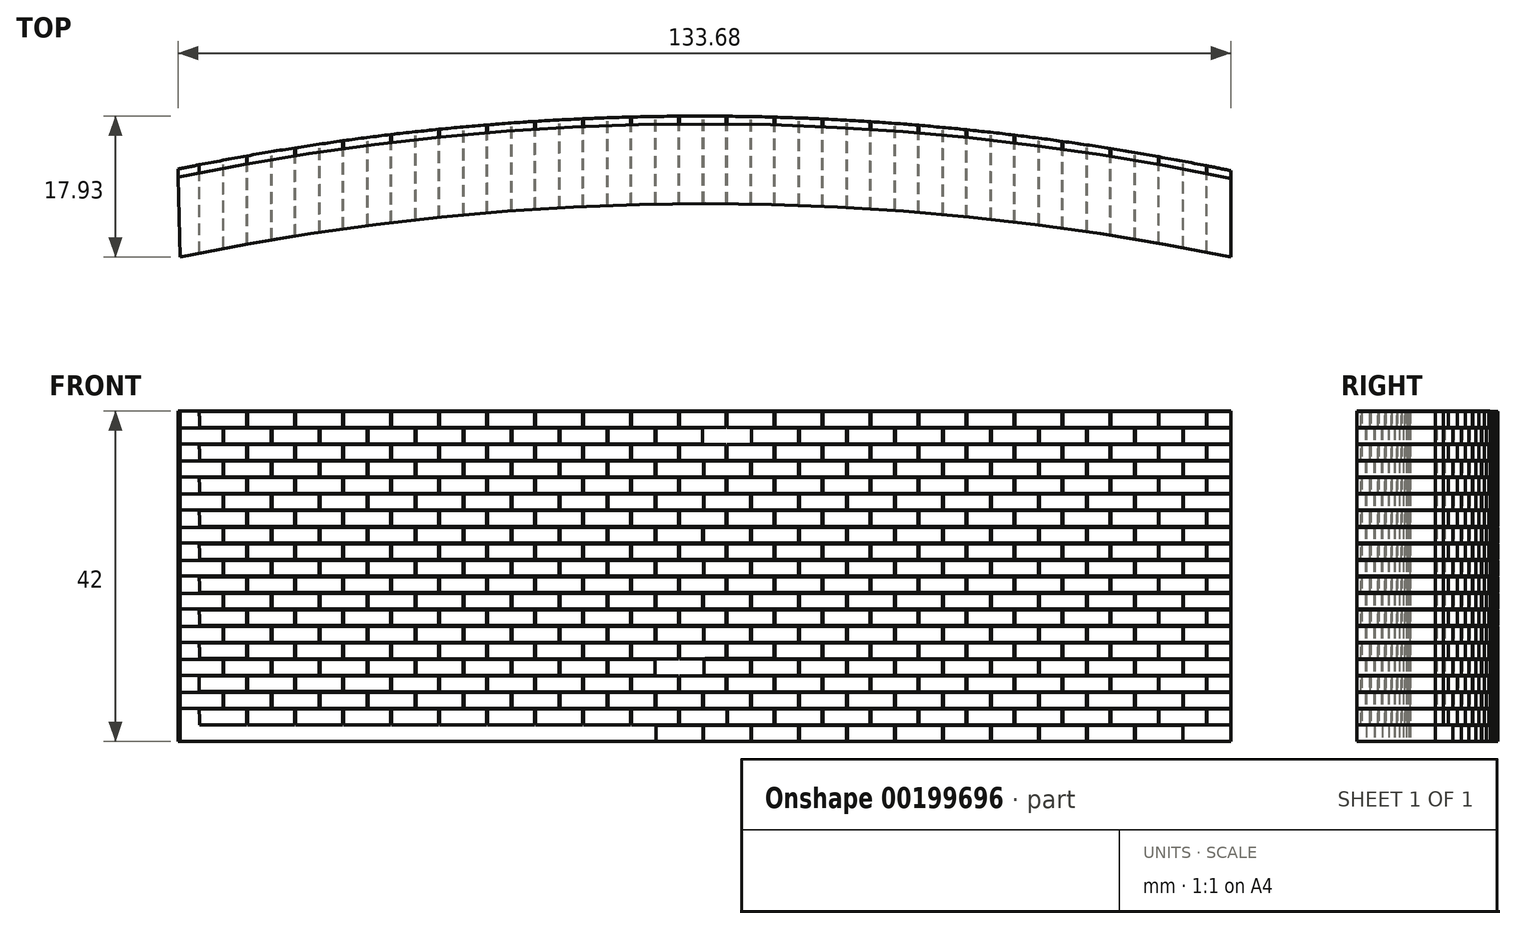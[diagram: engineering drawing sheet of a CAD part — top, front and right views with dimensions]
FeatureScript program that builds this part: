
annotation { "Feature Type Name" : "Feature", "Feature Type Description" : "" }
export const myFeature = defineFeature(function(context is Context, id is Id, definition is map)
    precondition{}
    {
        {
            var Q0;
            Q0=qCreatedBy(makeId("Front.planeOp"),FACE);
            var sketch = newSketch(context, id + "F0", { "sketchPlane" : qUnion([Q0])});
            skLineSegment(sketch, "E0", {"start": v(70.88, 0) * mm, "end": v(70.88, 50) * mm});
            skLineSegment(sketch, "E1", {"start": v(70.88, 0) * mm, "end": v(-68.5, 0) * mm});
            skLineSegment(sketch, "E2", {"start": v(-68.5, 0) * mm, "end": v(-68.5, 50) * mm});
            skLineSegment(sketch, "E3", {"start": v(70.88, 50) * mm, "end": v(-68.5, 50) * mm});
            skLineSegment(sketch, "E4", {"start": v(70.88, 0) * mm, "end": v(70.88, 2) * mm});
            skLineSegment(sketch, "E5", {"start": v(70.88, 2) * mm, "end": v(64.88, 2) * mm});
            skLineSegment(sketch, "E6", {"start": v(64.88, 2) * mm, "end": v(64.88, 0) * mm});
            skLineSegment(sketch, "E7", {"start": v(64.88, 0) * mm, "end": v(70.88, 0) * mm});
            skLineSegment(sketch, "E8", {"start": v(64.88, 0) * mm, "end": v(64.78, 0) * mm});
            skLineSegment(sketch, "E9", {"start": v(64.78, 0) * mm, "end": v(64.78, 2) * mm});
            skLineSegment(sketch, "E10", {"start": v(64.78, 2) * mm, "end": v(58.78, 2) * mm});
            skLineSegment(sketch, "E11", {"start": v(58.78, 2) * mm, "end": v(58.78, 0) * mm});
            skLineSegment(sketch, "E12", {"start": v(58.78, 0) * mm, "end": v(64.78, 0) * mm});
            skLineSegment(sketch, "E13.1.0.0", {"start": v(58.68, 2) * mm, "end": v(52.68, 2) * mm});
            skLineSegment(sketch, "E13.1.0.1", {"start": v(52.68, 2) * mm, "end": v(52.68, 0) * mm});
            skLineSegment(sketch, "E13.1.0.2", {"start": v(52.68, 0) * mm, "end": v(58.68, 0) * mm});
            skLineSegment(sketch, "E13.1.0.3", {"start": v(58.68, 0) * mm, "end": v(58.68, 2) * mm});
            skLineSegment(sketch, "E13.2.0.0", {"start": v(52.58, 2) * mm, "end": v(46.58, 2) * mm});
            skLineSegment(sketch, "E13.2.0.1", {"start": v(46.58, 2) * mm, "end": v(46.58, 0) * mm});
            skLineSegment(sketch, "E13.2.0.2", {"start": v(46.58, 0) * mm, "end": v(52.58, 0) * mm});
            skLineSegment(sketch, "E13.2.0.3", {"start": v(52.58, 0) * mm, "end": v(52.58, 2) * mm});
            skLineSegment(sketch, "E13.3.0.0", {"start": v(46.48, 2) * mm, "end": v(40.48, 2) * mm});
            skLineSegment(sketch, "E13.3.0.1", {"start": v(40.48, 2) * mm, "end": v(40.48, 0) * mm});
            skLineSegment(sketch, "E13.3.0.2", {"start": v(40.48, 0) * mm, "end": v(46.48, 0) * mm});
            skLineSegment(sketch, "E13.3.0.3", {"start": v(46.48, 0) * mm, "end": v(46.48, 2) * mm});
            skLineSegment(sketch, "E13.4.0.0", {"start": v(40.38, 2) * mm, "end": v(34.38, 2) * mm});
            skLineSegment(sketch, "E13.4.0.1", {"start": v(34.38, 2) * mm, "end": v(34.38, 0) * mm});
            skLineSegment(sketch, "E13.4.0.2", {"start": v(34.38, 0) * mm, "end": v(40.38, 0) * mm});
            skLineSegment(sketch, "E13.4.0.3", {"start": v(40.38, 0) * mm, "end": v(40.38, 2) * mm});
            skLineSegment(sketch, "E13.5.0.0", {"start": v(34.28, 2) * mm, "end": v(28.28, 2) * mm});
            skLineSegment(sketch, "E13.5.0.1", {"start": v(28.28, 2) * mm, "end": v(28.28, 0) * mm});
            skLineSegment(sketch, "E13.5.0.2", {"start": v(28.28, 0) * mm, "end": v(34.28, 0) * mm});
            skLineSegment(sketch, "E13.5.0.3", {"start": v(34.28, 0) * mm, "end": v(34.28, 2) * mm});
            skLineSegment(sketch, "E13.6.0.0", {"start": v(28.18, 2) * mm, "end": v(22.18, 2) * mm});
            skLineSegment(sketch, "E13.6.0.1", {"start": v(22.18, 2) * mm, "end": v(22.18, 0) * mm});
            skLineSegment(sketch, "E13.6.0.2", {"start": v(22.18, 0) * mm, "end": v(28.18, 0) * mm});
            skLineSegment(sketch, "E13.6.0.3", {"start": v(28.18, 0) * mm, "end": v(28.18, 2) * mm});
            skLineSegment(sketch, "E13.7.0.0", {"start": v(22.08, 2) * mm, "end": v(16.08, 2) * mm});
            skLineSegment(sketch, "E13.7.0.1", {"start": v(16.08, 2) * mm, "end": v(16.08, 0) * mm});
            skLineSegment(sketch, "E13.7.0.2", {"start": v(16.08, 0) * mm, "end": v(22.08, 0) * mm});
            skLineSegment(sketch, "E13.7.0.3", {"start": v(22.08, 0) * mm, "end": v(22.08, 2) * mm});
            skLineSegment(sketch, "E13.8.0.0", {"start": v(15.98, 2) * mm, "end": v(9.98, 2) * mm});
            skLineSegment(sketch, "E13.8.0.1", {"start": v(9.98, 2) * mm, "end": v(9.98, 0) * mm});
            skLineSegment(sketch, "E13.8.0.2", {"start": v(9.98, 0) * mm, "end": v(15.98, 0) * mm});
            skLineSegment(sketch, "E13.8.0.3", {"start": v(15.98, 0) * mm, "end": v(15.98, 2) * mm});
            skLineSegment(sketch, "E13.9.0.3", {"start": v(9.93, 0) * mm, "end": v(9.93, 2) * mm});
            skLineSegment(sketch, "E14", {"start": v(70.88, 2.1) * mm, "end": v(67.86, 2.1) * mm});
            skLineSegment(sketch, "E15", {"start": v(67.86, 2.1) * mm, "end": v(67.86, 4.1) * mm});
            skLineSegment(sketch, "E16", {"start": v(67.86, 4.1) * mm, "end": v(70.88, 4.1) * mm});
            skLineSegment(sketch, "E17", {"start": v(70.88, 4.1) * mm, "end": v(70.88, 2.1) * mm});
            skLineSegment(sketch, "E18", {"start": v(67.86, 2.1) * mm, "end": v(67.76, 2.1) * mm});
            skLineSegment(sketch, "E19", {"start": v(67.76, 2.1) * mm, "end": v(67.76, 4.1) * mm});
            skLineSegment(sketch, "E20", {"start": v(67.76, 4.1) * mm, "end": v(61.76, 4.1) * mm});
            skLineSegment(sketch, "E21", {"start": v(61.76, 4.1) * mm, "end": v(61.78, 2.1) * mm});
            skPoint(sketch, "E21.endSnap0", {"position": v(61.78, 2) * mm});
            skLineSegment(sketch, "E22", {"start": v(67.76, 2.1) * mm, "end": v(61.78, 2.1) * mm});
            skLineSegment(sketch, "E23.1.0.0", {"start": v(61.66, 4.1) * mm, "end": v(55.66, 4.1) * mm});
            skLineSegment(sketch, "E23.1.0.1", {"start": v(55.66, 4.1) * mm, "end": v(55.68, 2.1) * mm});
            skLineSegment(sketch, "E23.1.0.2", {"start": v(61.66, 2.1) * mm, "end": v(55.68, 2.1) * mm});
            skLineSegment(sketch, "E23.1.0.3", {"start": v(61.66, 2.1) * mm, "end": v(61.66, 4.1) * mm});
            skLineSegment(sketch, "E23.2.0.0", {"start": v(55.56, 4.1) * mm, "end": v(49.56, 4.1) * mm});
            skLineSegment(sketch, "E23.2.0.1", {"start": v(49.56, 4.1) * mm, "end": v(49.58, 2.1) * mm});
            skLineSegment(sketch, "E23.2.0.2", {"start": v(55.56, 2.1) * mm, "end": v(49.58, 2.1) * mm});
            skLineSegment(sketch, "E23.2.0.3", {"start": v(55.56, 2.1) * mm, "end": v(55.56, 4.1) * mm});
            skLineSegment(sketch, "E23.3.0.0", {"start": v(49.46, 4.1) * mm, "end": v(43.46, 4.1) * mm});
            skLineSegment(sketch, "E23.3.0.1", {"start": v(43.46, 4.1) * mm, "end": v(43.48, 2.1) * mm});
            skLineSegment(sketch, "E23.3.0.2", {"start": v(49.46, 2.1) * mm, "end": v(43.48, 2.1) * mm});
            skLineSegment(sketch, "E23.3.0.3", {"start": v(49.46, 2.1) * mm, "end": v(49.46, 4.1) * mm});
            skLineSegment(sketch, "E23.4.0.0", {"start": v(43.36, 4.1) * mm, "end": v(37.36, 4.1) * mm});
            skLineSegment(sketch, "E23.4.0.1", {"start": v(37.36, 4.1) * mm, "end": v(37.38, 2.1) * mm});
            skLineSegment(sketch, "E23.4.0.2", {"start": v(43.36, 2.1) * mm, "end": v(37.38, 2.1) * mm});
            skLineSegment(sketch, "E23.4.0.3", {"start": v(43.36, 2.1) * mm, "end": v(43.36, 4.1) * mm});
            skLineSegment(sketch, "E23.5.0.0", {"start": v(37.26, 4.1) * mm, "end": v(31.26, 4.1) * mm});
            skLineSegment(sketch, "E23.5.0.1", {"start": v(31.26, 4.1) * mm, "end": v(31.28, 2.1) * mm});
            skLineSegment(sketch, "E23.5.0.2", {"start": v(37.26, 2.1) * mm, "end": v(31.28, 2.1) * mm});
            skLineSegment(sketch, "E23.5.0.3", {"start": v(37.26, 2.1) * mm, "end": v(37.26, 4.1) * mm});
            skLineSegment(sketch, "E23.6.0.0", {"start": v(31.16, 4.1) * mm, "end": v(25.16, 4.1) * mm});
            skLineSegment(sketch, "E23.6.0.1", {"start": v(25.16, 4.1) * mm, "end": v(25.18, 2.1) * mm});
            skLineSegment(sketch, "E23.6.0.2", {"start": v(31.16, 2.1) * mm, "end": v(25.18, 2.1) * mm});
            skLineSegment(sketch, "E23.6.0.3", {"start": v(31.16, 2.1) * mm, "end": v(31.16, 4.1) * mm});
            skLineSegment(sketch, "E23.7.0.0", {"start": v(25.06, 4.1) * mm, "end": v(19.06, 4.1) * mm});
            skLineSegment(sketch, "E23.7.0.1", {"start": v(19.06, 4.1) * mm, "end": v(19.08, 2.1) * mm});
            skLineSegment(sketch, "E23.7.0.2", {"start": v(25.06, 2.1) * mm, "end": v(19.08, 2.1) * mm});
            skLineSegment(sketch, "E23.7.0.3", {"start": v(25.06, 2.1) * mm, "end": v(25.06, 4.1) * mm});
            skLineSegment(sketch, "E23.8.0.0", {"start": v(18.96, 4.1) * mm, "end": v(12.96, 4.1) * mm});
            skLineSegment(sketch, "E23.8.0.1", {"start": v(12.96, 4.1) * mm, "end": v(12.98, 2.1) * mm});
            skLineSegment(sketch, "E23.8.0.2", {"start": v(18.96, 2.1) * mm, "end": v(12.98, 2.1) * mm});
            skLineSegment(sketch, "E23.8.0.3", {"start": v(18.96, 2.1) * mm, "end": v(18.96, 4.1) * mm});
            skLineSegment(sketch, "E23.9.0.3", {"start": v(12.86, 2.1) * mm, "end": v(12.86, 4.1) * mm});
            skLineSegment(sketch, "E24", {"start": v(70.88, 4.1) * mm, "end": v(70.88, 4.2) * mm});
            skLineSegment(sketch, "E25.0.1.0", {"start": v(31.16, 8.3) * mm, "end": v(25.16, 8.3) * mm});
            skLineSegment(sketch, "E25.0.1.1", {"start": v(55.56, 8.3) * mm, "end": v(49.56, 8.3) * mm});
            skLineSegment(sketch, "E25.0.1.2", {"start": v(18.96, 8.3) * mm, "end": v(12.96, 8.3) * mm});
            skLineSegment(sketch, "E25.0.1.3", {"start": v(43.36, 8.3) * mm, "end": v(37.36, 8.3) * mm});
            skLineSegment(sketch, "E25.0.1.4", {"start": v(25.06, 8.3) * mm, "end": v(19.06, 8.3) * mm});
            skLineSegment(sketch, "E25.0.1.5", {"start": v(49.46, 8.3) * mm, "end": v(43.46, 8.3) * mm});
            skLineSegment(sketch, "E25.0.1.6", {"start": v(61.66, 8.3) * mm, "end": v(55.66, 8.3) * mm});
            skLineSegment(sketch, "E25.0.1.7", {"start": v(12.86, 8.3) * mm, "end": v(6.86, 8.3) * mm});
            skLineSegment(sketch, "E25.0.1.8", {"start": v(37.26, 8.3) * mm, "end": v(31.26, 8.3) * mm});
            skLineSegment(sketch, "E25.0.1.9", {"start": v(46.58, 4.2) * mm, "end": v(52.58, 4.2) * mm});
            skLineSegment(sketch, "E25.0.1.10", {"start": v(22.18, 4.2) * mm, "end": v(28.18, 4.2) * mm});
            skLineSegment(sketch, "E25.0.1.11", {"start": v(9.98, 4.2) * mm, "end": v(15.98, 4.2) * mm});
            skLineSegment(sketch, "E25.0.1.12", {"start": v(34.38, 4.2) * mm, "end": v(40.38, 4.2) * mm});
            skLineSegment(sketch, "E25.0.1.13", {"start": v(16.08, 4.2) * mm, "end": v(22.08, 4.2) * mm});
            skLineSegment(sketch, "E25.0.1.14", {"start": v(40.48, 4.2) * mm, "end": v(46.48, 4.2) * mm});
            skPoint(sketch, "E25.0.1.15", {"position": v(61.78, 6.2) * mm});
            skLineSegment(sketch, "E25.0.1.17", {"start": v(28.28, 4.2) * mm, "end": v(34.28, 4.2) * mm});
            skLineSegment(sketch, "E25.0.1.18", {"start": v(52.68, 4.2) * mm, "end": v(58.68, 4.2) * mm});
            skLineSegment(sketch, "E25.0.1.19", {"start": v(64.88, 4.2) * mm, "end": v(70.88, 4.2) * mm});
            skLineSegment(sketch, "E25.0.1.20", {"start": v(67.76, 8.3) * mm, "end": v(61.76, 8.3) * mm});
            skLineSegment(sketch, "E25.0.1.22", {"start": v(58.78, 4.2) * mm, "end": v(64.78, 4.2) * mm});
            skLineSegment(sketch, "E25.0.1.23", {"start": v(43.46, 8.3) * mm, "end": v(43.48, 6.3) * mm});
            skLineSegment(sketch, "E25.0.1.24", {"start": v(6.86, 8.3) * mm, "end": v(6.88, 6.3) * mm});
            skLineSegment(sketch, "E25.0.1.26", {"start": v(12.87, 6.3) * mm, "end": v(6.88, 6.3) * mm});
            skLineSegment(sketch, "E25.0.1.27", {"start": v(46.48, 6.2) * mm, "end": v(40.48, 6.2) * mm});
            skLineSegment(sketch, "E25.0.1.28", {"start": v(15.98, 6.2) * mm, "end": v(9.98, 6.2) * mm});
            skLineSegment(sketch, "E25.0.1.29", {"start": v(43.36, 6.3) * mm, "end": v(43.36, 8.3) * mm});
            skLineSegment(sketch, "E25.0.1.30", {"start": v(9.98, 6.2) * mm, "end": v(9.98, 4.2) * mm});
            skLineSegment(sketch, "E25.0.1.31", {"start": v(9.97, 4.2) * mm, "end": v(9.97, 6.18) * mm});
            skLineSegment(sketch, "E25.0.1.32", {"start": v(49.46, 6.3) * mm, "end": v(43.48, 6.3) * mm});
            skLineSegment(sketch, "E25.0.1.33", {"start": v(40.38, 4.2) * mm, "end": v(40.38, 6.2) * mm});
            skLineSegment(sketch, "E25.0.1.34", {"start": v(18.96, 6.3) * mm, "end": v(12.98, 6.3) * mm});
            skLineSegment(sketch, "E25.0.1.35", {"start": v(43.36, 6.3) * mm, "end": v(37.38, 6.3) * mm});
            skLineSegment(sketch, "E25.0.1.36", {"start": v(49.46, 6.3) * mm, "end": v(49.46, 8.3) * mm});
            skLineSegment(sketch, "E25.0.1.37", {"start": v(22.08, 6.2) * mm, "end": v(16.08, 6.2) * mm});
            skLineSegment(sketch, "E25.0.1.38", {"start": v(52.58, 6.2) * mm, "end": v(46.58, 6.2) * mm});
            skLineSegment(sketch, "E25.0.1.39", {"start": v(40.38, 6.2) * mm, "end": v(34.38, 6.2) * mm});
            skLineSegment(sketch, "E25.0.1.40", {"start": v(18.96, 6.3) * mm, "end": v(18.96, 8.3) * mm});
            skLineSegment(sketch, "E25.0.1.41", {"start": v(40.48, 6.2) * mm, "end": v(40.48, 4.2) * mm});
            skLineSegment(sketch, "E25.0.1.42", {"start": v(25.16, 8.3) * mm, "end": v(25.18, 6.3) * mm});
            skLineSegment(sketch, "E25.0.1.43", {"start": v(49.56, 8.3) * mm, "end": v(49.58, 6.3) * mm});
            skLineSegment(sketch, "E25.0.1.44", {"start": v(16.08, 6.2) * mm, "end": v(16.08, 4.2) * mm});
            skLineSegment(sketch, "E25.0.1.45", {"start": v(58.68, 6.2) * mm, "end": v(52.68, 6.2) * mm});
            skLineSegment(sketch, "E25.0.1.46", {"start": v(46.58, 6.2) * mm, "end": v(46.58, 4.2) * mm});
            skLineSegment(sketch, "E25.0.1.47", {"start": v(22.18, 6.2) * mm, "end": v(22.18, 4.2) * mm});
            skLineSegment(sketch, "E25.0.1.48", {"start": v(64.78, 6.2) * mm, "end": v(58.78, 6.2) * mm});
            skLineSegment(sketch, "E25.0.1.49", {"start": v(34.38, 6.2) * mm, "end": v(34.38, 4.2) * mm});
            skLineSegment(sketch, "E25.0.1.50", {"start": v(19.06, 8.3) * mm, "end": v(19.08, 6.3) * mm});
            skLineSegment(sketch, "E25.0.1.51", {"start": v(31.16, 6.3) * mm, "end": v(25.18, 6.3) * mm});
            skLineSegment(sketch, "E25.0.1.52", {"start": v(55.56, 6.3) * mm, "end": v(49.58, 6.3) * mm});
            skLineSegment(sketch, "E25.0.1.53", {"start": v(34.28, 4.2) * mm, "end": v(34.28, 6.2) * mm});
            skLineSegment(sketch, "E25.0.1.54", {"start": v(55.66, 8.3) * mm, "end": v(55.68, 6.3) * mm});
            skLineSegment(sketch, "E25.0.1.55", {"start": v(31.26, 8.3) * mm, "end": v(31.28, 6.3) * mm});
            skLineSegment(sketch, "E25.0.1.56", {"start": v(52.58, 4.2) * mm, "end": v(52.58, 6.2) * mm});
            skLineSegment(sketch, "E25.0.1.57", {"start": v(37.26, 6.3) * mm, "end": v(37.26, 8.3) * mm});
            skLineSegment(sketch, "E25.0.1.58", {"start": v(25.06, 6.3) * mm, "end": v(19.08, 6.3) * mm});
            skLineSegment(sketch, "E25.0.1.59", {"start": v(34.28, 6.2) * mm, "end": v(28.28, 6.2) * mm});
            skLineSegment(sketch, "E25.0.1.60", {"start": v(28.18, 4.2) * mm, "end": v(28.18, 6.2) * mm});
            skLineSegment(sketch, "E25.0.1.61", {"start": v(12.86, 6.3) * mm, "end": v(12.86, 8.3) * mm});
            skLineSegment(sketch, "E25.0.1.62", {"start": v(58.68, 4.2) * mm, "end": v(58.68, 6.2) * mm});
            skLineSegment(sketch, "E25.0.1.63", {"start": v(12.96, 8.3) * mm, "end": v(12.98, 6.3) * mm});
            skLineSegment(sketch, "E25.0.1.64", {"start": v(37.36, 8.3) * mm, "end": v(37.38, 6.3) * mm});
            skLineSegment(sketch, "E25.0.1.65", {"start": v(61.66, 6.3) * mm, "end": v(55.68, 6.3) * mm});
            skLineSegment(sketch, "E25.0.1.66", {"start": v(15.98, 4.2) * mm, "end": v(15.98, 6.2) * mm});
            skLineSegment(sketch, "E25.0.1.67", {"start": v(37.26, 6.3) * mm, "end": v(31.28, 6.3) * mm});
            skLineSegment(sketch, "E25.0.1.68", {"start": v(22.08, 4.2) * mm, "end": v(22.08, 6.2) * mm});
            skLineSegment(sketch, "E25.0.1.69", {"start": v(46.48, 4.2) * mm, "end": v(46.48, 6.2) * mm});
            skLineSegment(sketch, "E25.0.1.70", {"start": v(25.06, 6.3) * mm, "end": v(25.06, 8.3) * mm});
            skLineSegment(sketch, "E25.0.1.71", {"start": v(28.28, 6.2) * mm, "end": v(28.28, 4.2) * mm});
            skLineSegment(sketch, "E25.0.1.72", {"start": v(31.16, 6.3) * mm, "end": v(31.16, 8.3) * mm});
            skLineSegment(sketch, "E25.0.1.73", {"start": v(55.56, 6.3) * mm, "end": v(55.56, 8.3) * mm});
            skLineSegment(sketch, "E25.0.1.74", {"start": v(28.18, 6.2) * mm, "end": v(22.18, 6.2) * mm});
            skLineSegment(sketch, "E25.0.1.75", {"start": v(52.68, 6.2) * mm, "end": v(52.68, 4.2) * mm});
            skLineSegment(sketch, "E25.0.1.76", {"start": v(70.88, 4.2) * mm, "end": v(70.88, 6.2) * mm});
            skLineSegment(sketch, "E25.0.1.77", {"start": v(70.88, 6.2) * mm, "end": v(64.88, 6.2) * mm});
            skLineSegment(sketch, "E25.0.1.78", {"start": v(64.88, 6.2) * mm, "end": v(64.88, 4.2) * mm});
            skLineSegment(sketch, "E25.0.1.79", {"start": v(64.78, 4.2) * mm, "end": v(64.78, 6.2) * mm});
            skLineSegment(sketch, "E25.0.1.80", {"start": v(58.78, 6.2) * mm, "end": v(58.78, 4.2) * mm});
            skLineSegment(sketch, "E25.0.1.81", {"start": v(67.86, 8.3) * mm, "end": v(70.88, 8.3) * mm});
            skLineSegment(sketch, "E25.0.1.82", {"start": v(70.88, 8.3) * mm, "end": v(70.88, 6.3) * mm});
            skLineSegment(sketch, "E25.0.1.83", {"start": v(70.88, 8.3) * mm, "end": v(70.88, 8.4) * mm});
            skLineSegment(sketch, "E25.0.1.84", {"start": v(70.88, 6.3) * mm, "end": v(67.86, 6.3) * mm});
            skLineSegment(sketch, "E25.0.1.85", {"start": v(67.76, 6.3) * mm, "end": v(61.78, 6.3) * mm});
            skLineSegment(sketch, "E25.0.1.86", {"start": v(67.86, 6.3) * mm, "end": v(67.86, 8.3) * mm});
            skLineSegment(sketch, "E25.0.1.87", {"start": v(61.66, 6.3) * mm, "end": v(61.66, 8.3) * mm});
            skLineSegment(sketch, "E25.0.1.88", {"start": v(61.76, 8.3) * mm, "end": v(61.78, 6.3) * mm});
            skLineSegment(sketch, "E25.0.1.89", {"start": v(67.76, 6.3) * mm, "end": v(67.76, 8.3) * mm});
            skLineSegment(sketch, "E25.0.1.90", {"start": v(64.88, 4.2) * mm, "end": v(64.78, 4.2) * mm});
            skLineSegment(sketch, "E25.0.1.91", {"start": v(67.86, 6.3) * mm, "end": v(67.76, 6.3) * mm});
            skLineSegment(sketch, "E25.0.2.0", {"start": v(31.16, 12.5) * mm, "end": v(25.16, 12.5) * mm});
            skLineSegment(sketch, "E25.0.2.1", {"start": v(55.56, 12.5) * mm, "end": v(49.56, 12.5) * mm});
            skLineSegment(sketch, "E25.0.2.2", {"start": v(18.96, 12.5) * mm, "end": v(12.96, 12.5) * mm});
            skLineSegment(sketch, "E25.0.2.3", {"start": v(43.36, 12.5) * mm, "end": v(37.36, 12.5) * mm});
            skLineSegment(sketch, "E25.0.2.4", {"start": v(25.06, 12.5) * mm, "end": v(19.06, 12.5) * mm});
            skLineSegment(sketch, "E25.0.2.5", {"start": v(49.46, 12.5) * mm, "end": v(43.46, 12.5) * mm});
            skLineSegment(sketch, "E25.0.2.6", {"start": v(61.66, 12.5) * mm, "end": v(55.66, 12.5) * mm});
            skLineSegment(sketch, "E25.0.2.7", {"start": v(12.86, 12.52) * mm, "end": v(6.86, 12.52) * mm});
            skLineSegment(sketch, "E25.0.2.8", {"start": v(37.26, 12.5) * mm, "end": v(31.26, 12.5) * mm});
            skLineSegment(sketch, "E25.0.2.9", {"start": v(46.58, 8.4) * mm, "end": v(52.58, 8.4) * mm});
            skLineSegment(sketch, "E25.0.2.10", {"start": v(22.18, 8.4) * mm, "end": v(28.18, 8.4) * mm});
            skLineSegment(sketch, "E25.0.2.11", {"start": v(9.98, 8.4) * mm, "end": v(15.98, 8.4) * mm});
            skLineSegment(sketch, "E25.0.2.12", {"start": v(34.38, 8.4) * mm, "end": v(40.38, 8.4) * mm});
            skLineSegment(sketch, "E25.0.2.13", {"start": v(16.08, 8.4) * mm, "end": v(22.08, 8.4) * mm});
            skLineSegment(sketch, "E25.0.2.14", {"start": v(40.48, 8.4) * mm, "end": v(46.48, 8.4) * mm});
            skPoint(sketch, "E25.0.2.15", {"position": v(61.78, 10.4) * mm});
            skLineSegment(sketch, "E25.0.2.17", {"start": v(28.28, 8.4) * mm, "end": v(34.28, 8.4) * mm});
            skLineSegment(sketch, "E25.0.2.18", {"start": v(52.68, 8.4) * mm, "end": v(58.68, 8.4) * mm});
            skLineSegment(sketch, "E25.0.2.19", {"start": v(64.88, 8.4) * mm, "end": v(70.88, 8.4) * mm});
            skLineSegment(sketch, "E25.0.2.20", {"start": v(67.76, 12.5) * mm, "end": v(61.76, 12.5) * mm});
            skLineSegment(sketch, "E25.0.2.22", {"start": v(58.78, 8.4) * mm, "end": v(64.78, 8.4) * mm});
            skLineSegment(sketch, "E25.0.2.23", {"start": v(43.46, 12.5) * mm, "end": v(43.48, 10.5) * mm});
            skLineSegment(sketch, "E25.0.2.24", {"start": v(6.86, 12.52) * mm, "end": v(6.88, 10.52) * mm});
            skLineSegment(sketch, "E25.0.2.26", {"start": v(12.86, 10.52) * mm, "end": v(6.88, 10.52) * mm});
            skLineSegment(sketch, "E25.0.2.27", {"start": v(46.48, 10.4) * mm, "end": v(40.48, 10.4) * mm});
            skLineSegment(sketch, "E25.0.2.28", {"start": v(15.98, 10.4) * mm, "end": v(9.98, 10.4) * mm});
            skLineSegment(sketch, "E25.0.2.29", {"start": v(43.36, 10.5) * mm, "end": v(43.36, 12.5) * mm});
            skLineSegment(sketch, "E25.0.2.30", {"start": v(9.98, 10.4) * mm, "end": v(9.98, 8.4) * mm});
            skLineSegment(sketch, "E25.0.2.31", {"start": v(9.88, 8.4) * mm, "end": v(9.88, 10.4) * mm});
            skLineSegment(sketch, "E25.0.2.32", {"start": v(49.46, 10.5) * mm, "end": v(43.48, 10.5) * mm});
            skLineSegment(sketch, "E25.0.2.33", {"start": v(40.38, 8.4) * mm, "end": v(40.38, 10.4) * mm});
            skLineSegment(sketch, "E25.0.2.34", {"start": v(18.96, 10.5) * mm, "end": v(12.98, 10.5) * mm});
            skLineSegment(sketch, "E25.0.2.35", {"start": v(43.36, 10.5) * mm, "end": v(37.38, 10.5) * mm});
            skLineSegment(sketch, "E25.0.2.36", {"start": v(49.46, 10.5) * mm, "end": v(49.46, 12.5) * mm});
            skLineSegment(sketch, "E25.0.2.37", {"start": v(22.08, 10.4) * mm, "end": v(16.08, 10.4) * mm});
            skLineSegment(sketch, "E25.0.2.38", {"start": v(52.58, 10.4) * mm, "end": v(46.58, 10.4) * mm});
            skLineSegment(sketch, "E25.0.2.39", {"start": v(40.38, 10.4) * mm, "end": v(34.38, 10.4) * mm});
            skLineSegment(sketch, "E25.0.2.40", {"start": v(18.96, 10.5) * mm, "end": v(18.96, 12.5) * mm});
            skLineSegment(sketch, "E25.0.2.41", {"start": v(40.48, 10.4) * mm, "end": v(40.48, 8.4) * mm});
            skLineSegment(sketch, "E25.0.2.42", {"start": v(25.16, 12.5) * mm, "end": v(25.18, 10.5) * mm});
            skLineSegment(sketch, "E25.0.2.43", {"start": v(49.56, 12.5) * mm, "end": v(49.58, 10.5) * mm});
            skLineSegment(sketch, "E25.0.2.44", {"start": v(16.08, 10.4) * mm, "end": v(16.08, 8.4) * mm});
            skLineSegment(sketch, "E25.0.2.45", {"start": v(58.68, 10.4) * mm, "end": v(52.68, 10.4) * mm});
            skLineSegment(sketch, "E25.0.2.46", {"start": v(46.58, 10.4) * mm, "end": v(46.58, 8.4) * mm});
            skLineSegment(sketch, "E25.0.2.47", {"start": v(22.18, 10.4) * mm, "end": v(22.18, 8.4) * mm});
            skLineSegment(sketch, "E25.0.2.48", {"start": v(64.78, 10.4) * mm, "end": v(58.78, 10.4) * mm});
            skLineSegment(sketch, "E25.0.2.49", {"start": v(34.38, 10.4) * mm, "end": v(34.38, 8.4) * mm});
            skLineSegment(sketch, "E25.0.2.50", {"start": v(19.06, 12.5) * mm, "end": v(19.08, 10.5) * mm});
            skLineSegment(sketch, "E25.0.2.51", {"start": v(31.16, 10.5) * mm, "end": v(25.18, 10.5) * mm});
            skLineSegment(sketch, "E25.0.2.52", {"start": v(55.56, 10.5) * mm, "end": v(49.58, 10.5) * mm});
            skLineSegment(sketch, "E25.0.2.53", {"start": v(34.28, 8.4) * mm, "end": v(34.28, 10.4) * mm});
            skLineSegment(sketch, "E25.0.2.54", {"start": v(55.66, 12.5) * mm, "end": v(55.68, 10.5) * mm});
            skLineSegment(sketch, "E25.0.2.55", {"start": v(31.26, 12.5) * mm, "end": v(31.28, 10.5) * mm});
            skLineSegment(sketch, "E25.0.2.56", {"start": v(52.58, 8.4) * mm, "end": v(52.58, 10.4) * mm});
            skLineSegment(sketch, "E25.0.2.57", {"start": v(37.26, 10.5) * mm, "end": v(37.26, 12.5) * mm});
            skLineSegment(sketch, "E25.0.2.58", {"start": v(25.06, 10.5) * mm, "end": v(19.08, 10.5) * mm});
            skLineSegment(sketch, "E25.0.2.59", {"start": v(34.28, 10.4) * mm, "end": v(28.28, 10.4) * mm});
            skLineSegment(sketch, "E25.0.2.60", {"start": v(28.18, 8.4) * mm, "end": v(28.18, 10.4) * mm});
            skLineSegment(sketch, "E25.0.2.61", {"start": v(12.86, 10.52) * mm, "end": v(12.86, 12.52) * mm});
            skLineSegment(sketch, "E25.0.2.62", {"start": v(58.68, 8.4) * mm, "end": v(58.68, 10.4) * mm});
            skLineSegment(sketch, "E25.0.2.63", {"start": v(12.96, 12.5) * mm, "end": v(12.98, 10.5) * mm});
            skLineSegment(sketch, "E25.0.2.64", {"start": v(37.36, 12.5) * mm, "end": v(37.38, 10.5) * mm});
            skLineSegment(sketch, "E25.0.2.65", {"start": v(61.66, 10.5) * mm, "end": v(55.68, 10.5) * mm});
            skLineSegment(sketch, "E25.0.2.66", {"start": v(15.98, 8.4) * mm, "end": v(15.98, 10.4) * mm});
            skLineSegment(sketch, "E25.0.2.67", {"start": v(37.26, 10.5) * mm, "end": v(31.28, 10.5) * mm});
            skLineSegment(sketch, "E25.0.2.68", {"start": v(22.08, 8.4) * mm, "end": v(22.08, 10.4) * mm});
            skLineSegment(sketch, "E25.0.2.69", {"start": v(46.48, 8.4) * mm, "end": v(46.48, 10.4) * mm});
            skLineSegment(sketch, "E25.0.2.70", {"start": v(25.06, 10.5) * mm, "end": v(25.06, 12.5) * mm});
            skLineSegment(sketch, "E25.0.2.71", {"start": v(28.28, 10.4) * mm, "end": v(28.28, 8.4) * mm});
            skLineSegment(sketch, "E25.0.2.72", {"start": v(31.16, 10.5) * mm, "end": v(31.16, 12.5) * mm});
            skLineSegment(sketch, "E25.0.2.73", {"start": v(55.56, 10.5) * mm, "end": v(55.56, 12.5) * mm});
            skLineSegment(sketch, "E25.0.2.74", {"start": v(28.18, 10.4) * mm, "end": v(22.18, 10.4) * mm});
            skLineSegment(sketch, "E25.0.2.75", {"start": v(52.68, 10.4) * mm, "end": v(52.68, 8.4) * mm});
            skLineSegment(sketch, "E25.0.2.76", {"start": v(70.88, 8.4) * mm, "end": v(70.88, 10.4) * mm});
            skLineSegment(sketch, "E25.0.2.77", {"start": v(70.88, 10.4) * mm, "end": v(64.88, 10.4) * mm});
            skLineSegment(sketch, "E25.0.2.78", {"start": v(64.88, 10.4) * mm, "end": v(64.88, 8.4) * mm});
            skLineSegment(sketch, "E25.0.2.79", {"start": v(64.78, 8.4) * mm, "end": v(64.78, 10.4) * mm});
            skLineSegment(sketch, "E25.0.2.80", {"start": v(58.78, 10.4) * mm, "end": v(58.78, 8.4) * mm});
            skLineSegment(sketch, "E25.0.2.81", {"start": v(67.86, 12.5) * mm, "end": v(70.88, 12.5) * mm});
            skLineSegment(sketch, "E25.0.2.82", {"start": v(70.88, 12.5) * mm, "end": v(70.88, 10.5) * mm});
            skLineSegment(sketch, "E25.0.2.83", {"start": v(70.88, 12.5) * mm, "end": v(70.88, 12.6) * mm});
            skLineSegment(sketch, "E25.0.2.84", {"start": v(70.88, 10.5) * mm, "end": v(67.86, 10.5) * mm});
            skLineSegment(sketch, "E25.0.2.85", {"start": v(67.76, 10.5) * mm, "end": v(61.78, 10.5) * mm});
            skLineSegment(sketch, "E25.0.2.86", {"start": v(67.86, 10.5) * mm, "end": v(67.86, 12.5) * mm});
            skLineSegment(sketch, "E25.0.2.87", {"start": v(61.66, 10.5) * mm, "end": v(61.66, 12.5) * mm});
            skLineSegment(sketch, "E25.0.2.88", {"start": v(61.76, 12.5) * mm, "end": v(61.78, 10.5) * mm});
            skLineSegment(sketch, "E25.0.2.89", {"start": v(67.76, 10.5) * mm, "end": v(67.76, 12.5) * mm});
            skLineSegment(sketch, "E25.0.2.90", {"start": v(64.88, 8.4) * mm, "end": v(64.78, 8.4) * mm});
            skLineSegment(sketch, "E25.0.2.91", {"start": v(67.86, 10.5) * mm, "end": v(67.76, 10.5) * mm});
            skLineSegment(sketch, "E25.0.3.0", {"start": v(31.16, 16.7) * mm, "end": v(25.16, 16.7) * mm});
            skLineSegment(sketch, "E25.0.3.1", {"start": v(55.56, 16.7) * mm, "end": v(49.56, 16.7) * mm});
            skLineSegment(sketch, "E25.0.3.2", {"start": v(18.96, 16.7) * mm, "end": v(12.96, 16.7) * mm});
            skLineSegment(sketch, "E25.0.3.3", {"start": v(43.36, 16.7) * mm, "end": v(37.36, 16.7) * mm});
            skLineSegment(sketch, "E25.0.3.4", {"start": v(25.06, 16.7) * mm, "end": v(19.06, 16.7) * mm});
            skLineSegment(sketch, "E25.0.3.5", {"start": v(49.46, 16.7) * mm, "end": v(43.46, 16.7) * mm});
            skLineSegment(sketch, "E25.0.3.6", {"start": v(61.66, 16.7) * mm, "end": v(55.66, 16.7) * mm});
            skLineSegment(sketch, "E25.0.3.7", {"start": v(12.86, 16.7) * mm, "end": v(6.86, 16.7) * mm});
            skLineSegment(sketch, "E25.0.3.8", {"start": v(37.26, 16.7) * mm, "end": v(31.26, 16.7) * mm});
            skLineSegment(sketch, "E25.0.3.9", {"start": v(46.58, 12.6) * mm, "end": v(52.58, 12.6) * mm});
            skLineSegment(sketch, "E25.0.3.10", {"start": v(22.18, 12.6) * mm, "end": v(28.18, 12.6) * mm});
            skLineSegment(sketch, "E25.0.3.11", {"start": v(9.98, 12.6) * mm, "end": v(15.98, 12.6) * mm});
            skLineSegment(sketch, "E25.0.3.12", {"start": v(34.38, 12.6) * mm, "end": v(40.38, 12.6) * mm});
            skLineSegment(sketch, "E25.0.3.13", {"start": v(16.08, 12.6) * mm, "end": v(22.08, 12.6) * mm});
            skLineSegment(sketch, "E25.0.3.14", {"start": v(40.48, 12.6) * mm, "end": v(46.48, 12.6) * mm});
            skPoint(sketch, "E25.0.3.15", {"position": v(61.78, 14.6) * mm});
            skLineSegment(sketch, "E25.0.3.17", {"start": v(28.28, 12.6) * mm, "end": v(34.28, 12.6) * mm});
            skLineSegment(sketch, "E25.0.3.18", {"start": v(52.68, 12.6) * mm, "end": v(58.68, 12.6) * mm});
            skLineSegment(sketch, "E25.0.3.19", {"start": v(64.88, 12.6) * mm, "end": v(70.88, 12.6) * mm});
            skLineSegment(sketch, "E25.0.3.20", {"start": v(67.76, 16.7) * mm, "end": v(61.76, 16.7) * mm});
            skLineSegment(sketch, "E25.0.3.22", {"start": v(58.78, 12.6) * mm, "end": v(64.78, 12.6) * mm});
            skLineSegment(sketch, "E25.0.3.23", {"start": v(43.46, 16.7) * mm, "end": v(43.48, 14.7) * mm});
            skLineSegment(sketch, "E25.0.3.24", {"start": v(6.86, 16.7) * mm, "end": v(6.88, 14.7) * mm});
            skLineSegment(sketch, "E25.0.3.26", {"start": v(12.86, 14.7) * mm, "end": v(6.88, 14.7) * mm});
            skLineSegment(sketch, "E25.0.3.27", {"start": v(46.48, 14.6) * mm, "end": v(40.48, 14.6) * mm});
            skLineSegment(sketch, "E25.0.3.28", {"start": v(15.98, 14.6) * mm, "end": v(9.98, 14.6) * mm});
            skLineSegment(sketch, "E25.0.3.29", {"start": v(43.36, 14.7) * mm, "end": v(43.36, 16.7) * mm});
            skLineSegment(sketch, "E25.0.3.30", {"start": v(9.98, 14.6) * mm, "end": v(9.98, 12.6) * mm});
            skLineSegment(sketch, "E25.0.3.31", {"start": v(9.88, 12.6) * mm, "end": v(9.88, 14.6) * mm});
            skLineSegment(sketch, "E25.0.3.32", {"start": v(49.46, 14.7) * mm, "end": v(43.48, 14.7) * mm});
            skLineSegment(sketch, "E25.0.3.33", {"start": v(40.38, 12.6) * mm, "end": v(40.38, 14.6) * mm});
            skLineSegment(sketch, "E25.0.3.34", {"start": v(18.96, 14.7) * mm, "end": v(12.98, 14.7) * mm});
            skLineSegment(sketch, "E25.0.3.35", {"start": v(43.36, 14.7) * mm, "end": v(37.38, 14.7) * mm});
            skLineSegment(sketch, "E25.0.3.36", {"start": v(49.46, 14.7) * mm, "end": v(49.46, 16.7) * mm});
            skLineSegment(sketch, "E25.0.3.37", {"start": v(22.08, 14.6) * mm, "end": v(16.08, 14.6) * mm});
            skLineSegment(sketch, "E25.0.3.38", {"start": v(52.58, 14.6) * mm, "end": v(46.58, 14.6) * mm});
            skLineSegment(sketch, "E25.0.3.39", {"start": v(40.38, 14.6) * mm, "end": v(34.38, 14.6) * mm});
            skLineSegment(sketch, "E25.0.3.40", {"start": v(18.96, 14.7) * mm, "end": v(18.96, 16.7) * mm});
            skLineSegment(sketch, "E25.0.3.41", {"start": v(40.48, 14.6) * mm, "end": v(40.48, 12.6) * mm});
            skLineSegment(sketch, "E25.0.3.42", {"start": v(25.16, 16.7) * mm, "end": v(25.18, 14.7) * mm});
            skLineSegment(sketch, "E25.0.3.43", {"start": v(49.56, 16.7) * mm, "end": v(49.58, 14.7) * mm});
            skLineSegment(sketch, "E25.0.3.44", {"start": v(16.08, 14.6) * mm, "end": v(16.08, 12.6) * mm});
            skLineSegment(sketch, "E25.0.3.45", {"start": v(58.68, 14.6) * mm, "end": v(52.68, 14.6) * mm});
            skLineSegment(sketch, "E25.0.3.46", {"start": v(46.58, 14.6) * mm, "end": v(46.58, 12.6) * mm});
            skLineSegment(sketch, "E25.0.3.47", {"start": v(22.18, 14.6) * mm, "end": v(22.18, 12.6) * mm});
            skLineSegment(sketch, "E25.0.3.48", {"start": v(64.78, 14.6) * mm, "end": v(58.78, 14.6) * mm});
            skLineSegment(sketch, "E25.0.3.49", {"start": v(34.38, 14.6) * mm, "end": v(34.38, 12.6) * mm});
            skLineSegment(sketch, "E25.0.3.50", {"start": v(19.06, 16.7) * mm, "end": v(19.08, 14.7) * mm});
            skLineSegment(sketch, "E25.0.3.51", {"start": v(31.16, 14.7) * mm, "end": v(25.18, 14.7) * mm});
            skLineSegment(sketch, "E25.0.3.52", {"start": v(55.56, 14.7) * mm, "end": v(49.58, 14.7) * mm});
            skLineSegment(sketch, "E25.0.3.53", {"start": v(34.28, 12.6) * mm, "end": v(34.28, 14.6) * mm});
            skLineSegment(sketch, "E25.0.3.54", {"start": v(55.66, 16.7) * mm, "end": v(55.68, 14.7) * mm});
            skLineSegment(sketch, "E25.0.3.55", {"start": v(31.26, 16.7) * mm, "end": v(31.28, 14.7) * mm});
            skLineSegment(sketch, "E25.0.3.56", {"start": v(52.58, 12.6) * mm, "end": v(52.58, 14.6) * mm});
            skLineSegment(sketch, "E25.0.3.57", {"start": v(37.26, 14.7) * mm, "end": v(37.26, 16.7) * mm});
            skLineSegment(sketch, "E25.0.3.58", {"start": v(25.06, 14.7) * mm, "end": v(19.08, 14.7) * mm});
            skLineSegment(sketch, "E25.0.3.59", {"start": v(34.28, 14.6) * mm, "end": v(28.28, 14.6) * mm});
            skLineSegment(sketch, "E25.0.3.60", {"start": v(28.18, 12.6) * mm, "end": v(28.18, 14.6) * mm});
            skLineSegment(sketch, "E25.0.3.61", {"start": v(12.86, 14.7) * mm, "end": v(12.86, 16.7) * mm});
            skLineSegment(sketch, "E25.0.3.62", {"start": v(58.68, 12.6) * mm, "end": v(58.68, 14.6) * mm});
            skLineSegment(sketch, "E25.0.3.63", {"start": v(12.96, 16.7) * mm, "end": v(12.98, 14.7) * mm});
            skLineSegment(sketch, "E25.0.3.64", {"start": v(37.36, 16.7) * mm, "end": v(37.38, 14.7) * mm});
            skLineSegment(sketch, "E25.0.3.65", {"start": v(61.66, 14.7) * mm, "end": v(55.68, 14.7) * mm});
            skLineSegment(sketch, "E25.0.3.66", {"start": v(15.98, 12.6) * mm, "end": v(15.98, 14.6) * mm});
            skLineSegment(sketch, "E25.0.3.67", {"start": v(37.26, 14.7) * mm, "end": v(31.28, 14.7) * mm});
            skLineSegment(sketch, "E25.0.3.68", {"start": v(22.08, 12.6) * mm, "end": v(22.08, 14.6) * mm});
            skLineSegment(sketch, "E25.0.3.69", {"start": v(46.48, 12.6) * mm, "end": v(46.48, 14.6) * mm});
            skLineSegment(sketch, "E25.0.3.70", {"start": v(25.06, 14.7) * mm, "end": v(25.06, 16.7) * mm});
            skLineSegment(sketch, "E25.0.3.71", {"start": v(28.28, 14.6) * mm, "end": v(28.28, 12.6) * mm});
            skLineSegment(sketch, "E25.0.3.72", {"start": v(31.16, 14.7) * mm, "end": v(31.16, 16.7) * mm});
            skLineSegment(sketch, "E25.0.3.73", {"start": v(55.56, 14.7) * mm, "end": v(55.56, 16.7) * mm});
            skLineSegment(sketch, "E25.0.3.74", {"start": v(28.18, 14.6) * mm, "end": v(22.18, 14.6) * mm});
            skLineSegment(sketch, "E25.0.3.75", {"start": v(52.68, 14.6) * mm, "end": v(52.68, 12.6) * mm});
            skLineSegment(sketch, "E25.0.3.76", {"start": v(70.88, 12.6) * mm, "end": v(70.88, 14.6) * mm});
            skLineSegment(sketch, "E25.0.3.77", {"start": v(70.88, 14.6) * mm, "end": v(64.88, 14.6) * mm});
            skLineSegment(sketch, "E25.0.3.78", {"start": v(64.88, 14.6) * mm, "end": v(64.88, 12.6) * mm});
            skLineSegment(sketch, "E25.0.3.79", {"start": v(64.78, 12.6) * mm, "end": v(64.78, 14.6) * mm});
            skLineSegment(sketch, "E25.0.3.80", {"start": v(58.78, 14.6) * mm, "end": v(58.78, 12.6) * mm});
            skLineSegment(sketch, "E25.0.3.81", {"start": v(67.86, 16.7) * mm, "end": v(70.88, 16.7) * mm});
            skLineSegment(sketch, "E25.0.3.82", {"start": v(70.88, 16.7) * mm, "end": v(70.88, 14.7) * mm});
            skLineSegment(sketch, "E25.0.3.83", {"start": v(70.88, 16.7) * mm, "end": v(70.88, 16.8) * mm});
            skLineSegment(sketch, "E25.0.3.84", {"start": v(70.88, 14.7) * mm, "end": v(67.86, 14.7) * mm});
            skLineSegment(sketch, "E25.0.3.85", {"start": v(67.76, 14.7) * mm, "end": v(61.78, 14.7) * mm});
            skLineSegment(sketch, "E25.0.3.86", {"start": v(67.86, 14.7) * mm, "end": v(67.86, 16.7) * mm});
            skLineSegment(sketch, "E25.0.3.87", {"start": v(61.66, 14.7) * mm, "end": v(61.66, 16.7) * mm});
            skLineSegment(sketch, "E25.0.3.88", {"start": v(61.76, 16.7) * mm, "end": v(61.78, 14.7) * mm});
            skLineSegment(sketch, "E25.0.3.89", {"start": v(67.76, 14.7) * mm, "end": v(67.76, 16.7) * mm});
            skLineSegment(sketch, "E25.0.3.90", {"start": v(64.88, 12.6) * mm, "end": v(64.78, 12.6) * mm});
            skLineSegment(sketch, "E25.0.3.91", {"start": v(67.86, 14.7) * mm, "end": v(67.76, 14.7) * mm});
            skLineSegment(sketch, "E25.0.4.0", {"start": v(31.16, 20.9) * mm, "end": v(25.16, 20.9) * mm});
            skLineSegment(sketch, "E25.0.4.1", {"start": v(55.56, 20.9) * mm, "end": v(49.56, 20.9) * mm});
            skLineSegment(sketch, "E25.0.4.2", {"start": v(18.96, 20.9) * mm, "end": v(12.96, 20.9) * mm});
            skLineSegment(sketch, "E25.0.4.3", {"start": v(43.36, 20.9) * mm, "end": v(37.36, 20.9) * mm});
            skLineSegment(sketch, "E25.0.4.4", {"start": v(25.06, 20.9) * mm, "end": v(19.06, 20.9) * mm});
            skLineSegment(sketch, "E25.0.4.5", {"start": v(49.46, 20.9) * mm, "end": v(43.46, 20.9) * mm});
            skLineSegment(sketch, "E25.0.4.6", {"start": v(61.66, 20.9) * mm, "end": v(55.66, 20.9) * mm});
            skLineSegment(sketch, "E25.0.4.7", {"start": v(12.86, 20.9) * mm, "end": v(6.86, 20.9) * mm});
            skLineSegment(sketch, "E25.0.4.8", {"start": v(37.26, 20.9) * mm, "end": v(31.26, 20.9) * mm});
            skLineSegment(sketch, "E25.0.4.9", {"start": v(46.58, 16.8) * mm, "end": v(52.58, 16.8) * mm});
            skLineSegment(sketch, "E25.0.4.10", {"start": v(22.18, 16.8) * mm, "end": v(28.18, 16.8) * mm});
            skLineSegment(sketch, "E25.0.4.11", {"start": v(9.98, 16.8) * mm, "end": v(15.98, 16.8) * mm});
            skLineSegment(sketch, "E25.0.4.12", {"start": v(34.38, 16.8) * mm, "end": v(40.38, 16.8) * mm});
            skLineSegment(sketch, "E25.0.4.13", {"start": v(16.08, 16.8) * mm, "end": v(22.08, 16.8) * mm});
            skLineSegment(sketch, "E25.0.4.14", {"start": v(40.48, 16.8) * mm, "end": v(46.48, 16.8) * mm});
            skPoint(sketch, "E25.0.4.15", {"position": v(61.78, 18.8) * mm});
            skLineSegment(sketch, "E25.0.4.16", {"start": v(3.88, 16.8) * mm, "end": v(9.88, 16.8) * mm});
            skLineSegment(sketch, "E25.0.4.17", {"start": v(28.28, 16.8) * mm, "end": v(34.28, 16.8) * mm});
            skLineSegment(sketch, "E25.0.4.18", {"start": v(52.68, 16.8) * mm, "end": v(58.68, 16.8) * mm});
            skLineSegment(sketch, "E25.0.4.19", {"start": v(64.88, 16.8) * mm, "end": v(70.88, 16.8) * mm});
            skLineSegment(sketch, "E25.0.4.20", {"start": v(67.76, 20.9) * mm, "end": v(61.76, 20.9) * mm});
            skLineSegment(sketch, "E25.0.4.21", {"start": v(3.88, 18.8) * mm, "end": v(3.88, 16.8) * mm});
            skLineSegment(sketch, "E25.0.4.22", {"start": v(58.78, 16.8) * mm, "end": v(64.78, 16.8) * mm});
            skLineSegment(sketch, "E25.0.4.23", {"start": v(43.46, 20.9) * mm, "end": v(43.48, 18.9) * mm});
            skLineSegment(sketch, "E25.0.4.24", {"start": v(6.86, 20.9) * mm, "end": v(6.88, 18.9) * mm});
            skLineSegment(sketch, "E25.0.4.25", {"start": v(9.88, 18.8) * mm, "end": v(3.88, 18.8) * mm});
            skLineSegment(sketch, "E25.0.4.26", {"start": v(12.86, 18.9) * mm, "end": v(6.88, 18.9) * mm});
            skLineSegment(sketch, "E25.0.4.27", {"start": v(46.48, 18.8) * mm, "end": v(40.48, 18.8) * mm});
            skLineSegment(sketch, "E25.0.4.28", {"start": v(15.98, 18.8) * mm, "end": v(9.98, 18.8) * mm});
            skLineSegment(sketch, "E25.0.4.29", {"start": v(43.36, 18.9) * mm, "end": v(43.36, 20.9) * mm});
            skLineSegment(sketch, "E25.0.4.30", {"start": v(9.98, 18.8) * mm, "end": v(9.98, 16.8) * mm});
            skLineSegment(sketch, "E25.0.4.31", {"start": v(9.88, 16.8) * mm, "end": v(9.88, 18.8) * mm});
            skLineSegment(sketch, "E25.0.4.32", {"start": v(49.46, 18.9) * mm, "end": v(43.48, 18.9) * mm});
            skLineSegment(sketch, "E25.0.4.33", {"start": v(40.38, 16.8) * mm, "end": v(40.38, 18.8) * mm});
            skLineSegment(sketch, "E25.0.4.34", {"start": v(18.96, 18.9) * mm, "end": v(12.98, 18.9) * mm});
            skLineSegment(sketch, "E25.0.4.35", {"start": v(43.36, 18.9) * mm, "end": v(37.38, 18.9) * mm});
            skLineSegment(sketch, "E25.0.4.36", {"start": v(49.46, 18.9) * mm, "end": v(49.46, 20.9) * mm});
            skLineSegment(sketch, "E25.0.4.37", {"start": v(22.08, 18.8) * mm, "end": v(16.08, 18.8) * mm});
            skLineSegment(sketch, "E25.0.4.38", {"start": v(52.58, 18.8) * mm, "end": v(46.58, 18.8) * mm});
            skLineSegment(sketch, "E25.0.4.39", {"start": v(40.38, 18.8) * mm, "end": v(34.38, 18.8) * mm});
            skLineSegment(sketch, "E25.0.4.40", {"start": v(18.96, 18.9) * mm, "end": v(18.96, 20.9) * mm});
            skLineSegment(sketch, "E25.0.4.41", {"start": v(40.48, 18.8) * mm, "end": v(40.48, 16.8) * mm});
            skLineSegment(sketch, "E25.0.4.42", {"start": v(25.16, 20.9) * mm, "end": v(25.18, 18.9) * mm});
            skLineSegment(sketch, "E25.0.4.43", {"start": v(49.56, 20.9) * mm, "end": v(49.58, 18.9) * mm});
            skLineSegment(sketch, "E25.0.4.44", {"start": v(16.08, 18.8) * mm, "end": v(16.08, 16.8) * mm});
            skLineSegment(sketch, "E25.0.4.45", {"start": v(58.68, 18.8) * mm, "end": v(52.68, 18.8) * mm});
            skLineSegment(sketch, "E25.0.4.46", {"start": v(46.58, 18.8) * mm, "end": v(46.58, 16.8) * mm});
            skLineSegment(sketch, "E25.0.4.47", {"start": v(22.18, 18.8) * mm, "end": v(22.18, 16.8) * mm});
            skLineSegment(sketch, "E25.0.4.48", {"start": v(64.78, 18.8) * mm, "end": v(58.78, 18.8) * mm});
            skLineSegment(sketch, "E25.0.4.49", {"start": v(34.38, 18.8) * mm, "end": v(34.38, 16.8) * mm});
            skLineSegment(sketch, "E25.0.4.50", {"start": v(19.06, 20.9) * mm, "end": v(19.08, 18.9) * mm});
            skLineSegment(sketch, "E25.0.4.51", {"start": v(31.16, 18.9) * mm, "end": v(25.18, 18.9) * mm});
            skLineSegment(sketch, "E25.0.4.52", {"start": v(55.56, 18.9) * mm, "end": v(49.58, 18.9) * mm});
            skLineSegment(sketch, "E25.0.4.53", {"start": v(34.28, 16.8) * mm, "end": v(34.28, 18.8) * mm});
            skLineSegment(sketch, "E25.0.4.54", {"start": v(55.66, 20.9) * mm, "end": v(55.68, 18.9) * mm});
            skLineSegment(sketch, "E25.0.4.55", {"start": v(31.26, 20.9) * mm, "end": v(31.28, 18.9) * mm});
            skLineSegment(sketch, "E25.0.4.56", {"start": v(52.58, 16.8) * mm, "end": v(52.58, 18.8) * mm});
            skLineSegment(sketch, "E25.0.4.57", {"start": v(37.26, 18.9) * mm, "end": v(37.26, 20.9) * mm});
            skLineSegment(sketch, "E25.0.4.58", {"start": v(25.06, 18.9) * mm, "end": v(19.08, 18.9) * mm});
            skLineSegment(sketch, "E25.0.4.59", {"start": v(34.28, 18.8) * mm, "end": v(28.28, 18.8) * mm});
            skLineSegment(sketch, "E25.0.4.60", {"start": v(28.18, 16.8) * mm, "end": v(28.18, 18.8) * mm});
            skLineSegment(sketch, "E25.0.4.61", {"start": v(12.86, 18.9) * mm, "end": v(12.86, 20.9) * mm});
            skLineSegment(sketch, "E25.0.4.62", {"start": v(58.68, 16.8) * mm, "end": v(58.68, 18.8) * mm});
            skLineSegment(sketch, "E25.0.4.63", {"start": v(12.96, 20.9) * mm, "end": v(12.98, 18.9) * mm});
            skLineSegment(sketch, "E25.0.4.64", {"start": v(37.36, 20.9) * mm, "end": v(37.38, 18.9) * mm});
            skLineSegment(sketch, "E25.0.4.65", {"start": v(61.66, 18.9) * mm, "end": v(55.68, 18.9) * mm});
            skLineSegment(sketch, "E25.0.4.66", {"start": v(15.98, 16.8) * mm, "end": v(15.98, 18.8) * mm});
            skLineSegment(sketch, "E25.0.4.67", {"start": v(37.26, 18.9) * mm, "end": v(31.28, 18.9) * mm});
            skLineSegment(sketch, "E25.0.4.68", {"start": v(22.08, 16.8) * mm, "end": v(22.08, 18.8) * mm});
            skLineSegment(sketch, "E25.0.4.69", {"start": v(46.48, 16.8) * mm, "end": v(46.48, 18.8) * mm});
            skLineSegment(sketch, "E25.0.4.70", {"start": v(25.06, 18.9) * mm, "end": v(25.06, 20.9) * mm});
            skLineSegment(sketch, "E25.0.4.71", {"start": v(28.28, 18.8) * mm, "end": v(28.28, 16.8) * mm});
            skLineSegment(sketch, "E25.0.4.72", {"start": v(31.16, 18.9) * mm, "end": v(31.16, 20.9) * mm});
            skLineSegment(sketch, "E25.0.4.73", {"start": v(55.56, 18.9) * mm, "end": v(55.56, 20.9) * mm});
            skLineSegment(sketch, "E25.0.4.74", {"start": v(28.18, 18.8) * mm, "end": v(22.18, 18.8) * mm});
            skLineSegment(sketch, "E25.0.4.75", {"start": v(52.68, 18.8) * mm, "end": v(52.68, 16.8) * mm});
            skLineSegment(sketch, "E25.0.4.76", {"start": v(70.88, 16.8) * mm, "end": v(70.88, 18.8) * mm});
            skLineSegment(sketch, "E25.0.4.77", {"start": v(70.88, 18.8) * mm, "end": v(64.88, 18.8) * mm});
            skLineSegment(sketch, "E25.0.4.78", {"start": v(64.88, 18.8) * mm, "end": v(64.88, 16.8) * mm});
            skLineSegment(sketch, "E25.0.4.79", {"start": v(64.78, 16.8) * mm, "end": v(64.78, 18.8) * mm});
            skLineSegment(sketch, "E25.0.4.80", {"start": v(58.78, 18.8) * mm, "end": v(58.78, 16.8) * mm});
            skLineSegment(sketch, "E25.0.4.81", {"start": v(67.86, 20.9) * mm, "end": v(70.88, 20.9) * mm});
            skLineSegment(sketch, "E25.0.4.82", {"start": v(70.88, 20.9) * mm, "end": v(70.88, 18.9) * mm});
            skLineSegment(sketch, "E25.0.4.83", {"start": v(70.88, 20.9) * mm, "end": v(70.88, 21) * mm});
            skLineSegment(sketch, "E25.0.4.84", {"start": v(70.88, 18.9) * mm, "end": v(67.86, 18.9) * mm});
            skLineSegment(sketch, "E25.0.4.85", {"start": v(67.76, 18.9) * mm, "end": v(61.78, 18.9) * mm});
            skLineSegment(sketch, "E25.0.4.86", {"start": v(67.86, 18.9) * mm, "end": v(67.86, 20.9) * mm});
            skLineSegment(sketch, "E25.0.4.87", {"start": v(61.66, 18.9) * mm, "end": v(61.66, 20.9) * mm});
            skLineSegment(sketch, "E25.0.4.88", {"start": v(61.76, 20.9) * mm, "end": v(61.78, 18.9) * mm});
            skLineSegment(sketch, "E25.0.4.89", {"start": v(67.76, 18.9) * mm, "end": v(67.76, 20.9) * mm});
            skLineSegment(sketch, "E25.0.4.90", {"start": v(64.88, 16.8) * mm, "end": v(64.78, 16.8) * mm});
            skLineSegment(sketch, "E25.0.4.91", {"start": v(67.86, 18.9) * mm, "end": v(67.76, 18.9) * mm});
            skLineSegment(sketch, "E25.0.5.0", {"start": v(31.16, 25.1) * mm, "end": v(25.16, 25.1) * mm});
            skLineSegment(sketch, "E25.0.5.1", {"start": v(55.56, 25.1) * mm, "end": v(49.56, 25.1) * mm});
            skLineSegment(sketch, "E25.0.5.2", {"start": v(18.96, 25.1) * mm, "end": v(12.96, 25.1) * mm});
            skLineSegment(sketch, "E25.0.5.3", {"start": v(43.36, 25.1) * mm, "end": v(37.36, 25.1) * mm});
            skLineSegment(sketch, "E25.0.5.4", {"start": v(25.06, 25.1) * mm, "end": v(19.06, 25.1) * mm});
            skLineSegment(sketch, "E25.0.5.5", {"start": v(49.46, 25.1) * mm, "end": v(43.46, 25.1) * mm});
            skLineSegment(sketch, "E25.0.5.6", {"start": v(61.66, 25.1) * mm, "end": v(55.66, 25.1) * mm});
            skLineSegment(sketch, "E25.0.5.7", {"start": v(12.86, 25.1) * mm, "end": v(6.86, 25.1) * mm});
            skLineSegment(sketch, "E25.0.5.8", {"start": v(37.26, 25.1) * mm, "end": v(31.26, 25.1) * mm});
            skLineSegment(sketch, "E25.0.5.9", {"start": v(46.58, 21) * mm, "end": v(52.58, 21) * mm});
            skLineSegment(sketch, "E25.0.5.10", {"start": v(22.18, 21) * mm, "end": v(28.18, 21) * mm});
            skLineSegment(sketch, "E25.0.5.11", {"start": v(9.98, 21) * mm, "end": v(15.98, 21) * mm});
            skLineSegment(sketch, "E25.0.5.12", {"start": v(34.38, 21) * mm, "end": v(40.38, 21) * mm});
            skLineSegment(sketch, "E25.0.5.13", {"start": v(16.08, 21) * mm, "end": v(22.08, 21) * mm});
            skLineSegment(sketch, "E25.0.5.14", {"start": v(40.48, 21) * mm, "end": v(46.48, 21) * mm});
            skPoint(sketch, "E25.0.5.15", {"position": v(61.78, 23) * mm});
            skLineSegment(sketch, "E25.0.5.17", {"start": v(28.28, 21) * mm, "end": v(34.28, 21) * mm});
            skLineSegment(sketch, "E25.0.5.18", {"start": v(52.68, 21) * mm, "end": v(58.68, 21) * mm});
            skLineSegment(sketch, "E25.0.5.19", {"start": v(64.88, 21) * mm, "end": v(70.88, 21) * mm});
            skLineSegment(sketch, "E25.0.5.20", {"start": v(67.76, 25.1) * mm, "end": v(61.76, 25.1) * mm});
            skLineSegment(sketch, "E25.0.5.21", {"start": v(3.88, 23) * mm, "end": v(3.88, 21) * mm});
            skLineSegment(sketch, "E25.0.5.22", {"start": v(58.78, 21) * mm, "end": v(64.78, 21) * mm});
            skLineSegment(sketch, "E25.0.5.23", {"start": v(43.46, 25.1) * mm, "end": v(43.48, 23.1) * mm});
            skLineSegment(sketch, "E25.0.5.24", {"start": v(6.86, 25.1) * mm, "end": v(6.88, 23.1) * mm});
            skLineSegment(sketch, "E25.0.5.26", {"start": v(12.86, 23.1) * mm, "end": v(6.88, 23.1) * mm});
            skLineSegment(sketch, "E25.0.5.27", {"start": v(46.48, 23) * mm, "end": v(40.48, 23) * mm});
            skLineSegment(sketch, "E25.0.5.28", {"start": v(15.98, 23) * mm, "end": v(9.98, 23) * mm});
            skLineSegment(sketch, "E25.0.5.29", {"start": v(43.36, 23.1) * mm, "end": v(43.36, 25.1) * mm});
            skLineSegment(sketch, "E25.0.5.30", {"start": v(9.98, 23) * mm, "end": v(9.98, 21) * mm});
            skLineSegment(sketch, "E25.0.5.31", {"start": v(9.88, 21) * mm, "end": v(9.88, 23) * mm});
            skLineSegment(sketch, "E25.0.5.32", {"start": v(49.46, 23.1) * mm, "end": v(43.48, 23.1) * mm});
            skLineSegment(sketch, "E25.0.5.33", {"start": v(40.38, 21) * mm, "end": v(40.38, 23) * mm});
            skLineSegment(sketch, "E25.0.5.34", {"start": v(18.96, 23.1) * mm, "end": v(12.98, 23.1) * mm});
            skLineSegment(sketch, "E25.0.5.35", {"start": v(43.36, 23.1) * mm, "end": v(37.38, 23.1) * mm});
            skLineSegment(sketch, "E25.0.5.36", {"start": v(49.46, 23.1) * mm, "end": v(49.46, 25.1) * mm});
            skLineSegment(sketch, "E25.0.5.37", {"start": v(22.08, 23) * mm, "end": v(16.08, 23) * mm});
            skLineSegment(sketch, "E25.0.5.38", {"start": v(52.58, 23) * mm, "end": v(46.58, 23) * mm});
            skLineSegment(sketch, "E25.0.5.39", {"start": v(40.38, 23) * mm, "end": v(34.38, 23) * mm});
            skLineSegment(sketch, "E25.0.5.40", {"start": v(18.96, 23.1) * mm, "end": v(18.96, 25.1) * mm});
            skLineSegment(sketch, "E25.0.5.41", {"start": v(40.48, 23) * mm, "end": v(40.48, 21) * mm});
            skLineSegment(sketch, "E25.0.5.42", {"start": v(25.16, 25.1) * mm, "end": v(25.18, 23.1) * mm});
            skLineSegment(sketch, "E25.0.5.43", {"start": v(49.56, 25.1) * mm, "end": v(49.58, 23.1) * mm});
            skLineSegment(sketch, "E25.0.5.44", {"start": v(16.08, 23) * mm, "end": v(16.08, 21) * mm});
            skLineSegment(sketch, "E25.0.5.45", {"start": v(58.68, 23) * mm, "end": v(52.68, 23) * mm});
            skLineSegment(sketch, "E25.0.5.46", {"start": v(46.58, 23) * mm, "end": v(46.58, 21) * mm});
            skLineSegment(sketch, "E25.0.5.47", {"start": v(22.18, 23) * mm, "end": v(22.18, 21) * mm});
            skLineSegment(sketch, "E25.0.5.48", {"start": v(64.78, 23) * mm, "end": v(58.78, 23) * mm});
            skLineSegment(sketch, "E25.0.5.49", {"start": v(34.38, 23) * mm, "end": v(34.38, 21) * mm});
            skLineSegment(sketch, "E25.0.5.50", {"start": v(19.06, 25.1) * mm, "end": v(19.08, 23.1) * mm});
            skLineSegment(sketch, "E25.0.5.51", {"start": v(31.16, 23.1) * mm, "end": v(25.18, 23.1) * mm});
            skLineSegment(sketch, "E25.0.5.52", {"start": v(55.56, 23.1) * mm, "end": v(49.58, 23.1) * mm});
            skLineSegment(sketch, "E25.0.5.53", {"start": v(34.28, 21) * mm, "end": v(34.28, 23) * mm});
            skLineSegment(sketch, "E25.0.5.54", {"start": v(55.66, 25.1) * mm, "end": v(55.68, 23.1) * mm});
            skLineSegment(sketch, "E25.0.5.55", {"start": v(31.26, 25.1) * mm, "end": v(31.28, 23.1) * mm});
            skLineSegment(sketch, "E25.0.5.56", {"start": v(52.58, 21) * mm, "end": v(52.58, 23) * mm});
            skLineSegment(sketch, "E25.0.5.57", {"start": v(37.26, 23.1) * mm, "end": v(37.26, 25.1) * mm});
            skLineSegment(sketch, "E25.0.5.58", {"start": v(25.06, 23.1) * mm, "end": v(19.08, 23.1) * mm});
            skLineSegment(sketch, "E25.0.5.59", {"start": v(34.28, 23) * mm, "end": v(28.28, 23) * mm});
            skLineSegment(sketch, "E25.0.5.60", {"start": v(28.18, 21) * mm, "end": v(28.18, 23) * mm});
            skLineSegment(sketch, "E25.0.5.61", {"start": v(12.86, 23.1) * mm, "end": v(12.86, 25.1) * mm});
            skLineSegment(sketch, "E25.0.5.62", {"start": v(58.68, 21) * mm, "end": v(58.68, 23) * mm});
            skLineSegment(sketch, "E25.0.5.63", {"start": v(12.96, 25.1) * mm, "end": v(12.98, 23.1) * mm});
            skLineSegment(sketch, "E25.0.5.64", {"start": v(37.36, 25.1) * mm, "end": v(37.38, 23.1) * mm});
            skLineSegment(sketch, "E25.0.5.65", {"start": v(61.66, 23.1) * mm, "end": v(55.68, 23.1) * mm});
            skLineSegment(sketch, "E25.0.5.66", {"start": v(15.98, 21) * mm, "end": v(15.98, 23) * mm});
            skLineSegment(sketch, "E25.0.5.67", {"start": v(37.26, 23.1) * mm, "end": v(31.28, 23.1) * mm});
            skLineSegment(sketch, "E25.0.5.68", {"start": v(22.08, 21) * mm, "end": v(22.08, 23) * mm});
            skLineSegment(sketch, "E25.0.5.69", {"start": v(46.48, 21) * mm, "end": v(46.48, 23) * mm});
            skLineSegment(sketch, "E25.0.5.70", {"start": v(25.06, 23.1) * mm, "end": v(25.06, 25.1) * mm});
            skLineSegment(sketch, "E25.0.5.71", {"start": v(28.28, 23) * mm, "end": v(28.28, 21) * mm});
            skLineSegment(sketch, "E25.0.5.72", {"start": v(31.16, 23.1) * mm, "end": v(31.16, 25.1) * mm});
            skLineSegment(sketch, "E25.0.5.73", {"start": v(55.56, 23.1) * mm, "end": v(55.56, 25.1) * mm});
            skLineSegment(sketch, "E25.0.5.74", {"start": v(28.18, 23) * mm, "end": v(22.18, 23) * mm});
            skLineSegment(sketch, "E25.0.5.75", {"start": v(52.68, 23) * mm, "end": v(52.68, 21) * mm});
            skLineSegment(sketch, "E25.0.5.76", {"start": v(70.88, 21) * mm, "end": v(70.88, 23) * mm});
            skLineSegment(sketch, "E25.0.5.77", {"start": v(70.88, 23) * mm, "end": v(64.88, 23) * mm});
            skLineSegment(sketch, "E25.0.5.78", {"start": v(64.88, 23) * mm, "end": v(64.88, 21) * mm});
            skLineSegment(sketch, "E25.0.5.79", {"start": v(64.78, 21) * mm, "end": v(64.78, 23) * mm});
            skLineSegment(sketch, "E25.0.5.80", {"start": v(58.78, 23) * mm, "end": v(58.78, 21) * mm});
            skLineSegment(sketch, "E25.0.5.81", {"start": v(67.86, 25.1) * mm, "end": v(70.88, 25.1) * mm});
            skLineSegment(sketch, "E25.0.5.82", {"start": v(70.88, 25.1) * mm, "end": v(70.88, 23.1) * mm});
            skLineSegment(sketch, "E25.0.5.83", {"start": v(70.88, 25.1) * mm, "end": v(70.88, 25.2) * mm});
            skLineSegment(sketch, "E25.0.5.84", {"start": v(70.88, 23.1) * mm, "end": v(67.86, 23.1) * mm});
            skLineSegment(sketch, "E25.0.5.85", {"start": v(67.76, 23.1) * mm, "end": v(61.78, 23.1) * mm});
            skLineSegment(sketch, "E25.0.5.86", {"start": v(67.86, 23.1) * mm, "end": v(67.86, 25.1) * mm});
            skLineSegment(sketch, "E25.0.5.87", {"start": v(61.66, 23.1) * mm, "end": v(61.66, 25.1) * mm});
            skLineSegment(sketch, "E25.0.5.88", {"start": v(61.76, 25.1) * mm, "end": v(61.78, 23.1) * mm});
            skLineSegment(sketch, "E25.0.5.89", {"start": v(67.76, 23.1) * mm, "end": v(67.76, 25.1) * mm});
            skLineSegment(sketch, "E25.0.5.90", {"start": v(64.88, 21) * mm, "end": v(64.78, 21) * mm});
            skLineSegment(sketch, "E25.0.5.91", {"start": v(67.86, 23.1) * mm, "end": v(67.76, 23.1) * mm});
            skLineSegment(sketch, "E25.0.6.0", {"start": v(31.16, 29.3) * mm, "end": v(25.16, 29.3) * mm});
            skLineSegment(sketch, "E25.0.6.1", {"start": v(55.56, 29.3) * mm, "end": v(49.56, 29.3) * mm});
            skLineSegment(sketch, "E25.0.6.2", {"start": v(18.96, 29.3) * mm, "end": v(12.96, 29.3) * mm});
            skLineSegment(sketch, "E25.0.6.3", {"start": v(43.36, 29.3) * mm, "end": v(37.36, 29.3) * mm});
            skLineSegment(sketch, "E25.0.6.4", {"start": v(25.06, 29.3) * mm, "end": v(19.06, 29.3) * mm});
            skLineSegment(sketch, "E25.0.6.5", {"start": v(49.46, 29.3) * mm, "end": v(43.46, 29.3) * mm});
            skLineSegment(sketch, "E25.0.6.6", {"start": v(61.66, 29.3) * mm, "end": v(55.66, 29.3) * mm});
            skLineSegment(sketch, "E25.0.6.7", {"start": v(12.86, 29.3) * mm, "end": v(6.86, 29.3) * mm});
            skLineSegment(sketch, "E25.0.6.8", {"start": v(37.26, 29.3) * mm, "end": v(31.26, 29.3) * mm});
            skLineSegment(sketch, "E25.0.6.9", {"start": v(46.58, 25.2) * mm, "end": v(52.58, 25.2) * mm});
            skLineSegment(sketch, "E25.0.6.10", {"start": v(22.18, 25.2) * mm, "end": v(28.18, 25.2) * mm});
            skLineSegment(sketch, "E25.0.6.11", {"start": v(9.98, 25.2) * mm, "end": v(15.98, 25.2) * mm});
            skLineSegment(sketch, "E25.0.6.12", {"start": v(34.38, 25.2) * mm, "end": v(40.38, 25.2) * mm});
            skLineSegment(sketch, "E25.0.6.13", {"start": v(16.08, 25.2) * mm, "end": v(22.08, 25.2) * mm});
            skLineSegment(sketch, "E25.0.6.14", {"start": v(40.48, 25.2) * mm, "end": v(46.48, 25.2) * mm});
            skPoint(sketch, "E25.0.6.15", {"position": v(61.78, 27.2) * mm});
            skLineSegment(sketch, "E25.0.6.16", {"start": v(3.88, 25.2) * mm, "end": v(9.88, 25.2) * mm});
            skLineSegment(sketch, "E25.0.6.17", {"start": v(28.28, 25.2) * mm, "end": v(34.28, 25.2) * mm});
            skLineSegment(sketch, "E25.0.6.18", {"start": v(52.68, 25.2) * mm, "end": v(58.68, 25.2) * mm});
            skLineSegment(sketch, "E25.0.6.19", {"start": v(64.88, 25.2) * mm, "end": v(70.88, 25.2) * mm});
            skLineSegment(sketch, "E25.0.6.20", {"start": v(67.76, 29.3) * mm, "end": v(61.76, 29.3) * mm});
            skLineSegment(sketch, "E25.0.6.22", {"start": v(58.78, 25.2) * mm, "end": v(64.78, 25.2) * mm});
            skLineSegment(sketch, "E25.0.6.23", {"start": v(43.46, 29.3) * mm, "end": v(43.48, 27.3) * mm});
            skLineSegment(sketch, "E25.0.6.24", {"start": v(6.86, 29.3) * mm, "end": v(6.88, 27.3) * mm});
            skLineSegment(sketch, "E25.0.6.25", {"start": v(9.88, 27.2) * mm, "end": v(3.88, 27.2) * mm});
            skLineSegment(sketch, "E25.0.6.26", {"start": v(12.86, 27.3) * mm, "end": v(6.88, 27.3) * mm});
            skLineSegment(sketch, "E25.0.6.27", {"start": v(46.48, 27.2) * mm, "end": v(40.48, 27.2) * mm});
            skLineSegment(sketch, "E25.0.6.28", {"start": v(15.98, 27.2) * mm, "end": v(9.98, 27.2) * mm});
            skLineSegment(sketch, "E25.0.6.29", {"start": v(43.36, 27.3) * mm, "end": v(43.36, 29.3) * mm});
            skLineSegment(sketch, "E25.0.6.30", {"start": v(9.98, 27.2) * mm, "end": v(9.98, 25.2) * mm});
            skLineSegment(sketch, "E25.0.6.31", {"start": v(9.88, 25.2) * mm, "end": v(9.88, 27.2) * mm});
            skLineSegment(sketch, "E25.0.6.32", {"start": v(49.46, 27.3) * mm, "end": v(43.48, 27.3) * mm});
            skLineSegment(sketch, "E25.0.6.33", {"start": v(40.38, 25.2) * mm, "end": v(40.38, 27.2) * mm});
            skLineSegment(sketch, "E25.0.6.34", {"start": v(18.96, 27.3) * mm, "end": v(12.98, 27.3) * mm});
            skLineSegment(sketch, "E25.0.6.35", {"start": v(43.36, 27.3) * mm, "end": v(37.38, 27.3) * mm});
            skLineSegment(sketch, "E25.0.6.36", {"start": v(49.46, 27.3) * mm, "end": v(49.46, 29.3) * mm});
            skLineSegment(sketch, "E25.0.6.37", {"start": v(22.08, 27.2) * mm, "end": v(16.08, 27.2) * mm});
            skLineSegment(sketch, "E25.0.6.38", {"start": v(52.58, 27.2) * mm, "end": v(46.58, 27.2) * mm});
            skLineSegment(sketch, "E25.0.6.39", {"start": v(40.38, 27.2) * mm, "end": v(34.38, 27.2) * mm});
            skLineSegment(sketch, "E25.0.6.40", {"start": v(18.96, 27.3) * mm, "end": v(18.96, 29.3) * mm});
            skLineSegment(sketch, "E25.0.6.41", {"start": v(40.48, 27.2) * mm, "end": v(40.48, 25.2) * mm});
            skLineSegment(sketch, "E25.0.6.42", {"start": v(25.16, 29.3) * mm, "end": v(25.18, 27.3) * mm});
            skLineSegment(sketch, "E25.0.6.43", {"start": v(49.56, 29.3) * mm, "end": v(49.58, 27.3) * mm});
            skLineSegment(sketch, "E25.0.6.44", {"start": v(16.08, 27.2) * mm, "end": v(16.08, 25.2) * mm});
            skLineSegment(sketch, "E25.0.6.45", {"start": v(58.68, 27.2) * mm, "end": v(52.68, 27.2) * mm});
            skLineSegment(sketch, "E25.0.6.46", {"start": v(46.58, 27.2) * mm, "end": v(46.58, 25.2) * mm});
            skLineSegment(sketch, "E25.0.6.47", {"start": v(22.18, 27.2) * mm, "end": v(22.18, 25.2) * mm});
            skLineSegment(sketch, "E25.0.6.48", {"start": v(64.78, 27.2) * mm, "end": v(58.78, 27.2) * mm});
            skLineSegment(sketch, "E25.0.6.49", {"start": v(34.38, 27.2) * mm, "end": v(34.38, 25.2) * mm});
            skLineSegment(sketch, "E25.0.6.50", {"start": v(19.06, 29.3) * mm, "end": v(19.08, 27.3) * mm});
            skLineSegment(sketch, "E25.0.6.51", {"start": v(31.16, 27.3) * mm, "end": v(25.18, 27.3) * mm});
            skLineSegment(sketch, "E25.0.6.52", {"start": v(55.56, 27.3) * mm, "end": v(49.58, 27.3) * mm});
            skLineSegment(sketch, "E25.0.6.53", {"start": v(34.28, 25.2) * mm, "end": v(34.28, 27.2) * mm});
            skLineSegment(sketch, "E25.0.6.54", {"start": v(55.66, 29.3) * mm, "end": v(55.68, 27.3) * mm});
            skLineSegment(sketch, "E25.0.6.55", {"start": v(31.26, 29.3) * mm, "end": v(31.28, 27.3) * mm});
            skLineSegment(sketch, "E25.0.6.56", {"start": v(52.58, 25.2) * mm, "end": v(52.58, 27.2) * mm});
            skLineSegment(sketch, "E25.0.6.57", {"start": v(37.26, 27.3) * mm, "end": v(37.26, 29.3) * mm});
            skLineSegment(sketch, "E25.0.6.58", {"start": v(25.06, 27.3) * mm, "end": v(19.08, 27.3) * mm});
            skLineSegment(sketch, "E25.0.6.59", {"start": v(34.28, 27.2) * mm, "end": v(28.28, 27.2) * mm});
            skLineSegment(sketch, "E25.0.6.60", {"start": v(28.18, 25.2) * mm, "end": v(28.18, 27.2) * mm});
            skLineSegment(sketch, "E25.0.6.61", {"start": v(12.86, 27.3) * mm, "end": v(12.86, 29.3) * mm});
            skLineSegment(sketch, "E25.0.6.62", {"start": v(58.68, 25.2) * mm, "end": v(58.68, 27.2) * mm});
            skLineSegment(sketch, "E25.0.6.63", {"start": v(12.96, 29.3) * mm, "end": v(12.98, 27.3) * mm});
            skLineSegment(sketch, "E25.0.6.64", {"start": v(37.36, 29.3) * mm, "end": v(37.38, 27.3) * mm});
            skLineSegment(sketch, "E25.0.6.65", {"start": v(61.66, 27.3) * mm, "end": v(55.68, 27.3) * mm});
            skLineSegment(sketch, "E25.0.6.66", {"start": v(15.98, 25.2) * mm, "end": v(15.98, 27.2) * mm});
            skLineSegment(sketch, "E25.0.6.67", {"start": v(37.26, 27.3) * mm, "end": v(31.28, 27.3) * mm});
            skLineSegment(sketch, "E25.0.6.68", {"start": v(22.08, 25.2) * mm, "end": v(22.08, 27.2) * mm});
            skLineSegment(sketch, "E25.0.6.69", {"start": v(46.48, 25.2) * mm, "end": v(46.48, 27.2) * mm});
            skLineSegment(sketch, "E25.0.6.70", {"start": v(25.06, 27.3) * mm, "end": v(25.06, 29.3) * mm});
            skLineSegment(sketch, "E25.0.6.71", {"start": v(28.28, 27.2) * mm, "end": v(28.28, 25.2) * mm});
            skLineSegment(sketch, "E25.0.6.72", {"start": v(31.16, 27.3) * mm, "end": v(31.16, 29.3) * mm});
            skLineSegment(sketch, "E25.0.6.73", {"start": v(55.56, 27.3) * mm, "end": v(55.56, 29.3) * mm});
            skLineSegment(sketch, "E25.0.6.74", {"start": v(28.18, 27.2) * mm, "end": v(22.18, 27.2) * mm});
            skLineSegment(sketch, "E25.0.6.75", {"start": v(52.68, 27.2) * mm, "end": v(52.68, 25.2) * mm});
            skLineSegment(sketch, "E25.0.6.76", {"start": v(70.88, 25.2) * mm, "end": v(70.88, 27.2) * mm});
            skLineSegment(sketch, "E25.0.6.77", {"start": v(70.88, 27.2) * mm, "end": v(64.88, 27.2) * mm});
            skLineSegment(sketch, "E25.0.6.78", {"start": v(64.88, 27.2) * mm, "end": v(64.88, 25.2) * mm});
            skLineSegment(sketch, "E25.0.6.79", {"start": v(64.78, 25.2) * mm, "end": v(64.78, 27.2) * mm});
            skLineSegment(sketch, "E25.0.6.80", {"start": v(58.78, 27.2) * mm, "end": v(58.78, 25.2) * mm});
            skLineSegment(sketch, "E25.0.6.81", {"start": v(67.86, 29.3) * mm, "end": v(70.88, 29.3) * mm});
            skLineSegment(sketch, "E25.0.6.82", {"start": v(70.88, 29.3) * mm, "end": v(70.88, 27.3) * mm});
            skLineSegment(sketch, "E25.0.6.83", {"start": v(70.88, 29.3) * mm, "end": v(70.88, 29.4) * mm});
            skLineSegment(sketch, "E25.0.6.84", {"start": v(70.88, 27.3) * mm, "end": v(67.86, 27.3) * mm});
            skLineSegment(sketch, "E25.0.6.85", {"start": v(67.76, 27.3) * mm, "end": v(61.78, 27.3) * mm});
            skLineSegment(sketch, "E25.0.6.86", {"start": v(67.86, 27.3) * mm, "end": v(67.86, 29.3) * mm});
            skLineSegment(sketch, "E25.0.6.87", {"start": v(61.66, 27.3) * mm, "end": v(61.66, 29.3) * mm});
            skLineSegment(sketch, "E25.0.6.88", {"start": v(61.76, 29.3) * mm, "end": v(61.78, 27.3) * mm});
            skLineSegment(sketch, "E25.0.6.89", {"start": v(67.76, 27.3) * mm, "end": v(67.76, 29.3) * mm});
            skLineSegment(sketch, "E25.0.6.90", {"start": v(64.88, 25.2) * mm, "end": v(64.78, 25.2) * mm});
            skLineSegment(sketch, "E25.0.6.91", {"start": v(67.86, 27.3) * mm, "end": v(67.76, 27.3) * mm});
            skLineSegment(sketch, "E25.0.7.0", {"start": v(31.16, 33.5) * mm, "end": v(25.16, 33.5) * mm});
            skLineSegment(sketch, "E25.0.7.1", {"start": v(55.56, 33.5) * mm, "end": v(49.56, 33.5) * mm});
            skLineSegment(sketch, "E25.0.7.2", {"start": v(18.96, 33.5) * mm, "end": v(12.96, 33.5) * mm});
            skLineSegment(sketch, "E25.0.7.3", {"start": v(43.36, 33.5) * mm, "end": v(37.36, 33.5) * mm});
            skLineSegment(sketch, "E25.0.7.4", {"start": v(25.06, 33.5) * mm, "end": v(19.06, 33.5) * mm});
            skLineSegment(sketch, "E25.0.7.5", {"start": v(49.46, 33.5) * mm, "end": v(43.46, 33.5) * mm});
            skLineSegment(sketch, "E25.0.7.6", {"start": v(61.66, 33.5) * mm, "end": v(55.66, 33.5) * mm});
            skLineSegment(sketch, "E25.0.7.7", {"start": v(12.86, 33.5) * mm, "end": v(6.86, 33.5) * mm});
            skLineSegment(sketch, "E25.0.7.8", {"start": v(37.26, 33.5) * mm, "end": v(31.26, 33.5) * mm});
            skLineSegment(sketch, "E25.0.7.9", {"start": v(46.58, 29.4) * mm, "end": v(52.58, 29.4) * mm});
            skLineSegment(sketch, "E25.0.7.10", {"start": v(22.18, 29.4) * mm, "end": v(28.18, 29.4) * mm});
            skLineSegment(sketch, "E25.0.7.11", {"start": v(9.98, 29.4) * mm, "end": v(15.98, 29.4) * mm});
            skLineSegment(sketch, "E25.0.7.12", {"start": v(34.38, 29.4) * mm, "end": v(40.38, 29.4) * mm});
            skLineSegment(sketch, "E25.0.7.13", {"start": v(16.08, 29.4) * mm, "end": v(22.08, 29.4) * mm});
            skLineSegment(sketch, "E25.0.7.14", {"start": v(40.48, 29.4) * mm, "end": v(46.48, 29.4) * mm});
            skPoint(sketch, "E25.0.7.15", {"position": v(61.78, 31.4) * mm});
            skLineSegment(sketch, "E25.0.7.17", {"start": v(28.28, 29.4) * mm, "end": v(34.28, 29.4) * mm});
            skLineSegment(sketch, "E25.0.7.18", {"start": v(52.68, 29.4) * mm, "end": v(58.68, 29.4) * mm});
            skLineSegment(sketch, "E25.0.7.19", {"start": v(64.88, 29.4) * mm, "end": v(70.88, 29.4) * mm});
            skLineSegment(sketch, "E25.0.7.20", {"start": v(67.76, 33.5) * mm, "end": v(61.76, 33.5) * mm});
            skLineSegment(sketch, "E25.0.7.22", {"start": v(58.78, 29.4) * mm, "end": v(64.78, 29.4) * mm});
            skLineSegment(sketch, "E25.0.7.23", {"start": v(43.46, 33.5) * mm, "end": v(43.48, 31.5) * mm});
            skLineSegment(sketch, "E25.0.7.24", {"start": v(6.86, 33.5) * mm, "end": v(6.88, 31.5) * mm});
            skLineSegment(sketch, "E25.0.7.26", {"start": v(12.86, 31.5) * mm, "end": v(6.88, 31.5) * mm});
            skLineSegment(sketch, "E25.0.7.27", {"start": v(46.48, 31.4) * mm, "end": v(40.48, 31.4) * mm});
            skLineSegment(sketch, "E25.0.7.28", {"start": v(15.98, 31.4) * mm, "end": v(9.98, 31.4) * mm});
            skLineSegment(sketch, "E25.0.7.29", {"start": v(43.36, 31.5) * mm, "end": v(43.36, 33.5) * mm});
            skLineSegment(sketch, "E25.0.7.30", {"start": v(9.98, 31.4) * mm, "end": v(9.98, 29.4) * mm});
            skLineSegment(sketch, "E25.0.7.31", {"start": v(9.88, 29.4) * mm, "end": v(9.88, 31.4) * mm});
            skLineSegment(sketch, "E25.0.7.32", {"start": v(49.46, 31.5) * mm, "end": v(43.48, 31.5) * mm});
            skLineSegment(sketch, "E25.0.7.33", {"start": v(40.38, 29.4) * mm, "end": v(40.38, 31.4) * mm});
            skLineSegment(sketch, "E25.0.7.34", {"start": v(18.96, 31.5) * mm, "end": v(12.98, 31.5) * mm});
            skLineSegment(sketch, "E25.0.7.35", {"start": v(43.36, 31.5) * mm, "end": v(37.38, 31.5) * mm});
            skLineSegment(sketch, "E25.0.7.36", {"start": v(49.46, 31.5) * mm, "end": v(49.46, 33.5) * mm});
            skLineSegment(sketch, "E25.0.7.37", {"start": v(22.08, 31.4) * mm, "end": v(16.08, 31.4) * mm});
            skLineSegment(sketch, "E25.0.7.38", {"start": v(52.58, 31.4) * mm, "end": v(46.58, 31.4) * mm});
            skLineSegment(sketch, "E25.0.7.39", {"start": v(40.38, 31.4) * mm, "end": v(34.38, 31.4) * mm});
            skLineSegment(sketch, "E25.0.7.40", {"start": v(18.96, 31.5) * mm, "end": v(18.96, 33.5) * mm});
            skLineSegment(sketch, "E25.0.7.41", {"start": v(40.48, 31.4) * mm, "end": v(40.48, 29.4) * mm});
            skLineSegment(sketch, "E25.0.7.42", {"start": v(25.16, 33.5) * mm, "end": v(25.18, 31.5) * mm});
            skLineSegment(sketch, "E25.0.7.43", {"start": v(49.56, 33.5) * mm, "end": v(49.58, 31.5) * mm});
            skLineSegment(sketch, "E25.0.7.44", {"start": v(16.08, 31.4) * mm, "end": v(16.08, 29.4) * mm});
            skLineSegment(sketch, "E25.0.7.45", {"start": v(58.68, 31.4) * mm, "end": v(52.68, 31.4) * mm});
            skLineSegment(sketch, "E25.0.7.46", {"start": v(46.58, 31.4) * mm, "end": v(46.58, 29.4) * mm});
            skLineSegment(sketch, "E25.0.7.47", {"start": v(22.18, 31.4) * mm, "end": v(22.18, 29.4) * mm});
            skLineSegment(sketch, "E25.0.7.48", {"start": v(64.78, 31.4) * mm, "end": v(58.78, 31.4) * mm});
            skLineSegment(sketch, "E25.0.7.49", {"start": v(34.38, 31.4) * mm, "end": v(34.38, 29.4) * mm});
            skLineSegment(sketch, "E25.0.7.50", {"start": v(19.06, 33.5) * mm, "end": v(19.08, 31.5) * mm});
            skLineSegment(sketch, "E25.0.7.51", {"start": v(31.16, 31.5) * mm, "end": v(25.18, 31.5) * mm});
            skLineSegment(sketch, "E25.0.7.52", {"start": v(55.56, 31.5) * mm, "end": v(49.58, 31.5) * mm});
            skLineSegment(sketch, "E25.0.7.53", {"start": v(34.28, 29.4) * mm, "end": v(34.28, 31.4) * mm});
            skLineSegment(sketch, "E25.0.7.54", {"start": v(55.66, 33.5) * mm, "end": v(55.68, 31.5) * mm});
            skLineSegment(sketch, "E25.0.7.55", {"start": v(31.26, 33.5) * mm, "end": v(31.28, 31.5) * mm});
            skLineSegment(sketch, "E25.0.7.56", {"start": v(52.58, 29.4) * mm, "end": v(52.58, 31.4) * mm});
            skLineSegment(sketch, "E25.0.7.57", {"start": v(37.26, 31.5) * mm, "end": v(37.26, 33.5) * mm});
            skLineSegment(sketch, "E25.0.7.58", {"start": v(25.06, 31.5) * mm, "end": v(19.08, 31.5) * mm});
            skLineSegment(sketch, "E25.0.7.59", {"start": v(34.28, 31.4) * mm, "end": v(28.28, 31.4) * mm});
            skLineSegment(sketch, "E25.0.7.60", {"start": v(28.18, 29.4) * mm, "end": v(28.18, 31.4) * mm});
            skLineSegment(sketch, "E25.0.7.61", {"start": v(12.86, 31.5) * mm, "end": v(12.86, 33.5) * mm});
            skLineSegment(sketch, "E25.0.7.62", {"start": v(58.68, 29.4) * mm, "end": v(58.68, 31.4) * mm});
            skLineSegment(sketch, "E25.0.7.63", {"start": v(12.96, 33.5) * mm, "end": v(12.98, 31.5) * mm});
            skLineSegment(sketch, "E25.0.7.64", {"start": v(37.36, 33.5) * mm, "end": v(37.38, 31.5) * mm});
            skLineSegment(sketch, "E25.0.7.65", {"start": v(61.66, 31.5) * mm, "end": v(55.68, 31.5) * mm});
            skLineSegment(sketch, "E25.0.7.66", {"start": v(15.98, 29.4) * mm, "end": v(15.98, 31.4) * mm});
            skLineSegment(sketch, "E25.0.7.67", {"start": v(37.26, 31.5) * mm, "end": v(31.28, 31.5) * mm});
            skLineSegment(sketch, "E25.0.7.68", {"start": v(22.08, 29.4) * mm, "end": v(22.08, 31.4) * mm});
            skLineSegment(sketch, "E25.0.7.69", {"start": v(46.48, 29.4) * mm, "end": v(46.48, 31.4) * mm});
            skLineSegment(sketch, "E25.0.7.70", {"start": v(25.06, 31.5) * mm, "end": v(25.06, 33.5) * mm});
            skLineSegment(sketch, "E25.0.7.71", {"start": v(28.28, 31.4) * mm, "end": v(28.28, 29.4) * mm});
            skLineSegment(sketch, "E25.0.7.72", {"start": v(31.16, 31.5) * mm, "end": v(31.16, 33.5) * mm});
            skLineSegment(sketch, "E25.0.7.73", {"start": v(55.56, 31.5) * mm, "end": v(55.56, 33.5) * mm});
            skLineSegment(sketch, "E25.0.7.74", {"start": v(28.18, 31.4) * mm, "end": v(22.18, 31.4) * mm});
            skLineSegment(sketch, "E25.0.7.75", {"start": v(52.68, 31.4) * mm, "end": v(52.68, 29.4) * mm});
            skLineSegment(sketch, "E25.0.7.76", {"start": v(70.88, 29.4) * mm, "end": v(70.88, 31.4) * mm});
            skLineSegment(sketch, "E25.0.7.77", {"start": v(70.88, 31.4) * mm, "end": v(64.88, 31.4) * mm});
            skLineSegment(sketch, "E25.0.7.78", {"start": v(64.88, 31.4) * mm, "end": v(64.88, 29.4) * mm});
            skLineSegment(sketch, "E25.0.7.79", {"start": v(64.78, 29.4) * mm, "end": v(64.78, 31.4) * mm});
            skLineSegment(sketch, "E25.0.7.80", {"start": v(58.78, 31.4) * mm, "end": v(58.78, 29.4) * mm});
            skLineSegment(sketch, "E25.0.7.81", {"start": v(67.86, 33.5) * mm, "end": v(70.88, 33.5) * mm});
            skLineSegment(sketch, "E25.0.7.82", {"start": v(70.88, 33.5) * mm, "end": v(70.88, 31.5) * mm});
            skLineSegment(sketch, "E25.0.7.83", {"start": v(70.88, 33.5) * mm, "end": v(70.88, 33.6) * mm});
            skLineSegment(sketch, "E25.0.7.84", {"start": v(70.88, 31.5) * mm, "end": v(67.86, 31.5) * mm});
            skLineSegment(sketch, "E25.0.7.85", {"start": v(67.76, 31.5) * mm, "end": v(61.78, 31.5) * mm});
            skLineSegment(sketch, "E25.0.7.86", {"start": v(67.86, 31.5) * mm, "end": v(67.86, 33.5) * mm});
            skLineSegment(sketch, "E25.0.7.87", {"start": v(61.66, 31.5) * mm, "end": v(61.66, 33.5) * mm});
            skLineSegment(sketch, "E25.0.7.88", {"start": v(61.76, 33.5) * mm, "end": v(61.78, 31.5) * mm});
            skLineSegment(sketch, "E25.0.7.89", {"start": v(67.76, 31.5) * mm, "end": v(67.76, 33.5) * mm});
            skLineSegment(sketch, "E25.0.7.90", {"start": v(64.88, 29.4) * mm, "end": v(64.78, 29.4) * mm});
            skLineSegment(sketch, "E25.0.7.91", {"start": v(67.86, 31.5) * mm, "end": v(67.76, 31.5) * mm});
            skLineSegment(sketch, "E25.0.8.0", {"start": v(31.16, 37.7) * mm, "end": v(25.16, 37.7) * mm});
            skLineSegment(sketch, "E25.0.8.1", {"start": v(55.56, 37.7) * mm, "end": v(49.56, 37.7) * mm});
            skLineSegment(sketch, "E25.0.8.2", {"start": v(18.96, 37.7) * mm, "end": v(12.96, 37.7) * mm});
            skLineSegment(sketch, "E25.0.8.3", {"start": v(43.36, 37.7) * mm, "end": v(37.36, 37.7) * mm});
            skLineSegment(sketch, "E25.0.8.4", {"start": v(25.06, 37.7) * mm, "end": v(19.06, 37.7) * mm});
            skLineSegment(sketch, "E25.0.8.5", {"start": v(49.46, 37.7) * mm, "end": v(43.46, 37.7) * mm});
            skLineSegment(sketch, "E25.0.8.6", {"start": v(61.66, 37.7) * mm, "end": v(55.66, 37.7) * mm});
            skLineSegment(sketch, "E25.0.8.7", {"start": v(12.86, 37.7) * mm, "end": v(6.86, 37.7) * mm});
            skLineSegment(sketch, "E25.0.8.8", {"start": v(37.26, 37.7) * mm, "end": v(31.26, 37.7) * mm});
            skLineSegment(sketch, "E25.0.8.9", {"start": v(46.58, 33.6) * mm, "end": v(52.58, 33.6) * mm});
            skLineSegment(sketch, "E25.0.8.10", {"start": v(22.18, 33.6) * mm, "end": v(28.18, 33.6) * mm});
            skLineSegment(sketch, "E25.0.8.11", {"start": v(9.98, 33.6) * mm, "end": v(15.98, 33.6) * mm});
            skLineSegment(sketch, "E25.0.8.12", {"start": v(34.38, 33.6) * mm, "end": v(40.38, 33.6) * mm});
            skLineSegment(sketch, "E25.0.8.13", {"start": v(16.08, 33.6) * mm, "end": v(22.08, 33.6) * mm});
            skLineSegment(sketch, "E25.0.8.14", {"start": v(40.48, 33.6) * mm, "end": v(46.48, 33.6) * mm});
            skPoint(sketch, "E25.0.8.15", {"position": v(61.78, 35.6) * mm});
            skLineSegment(sketch, "E25.0.8.17", {"start": v(28.28, 33.6) * mm, "end": v(34.28, 33.6) * mm});
            skLineSegment(sketch, "E25.0.8.18", {"start": v(52.68, 33.6) * mm, "end": v(58.68, 33.6) * mm});
            skLineSegment(sketch, "E25.0.8.19", {"start": v(64.88, 33.6) * mm, "end": v(70.88, 33.6) * mm});
            skLineSegment(sketch, "E25.0.8.20", {"start": v(67.76, 37.7) * mm, "end": v(61.76, 37.7) * mm});
            skLineSegment(sketch, "E25.0.8.22", {"start": v(58.78, 33.6) * mm, "end": v(64.78, 33.6) * mm});
            skLineSegment(sketch, "E25.0.8.23", {"start": v(43.46, 37.7) * mm, "end": v(43.48, 35.7) * mm});
            skLineSegment(sketch, "E25.0.8.24", {"start": v(6.86, 37.7) * mm, "end": v(6.88, 35.7) * mm});
            skLineSegment(sketch, "E25.0.8.26", {"start": v(12.86, 35.7) * mm, "end": v(6.88, 35.7) * mm});
            skLineSegment(sketch, "E25.0.8.27", {"start": v(46.48, 35.6) * mm, "end": v(40.48, 35.6) * mm});
            skLineSegment(sketch, "E25.0.8.28", {"start": v(15.98, 35.6) * mm, "end": v(9.98, 35.6) * mm});
            skLineSegment(sketch, "E25.0.8.29", {"start": v(43.36, 35.7) * mm, "end": v(43.36, 37.7) * mm});
            skLineSegment(sketch, "E25.0.8.30", {"start": v(9.98, 35.6) * mm, "end": v(9.98, 33.6) * mm});
            skLineSegment(sketch, "E25.0.8.31", {"start": v(9.88, 33.6) * mm, "end": v(9.88, 35.6) * mm});
            skLineSegment(sketch, "E25.0.8.32", {"start": v(49.46, 35.7) * mm, "end": v(43.48, 35.7) * mm});
            skLineSegment(sketch, "E25.0.8.33", {"start": v(40.38, 33.6) * mm, "end": v(40.38, 35.6) * mm});
            skLineSegment(sketch, "E25.0.8.34", {"start": v(18.96, 35.7) * mm, "end": v(12.98, 35.7) * mm});
            skLineSegment(sketch, "E25.0.8.35", {"start": v(43.36, 35.7) * mm, "end": v(37.38, 35.7) * mm});
            skLineSegment(sketch, "E25.0.8.36", {"start": v(49.46, 35.7) * mm, "end": v(49.46, 37.7) * mm});
            skLineSegment(sketch, "E25.0.8.37", {"start": v(22.08, 35.6) * mm, "end": v(16.08, 35.6) * mm});
            skLineSegment(sketch, "E25.0.8.38", {"start": v(52.58, 35.6) * mm, "end": v(46.58, 35.6) * mm});
            skLineSegment(sketch, "E25.0.8.39", {"start": v(40.38, 35.6) * mm, "end": v(34.38, 35.6) * mm});
            skLineSegment(sketch, "E25.0.8.40", {"start": v(18.96, 35.7) * mm, "end": v(18.96, 37.7) * mm});
            skLineSegment(sketch, "E25.0.8.41", {"start": v(40.48, 35.6) * mm, "end": v(40.48, 33.6) * mm});
            skLineSegment(sketch, "E25.0.8.42", {"start": v(25.16, 37.7) * mm, "end": v(25.18, 35.7) * mm});
            skLineSegment(sketch, "E25.0.8.43", {"start": v(49.56, 37.7) * mm, "end": v(49.58, 35.7) * mm});
            skLineSegment(sketch, "E25.0.8.44", {"start": v(16.08, 35.6) * mm, "end": v(16.08, 33.6) * mm});
            skLineSegment(sketch, "E25.0.8.45", {"start": v(58.68, 35.6) * mm, "end": v(52.68, 35.6) * mm});
            skLineSegment(sketch, "E25.0.8.46", {"start": v(46.58, 35.6) * mm, "end": v(46.58, 33.6) * mm});
            skLineSegment(sketch, "E25.0.8.47", {"start": v(22.18, 35.6) * mm, "end": v(22.18, 33.6) * mm});
            skLineSegment(sketch, "E25.0.8.48", {"start": v(64.78, 35.6) * mm, "end": v(58.78, 35.6) * mm});
            skLineSegment(sketch, "E25.0.8.49", {"start": v(34.38, 35.6) * mm, "end": v(34.38, 33.6) * mm});
            skLineSegment(sketch, "E25.0.8.50", {"start": v(19.06, 37.7) * mm, "end": v(19.08, 35.7) * mm});
            skLineSegment(sketch, "E25.0.8.51", {"start": v(31.16, 35.7) * mm, "end": v(25.18, 35.7) * mm});
            skLineSegment(sketch, "E25.0.8.52", {"start": v(55.56, 35.7) * mm, "end": v(49.58, 35.7) * mm});
            skLineSegment(sketch, "E25.0.8.53", {"start": v(34.28, 33.6) * mm, "end": v(34.28, 35.6) * mm});
            skLineSegment(sketch, "E25.0.8.54", {"start": v(55.66, 37.7) * mm, "end": v(55.68, 35.7) * mm});
            skLineSegment(sketch, "E25.0.8.55", {"start": v(31.26, 37.7) * mm, "end": v(31.28, 35.7) * mm});
            skLineSegment(sketch, "E25.0.8.56", {"start": v(52.58, 33.6) * mm, "end": v(52.58, 35.6) * mm});
            skLineSegment(sketch, "E25.0.8.57", {"start": v(37.26, 35.7) * mm, "end": v(37.26, 37.7) * mm});
            skLineSegment(sketch, "E25.0.8.58", {"start": v(25.06, 35.7) * mm, "end": v(19.08, 35.7) * mm});
            skLineSegment(sketch, "E25.0.8.59", {"start": v(34.28, 35.6) * mm, "end": v(28.28, 35.6) * mm});
            skLineSegment(sketch, "E25.0.8.60", {"start": v(28.18, 33.6) * mm, "end": v(28.18, 35.6) * mm});
            skLineSegment(sketch, "E25.0.8.61", {"start": v(12.86, 35.7) * mm, "end": v(12.86, 37.7) * mm});
            skLineSegment(sketch, "E25.0.8.62", {"start": v(58.68, 33.6) * mm, "end": v(58.68, 35.6) * mm});
            skLineSegment(sketch, "E25.0.8.63", {"start": v(12.96, 37.7) * mm, "end": v(12.98, 35.7) * mm});
            skLineSegment(sketch, "E25.0.8.64", {"start": v(37.36, 37.7) * mm, "end": v(37.38, 35.7) * mm});
            skLineSegment(sketch, "E25.0.8.65", {"start": v(61.66, 35.7) * mm, "end": v(55.68, 35.7) * mm});
            skLineSegment(sketch, "E25.0.8.66", {"start": v(15.98, 33.6) * mm, "end": v(15.98, 35.6) * mm});
            skLineSegment(sketch, "E25.0.8.67", {"start": v(37.26, 35.7) * mm, "end": v(31.28, 35.7) * mm});
            skLineSegment(sketch, "E25.0.8.68", {"start": v(22.08, 33.6) * mm, "end": v(22.08, 35.6) * mm});
            skLineSegment(sketch, "E25.0.8.69", {"start": v(46.48, 33.6) * mm, "end": v(46.48, 35.6) * mm});
            skLineSegment(sketch, "E25.0.8.70", {"start": v(25.06, 35.7) * mm, "end": v(25.06, 37.7) * mm});
            skLineSegment(sketch, "E25.0.8.71", {"start": v(28.28, 35.6) * mm, "end": v(28.28, 33.6) * mm});
            skLineSegment(sketch, "E25.0.8.72", {"start": v(31.16, 35.7) * mm, "end": v(31.16, 37.7) * mm});
            skLineSegment(sketch, "E25.0.8.73", {"start": v(55.56, 35.7) * mm, "end": v(55.56, 37.7) * mm});
            skLineSegment(sketch, "E25.0.8.74", {"start": v(28.18, 35.6) * mm, "end": v(22.18, 35.6) * mm});
            skLineSegment(sketch, "E25.0.8.75", {"start": v(52.68, 35.6) * mm, "end": v(52.68, 33.6) * mm});
            skLineSegment(sketch, "E25.0.8.76", {"start": v(70.88, 33.6) * mm, "end": v(70.88, 35.6) * mm});
            skLineSegment(sketch, "E25.0.8.77", {"start": v(70.88, 35.6) * mm, "end": v(64.88, 35.6) * mm});
            skLineSegment(sketch, "E25.0.8.78", {"start": v(64.88, 35.6) * mm, "end": v(64.88, 33.6) * mm});
            skLineSegment(sketch, "E25.0.8.79", {"start": v(64.78, 33.6) * mm, "end": v(64.78, 35.6) * mm});
            skLineSegment(sketch, "E25.0.8.80", {"start": v(58.78, 35.6) * mm, "end": v(58.78, 33.6) * mm});
            skLineSegment(sketch, "E25.0.8.81", {"start": v(67.86, 37.7) * mm, "end": v(70.88, 37.7) * mm});
            skLineSegment(sketch, "E25.0.8.82", {"start": v(70.88, 37.7) * mm, "end": v(70.88, 35.7) * mm});
            skLineSegment(sketch, "E25.0.8.83", {"start": v(70.88, 37.7) * mm, "end": v(70.88, 37.8) * mm});
            skLineSegment(sketch, "E25.0.8.84", {"start": v(70.88, 35.7) * mm, "end": v(67.86, 35.7) * mm});
            skLineSegment(sketch, "E25.0.8.85", {"start": v(67.76, 35.7) * mm, "end": v(61.78, 35.7) * mm});
            skLineSegment(sketch, "E25.0.8.86", {"start": v(67.86, 35.7) * mm, "end": v(67.86, 37.7) * mm});
            skLineSegment(sketch, "E25.0.8.87", {"start": v(61.66, 35.7) * mm, "end": v(61.66, 37.7) * mm});
            skLineSegment(sketch, "E25.0.8.88", {"start": v(61.76, 37.7) * mm, "end": v(61.78, 35.7) * mm});
            skLineSegment(sketch, "E25.0.8.89", {"start": v(67.76, 35.7) * mm, "end": v(67.76, 37.7) * mm});
            skLineSegment(sketch, "E25.0.8.90", {"start": v(64.88, 33.6) * mm, "end": v(64.78, 33.6) * mm});
            skLineSegment(sketch, "E25.0.8.91", {"start": v(67.86, 35.7) * mm, "end": v(67.76, 35.7) * mm});
            skLineSegment(sketch, "E25.0.9.0", {"start": v(31.16, 41.9) * mm, "end": v(25.16, 41.9) * mm});
            skLineSegment(sketch, "E25.0.9.1", {"start": v(55.56, 41.9) * mm, "end": v(49.56, 41.9) * mm});
            skLineSegment(sketch, "E25.0.9.2", {"start": v(18.96, 41.9) * mm, "end": v(12.96, 41.9) * mm});
            skLineSegment(sketch, "E25.0.9.3", {"start": v(43.36, 41.9) * mm, "end": v(37.36, 41.9) * mm});
            skLineSegment(sketch, "E25.0.9.4", {"start": v(25.06, 41.9) * mm, "end": v(19.06, 41.9) * mm});
            skLineSegment(sketch, "E25.0.9.5", {"start": v(49.46, 41.9) * mm, "end": v(43.46, 41.9) * mm});
            skLineSegment(sketch, "E25.0.9.6", {"start": v(61.66, 41.9) * mm, "end": v(55.66, 41.9) * mm});
            skLineSegment(sketch, "E25.0.9.7", {"start": v(12.86, 41.9) * mm, "end": v(6.86, 41.9) * mm});
            skLineSegment(sketch, "E25.0.9.8", {"start": v(37.26, 41.9) * mm, "end": v(31.26, 41.9) * mm});
            skLineSegment(sketch, "E25.0.9.9", {"start": v(46.58, 37.8) * mm, "end": v(52.58, 37.8) * mm});
            skLineSegment(sketch, "E25.0.9.10", {"start": v(22.18, 37.8) * mm, "end": v(28.18, 37.8) * mm});
            skLineSegment(sketch, "E25.0.9.11", {"start": v(9.98, 37.8) * mm, "end": v(15.98, 37.8) * mm});
            skLineSegment(sketch, "E25.0.9.12", {"start": v(34.38, 37.8) * mm, "end": v(40.38, 37.8) * mm});
            skLineSegment(sketch, "E25.0.9.13", {"start": v(16.08, 37.8) * mm, "end": v(22.08, 37.8) * mm});
            skLineSegment(sketch, "E25.0.9.14", {"start": v(40.48, 37.8) * mm, "end": v(46.48, 37.8) * mm});
            skPoint(sketch, "E25.0.9.15", {"position": v(61.78, 39.8) * mm});
            skLineSegment(sketch, "E25.0.9.16", {"start": v(3.88, 37.8) * mm, "end": v(9.88, 37.8) * mm});
            skLineSegment(sketch, "E25.0.9.17", {"start": v(28.28, 37.8) * mm, "end": v(34.28, 37.8) * mm});
            skLineSegment(sketch, "E25.0.9.18", {"start": v(52.68, 37.8) * mm, "end": v(58.68, 37.8) * mm});
            skLineSegment(sketch, "E25.0.9.19", {"start": v(64.88, 37.8) * mm, "end": v(70.88, 37.8) * mm});
            skLineSegment(sketch, "E25.0.9.20", {"start": v(67.76, 41.9) * mm, "end": v(61.76, 41.9) * mm});
            skLineSegment(sketch, "E25.0.9.22", {"start": v(58.78, 37.8) * mm, "end": v(64.78, 37.8) * mm});
            skLineSegment(sketch, "E25.0.9.23", {"start": v(43.46, 41.9) * mm, "end": v(43.48, 39.9) * mm});
            skLineSegment(sketch, "E25.0.9.24", {"start": v(6.86, 41.9) * mm, "end": v(6.88, 39.9) * mm});
            skLineSegment(sketch, "E25.0.9.25", {"start": v(9.88, 39.8) * mm, "end": v(3.88, 39.8) * mm});
            skLineSegment(sketch, "E25.0.9.26", {"start": v(12.86, 39.9) * mm, "end": v(6.88, 39.9) * mm});
            skLineSegment(sketch, "E25.0.9.27", {"start": v(46.48, 39.8) * mm, "end": v(40.48, 39.8) * mm});
            skLineSegment(sketch, "E25.0.9.28", {"start": v(15.98, 39.8) * mm, "end": v(9.98, 39.8) * mm});
            skLineSegment(sketch, "E25.0.9.29", {"start": v(43.36, 39.9) * mm, "end": v(43.36, 41.9) * mm});
            skLineSegment(sketch, "E25.0.9.30", {"start": v(9.98, 39.8) * mm, "end": v(9.98, 37.8) * mm});
            skLineSegment(sketch, "E25.0.9.31", {"start": v(9.88, 37.8) * mm, "end": v(9.88, 39.8) * mm});
            skLineSegment(sketch, "E25.0.9.32", {"start": v(49.46, 39.9) * mm, "end": v(43.48, 39.9) * mm});
            skLineSegment(sketch, "E25.0.9.33", {"start": v(40.38, 37.8) * mm, "end": v(40.38, 39.8) * mm});
            skLineSegment(sketch, "E25.0.9.34", {"start": v(18.96, 39.9) * mm, "end": v(12.98, 39.9) * mm});
            skLineSegment(sketch, "E25.0.9.35", {"start": v(43.36, 39.9) * mm, "end": v(37.38, 39.9) * mm});
            skLineSegment(sketch, "E25.0.9.36", {"start": v(49.46, 39.9) * mm, "end": v(49.46, 41.9) * mm});
            skLineSegment(sketch, "E25.0.9.37", {"start": v(22.08, 39.8) * mm, "end": v(16.08, 39.8) * mm});
            skLineSegment(sketch, "E25.0.9.38", {"start": v(52.58, 39.8) * mm, "end": v(46.58, 39.8) * mm});
            skLineSegment(sketch, "E25.0.9.39", {"start": v(40.38, 39.8) * mm, "end": v(34.38, 39.8) * mm});
            skLineSegment(sketch, "E25.0.9.40", {"start": v(18.96, 39.9) * mm, "end": v(18.96, 41.9) * mm});
            skLineSegment(sketch, "E25.0.9.41", {"start": v(40.48, 39.8) * mm, "end": v(40.48, 37.8) * mm});
            skLineSegment(sketch, "E25.0.9.42", {"start": v(25.16, 41.9) * mm, "end": v(25.18, 39.9) * mm});
            skLineSegment(sketch, "E25.0.9.43", {"start": v(49.56, 41.9) * mm, "end": v(49.58, 39.9) * mm});
            skLineSegment(sketch, "E25.0.9.44", {"start": v(16.08, 39.8) * mm, "end": v(16.08, 37.8) * mm});
            skLineSegment(sketch, "E25.0.9.45", {"start": v(58.68, 39.8) * mm, "end": v(52.68, 39.8) * mm});
            skLineSegment(sketch, "E25.0.9.46", {"start": v(46.58, 39.8) * mm, "end": v(46.58, 37.8) * mm});
            skLineSegment(sketch, "E25.0.9.47", {"start": v(22.18, 39.8) * mm, "end": v(22.18, 37.8) * mm});
            skLineSegment(sketch, "E25.0.9.48", {"start": v(64.78, 39.8) * mm, "end": v(58.78, 39.8) * mm});
            skLineSegment(sketch, "E25.0.9.49", {"start": v(34.38, 39.8) * mm, "end": v(34.38, 37.8) * mm});
            skLineSegment(sketch, "E25.0.9.50", {"start": v(19.06, 41.9) * mm, "end": v(19.08, 39.9) * mm});
            skLineSegment(sketch, "E25.0.9.51", {"start": v(31.16, 39.9) * mm, "end": v(25.18, 39.9) * mm});
            skLineSegment(sketch, "E25.0.9.52", {"start": v(55.56, 39.9) * mm, "end": v(49.58, 39.9) * mm});
            skLineSegment(sketch, "E25.0.9.53", {"start": v(34.28, 37.8) * mm, "end": v(34.28, 39.8) * mm});
            skLineSegment(sketch, "E25.0.9.54", {"start": v(55.66, 41.9) * mm, "end": v(55.68, 39.9) * mm});
            skLineSegment(sketch, "E25.0.9.55", {"start": v(31.26, 41.9) * mm, "end": v(31.28, 39.9) * mm});
            skLineSegment(sketch, "E25.0.9.56", {"start": v(52.58, 37.8) * mm, "end": v(52.58, 39.8) * mm});
            skLineSegment(sketch, "E25.0.9.57", {"start": v(37.26, 39.9) * mm, "end": v(37.26, 41.9) * mm});
            skLineSegment(sketch, "E25.0.9.58", {"start": v(25.06, 39.9) * mm, "end": v(19.08, 39.9) * mm});
            skLineSegment(sketch, "E25.0.9.59", {"start": v(34.28, 39.8) * mm, "end": v(28.28, 39.8) * mm});
            skLineSegment(sketch, "E25.0.9.60", {"start": v(28.18, 37.8) * mm, "end": v(28.18, 39.8) * mm});
            skLineSegment(sketch, "E25.0.9.61", {"start": v(12.86, 39.9) * mm, "end": v(12.86, 41.9) * mm});
            skLineSegment(sketch, "E25.0.9.62", {"start": v(58.68, 37.8) * mm, "end": v(58.68, 39.8) * mm});
            skLineSegment(sketch, "E25.0.9.63", {"start": v(12.96, 41.9) * mm, "end": v(12.98, 39.9) * mm});
            skLineSegment(sketch, "E25.0.9.64", {"start": v(37.36, 41.9) * mm, "end": v(37.38, 39.9) * mm});
            skLineSegment(sketch, "E25.0.9.65", {"start": v(61.66, 39.9) * mm, "end": v(55.68, 39.9) * mm});
            skLineSegment(sketch, "E25.0.9.66", {"start": v(15.98, 37.8) * mm, "end": v(15.98, 39.8) * mm});
            skLineSegment(sketch, "E25.0.9.67", {"start": v(37.26, 39.9) * mm, "end": v(31.28, 39.9) * mm});
            skLineSegment(sketch, "E25.0.9.68", {"start": v(22.08, 37.8) * mm, "end": v(22.08, 39.8) * mm});
            skLineSegment(sketch, "E25.0.9.69", {"start": v(46.48, 37.8) * mm, "end": v(46.48, 39.8) * mm});
            skLineSegment(sketch, "E25.0.9.70", {"start": v(25.06, 39.9) * mm, "end": v(25.06, 41.9) * mm});
            skLineSegment(sketch, "E25.0.9.71", {"start": v(28.28, 39.8) * mm, "end": v(28.28, 37.8) * mm});
            skLineSegment(sketch, "E25.0.9.72", {"start": v(31.16, 39.9) * mm, "end": v(31.16, 41.9) * mm});
            skLineSegment(sketch, "E25.0.9.73", {"start": v(55.56, 39.9) * mm, "end": v(55.56, 41.9) * mm});
            skLineSegment(sketch, "E25.0.9.74", {"start": v(28.18, 39.8) * mm, "end": v(22.18, 39.8) * mm});
            skLineSegment(sketch, "E25.0.9.75", {"start": v(52.68, 39.8) * mm, "end": v(52.68, 37.8) * mm});
            skLineSegment(sketch, "E25.0.9.76", {"start": v(70.88, 37.8) * mm, "end": v(70.88, 39.8) * mm});
            skLineSegment(sketch, "E25.0.9.77", {"start": v(70.88, 39.8) * mm, "end": v(64.88, 39.8) * mm});
            skLineSegment(sketch, "E25.0.9.78", {"start": v(64.88, 39.8) * mm, "end": v(64.88, 37.8) * mm});
            skLineSegment(sketch, "E25.0.9.79", {"start": v(64.78, 37.8) * mm, "end": v(64.78, 39.8) * mm});
            skLineSegment(sketch, "E25.0.9.80", {"start": v(58.78, 39.8) * mm, "end": v(58.78, 37.8) * mm});
            skLineSegment(sketch, "E25.0.9.81", {"start": v(67.86, 41.9) * mm, "end": v(70.88, 41.9) * mm});
            skLineSegment(sketch, "E25.0.9.82", {"start": v(70.88, 41.9) * mm, "end": v(70.88, 39.9) * mm});
            skLineSegment(sketch, "E25.0.9.83", {"start": v(70.88, 41.9) * mm, "end": v(70.88, 42) * mm});
            skLineSegment(sketch, "E25.0.9.84", {"start": v(70.88, 39.9) * mm, "end": v(67.86, 39.9) * mm});
            skLineSegment(sketch, "E25.0.9.85", {"start": v(67.76, 39.9) * mm, "end": v(61.78, 39.9) * mm});
            skLineSegment(sketch, "E25.0.9.86", {"start": v(67.86, 39.9) * mm, "end": v(67.86, 41.9) * mm});
            skLineSegment(sketch, "E25.0.9.87", {"start": v(61.66, 39.9) * mm, "end": v(61.66, 41.9) * mm});
            skLineSegment(sketch, "E25.0.9.88", {"start": v(61.76, 41.9) * mm, "end": v(61.78, 39.9) * mm});
            skLineSegment(sketch, "E25.0.9.89", {"start": v(67.76, 39.9) * mm, "end": v(67.76, 41.9) * mm});
            skLineSegment(sketch, "E25.0.9.90", {"start": v(64.88, 37.8) * mm, "end": v(64.78, 37.8) * mm});
            skLineSegment(sketch, "E25.0.9.91", {"start": v(67.86, 39.9) * mm, "end": v(67.76, 39.9) * mm});
            skLineSegment(sketch, "E25.1.0.0", {"start": v(-35.84, 4.1) * mm, "end": v(-41.84, 4.1) * mm});
            skLineSegment(sketch, "E25.1.0.1", {"start": v(-11.44, 4.1) * mm, "end": v(-17.44, 4.1) * mm});
            skLineSegment(sketch, "E25.1.0.2", {"start": v(-48.04, 4.1) * mm, "end": v(-54.04, 4.1) * mm});
            skLineSegment(sketch, "E25.1.0.3", {"start": v(-23.64, 4.1) * mm, "end": v(-29.64, 4.1) * mm});
            skLineSegment(sketch, "E25.1.0.4", {"start": v(-41.94, 4.1) * mm, "end": v(-47.94, 4.1) * mm});
            skLineSegment(sketch, "E25.1.0.5", {"start": v(-17.54, 4.1) * mm, "end": v(-23.54, 4.1) * mm});
            skLineSegment(sketch, "E25.1.0.6", {"start": v(-5.34, 4.1) * mm, "end": v(-11.34, 4.1) * mm});
            skLineSegment(sketch, "E25.1.0.7", {"start": v(-54.14, 4.1) * mm, "end": v(-60.14, 4.1) * mm});
            skLineSegment(sketch, "E25.1.0.8", {"start": v(-29.74, 4.1) * mm, "end": v(-35.74, 4.1) * mm});
            skLineSegment(sketch, "E25.1.0.9", {"start": v(-20.42, 0) * mm, "end": v(-14.42, 0) * mm});
            skLineSegment(sketch, "E25.1.0.10", {"start": v(-44.82, 0) * mm, "end": v(-38.82, 0) * mm});
            skLineSegment(sketch, "E25.1.0.11", {"start": v(-57.02, 0) * mm, "end": v(-51.02, 0) * mm});
            skLineSegment(sketch, "E25.1.0.12", {"start": v(-32.62, 0) * mm, "end": v(-26.62, 0) * mm});
            skLineSegment(sketch, "E25.1.0.13", {"start": v(-50.92, 0) * mm, "end": v(-44.92, 0) * mm});
            skLineSegment(sketch, "E25.1.0.14", {"start": v(-26.52, 0) * mm, "end": v(-20.52, 0) * mm});
            skPoint(sketch, "E25.1.0.15", {"position": v(-5.22, 2) * mm});
            skLineSegment(sketch, "E25.1.0.16", {"start": v(-63.12, 0) * mm, "end": v(-57.12, 0) * mm});
            skLineSegment(sketch, "E25.1.0.17", {"start": v(-38.72, 0) * mm, "end": v(-32.72, 0) * mm});
            skLineSegment(sketch, "E25.1.0.18", {"start": v(-14.32, 0) * mm, "end": v(-8.32, 0) * mm});
            skLineSegment(sketch, "E25.1.0.20", {"start": v(0.76, 4.1) * mm, "end": v(-5.24, 4.1) * mm});
            skLineSegment(sketch, "E25.1.0.21", {"start": v(-63.12, 2) * mm, "end": v(-63.12, 0) * mm});
            skLineSegment(sketch, "E25.1.0.22", {"start": v(-8.22, 0) * mm, "end": v(-2.22, 0) * mm});
            skLineSegment(sketch, "E25.1.0.23", {"start": v(-23.54, 4.1) * mm, "end": v(-23.52, 2.1) * mm});
            skLineSegment(sketch, "E25.1.0.24", {"start": v(-60.14, 4.1) * mm, "end": v(-60.12, 2.1) * mm});
            skLineSegment(sketch, "E25.1.0.25", {"start": v(-57.12, 2) * mm, "end": v(-63.12, 2) * mm});
            skLineSegment(sketch, "E25.1.0.26", {"start": v(-54.14, 2.1) * mm, "end": v(-60.12, 2.1) * mm});
            skLineSegment(sketch, "E25.1.0.27", {"start": v(-20.52, 2) * mm, "end": v(-26.52, 2) * mm});
            skLineSegment(sketch, "E25.1.0.28", {"start": v(-51.02, 2) * mm, "end": v(-57.02, 2) * mm});
            skLineSegment(sketch, "E25.1.0.29", {"start": v(-23.64, 2.1) * mm, "end": v(-23.64, 4.1) * mm});
            skLineSegment(sketch, "E25.1.0.30", {"start": v(-57.02, 2) * mm, "end": v(-57.02, 0) * mm});
            skLineSegment(sketch, "E25.1.0.31", {"start": v(-57.12, 0) * mm, "end": v(-57.12, 2) * mm});
            skLineSegment(sketch, "E25.1.0.32", {"start": v(-17.54, 2.1) * mm, "end": v(-23.52, 2.1) * mm});
            skLineSegment(sketch, "E25.1.0.33", {"start": v(-26.62, 0) * mm, "end": v(-26.62, 2) * mm});
            skLineSegment(sketch, "E25.1.0.34", {"start": v(-48.04, 2.1) * mm, "end": v(-54.02, 2.1) * mm});
            skLineSegment(sketch, "E25.1.0.35", {"start": v(-23.64, 2.1) * mm, "end": v(-29.62, 2.1) * mm});
            skLineSegment(sketch, "E25.1.0.36", {"start": v(-17.54, 2.1) * mm, "end": v(-17.54, 4.1) * mm});
            skLineSegment(sketch, "E25.1.0.37", {"start": v(-44.92, 2) * mm, "end": v(-50.92, 2) * mm});
            skLineSegment(sketch, "E25.1.0.38", {"start": v(-14.42, 2) * mm, "end": v(-20.42, 2) * mm});
            skLineSegment(sketch, "E25.1.0.39", {"start": v(-26.62, 2) * mm, "end": v(-32.62, 2) * mm});
            skLineSegment(sketch, "E25.1.0.40", {"start": v(-48.04, 2.1) * mm, "end": v(-48.04, 4.1) * mm});
            skLineSegment(sketch, "E25.1.0.41", {"start": v(-26.52, 2) * mm, "end": v(-26.52, 0) * mm});
            skLineSegment(sketch, "E25.1.0.42", {"start": v(-41.84, 4.1) * mm, "end": v(-41.82, 2.1) * mm});
            skLineSegment(sketch, "E25.1.0.43", {"start": v(-17.44, 4.1) * mm, "end": v(-17.42, 2.1) * mm});
            skLineSegment(sketch, "E25.1.0.44", {"start": v(-50.92, 2) * mm, "end": v(-50.92, 0) * mm});
            skLineSegment(sketch, "E25.1.0.45", {"start": v(-8.32, 2) * mm, "end": v(-14.32, 2) * mm});
            skLineSegment(sketch, "E25.1.0.46", {"start": v(-20.42, 2) * mm, "end": v(-20.42, 0) * mm});
            skLineSegment(sketch, "E25.1.0.47", {"start": v(-44.82, 2) * mm, "end": v(-44.82, 0) * mm});
            skLineSegment(sketch, "E25.1.0.48", {"start": v(-2.22, 2) * mm, "end": v(-8.22, 2) * mm});
            skLineSegment(sketch, "E25.1.0.49", {"start": v(-32.62, 2) * mm, "end": v(-32.62, 0) * mm});
            skLineSegment(sketch, "E25.1.0.50", {"start": v(-47.94, 4.1) * mm, "end": v(-47.92, 2.1) * mm});
            skLineSegment(sketch, "E25.1.0.51", {"start": v(-35.84, 2.1) * mm, "end": v(-41.82, 2.1) * mm});
            skLineSegment(sketch, "E25.1.0.52", {"start": v(-11.44, 2.1) * mm, "end": v(-17.42, 2.1) * mm});
            skLineSegment(sketch, "E25.1.0.53", {"start": v(-32.72, 0) * mm, "end": v(-32.72, 2) * mm});
            skLineSegment(sketch, "E25.1.0.54", {"start": v(-11.34, 4.1) * mm, "end": v(-11.32, 2.1) * mm});
            skLineSegment(sketch, "E25.1.0.55", {"start": v(-35.74, 4.1) * mm, "end": v(-35.72, 2.1) * mm});
            skLineSegment(sketch, "E25.1.0.56", {"start": v(-14.42, 0) * mm, "end": v(-14.42, 2) * mm});
            skLineSegment(sketch, "E25.1.0.57", {"start": v(-29.74, 2.1) * mm, "end": v(-29.74, 4.1) * mm});
            skLineSegment(sketch, "E25.1.0.58", {"start": v(-41.94, 2.1) * mm, "end": v(-47.92, 2.1) * mm});
            skLineSegment(sketch, "E25.1.0.59", {"start": v(-32.72, 2) * mm, "end": v(-38.72, 2) * mm});
            skLineSegment(sketch, "E25.1.0.60", {"start": v(-38.82, 0) * mm, "end": v(-38.82, 2) * mm});
            skLineSegment(sketch, "E25.1.0.61", {"start": v(-54.14, 2.1) * mm, "end": v(-54.14, 4.1) * mm});
            skLineSegment(sketch, "E25.1.0.62", {"start": v(-8.32, 0) * mm, "end": v(-8.32, 2) * mm});
            skLineSegment(sketch, "E25.1.0.63", {"start": v(-54.04, 4.1) * mm, "end": v(-54.02, 2.1) * mm});
            skLineSegment(sketch, "E25.1.0.64", {"start": v(-29.64, 4.1) * mm, "end": v(-29.62, 2.1) * mm});
            skLineSegment(sketch, "E25.1.0.65", {"start": v(-5.34, 2.1) * mm, "end": v(-11.32, 2.1) * mm});
            skLineSegment(sketch, "E25.1.0.66", {"start": v(-51.02, 0) * mm, "end": v(-51.02, 2) * mm});
            skLineSegment(sketch, "E25.1.0.67", {"start": v(-29.74, 2.1) * mm, "end": v(-35.72, 2.1) * mm});
            skLineSegment(sketch, "E25.1.0.68", {"start": v(-44.92, 0) * mm, "end": v(-44.92, 2) * mm});
            skLineSegment(sketch, "E25.1.0.69", {"start": v(-20.52, 0) * mm, "end": v(-20.52, 2) * mm});
            skLineSegment(sketch, "E25.1.0.70", {"start": v(-41.94, 2.1) * mm, "end": v(-41.94, 4.1) * mm});
            skLineSegment(sketch, "E25.1.0.71", {"start": v(-38.72, 2) * mm, "end": v(-38.72, 0) * mm});
            skLineSegment(sketch, "E25.1.0.72", {"start": v(-35.84, 2.1) * mm, "end": v(-35.84, 4.1) * mm});
            skLineSegment(sketch, "E25.1.0.73", {"start": v(-11.44, 2.1) * mm, "end": v(-11.44, 4.1) * mm});
            skLineSegment(sketch, "E25.1.0.74", {"start": v(-38.82, 2) * mm, "end": v(-44.82, 2) * mm});
            skLineSegment(sketch, "E25.1.0.75", {"start": v(-14.32, 2) * mm, "end": v(-14.32, 0) * mm});
            skLineSegment(sketch, "E25.1.0.78", {"start": v(-2.12, 2) * mm, "end": v(-2.12, 0) * mm});
            skLineSegment(sketch, "E25.1.0.79", {"start": v(-2.22, 0) * mm, "end": v(-2.22, 2) * mm});
            skLineSegment(sketch, "E25.1.0.80", {"start": v(-8.22, 2) * mm, "end": v(-8.22, 0) * mm});
            skLineSegment(sketch, "E25.1.0.85", {"start": v(0.76, 2.1) * mm, "end": v(-5.22, 2.1) * mm});
            skLineSegment(sketch, "E25.1.0.86", {"start": v(0.86, 2.1) * mm, "end": v(0.86, 4.1) * mm});
            skLineSegment(sketch, "E25.1.0.87", {"start": v(-5.34, 2.1) * mm, "end": v(-5.34, 4.1) * mm});
            skLineSegment(sketch, "E25.1.0.88", {"start": v(-5.24, 4.1) * mm, "end": v(-5.22, 2.1) * mm});
            skLineSegment(sketch, "E25.1.0.89", {"start": v(0.76, 2.1) * mm, "end": v(0.76, 4.1) * mm});
            skLineSegment(sketch, "E25.1.0.90", {"start": v(-2.12, 0) * mm, "end": v(-2.22, 0) * mm});
            skLineSegment(sketch, "E25.1.0.91", {"start": v(0.86, 2.1) * mm, "end": v(0.76, 2.1) * mm});
            skLineSegment(sketch, "E25.1.1.0", {"start": v(-35.84, 8.32) * mm, "end": v(-41.84, 8.32) * mm});
            skLineSegment(sketch, "E25.1.1.1", {"start": v(-11.44, 8.3) * mm, "end": v(-17.44, 8.3) * mm});
            skLineSegment(sketch, "E25.1.1.2", {"start": v(-48.04, 8.32) * mm, "end": v(-54.04, 8.32) * mm});
            skLineSegment(sketch, "E25.1.1.3", {"start": v(-23.64, 8.3) * mm, "end": v(-29.64, 8.3) * mm});
            skLineSegment(sketch, "E25.1.1.4", {"start": v(-41.94, 8.32) * mm, "end": v(-47.94, 8.32) * mm});
            skLineSegment(sketch, "E25.1.1.5", {"start": v(-17.54, 8.3) * mm, "end": v(-23.54, 8.3) * mm});
            skLineSegment(sketch, "E25.1.1.6", {"start": v(-5.34, 8.3) * mm, "end": v(-11.34, 8.3) * mm});
            skLineSegment(sketch, "E25.1.1.8", {"start": v(-29.74, 8.3) * mm, "end": v(-35.74, 8.3) * mm});
            skLineSegment(sketch, "E25.1.1.9", {"start": v(-20.42, 4.2) * mm, "end": v(-14.42, 4.2) * mm});
            skLineSegment(sketch, "E25.1.1.10", {"start": v(-44.82, 4.2) * mm, "end": v(-38.82, 4.2) * mm});
            skLineSegment(sketch, "E25.1.1.11", {"start": v(-57.02, 4.2) * mm, "end": v(-51.02, 4.2) * mm});
            skLineSegment(sketch, "E25.1.1.12", {"start": v(-32.62, 4.2) * mm, "end": v(-26.62, 4.2) * mm});
            skLineSegment(sketch, "E25.1.1.13", {"start": v(-50.92, 4.2) * mm, "end": v(-44.92, 4.2) * mm});
            skLineSegment(sketch, "E25.1.1.14", {"start": v(-26.52, 4.2) * mm, "end": v(-20.52, 4.2) * mm});
            skPoint(sketch, "E25.1.1.15", {"position": v(-5.22, 6.2) * mm});
            skLineSegment(sketch, "E25.1.1.16", {"start": v(-63.12, 4.2) * mm, "end": v(-57.12, 4.2) * mm});
            skLineSegment(sketch, "E25.1.1.17", {"start": v(-38.72, 4.2) * mm, "end": v(-32.72, 4.2) * mm});
            skLineSegment(sketch, "E25.1.1.18", {"start": v(-14.32, 4.2) * mm, "end": v(-8.32, 4.2) * mm});
            skLineSegment(sketch, "E25.1.1.20", {"start": v(0.76, 8.3) * mm, "end": v(-5.24, 8.3) * mm});
            skLineSegment(sketch, "E25.1.1.21", {"start": v(-63.12, 6.2) * mm, "end": v(-63.12, 4.2) * mm});
            skLineSegment(sketch, "E25.1.1.22", {"start": v(-8.22, 4.2) * mm, "end": v(-2.22, 4.2) * mm});
            skLineSegment(sketch, "E25.1.1.23", {"start": v(-23.54, 8.3) * mm, "end": v(-23.52, 6.3) * mm});
            skLineSegment(sketch, "E25.1.1.25", {"start": v(-57.12, 6.2) * mm, "end": v(-63.12, 6.2) * mm});
            skLineSegment(sketch, "E25.1.1.27", {"start": v(-20.52, 6.2) * mm, "end": v(-26.52, 6.2) * mm});
            skLineSegment(sketch, "E25.1.1.28", {"start": v(-51.02, 6.2) * mm, "end": v(-57.02, 6.2) * mm});
            skLineSegment(sketch, "E25.1.1.29", {"start": v(-23.64, 6.3) * mm, "end": v(-23.64, 8.3) * mm});
            skLineSegment(sketch, "E25.1.1.30", {"start": v(-57.02, 6.2) * mm, "end": v(-57.02, 4.2) * mm});
            skLineSegment(sketch, "E25.1.1.31", {"start": v(-57.12, 4.2) * mm, "end": v(-57.12, 6.2) * mm});
            skLineSegment(sketch, "E25.1.1.32", {"start": v(-17.54, 6.3) * mm, "end": v(-23.52, 6.3) * mm});
            skLineSegment(sketch, "E25.1.1.33", {"start": v(-26.62, 4.2) * mm, "end": v(-26.62, 6.2) * mm});
            skLineSegment(sketch, "E25.1.1.34", {"start": v(-48.04, 6.32) * mm, "end": v(-54.02, 6.32) * mm});
            skLineSegment(sketch, "E25.1.1.35", {"start": v(-23.64, 6.3) * mm, "end": v(-29.62, 6.3) * mm});
            skLineSegment(sketch, "E25.1.1.36", {"start": v(-17.54, 6.3) * mm, "end": v(-17.54, 8.3) * mm});
            skLineSegment(sketch, "E25.1.1.37", {"start": v(-44.92, 6.2) * mm, "end": v(-50.92, 6.2) * mm});
            skLineSegment(sketch, "E25.1.1.38", {"start": v(-14.42, 6.2) * mm, "end": v(-20.42, 6.2) * mm});
            skLineSegment(sketch, "E25.1.1.39", {"start": v(-26.62, 6.2) * mm, "end": v(-32.62, 6.2) * mm});
            skLineSegment(sketch, "E25.1.1.40", {"start": v(-48.04, 6.32) * mm, "end": v(-48.04, 8.32) * mm});
            skLineSegment(sketch, "E25.1.1.41", {"start": v(-26.52, 6.2) * mm, "end": v(-26.52, 4.2) * mm});
            skLineSegment(sketch, "E25.1.1.42", {"start": v(-41.84, 8.32) * mm, "end": v(-41.82, 6.32) * mm});
            skLineSegment(sketch, "E25.1.1.43", {"start": v(-17.44, 8.3) * mm, "end": v(-17.42, 6.3) * mm});
            skLineSegment(sketch, "E25.1.1.44", {"start": v(-50.92, 6.2) * mm, "end": v(-50.92, 4.2) * mm});
            skLineSegment(sketch, "E25.1.1.45", {"start": v(-8.32, 6.2) * mm, "end": v(-14.32, 6.2) * mm});
            skLineSegment(sketch, "E25.1.1.46", {"start": v(-20.42, 6.2) * mm, "end": v(-20.42, 4.2) * mm});
            skLineSegment(sketch, "E25.1.1.47", {"start": v(-44.82, 6.2) * mm, "end": v(-44.82, 4.2) * mm});
            skLineSegment(sketch, "E25.1.1.48", {"start": v(-2.22, 6.2) * mm, "end": v(-8.22, 6.2) * mm});
            skLineSegment(sketch, "E25.1.1.49", {"start": v(-32.62, 6.2) * mm, "end": v(-32.62, 4.2) * mm});
            skLineSegment(sketch, "E25.1.1.50", {"start": v(-47.94, 8.32) * mm, "end": v(-47.92, 6.32) * mm});
            skLineSegment(sketch, "E25.1.1.51", {"start": v(-35.84, 6.32) * mm, "end": v(-41.82, 6.32) * mm});
            skLineSegment(sketch, "E25.1.1.52", {"start": v(-11.44, 6.3) * mm, "end": v(-17.42, 6.3) * mm});
            skLineSegment(sketch, "E25.1.1.53", {"start": v(-32.72, 4.2) * mm, "end": v(-32.72, 6.2) * mm});
            skLineSegment(sketch, "E25.1.1.54", {"start": v(-11.34, 8.3) * mm, "end": v(-11.32, 6.3) * mm});
            skLineSegment(sketch, "E25.1.1.55", {"start": v(-35.74, 8.3) * mm, "end": v(-35.72, 6.3) * mm});
            skLineSegment(sketch, "E25.1.1.56", {"start": v(-14.42, 4.2) * mm, "end": v(-14.42, 6.2) * mm});
            skLineSegment(sketch, "E25.1.1.57", {"start": v(-29.74, 6.3) * mm, "end": v(-29.74, 8.3) * mm});
            skLineSegment(sketch, "E25.1.1.58", {"start": v(-41.94, 6.32) * mm, "end": v(-47.92, 6.32) * mm});
            skLineSegment(sketch, "E25.1.1.59", {"start": v(-32.72, 6.2) * mm, "end": v(-38.72, 6.2) * mm});
            skLineSegment(sketch, "E25.1.1.60", {"start": v(-38.82, 4.2) * mm, "end": v(-38.82, 6.2) * mm});
            skLineSegment(sketch, "E25.1.1.62", {"start": v(-8.32, 4.2) * mm, "end": v(-8.32, 6.2) * mm});
            skLineSegment(sketch, "E25.1.1.64", {"start": v(-29.64, 8.3) * mm, "end": v(-29.62, 6.3) * mm});
            skLineSegment(sketch, "E25.1.1.65", {"start": v(-5.34, 6.3) * mm, "end": v(-11.32, 6.3) * mm});
            skLineSegment(sketch, "E25.1.1.66", {"start": v(-51.02, 4.2) * mm, "end": v(-51.02, 6.2) * mm});
            skLineSegment(sketch, "E25.1.1.67", {"start": v(-29.74, 6.3) * mm, "end": v(-35.72, 6.3) * mm});
            skLineSegment(sketch, "E25.1.1.68", {"start": v(-44.92, 4.2) * mm, "end": v(-44.92, 6.2) * mm});
            skLineSegment(sketch, "E25.1.1.69", {"start": v(-20.52, 4.2) * mm, "end": v(-20.52, 6.2) * mm});
            skLineSegment(sketch, "E25.1.1.70", {"start": v(-41.94, 6.32) * mm, "end": v(-41.94, 8.32) * mm});
            skLineSegment(sketch, "E25.1.1.71", {"start": v(-38.72, 6.2) * mm, "end": v(-38.72, 4.2) * mm});
            skLineSegment(sketch, "E25.1.1.72", {"start": v(-35.84, 6.32) * mm, "end": v(-35.84, 8.32) * mm});
            skLineSegment(sketch, "E25.1.1.73", {"start": v(-11.44, 6.3) * mm, "end": v(-11.44, 8.3) * mm});
            skLineSegment(sketch, "E25.1.1.74", {"start": v(-38.82, 6.2) * mm, "end": v(-44.82, 6.2) * mm});
            skLineSegment(sketch, "E25.1.1.75", {"start": v(-14.32, 6.2) * mm, "end": v(-14.32, 4.2) * mm});
            skLineSegment(sketch, "E25.1.1.78", {"start": v(-2.12, 6.2) * mm, "end": v(-2.12, 4.2) * mm});
            skLineSegment(sketch, "E25.1.1.79", {"start": v(-2.22, 4.2) * mm, "end": v(-2.22, 6.2) * mm});
            skLineSegment(sketch, "E25.1.1.80", {"start": v(-8.22, 6.2) * mm, "end": v(-8.22, 4.2) * mm});
            skLineSegment(sketch, "E25.1.1.81", {"start": v(0.86, 8.3) * mm, "end": v(3.88, 8.3) * mm});
            skLineSegment(sketch, "E25.1.1.84", {"start": v(3.88, 6.3) * mm, "end": v(0.86, 6.3) * mm});
            skLineSegment(sketch, "E25.1.1.85", {"start": v(0.76, 6.3) * mm, "end": v(-5.22, 6.3) * mm});
            skLineSegment(sketch, "E25.1.1.86", {"start": v(0.86, 6.3) * mm, "end": v(0.86, 8.3) * mm});
            skLineSegment(sketch, "E25.1.1.87", {"start": v(-5.34, 6.3) * mm, "end": v(-5.34, 8.3) * mm});
            skLineSegment(sketch, "E25.1.1.88", {"start": v(-5.24, 8.3) * mm, "end": v(-5.22, 6.3) * mm});
            skLineSegment(sketch, "E25.1.1.89", {"start": v(0.76, 6.3) * mm, "end": v(0.76, 8.3) * mm});
            skLineSegment(sketch, "E25.1.1.90", {"start": v(-2.12, 4.2) * mm, "end": v(-2.22, 4.2) * mm});
            skLineSegment(sketch, "E25.1.1.91", {"start": v(0.86, 6.3) * mm, "end": v(0.76, 6.3) * mm});
            skLineSegment(sketch, "E25.1.2.0", {"start": v(-35.84, 12.5) * mm, "end": v(-41.84, 12.5) * mm});
            skLineSegment(sketch, "E25.1.2.1", {"start": v(-11.44, 12.5) * mm, "end": v(-17.44, 12.5) * mm});
            skLineSegment(sketch, "E25.1.2.2", {"start": v(-48.04, 12.5) * mm, "end": v(-54.04, 12.5) * mm});
            skLineSegment(sketch, "E25.1.2.3", {"start": v(-23.64, 12.5) * mm, "end": v(-29.64, 12.5) * mm});
            skLineSegment(sketch, "E25.1.2.4", {"start": v(-41.94, 12.5) * mm, "end": v(-47.94, 12.5) * mm});
            skLineSegment(sketch, "E25.1.2.5", {"start": v(-17.54, 12.5) * mm, "end": v(-23.54, 12.5) * mm});
            skLineSegment(sketch, "E25.1.2.6", {"start": v(-5.34, 12.5) * mm, "end": v(-11.34, 12.5) * mm});
            skLineSegment(sketch, "E25.1.2.7", {"start": v(-54.14, 12.5) * mm, "end": v(-60.14, 12.5) * mm});
            skLineSegment(sketch, "E25.1.2.8", {"start": v(-29.74, 12.5) * mm, "end": v(-35.74, 12.5) * mm});
            skLineSegment(sketch, "E25.1.2.9", {"start": v(-20.42, 8.4) * mm, "end": v(-14.42, 8.4) * mm});
            skLineSegment(sketch, "E25.1.2.10", {"start": v(-44.82, 8.4) * mm, "end": v(-38.82, 8.4) * mm});
            skLineSegment(sketch, "E25.1.2.11", {"start": v(-57.02, 8.4) * mm, "end": v(-51.02, 8.4) * mm});
            skLineSegment(sketch, "E25.1.2.12", {"start": v(-32.62, 8.4) * mm, "end": v(-26.62, 8.4) * mm});
            skLineSegment(sketch, "E25.1.2.13", {"start": v(-50.92, 8.4) * mm, "end": v(-44.92, 8.4) * mm});
            skLineSegment(sketch, "E25.1.2.14", {"start": v(-26.52, 8.4) * mm, "end": v(-20.52, 8.4) * mm});
            skPoint(sketch, "E25.1.2.15", {"position": v(-5.22, 10.4) * mm});
            skLineSegment(sketch, "E25.1.2.16", {"start": v(-63.12, 8.4) * mm, "end": v(-57.12, 8.4) * mm});
            skLineSegment(sketch, "E25.1.2.17", {"start": v(-38.72, 8.4) * mm, "end": v(-32.72, 8.4) * mm});
            skLineSegment(sketch, "E25.1.2.18", {"start": v(-14.32, 8.4) * mm, "end": v(-8.32, 8.4) * mm});
            skLineSegment(sketch, "E25.1.2.19", {"start": v(-2.12, 8.4) * mm, "end": v(3.88, 8.4) * mm});
            skLineSegment(sketch, "E25.1.2.20", {"start": v(0.76, 12.5) * mm, "end": v(-5.24, 12.5) * mm});
            skLineSegment(sketch, "E25.1.2.21", {"start": v(-63.12, 10.4) * mm, "end": v(-63.12, 8.4) * mm});
            skLineSegment(sketch, "E25.1.2.22", {"start": v(-8.22, 8.4) * mm, "end": v(-2.22, 8.4) * mm});
            skLineSegment(sketch, "E25.1.2.23", {"start": v(-23.54, 12.5) * mm, "end": v(-23.52, 10.5) * mm});
            skLineSegment(sketch, "E25.1.2.24", {"start": v(-60.14, 12.5) * mm, "end": v(-60.12, 10.5) * mm});
            skLineSegment(sketch, "E25.1.2.25", {"start": v(-57.12, 10.4) * mm, "end": v(-63.12, 10.4) * mm});
            skLineSegment(sketch, "E25.1.2.26", {"start": v(-54.14, 10.5) * mm, "end": v(-60.12, 10.5) * mm});
            skLineSegment(sketch, "E25.1.2.27", {"start": v(-20.52, 10.4) * mm, "end": v(-26.52, 10.4) * mm});
            skLineSegment(sketch, "E25.1.2.28", {"start": v(-51.02, 10.4) * mm, "end": v(-57.02, 10.4) * mm});
            skLineSegment(sketch, "E25.1.2.29", {"start": v(-23.64, 10.5) * mm, "end": v(-23.64, 12.5) * mm});
            skLineSegment(sketch, "E25.1.2.30", {"start": v(-57.02, 10.4) * mm, "end": v(-57.02, 8.4) * mm});
            skLineSegment(sketch, "E25.1.2.31", {"start": v(-57.12, 8.4) * mm, "end": v(-57.12, 10.4) * mm});
            skLineSegment(sketch, "E25.1.2.32", {"start": v(-17.54, 10.5) * mm, "end": v(-23.52, 10.5) * mm});
            skLineSegment(sketch, "E25.1.2.33", {"start": v(-26.62, 8.4) * mm, "end": v(-26.62, 10.4) * mm});
            skLineSegment(sketch, "E25.1.2.34", {"start": v(-48.04, 10.5) * mm, "end": v(-54.02, 10.5) * mm});
            skLineSegment(sketch, "E25.1.2.35", {"start": v(-23.64, 10.5) * mm, "end": v(-29.62, 10.5) * mm});
            skLineSegment(sketch, "E25.1.2.36", {"start": v(-17.54, 10.5) * mm, "end": v(-17.54, 12.5) * mm});
            skLineSegment(sketch, "E25.1.2.37", {"start": v(-44.92, 10.4) * mm, "end": v(-50.92, 10.4) * mm});
            skLineSegment(sketch, "E25.1.2.38", {"start": v(-14.42, 10.4) * mm, "end": v(-20.42, 10.4) * mm});
            skLineSegment(sketch, "E25.1.2.39", {"start": v(-26.62, 10.4) * mm, "end": v(-32.62, 10.4) * mm});
            skLineSegment(sketch, "E25.1.2.40", {"start": v(-48.04, 10.5) * mm, "end": v(-48.04, 12.5) * mm});
            skLineSegment(sketch, "E25.1.2.41", {"start": v(-26.52, 10.4) * mm, "end": v(-26.52, 8.4) * mm});
            skLineSegment(sketch, "E25.1.2.42", {"start": v(-41.84, 12.5) * mm, "end": v(-41.82, 10.5) * mm});
            skLineSegment(sketch, "E25.1.2.43", {"start": v(-17.44, 12.5) * mm, "end": v(-17.42, 10.5) * mm});
            skLineSegment(sketch, "E25.1.2.44", {"start": v(-50.92, 10.4) * mm, "end": v(-50.92, 8.4) * mm});
            skLineSegment(sketch, "E25.1.2.45", {"start": v(-8.32, 10.4) * mm, "end": v(-14.32, 10.4) * mm});
            skLineSegment(sketch, "E25.1.2.46", {"start": v(-20.42, 10.4) * mm, "end": v(-20.42, 8.4) * mm});
            skLineSegment(sketch, "E25.1.2.47", {"start": v(-44.82, 10.4) * mm, "end": v(-44.82, 8.4) * mm});
            skLineSegment(sketch, "E25.1.2.48", {"start": v(-2.22, 10.4) * mm, "end": v(-8.22, 10.4) * mm});
            skLineSegment(sketch, "E25.1.2.49", {"start": v(-32.62, 10.4) * mm, "end": v(-32.62, 8.4) * mm});
            skLineSegment(sketch, "E25.1.2.50", {"start": v(-47.94, 12.5) * mm, "end": v(-47.92, 10.5) * mm});
            skLineSegment(sketch, "E25.1.2.51", {"start": v(-35.84, 10.5) * mm, "end": v(-41.82, 10.5) * mm});
            skLineSegment(sketch, "E25.1.2.52", {"start": v(-11.44, 10.5) * mm, "end": v(-17.42, 10.5) * mm});
            skLineSegment(sketch, "E25.1.2.53", {"start": v(-32.72, 8.4) * mm, "end": v(-32.72, 10.4) * mm});
            skLineSegment(sketch, "E25.1.2.54", {"start": v(-11.34, 12.5) * mm, "end": v(-11.32, 10.5) * mm});
            skLineSegment(sketch, "E25.1.2.55", {"start": v(-35.74, 12.5) * mm, "end": v(-35.72, 10.5) * mm});
            skLineSegment(sketch, "E25.1.2.56", {"start": v(-14.42, 8.4) * mm, "end": v(-14.42, 10.4) * mm});
            skLineSegment(sketch, "E25.1.2.57", {"start": v(-29.74, 10.5) * mm, "end": v(-29.74, 12.5) * mm});
            skLineSegment(sketch, "E25.1.2.58", {"start": v(-41.94, 10.5) * mm, "end": v(-47.92, 10.5) * mm});
            skLineSegment(sketch, "E25.1.2.59", {"start": v(-32.72, 10.4) * mm, "end": v(-38.72, 10.4) * mm});
            skLineSegment(sketch, "E25.1.2.60", {"start": v(-38.82, 8.4) * mm, "end": v(-38.82, 10.4) * mm});
            skLineSegment(sketch, "E25.1.2.61", {"start": v(-54.14, 10.5) * mm, "end": v(-54.14, 12.5) * mm});
            skLineSegment(sketch, "E25.1.2.62", {"start": v(-8.32, 8.4) * mm, "end": v(-8.32, 10.4) * mm});
            skLineSegment(sketch, "E25.1.2.63", {"start": v(-54.04, 12.5) * mm, "end": v(-54.02, 10.5) * mm});
            skLineSegment(sketch, "E25.1.2.64", {"start": v(-29.64, 12.5) * mm, "end": v(-29.62, 10.5) * mm});
            skLineSegment(sketch, "E25.1.2.65", {"start": v(-5.34, 10.5) * mm, "end": v(-11.32, 10.5) * mm});
            skLineSegment(sketch, "E25.1.2.66", {"start": v(-51.02, 8.4) * mm, "end": v(-51.02, 10.4) * mm});
            skLineSegment(sketch, "E25.1.2.67", {"start": v(-29.74, 10.5) * mm, "end": v(-35.72, 10.5) * mm});
            skLineSegment(sketch, "E25.1.2.68", {"start": v(-44.92, 8.4) * mm, "end": v(-44.92, 10.4) * mm});
            skLineSegment(sketch, "E25.1.2.69", {"start": v(-20.52, 8.4) * mm, "end": v(-20.52, 10.4) * mm});
            skLineSegment(sketch, "E25.1.2.70", {"start": v(-41.94, 10.5) * mm, "end": v(-41.94, 12.5) * mm});
            skLineSegment(sketch, "E25.1.2.71", {"start": v(-38.72, 10.4) * mm, "end": v(-38.72, 8.4) * mm});
            skLineSegment(sketch, "E25.1.2.72", {"start": v(-35.84, 10.5) * mm, "end": v(-35.84, 12.5) * mm});
            skLineSegment(sketch, "E25.1.2.73", {"start": v(-11.44, 10.5) * mm, "end": v(-11.44, 12.5) * mm});
            skLineSegment(sketch, "E25.1.2.74", {"start": v(-38.82, 10.4) * mm, "end": v(-44.82, 10.4) * mm});
            skLineSegment(sketch, "E25.1.2.75", {"start": v(-14.32, 10.4) * mm, "end": v(-14.32, 8.4) * mm});
            skLineSegment(sketch, "E25.1.2.76", {"start": v(3.88, 8.4) * mm, "end": v(3.88, 10.4) * mm});
            skLineSegment(sketch, "E25.1.2.77", {"start": v(3.88, 10.4) * mm, "end": v(-2.12, 10.4) * mm});
            skLineSegment(sketch, "E25.1.2.78", {"start": v(-2.12, 10.4) * mm, "end": v(-2.12, 8.4) * mm});
            skLineSegment(sketch, "E25.1.2.79", {"start": v(-2.22, 8.4) * mm, "end": v(-2.22, 10.4) * mm});
            skLineSegment(sketch, "E25.1.2.80", {"start": v(-8.22, 10.4) * mm, "end": v(-8.22, 8.4) * mm});
            skLineSegment(sketch, "E25.1.2.81", {"start": v(0.86, 12.5) * mm, "end": v(3.88, 12.5) * mm});
            skLineSegment(sketch, "E25.1.2.84", {"start": v(3.88, 10.5) * mm, "end": v(0.86, 10.5) * mm});
            skLineSegment(sketch, "E25.1.2.85", {"start": v(0.76, 10.5) * mm, "end": v(-5.22, 10.5) * mm});
            skLineSegment(sketch, "E25.1.2.86", {"start": v(0.86, 10.5) * mm, "end": v(0.86, 12.5) * mm});
            skLineSegment(sketch, "E25.1.2.87", {"start": v(-5.34, 10.5) * mm, "end": v(-5.34, 12.5) * mm});
            skLineSegment(sketch, "E25.1.2.88", {"start": v(-5.24, 12.5) * mm, "end": v(-5.22, 10.5) * mm});
            skLineSegment(sketch, "E25.1.2.89", {"start": v(0.76, 10.5) * mm, "end": v(0.76, 12.5) * mm});
            skLineSegment(sketch, "E25.1.2.90", {"start": v(-2.12, 8.4) * mm, "end": v(-2.22, 8.4) * mm});
            skLineSegment(sketch, "E25.1.2.91", {"start": v(0.86, 10.5) * mm, "end": v(0.76, 10.5) * mm});
            skLineSegment(sketch, "E25.1.3.0", {"start": v(-35.84, 16.7) * mm, "end": v(-41.84, 16.7) * mm});
            skLineSegment(sketch, "E25.1.3.1", {"start": v(-11.44, 16.7) * mm, "end": v(-17.44, 16.7) * mm});
            skLineSegment(sketch, "E25.1.3.2", {"start": v(-48.04, 16.7) * mm, "end": v(-54.04, 16.7) * mm});
            skLineSegment(sketch, "E25.1.3.3", {"start": v(-23.64, 16.7) * mm, "end": v(-29.64, 16.7) * mm});
            skLineSegment(sketch, "E25.1.3.4", {"start": v(-41.94, 16.7) * mm, "end": v(-47.94, 16.7) * mm});
            skLineSegment(sketch, "E25.1.3.5", {"start": v(-17.54, 16.7) * mm, "end": v(-23.54, 16.7) * mm});
            skLineSegment(sketch, "E25.1.3.6", {"start": v(-5.34, 16.7) * mm, "end": v(-11.34, 16.7) * mm});
            skLineSegment(sketch, "E25.1.3.7", {"start": v(-54.14, 16.7) * mm, "end": v(-60.14, 16.7) * mm});
            skLineSegment(sketch, "E25.1.3.8", {"start": v(-29.74, 16.7) * mm, "end": v(-35.74, 16.7) * mm});
            skLineSegment(sketch, "E25.1.3.9", {"start": v(-20.42, 12.6) * mm, "end": v(-14.42, 12.6) * mm});
            skLineSegment(sketch, "E25.1.3.10", {"start": v(-44.82, 12.6) * mm, "end": v(-38.82, 12.6) * mm});
            skLineSegment(sketch, "E25.1.3.11", {"start": v(-57.02, 12.6) * mm, "end": v(-51.02, 12.6) * mm});
            skLineSegment(sketch, "E25.1.3.12", {"start": v(-32.62, 12.6) * mm, "end": v(-26.62, 12.6) * mm});
            skLineSegment(sketch, "E25.1.3.13", {"start": v(-50.92, 12.6) * mm, "end": v(-44.92, 12.6) * mm});
            skLineSegment(sketch, "E25.1.3.14", {"start": v(-26.52, 12.6) * mm, "end": v(-20.52, 12.6) * mm});
            skPoint(sketch, "E25.1.3.15", {"position": v(-5.22, 14.6) * mm});
            skLineSegment(sketch, "E25.1.3.16", {"start": v(-63.12, 12.6) * mm, "end": v(-57.12, 12.6) * mm});
            skLineSegment(sketch, "E25.1.3.17", {"start": v(-38.72, 12.6) * mm, "end": v(-32.72, 12.6) * mm});
            skLineSegment(sketch, "E25.1.3.18", {"start": v(-14.32, 12.6) * mm, "end": v(-8.32, 12.6) * mm});
            skLineSegment(sketch, "E25.1.3.19", {"start": v(-2.12, 12.6) * mm, "end": v(3.88, 12.6) * mm});
            skLineSegment(sketch, "E25.1.3.20", {"start": v(0.76, 16.7) * mm, "end": v(-5.24, 16.7) * mm});
            skLineSegment(sketch, "E25.1.3.21", {"start": v(-63.12, 14.6) * mm, "end": v(-63.12, 12.6) * mm});
            skLineSegment(sketch, "E25.1.3.22", {"start": v(-8.22, 12.6) * mm, "end": v(-2.22, 12.6) * mm});
            skLineSegment(sketch, "E25.1.3.23", {"start": v(-23.54, 16.7) * mm, "end": v(-23.52, 14.7) * mm});
            skLineSegment(sketch, "E25.1.3.24", {"start": v(-60.14, 16.7) * mm, "end": v(-60.12, 14.7) * mm});
            skLineSegment(sketch, "E25.1.3.25", {"start": v(-57.12, 14.6) * mm, "end": v(-63.12, 14.6) * mm});
            skLineSegment(sketch, "E25.1.3.26", {"start": v(-54.14, 14.7) * mm, "end": v(-60.12, 14.7) * mm});
            skLineSegment(sketch, "E25.1.3.27", {"start": v(-20.52, 14.6) * mm, "end": v(-26.52, 14.6) * mm});
            skLineSegment(sketch, "E25.1.3.28", {"start": v(-51.02, 14.6) * mm, "end": v(-57.02, 14.6) * mm});
            skLineSegment(sketch, "E25.1.3.29", {"start": v(-23.64, 14.7) * mm, "end": v(-23.64, 16.7) * mm});
            skLineSegment(sketch, "E25.1.3.30", {"start": v(-57.02, 14.6) * mm, "end": v(-57.02, 12.6) * mm});
            skLineSegment(sketch, "E25.1.3.31", {"start": v(-57.12, 12.6) * mm, "end": v(-57.12, 14.6) * mm});
            skLineSegment(sketch, "E25.1.3.32", {"start": v(-17.54, 14.7) * mm, "end": v(-23.52, 14.7) * mm});
            skLineSegment(sketch, "E25.1.3.33", {"start": v(-26.62, 12.6) * mm, "end": v(-26.62, 14.6) * mm});
            skLineSegment(sketch, "E25.1.3.34", {"start": v(-48.04, 14.7) * mm, "end": v(-54.02, 14.7) * mm});
            skLineSegment(sketch, "E25.1.3.35", {"start": v(-23.64, 14.7) * mm, "end": v(-29.62, 14.7) * mm});
            skLineSegment(sketch, "E25.1.3.36", {"start": v(-17.54, 14.7) * mm, "end": v(-17.54, 16.7) * mm});
            skLineSegment(sketch, "E25.1.3.37", {"start": v(-44.92, 14.6) * mm, "end": v(-50.92, 14.6) * mm});
            skLineSegment(sketch, "E25.1.3.38", {"start": v(-14.42, 14.6) * mm, "end": v(-20.42, 14.6) * mm});
            skLineSegment(sketch, "E25.1.3.39", {"start": v(-26.62, 14.6) * mm, "end": v(-32.62, 14.6) * mm});
            skLineSegment(sketch, "E25.1.3.40", {"start": v(-48.04, 14.7) * mm, "end": v(-48.04, 16.7) * mm});
            skLineSegment(sketch, "E25.1.3.41", {"start": v(-26.52, 14.6) * mm, "end": v(-26.52, 12.6) * mm});
            skLineSegment(sketch, "E25.1.3.42", {"start": v(-41.84, 16.7) * mm, "end": v(-41.82, 14.7) * mm});
            skLineSegment(sketch, "E25.1.3.43", {"start": v(-17.44, 16.7) * mm, "end": v(-17.42, 14.7) * mm});
            skLineSegment(sketch, "E25.1.3.44", {"start": v(-50.92, 14.6) * mm, "end": v(-50.92, 12.6) * mm});
            skLineSegment(sketch, "E25.1.3.45", {"start": v(-8.32, 14.6) * mm, "end": v(-14.32, 14.6) * mm});
            skLineSegment(sketch, "E25.1.3.46", {"start": v(-20.42, 14.6) * mm, "end": v(-20.42, 12.6) * mm});
            skLineSegment(sketch, "E25.1.3.47", {"start": v(-44.82, 14.6) * mm, "end": v(-44.82, 12.6) * mm});
            skLineSegment(sketch, "E25.1.3.48", {"start": v(-2.22, 14.6) * mm, "end": v(-8.22, 14.6) * mm});
            skLineSegment(sketch, "E25.1.3.49", {"start": v(-32.62, 14.6) * mm, "end": v(-32.62, 12.6) * mm});
            skLineSegment(sketch, "E25.1.3.50", {"start": v(-47.94, 16.7) * mm, "end": v(-47.92, 14.7) * mm});
            skLineSegment(sketch, "E25.1.3.51", {"start": v(-35.84, 14.7) * mm, "end": v(-41.82, 14.7) * mm});
            skLineSegment(sketch, "E25.1.3.52", {"start": v(-11.44, 14.7) * mm, "end": v(-17.42, 14.7) * mm});
            skLineSegment(sketch, "E25.1.3.53", {"start": v(-32.72, 12.6) * mm, "end": v(-32.72, 14.6) * mm});
            skLineSegment(sketch, "E25.1.3.54", {"start": v(-11.34, 16.7) * mm, "end": v(-11.32, 14.7) * mm});
            skLineSegment(sketch, "E25.1.3.55", {"start": v(-35.74, 16.7) * mm, "end": v(-35.72, 14.7) * mm});
            skLineSegment(sketch, "E25.1.3.56", {"start": v(-14.42, 12.6) * mm, "end": v(-14.42, 14.6) * mm});
            skLineSegment(sketch, "E25.1.3.57", {"start": v(-29.74, 14.7) * mm, "end": v(-29.74, 16.7) * mm});
            skLineSegment(sketch, "E25.1.3.58", {"start": v(-41.94, 14.7) * mm, "end": v(-47.92, 14.7) * mm});
            skLineSegment(sketch, "E25.1.3.59", {"start": v(-32.72, 14.6) * mm, "end": v(-38.72, 14.6) * mm});
            skLineSegment(sketch, "E25.1.3.60", {"start": v(-38.82, 12.6) * mm, "end": v(-38.82, 14.6) * mm});
            skLineSegment(sketch, "E25.1.3.61", {"start": v(-54.14, 14.7) * mm, "end": v(-54.14, 16.7) * mm});
            skLineSegment(sketch, "E25.1.3.62", {"start": v(-8.32, 12.6) * mm, "end": v(-8.32, 14.6) * mm});
            skLineSegment(sketch, "E25.1.3.63", {"start": v(-54.04, 16.7) * mm, "end": v(-54.02, 14.7) * mm});
            skLineSegment(sketch, "E25.1.3.64", {"start": v(-29.64, 16.7) * mm, "end": v(-29.62, 14.7) * mm});
            skLineSegment(sketch, "E25.1.3.65", {"start": v(-5.34, 14.7) * mm, "end": v(-11.32, 14.7) * mm});
            skLineSegment(sketch, "E25.1.3.66", {"start": v(-51.02, 12.6) * mm, "end": v(-51.02, 14.6) * mm});
            skLineSegment(sketch, "E25.1.3.67", {"start": v(-29.74, 14.7) * mm, "end": v(-35.72, 14.7) * mm});
            skLineSegment(sketch, "E25.1.3.68", {"start": v(-44.92, 12.6) * mm, "end": v(-44.92, 14.6) * mm});
            skLineSegment(sketch, "E25.1.3.69", {"start": v(-20.52, 12.6) * mm, "end": v(-20.52, 14.6) * mm});
            skLineSegment(sketch, "E25.1.3.70", {"start": v(-41.94, 14.7) * mm, "end": v(-41.94, 16.7) * mm});
            skLineSegment(sketch, "E25.1.3.71", {"start": v(-38.72, 14.6) * mm, "end": v(-38.72, 12.6) * mm});
            skLineSegment(sketch, "E25.1.3.72", {"start": v(-35.84, 14.7) * mm, "end": v(-35.84, 16.7) * mm});
            skLineSegment(sketch, "E25.1.3.73", {"start": v(-11.44, 14.7) * mm, "end": v(-11.44, 16.7) * mm});
            skLineSegment(sketch, "E25.1.3.74", {"start": v(-38.82, 14.6) * mm, "end": v(-44.82, 14.6) * mm});
            skLineSegment(sketch, "E25.1.3.75", {"start": v(-14.32, 14.6) * mm, "end": v(-14.32, 12.6) * mm});
            skLineSegment(sketch, "E25.1.3.76", {"start": v(3.88, 12.6) * mm, "end": v(3.88, 14.6) * mm});
            skLineSegment(sketch, "E25.1.3.77", {"start": v(3.88, 14.6) * mm, "end": v(-2.12, 14.6) * mm});
            skLineSegment(sketch, "E25.1.3.78", {"start": v(-2.12, 14.6) * mm, "end": v(-2.12, 12.6) * mm});
            skLineSegment(sketch, "E25.1.3.79", {"start": v(-2.22, 12.6) * mm, "end": v(-2.22, 14.6) * mm});
            skLineSegment(sketch, "E25.1.3.80", {"start": v(-8.22, 14.6) * mm, "end": v(-8.22, 12.6) * mm});
            skLineSegment(sketch, "E25.1.3.81", {"start": v(0.86, 16.7) * mm, "end": v(3.88, 16.7) * mm});
            skLineSegment(sketch, "E25.1.3.84", {"start": v(3.88, 14.7) * mm, "end": v(0.86, 14.7) * mm});
            skLineSegment(sketch, "E25.1.3.85", {"start": v(0.76, 14.7) * mm, "end": v(-5.22, 14.7) * mm});
            skLineSegment(sketch, "E25.1.3.86", {"start": v(0.86, 14.7) * mm, "end": v(0.86, 16.7) * mm});
            skLineSegment(sketch, "E25.1.3.87", {"start": v(-5.34, 14.7) * mm, "end": v(-5.34, 16.7) * mm});
            skLineSegment(sketch, "E25.1.3.88", {"start": v(-5.24, 16.7) * mm, "end": v(-5.22, 14.7) * mm});
            skLineSegment(sketch, "E25.1.3.89", {"start": v(0.76, 14.7) * mm, "end": v(0.76, 16.7) * mm});
            skLineSegment(sketch, "E25.1.3.90", {"start": v(-2.12, 12.6) * mm, "end": v(-2.22, 12.6) * mm});
            skLineSegment(sketch, "E25.1.3.91", {"start": v(0.86, 14.7) * mm, "end": v(0.76, 14.7) * mm});
            skLineSegment(sketch, "E25.1.4.0", {"start": v(-35.84, 20.9) * mm, "end": v(-41.84, 20.9) * mm});
            skLineSegment(sketch, "E25.1.4.1", {"start": v(-11.44, 20.9) * mm, "end": v(-17.44, 20.9) * mm});
            skLineSegment(sketch, "E25.1.4.2", {"start": v(-48.04, 20.9) * mm, "end": v(-54.04, 20.9) * mm});
            skLineSegment(sketch, "E25.1.4.3", {"start": v(-23.64, 20.9) * mm, "end": v(-29.64, 20.9) * mm});
            skLineSegment(sketch, "E25.1.4.4", {"start": v(-41.94, 20.9) * mm, "end": v(-47.94, 20.9) * mm});
            skLineSegment(sketch, "E25.1.4.5", {"start": v(-17.54, 20.9) * mm, "end": v(-23.54, 20.9) * mm});
            skLineSegment(sketch, "E25.1.4.6", {"start": v(-5.34, 20.9) * mm, "end": v(-11.34, 20.9) * mm});
            skLineSegment(sketch, "E25.1.4.7", {"start": v(-54.14, 20.9) * mm, "end": v(-60.14, 20.9) * mm});
            skLineSegment(sketch, "E25.1.4.8", {"start": v(-29.74, 20.9) * mm, "end": v(-35.74, 20.9) * mm});
            skLineSegment(sketch, "E25.1.4.9", {"start": v(-20.42, 16.8) * mm, "end": v(-14.42, 16.8) * mm});
            skLineSegment(sketch, "E25.1.4.10", {"start": v(-44.82, 16.8) * mm, "end": v(-38.82, 16.8) * mm});
            skLineSegment(sketch, "E25.1.4.11", {"start": v(-57.02, 16.8) * mm, "end": v(-51.02, 16.8) * mm});
            skLineSegment(sketch, "E25.1.4.12", {"start": v(-32.62, 16.8) * mm, "end": v(-26.62, 16.8) * mm});
            skLineSegment(sketch, "E25.1.4.13", {"start": v(-50.92, 16.8) * mm, "end": v(-44.92, 16.8) * mm});
            skLineSegment(sketch, "E25.1.4.14", {"start": v(-26.52, 16.8) * mm, "end": v(-20.52, 16.8) * mm});
            skPoint(sketch, "E25.1.4.15", {"position": v(-5.22, 18.8) * mm});
            skLineSegment(sketch, "E25.1.4.16", {"start": v(-63.12, 16.8) * mm, "end": v(-57.12, 16.8) * mm});
            skLineSegment(sketch, "E25.1.4.17", {"start": v(-38.72, 16.8) * mm, "end": v(-32.72, 16.8) * mm});
            skLineSegment(sketch, "E25.1.4.18", {"start": v(-14.32, 16.8) * mm, "end": v(-8.32, 16.8) * mm});
            skLineSegment(sketch, "E25.1.4.20", {"start": v(0.76, 20.9) * mm, "end": v(-5.24, 20.9) * mm});
            skLineSegment(sketch, "E25.1.4.21", {"start": v(-63.12, 18.8) * mm, "end": v(-63.12, 16.8) * mm});
            skLineSegment(sketch, "E25.1.4.22", {"start": v(-8.22, 16.8) * mm, "end": v(-2.22, 16.8) * mm});
            skLineSegment(sketch, "E25.1.4.23", {"start": v(-23.54, 20.9) * mm, "end": v(-23.52, 18.9) * mm});
            skLineSegment(sketch, "E25.1.4.24", {"start": v(-60.14, 20.9) * mm, "end": v(-60.12, 18.9) * mm});
            skLineSegment(sketch, "E25.1.4.25", {"start": v(-57.12, 18.8) * mm, "end": v(-63.12, 18.8) * mm});
            skLineSegment(sketch, "E25.1.4.26", {"start": v(-54.14, 18.9) * mm, "end": v(-60.12, 18.9) * mm});
            skLineSegment(sketch, "E25.1.4.27", {"start": v(-20.52, 18.8) * mm, "end": v(-26.52, 18.8) * mm});
            skLineSegment(sketch, "E25.1.4.28", {"start": v(-51.02, 18.8) * mm, "end": v(-57.02, 18.8) * mm});
            skLineSegment(sketch, "E25.1.4.29", {"start": v(-23.64, 18.9) * mm, "end": v(-23.64, 20.9) * mm});
            skLineSegment(sketch, "E25.1.4.30", {"start": v(-57.02, 18.8) * mm, "end": v(-57.02, 16.8) * mm});
            skLineSegment(sketch, "E25.1.4.31", {"start": v(-57.12, 16.8) * mm, "end": v(-57.12, 18.8) * mm});
            skLineSegment(sketch, "E25.1.4.32", {"start": v(-17.54, 18.9) * mm, "end": v(-23.52, 18.9) * mm});
            skLineSegment(sketch, "E25.1.4.33", {"start": v(-26.62, 16.8) * mm, "end": v(-26.62, 18.8) * mm});
            skLineSegment(sketch, "E25.1.4.34", {"start": v(-48.04, 18.9) * mm, "end": v(-54.02, 18.9) * mm});
            skLineSegment(sketch, "E25.1.4.35", {"start": v(-23.64, 18.9) * mm, "end": v(-29.62, 18.9) * mm});
            skLineSegment(sketch, "E25.1.4.36", {"start": v(-17.54, 18.9) * mm, "end": v(-17.54, 20.9) * mm});
            skLineSegment(sketch, "E25.1.4.37", {"start": v(-44.92, 18.8) * mm, "end": v(-50.92, 18.8) * mm});
            skLineSegment(sketch, "E25.1.4.38", {"start": v(-14.42, 18.8) * mm, "end": v(-20.42, 18.8) * mm});
            skLineSegment(sketch, "E25.1.4.39", {"start": v(-26.62, 18.8) * mm, "end": v(-32.62, 18.8) * mm});
            skLineSegment(sketch, "E25.1.4.40", {"start": v(-48.04, 18.9) * mm, "end": v(-48.04, 20.9) * mm});
            skLineSegment(sketch, "E25.1.4.41", {"start": v(-26.52, 18.8) * mm, "end": v(-26.52, 16.8) * mm});
            skLineSegment(sketch, "E25.1.4.42", {"start": v(-41.84, 20.9) * mm, "end": v(-41.82, 18.9) * mm});
            skLineSegment(sketch, "E25.1.4.43", {"start": v(-17.44, 20.9) * mm, "end": v(-17.42, 18.9) * mm});
            skLineSegment(sketch, "E25.1.4.44", {"start": v(-50.92, 18.8) * mm, "end": v(-50.92, 16.8) * mm});
            skLineSegment(sketch, "E25.1.4.45", {"start": v(-8.32, 18.8) * mm, "end": v(-14.32, 18.8) * mm});
            skLineSegment(sketch, "E25.1.4.46", {"start": v(-20.42, 18.8) * mm, "end": v(-20.42, 16.8) * mm});
            skLineSegment(sketch, "E25.1.4.47", {"start": v(-44.82, 18.8) * mm, "end": v(-44.82, 16.8) * mm});
            skLineSegment(sketch, "E25.1.4.48", {"start": v(-2.22, 18.8) * mm, "end": v(-8.22, 18.8) * mm});
            skLineSegment(sketch, "E25.1.4.49", {"start": v(-32.62, 18.8) * mm, "end": v(-32.62, 16.8) * mm});
            skLineSegment(sketch, "E25.1.4.50", {"start": v(-47.94, 20.9) * mm, "end": v(-47.92, 18.9) * mm});
            skLineSegment(sketch, "E25.1.4.51", {"start": v(-35.84, 18.9) * mm, "end": v(-41.82, 18.9) * mm});
            skLineSegment(sketch, "E25.1.4.52", {"start": v(-11.44, 18.9) * mm, "end": v(-17.42, 18.9) * mm});
            skLineSegment(sketch, "E25.1.4.53", {"start": v(-32.72, 16.8) * mm, "end": v(-32.72, 18.8) * mm});
            skLineSegment(sketch, "E25.1.4.54", {"start": v(-11.34, 20.9) * mm, "end": v(-11.32, 18.9) * mm});
            skLineSegment(sketch, "E25.1.4.55", {"start": v(-35.74, 20.9) * mm, "end": v(-35.72, 18.9) * mm});
            skLineSegment(sketch, "E25.1.4.56", {"start": v(-14.42, 16.8) * mm, "end": v(-14.42, 18.8) * mm});
            skLineSegment(sketch, "E25.1.4.57", {"start": v(-29.74, 18.9) * mm, "end": v(-29.74, 20.9) * mm});
            skLineSegment(sketch, "E25.1.4.58", {"start": v(-41.94, 18.9) * mm, "end": v(-47.92, 18.9) * mm});
            skLineSegment(sketch, "E25.1.4.59", {"start": v(-32.72, 18.8) * mm, "end": v(-38.72, 18.8) * mm});
            skLineSegment(sketch, "E25.1.4.60", {"start": v(-38.82, 16.8) * mm, "end": v(-38.82, 18.8) * mm});
            skLineSegment(sketch, "E25.1.4.61", {"start": v(-54.14, 18.9) * mm, "end": v(-54.14, 20.9) * mm});
            skLineSegment(sketch, "E25.1.4.62", {"start": v(-8.32, 16.8) * mm, "end": v(-8.32, 18.8) * mm});
            skLineSegment(sketch, "E25.1.4.63", {"start": v(-54.04, 20.9) * mm, "end": v(-54.02, 18.9) * mm});
            skLineSegment(sketch, "E25.1.4.64", {"start": v(-29.64, 20.9) * mm, "end": v(-29.62, 18.9) * mm});
            skLineSegment(sketch, "E25.1.4.65", {"start": v(-5.34, 18.9) * mm, "end": v(-11.32, 18.9) * mm});
            skLineSegment(sketch, "E25.1.4.66", {"start": v(-51.02, 16.8) * mm, "end": v(-51.02, 18.8) * mm});
            skLineSegment(sketch, "E25.1.4.67", {"start": v(-29.74, 18.9) * mm, "end": v(-35.72, 18.9) * mm});
            skLineSegment(sketch, "E25.1.4.68", {"start": v(-44.92, 16.8) * mm, "end": v(-44.92, 18.8) * mm});
            skLineSegment(sketch, "E25.1.4.69", {"start": v(-20.52, 16.8) * mm, "end": v(-20.52, 18.8) * mm});
            skLineSegment(sketch, "E25.1.4.70", {"start": v(-41.94, 18.9) * mm, "end": v(-41.94, 20.9) * mm});
            skLineSegment(sketch, "E25.1.4.71", {"start": v(-38.72, 18.8) * mm, "end": v(-38.72, 16.8) * mm});
            skLineSegment(sketch, "E25.1.4.72", {"start": v(-35.84, 18.9) * mm, "end": v(-35.84, 20.9) * mm});
            skLineSegment(sketch, "E25.1.4.73", {"start": v(-11.44, 18.9) * mm, "end": v(-11.44, 20.9) * mm});
            skLineSegment(sketch, "E25.1.4.74", {"start": v(-38.82, 18.8) * mm, "end": v(-44.82, 18.8) * mm});
            skLineSegment(sketch, "E25.1.4.75", {"start": v(-14.32, 18.8) * mm, "end": v(-14.32, 16.8) * mm});
            skLineSegment(sketch, "E25.1.4.78", {"start": v(-2.12, 18.8) * mm, "end": v(-2.12, 16.8) * mm});
            skLineSegment(sketch, "E25.1.4.79", {"start": v(-2.22, 16.8) * mm, "end": v(-2.22, 18.8) * mm});
            skLineSegment(sketch, "E25.1.4.80", {"start": v(-8.22, 18.8) * mm, "end": v(-8.22, 16.8) * mm});
            skLineSegment(sketch, "E25.1.4.81", {"start": v(0.86, 20.9) * mm, "end": v(3.88, 20.9) * mm});
            skLineSegment(sketch, "E25.1.4.84", {"start": v(3.88, 18.9) * mm, "end": v(0.86, 18.9) * mm});
            skLineSegment(sketch, "E25.1.4.85", {"start": v(0.76, 18.9) * mm, "end": v(-5.22, 18.9) * mm});
            skLineSegment(sketch, "E25.1.4.86", {"start": v(0.86, 18.9) * mm, "end": v(0.86, 20.9) * mm});
            skLineSegment(sketch, "E25.1.4.87", {"start": v(-5.34, 18.9) * mm, "end": v(-5.34, 20.9) * mm});
            skLineSegment(sketch, "E25.1.4.88", {"start": v(-5.24, 20.9) * mm, "end": v(-5.22, 18.9) * mm});
            skLineSegment(sketch, "E25.1.4.89", {"start": v(0.76, 18.9) * mm, "end": v(0.76, 20.9) * mm});
            skLineSegment(sketch, "E25.1.4.90", {"start": v(-2.12, 16.8) * mm, "end": v(-2.22, 16.8) * mm});
            skLineSegment(sketch, "E25.1.4.91", {"start": v(0.86, 18.9) * mm, "end": v(0.76, 18.9) * mm});
            skLineSegment(sketch, "E25.1.5.0", {"start": v(-35.84, 25.1) * mm, "end": v(-41.84, 25.1) * mm});
            skLineSegment(sketch, "E25.1.5.1", {"start": v(-11.44, 25.1) * mm, "end": v(-17.44, 25.1) * mm});
            skLineSegment(sketch, "E25.1.5.2", {"start": v(-48.04, 25.1) * mm, "end": v(-54.04, 25.1) * mm});
            skLineSegment(sketch, "E25.1.5.3", {"start": v(-23.64, 25.1) * mm, "end": v(-29.64, 25.1) * mm});
            skLineSegment(sketch, "E25.1.5.4", {"start": v(-41.94, 25.1) * mm, "end": v(-47.94, 25.1) * mm});
            skLineSegment(sketch, "E25.1.5.5", {"start": v(-17.54, 25.1) * mm, "end": v(-23.54, 25.1) * mm});
            skLineSegment(sketch, "E25.1.5.6", {"start": v(-5.34, 25.1) * mm, "end": v(-11.34, 25.1) * mm});
            skLineSegment(sketch, "E25.1.5.7", {"start": v(-54.14, 25.1) * mm, "end": v(-60.14, 25.1) * mm});
            skLineSegment(sketch, "E25.1.5.8", {"start": v(-29.74, 25.1) * mm, "end": v(-35.74, 25.1) * mm});
            skLineSegment(sketch, "E25.1.5.9", {"start": v(-20.42, 21) * mm, "end": v(-14.42, 21) * mm});
            skLineSegment(sketch, "E25.1.5.10", {"start": v(-44.82, 21) * mm, "end": v(-38.82, 21) * mm});
            skLineSegment(sketch, "E25.1.5.11", {"start": v(-57.02, 21) * mm, "end": v(-51.02, 21) * mm});
            skLineSegment(sketch, "E25.1.5.12", {"start": v(-32.62, 21) * mm, "end": v(-26.62, 21) * mm});
            skLineSegment(sketch, "E25.1.5.13", {"start": v(-50.92, 21) * mm, "end": v(-44.92, 21) * mm});
            skLineSegment(sketch, "E25.1.5.14", {"start": v(-26.52, 21) * mm, "end": v(-20.52, 21) * mm});
            skPoint(sketch, "E25.1.5.15", {"position": v(-5.22, 23) * mm});
            skLineSegment(sketch, "E25.1.5.16", {"start": v(-63.12, 21) * mm, "end": v(-57.12, 21) * mm});
            skLineSegment(sketch, "E25.1.5.17", {"start": v(-38.72, 21) * mm, "end": v(-32.72, 21) * mm});
            skLineSegment(sketch, "E25.1.5.18", {"start": v(-14.32, 21) * mm, "end": v(-8.32, 21) * mm});
            skLineSegment(sketch, "E25.1.5.19", {"start": v(-2.12, 21) * mm, "end": v(3.88, 21) * mm});
            skLineSegment(sketch, "E25.1.5.20", {"start": v(0.76, 25.1) * mm, "end": v(-5.24, 25.1) * mm});
            skLineSegment(sketch, "E25.1.5.21", {"start": v(-63.12, 23) * mm, "end": v(-63.12, 21) * mm});
            skLineSegment(sketch, "E25.1.5.22", {"start": v(-8.22, 21) * mm, "end": v(-2.22, 21) * mm});
            skLineSegment(sketch, "E25.1.5.23", {"start": v(-23.54, 25.1) * mm, "end": v(-23.52, 23.1) * mm});
            skLineSegment(sketch, "E25.1.5.24", {"start": v(-60.14, 25.1) * mm, "end": v(-60.12, 23.1) * mm});
            skLineSegment(sketch, "E25.1.5.25", {"start": v(-57.12, 23) * mm, "end": v(-63.12, 23) * mm});
            skLineSegment(sketch, "E25.1.5.26", {"start": v(-54.14, 23.1) * mm, "end": v(-60.12, 23.1) * mm});
            skLineSegment(sketch, "E25.1.5.27", {"start": v(-20.52, 23) * mm, "end": v(-26.52, 23) * mm});
            skLineSegment(sketch, "E25.1.5.28", {"start": v(-51.02, 23) * mm, "end": v(-57.02, 23) * mm});
            skLineSegment(sketch, "E25.1.5.29", {"start": v(-23.64, 23.1) * mm, "end": v(-23.64, 25.1) * mm});
            skLineSegment(sketch, "E25.1.5.30", {"start": v(-57.02, 23) * mm, "end": v(-57.02, 21) * mm});
            skLineSegment(sketch, "E25.1.5.31", {"start": v(-57.12, 21) * mm, "end": v(-57.12, 23) * mm});
            skLineSegment(sketch, "E25.1.5.32", {"start": v(-17.54, 23.1) * mm, "end": v(-23.52, 23.1) * mm});
            skLineSegment(sketch, "E25.1.5.33", {"start": v(-26.62, 21) * mm, "end": v(-26.62, 23) * mm});
            skLineSegment(sketch, "E25.1.5.34", {"start": v(-48.04, 23.1) * mm, "end": v(-54.02, 23.1) * mm});
            skLineSegment(sketch, "E25.1.5.35", {"start": v(-23.64, 23.1) * mm, "end": v(-29.62, 23.1) * mm});
            skLineSegment(sketch, "E25.1.5.36", {"start": v(-17.54, 23.1) * mm, "end": v(-17.54, 25.1) * mm});
            skLineSegment(sketch, "E25.1.5.37", {"start": v(-44.92, 23) * mm, "end": v(-50.92, 23) * mm});
            skLineSegment(sketch, "E25.1.5.38", {"start": v(-14.42, 23) * mm, "end": v(-20.42, 23) * mm});
            skLineSegment(sketch, "E25.1.5.39", {"start": v(-26.62, 23) * mm, "end": v(-32.62, 23) * mm});
            skLineSegment(sketch, "E25.1.5.40", {"start": v(-48.04, 23.1) * mm, "end": v(-48.04, 25.1) * mm});
            skLineSegment(sketch, "E25.1.5.41", {"start": v(-26.52, 23) * mm, "end": v(-26.52, 21) * mm});
            skLineSegment(sketch, "E25.1.5.42", {"start": v(-41.84, 25.1) * mm, "end": v(-41.82, 23.1) * mm});
            skLineSegment(sketch, "E25.1.5.43", {"start": v(-17.44, 25.1) * mm, "end": v(-17.42, 23.1) * mm});
            skLineSegment(sketch, "E25.1.5.44", {"start": v(-50.92, 23) * mm, "end": v(-50.92, 21) * mm});
            skLineSegment(sketch, "E25.1.5.45", {"start": v(-8.32, 23) * mm, "end": v(-14.32, 23) * mm});
            skLineSegment(sketch, "E25.1.5.46", {"start": v(-20.42, 23) * mm, "end": v(-20.42, 21) * mm});
            skLineSegment(sketch, "E25.1.5.47", {"start": v(-44.82, 23) * mm, "end": v(-44.82, 21) * mm});
            skLineSegment(sketch, "E25.1.5.48", {"start": v(-2.22, 23) * mm, "end": v(-8.22, 23) * mm});
            skLineSegment(sketch, "E25.1.5.49", {"start": v(-32.62, 23) * mm, "end": v(-32.62, 21) * mm});
            skLineSegment(sketch, "E25.1.5.50", {"start": v(-47.94, 25.1) * mm, "end": v(-47.92, 23.1) * mm});
            skLineSegment(sketch, "E25.1.5.51", {"start": v(-35.84, 23.1) * mm, "end": v(-41.82, 23.1) * mm});
            skLineSegment(sketch, "E25.1.5.52", {"start": v(-11.44, 23.1) * mm, "end": v(-17.42, 23.1) * mm});
            skLineSegment(sketch, "E25.1.5.53", {"start": v(-32.72, 21) * mm, "end": v(-32.72, 23) * mm});
            skLineSegment(sketch, "E25.1.5.54", {"start": v(-11.34, 25.1) * mm, "end": v(-11.32, 23.1) * mm});
            skLineSegment(sketch, "E25.1.5.55", {"start": v(-35.74, 25.1) * mm, "end": v(-35.72, 23.1) * mm});
            skLineSegment(sketch, "E25.1.5.56", {"start": v(-14.42, 21) * mm, "end": v(-14.42, 23) * mm});
            skLineSegment(sketch, "E25.1.5.57", {"start": v(-29.74, 23.1) * mm, "end": v(-29.74, 25.1) * mm});
            skLineSegment(sketch, "E25.1.5.58", {"start": v(-41.94, 23.1) * mm, "end": v(-47.92, 23.1) * mm});
            skLineSegment(sketch, "E25.1.5.59", {"start": v(-32.72, 23) * mm, "end": v(-38.72, 23) * mm});
            skLineSegment(sketch, "E25.1.5.60", {"start": v(-38.82, 21) * mm, "end": v(-38.82, 23) * mm});
            skLineSegment(sketch, "E25.1.5.61", {"start": v(-54.14, 23.1) * mm, "end": v(-54.14, 25.1) * mm});
            skLineSegment(sketch, "E25.1.5.62", {"start": v(-8.32, 21) * mm, "end": v(-8.32, 23) * mm});
            skLineSegment(sketch, "E25.1.5.63", {"start": v(-54.04, 25.1) * mm, "end": v(-54.02, 23.1) * mm});
            skLineSegment(sketch, "E25.1.5.64", {"start": v(-29.64, 25.1) * mm, "end": v(-29.62, 23.1) * mm});
            skLineSegment(sketch, "E25.1.5.65", {"start": v(-5.34, 23.1) * mm, "end": v(-11.32, 23.1) * mm});
            skLineSegment(sketch, "E25.1.5.66", {"start": v(-51.02, 21) * mm, "end": v(-51.02, 23) * mm});
            skLineSegment(sketch, "E25.1.5.67", {"start": v(-29.74, 23.1) * mm, "end": v(-35.72, 23.1) * mm});
            skLineSegment(sketch, "E25.1.5.68", {"start": v(-44.92, 21) * mm, "end": v(-44.92, 23) * mm});
            skLineSegment(sketch, "E25.1.5.69", {"start": v(-20.52, 21) * mm, "end": v(-20.52, 23) * mm});
            skLineSegment(sketch, "E25.1.5.70", {"start": v(-41.94, 23.1) * mm, "end": v(-41.94, 25.1) * mm});
            skLineSegment(sketch, "E25.1.5.71", {"start": v(-38.72, 23) * mm, "end": v(-38.72, 21) * mm});
            skLineSegment(sketch, "E25.1.5.72", {"start": v(-35.84, 23.1) * mm, "end": v(-35.84, 25.1) * mm});
            skLineSegment(sketch, "E25.1.5.73", {"start": v(-11.44, 23.1) * mm, "end": v(-11.44, 25.1) * mm});
            skLineSegment(sketch, "E25.1.5.74", {"start": v(-38.82, 23) * mm, "end": v(-44.82, 23) * mm});
            skLineSegment(sketch, "E25.1.5.75", {"start": v(-14.32, 23) * mm, "end": v(-14.32, 21) * mm});
            skLineSegment(sketch, "E25.1.5.77", {"start": v(3.88, 23) * mm, "end": v(-2.12, 23) * mm});
            skLineSegment(sketch, "E25.1.5.78", {"start": v(-2.12, 23) * mm, "end": v(-2.12, 21) * mm});
            skLineSegment(sketch, "E25.1.5.79", {"start": v(-2.22, 21) * mm, "end": v(-2.22, 23) * mm});
            skLineSegment(sketch, "E25.1.5.80", {"start": v(-8.22, 23) * mm, "end": v(-8.22, 21) * mm});
            skLineSegment(sketch, "E25.1.5.81", {"start": v(0.86, 25.1) * mm, "end": v(3.88, 25.1) * mm});
            skLineSegment(sketch, "E25.1.5.85", {"start": v(0.76, 23.1) * mm, "end": v(-5.22, 23.1) * mm});
            skLineSegment(sketch, "E25.1.5.86", {"start": v(0.86, 23.1) * mm, "end": v(0.86, 25.1) * mm});
            skLineSegment(sketch, "E25.1.5.87", {"start": v(-5.34, 23.1) * mm, "end": v(-5.34, 25.1) * mm});
            skLineSegment(sketch, "E25.1.5.88", {"start": v(-5.24, 25.1) * mm, "end": v(-5.22, 23.1) * mm});
            skLineSegment(sketch, "E25.1.5.89", {"start": v(0.76, 23.1) * mm, "end": v(0.76, 25.1) * mm});
            skLineSegment(sketch, "E25.1.5.90", {"start": v(-2.12, 21) * mm, "end": v(-2.22, 21) * mm});
            skLineSegment(sketch, "E25.1.5.91", {"start": v(0.86, 23.1) * mm, "end": v(0.76, 23.1) * mm});
            skLineSegment(sketch, "E25.1.6.0", {"start": v(-35.84, 29.3) * mm, "end": v(-41.84, 29.3) * mm});
            skLineSegment(sketch, "E25.1.6.1", {"start": v(-11.44, 29.3) * mm, "end": v(-17.44, 29.3) * mm});
            skLineSegment(sketch, "E25.1.6.2", {"start": v(-48.04, 29.3) * mm, "end": v(-54.04, 29.3) * mm});
            skLineSegment(sketch, "E25.1.6.3", {"start": v(-23.64, 29.3) * mm, "end": v(-29.64, 29.3) * mm});
            skLineSegment(sketch, "E25.1.6.4", {"start": v(-41.94, 29.3) * mm, "end": v(-47.94, 29.3) * mm});
            skLineSegment(sketch, "E25.1.6.5", {"start": v(-17.54, 29.3) * mm, "end": v(-23.54, 29.3) * mm});
            skLineSegment(sketch, "E25.1.6.6", {"start": v(-5.34, 29.3) * mm, "end": v(-11.34, 29.3) * mm});
            skLineSegment(sketch, "E25.1.6.7", {"start": v(-54.14, 29.3) * mm, "end": v(-60.14, 29.3) * mm});
            skLineSegment(sketch, "E25.1.6.8", {"start": v(-29.74, 29.3) * mm, "end": v(-35.74, 29.3) * mm});
            skLineSegment(sketch, "E25.1.6.9", {"start": v(-20.42, 25.2) * mm, "end": v(-14.42, 25.2) * mm});
            skLineSegment(sketch, "E25.1.6.10", {"start": v(-44.82, 25.2) * mm, "end": v(-38.82, 25.2) * mm});
            skLineSegment(sketch, "E25.1.6.11", {"start": v(-57.02, 25.2) * mm, "end": v(-51.02, 25.2) * mm});
            skLineSegment(sketch, "E25.1.6.12", {"start": v(-32.62, 25.2) * mm, "end": v(-26.62, 25.2) * mm});
            skLineSegment(sketch, "E25.1.6.13", {"start": v(-50.92, 25.2) * mm, "end": v(-44.92, 25.2) * mm});
            skLineSegment(sketch, "E25.1.6.14", {"start": v(-26.52, 25.2) * mm, "end": v(-20.52, 25.2) * mm});
            skPoint(sketch, "E25.1.6.15", {"position": v(-5.22, 27.2) * mm});
            skLineSegment(sketch, "E25.1.6.16", {"start": v(-63.12, 25.2) * mm, "end": v(-57.12, 25.2) * mm});
            skLineSegment(sketch, "E25.1.6.17", {"start": v(-38.72, 25.2) * mm, "end": v(-32.72, 25.2) * mm});
            skLineSegment(sketch, "E25.1.6.18", {"start": v(-14.32, 25.2) * mm, "end": v(-8.32, 25.2) * mm});
            skLineSegment(sketch, "E25.1.6.20", {"start": v(0.76, 29.3) * mm, "end": v(-5.24, 29.3) * mm});
            skLineSegment(sketch, "E25.1.6.21", {"start": v(-63.12, 27.2) * mm, "end": v(-63.12, 25.2) * mm});
            skLineSegment(sketch, "E25.1.6.22", {"start": v(-8.22, 25.2) * mm, "end": v(-2.22, 25.2) * mm});
            skLineSegment(sketch, "E25.1.6.23", {"start": v(-23.54, 29.3) * mm, "end": v(-23.52, 27.3) * mm});
            skLineSegment(sketch, "E25.1.6.24", {"start": v(-60.14, 29.3) * mm, "end": v(-60.12, 27.3) * mm});
            skLineSegment(sketch, "E25.1.6.25", {"start": v(-57.12, 27.2) * mm, "end": v(-63.12, 27.2) * mm});
            skLineSegment(sketch, "E25.1.6.26", {"start": v(-54.14, 27.3) * mm, "end": v(-60.12, 27.3) * mm});
            skLineSegment(sketch, "E25.1.6.27", {"start": v(-20.52, 27.2) * mm, "end": v(-26.52, 27.2) * mm});
            skLineSegment(sketch, "E25.1.6.28", {"start": v(-51.02, 27.2) * mm, "end": v(-57.02, 27.2) * mm});
            skLineSegment(sketch, "E25.1.6.29", {"start": v(-23.64, 27.3) * mm, "end": v(-23.64, 29.3) * mm});
            skLineSegment(sketch, "E25.1.6.30", {"start": v(-57.02, 27.2) * mm, "end": v(-57.02, 25.2) * mm});
            skLineSegment(sketch, "E25.1.6.31", {"start": v(-57.12, 25.2) * mm, "end": v(-57.12, 27.2) * mm});
            skLineSegment(sketch, "E25.1.6.32", {"start": v(-17.54, 27.3) * mm, "end": v(-23.52, 27.3) * mm});
            skLineSegment(sketch, "E25.1.6.33", {"start": v(-26.62, 25.2) * mm, "end": v(-26.62, 27.2) * mm});
            skLineSegment(sketch, "E25.1.6.34", {"start": v(-48.04, 27.3) * mm, "end": v(-54.02, 27.3) * mm});
            skLineSegment(sketch, "E25.1.6.35", {"start": v(-23.64, 27.3) * mm, "end": v(-29.62, 27.3) * mm});
            skLineSegment(sketch, "E25.1.6.36", {"start": v(-17.54, 27.3) * mm, "end": v(-17.54, 29.3) * mm});
            skLineSegment(sketch, "E25.1.6.37", {"start": v(-44.92, 27.2) * mm, "end": v(-50.92, 27.2) * mm});
            skLineSegment(sketch, "E25.1.6.38", {"start": v(-14.42, 27.2) * mm, "end": v(-20.42, 27.2) * mm});
            skLineSegment(sketch, "E25.1.6.39", {"start": v(-26.62, 27.2) * mm, "end": v(-32.62, 27.2) * mm});
            skLineSegment(sketch, "E25.1.6.40", {"start": v(-48.04, 27.3) * mm, "end": v(-48.04, 29.3) * mm});
            skLineSegment(sketch, "E25.1.6.41", {"start": v(-26.52, 27.2) * mm, "end": v(-26.52, 25.2) * mm});
            skLineSegment(sketch, "E25.1.6.42", {"start": v(-41.84, 29.3) * mm, "end": v(-41.82, 27.3) * mm});
            skLineSegment(sketch, "E25.1.6.43", {"start": v(-17.44, 29.3) * mm, "end": v(-17.42, 27.3) * mm});
            skLineSegment(sketch, "E25.1.6.44", {"start": v(-50.92, 27.2) * mm, "end": v(-50.92, 25.2) * mm});
            skLineSegment(sketch, "E25.1.6.45", {"start": v(-8.32, 27.2) * mm, "end": v(-14.32, 27.2) * mm});
            skLineSegment(sketch, "E25.1.6.46", {"start": v(-20.42, 27.2) * mm, "end": v(-20.42, 25.2) * mm});
            skLineSegment(sketch, "E25.1.6.47", {"start": v(-44.82, 27.2) * mm, "end": v(-44.82, 25.2) * mm});
            skLineSegment(sketch, "E25.1.6.48", {"start": v(-2.22, 27.2) * mm, "end": v(-8.22, 27.2) * mm});
            skLineSegment(sketch, "E25.1.6.49", {"start": v(-32.62, 27.2) * mm, "end": v(-32.62, 25.2) * mm});
            skLineSegment(sketch, "E25.1.6.50", {"start": v(-47.94, 29.3) * mm, "end": v(-47.92, 27.3) * mm});
            skLineSegment(sketch, "E25.1.6.51", {"start": v(-35.84, 27.3) * mm, "end": v(-41.82, 27.3) * mm});
            skLineSegment(sketch, "E25.1.6.52", {"start": v(-11.44, 27.3) * mm, "end": v(-17.42, 27.3) * mm});
            skLineSegment(sketch, "E25.1.6.53", {"start": v(-32.72, 25.2) * mm, "end": v(-32.72, 27.2) * mm});
            skLineSegment(sketch, "E25.1.6.54", {"start": v(-11.34, 29.3) * mm, "end": v(-11.32, 27.3) * mm});
            skLineSegment(sketch, "E25.1.6.55", {"start": v(-35.74, 29.3) * mm, "end": v(-35.72, 27.3) * mm});
            skLineSegment(sketch, "E25.1.6.56", {"start": v(-14.42, 25.2) * mm, "end": v(-14.42, 27.2) * mm});
            skLineSegment(sketch, "E25.1.6.57", {"start": v(-29.74, 27.3) * mm, "end": v(-29.74, 29.3) * mm});
            skLineSegment(sketch, "E25.1.6.58", {"start": v(-41.94, 27.3) * mm, "end": v(-47.92, 27.3) * mm});
            skLineSegment(sketch, "E25.1.6.59", {"start": v(-32.72, 27.2) * mm, "end": v(-38.72, 27.2) * mm});
            skLineSegment(sketch, "E25.1.6.60", {"start": v(-38.82, 25.2) * mm, "end": v(-38.82, 27.2) * mm});
            skLineSegment(sketch, "E25.1.6.61", {"start": v(-54.14, 27.3) * mm, "end": v(-54.14, 29.3) * mm});
            skLineSegment(sketch, "E25.1.6.62", {"start": v(-8.32, 25.2) * mm, "end": v(-8.32, 27.2) * mm});
            skLineSegment(sketch, "E25.1.6.63", {"start": v(-54.04, 29.3) * mm, "end": v(-54.02, 27.3) * mm});
            skLineSegment(sketch, "E25.1.6.64", {"start": v(-29.64, 29.3) * mm, "end": v(-29.62, 27.3) * mm});
            skLineSegment(sketch, "E25.1.6.65", {"start": v(-5.34, 27.3) * mm, "end": v(-11.32, 27.3) * mm});
            skLineSegment(sketch, "E25.1.6.66", {"start": v(-51.02, 25.2) * mm, "end": v(-51.02, 27.2) * mm});
            skLineSegment(sketch, "E25.1.6.67", {"start": v(-29.74, 27.3) * mm, "end": v(-35.72, 27.3) * mm});
            skLineSegment(sketch, "E25.1.6.68", {"start": v(-44.92, 25.2) * mm, "end": v(-44.92, 27.2) * mm});
            skLineSegment(sketch, "E25.1.6.69", {"start": v(-20.52, 25.2) * mm, "end": v(-20.52, 27.2) * mm});
            skLineSegment(sketch, "E25.1.6.70", {"start": v(-41.94, 27.3) * mm, "end": v(-41.94, 29.3) * mm});
            skLineSegment(sketch, "E25.1.6.71", {"start": v(-38.72, 27.2) * mm, "end": v(-38.72, 25.2) * mm});
            skLineSegment(sketch, "E25.1.6.72", {"start": v(-35.84, 27.3) * mm, "end": v(-35.84, 29.3) * mm});
            skLineSegment(sketch, "E25.1.6.73", {"start": v(-11.44, 27.3) * mm, "end": v(-11.44, 29.3) * mm});
            skLineSegment(sketch, "E25.1.6.74", {"start": v(-38.82, 27.2) * mm, "end": v(-44.82, 27.2) * mm});
            skLineSegment(sketch, "E25.1.6.75", {"start": v(-14.32, 27.2) * mm, "end": v(-14.32, 25.2) * mm});
            skLineSegment(sketch, "E25.1.6.76", {"start": v(3.88, 25.2) * mm, "end": v(3.88, 27.2) * mm});
            skLineSegment(sketch, "E25.1.6.78", {"start": v(-2.12, 27.2) * mm, "end": v(-2.12, 25.2) * mm});
            skLineSegment(sketch, "E25.1.6.79", {"start": v(-2.22, 25.2) * mm, "end": v(-2.22, 27.2) * mm});
            skLineSegment(sketch, "E25.1.6.80", {"start": v(-8.22, 27.2) * mm, "end": v(-8.22, 25.2) * mm});
            skLineSegment(sketch, "E25.1.6.81", {"start": v(0.86, 29.3) * mm, "end": v(3.88, 29.3) * mm});
            skLineSegment(sketch, "E25.1.6.83", {"start": v(3.88, 29.3) * mm, "end": v(3.88, 29.4) * mm});
            skLineSegment(sketch, "E25.1.6.84", {"start": v(3.88, 27.3) * mm, "end": v(0.86, 27.3) * mm});
            skLineSegment(sketch, "E25.1.6.85", {"start": v(0.76, 27.3) * mm, "end": v(-5.22, 27.3) * mm});
            skLineSegment(sketch, "E25.1.6.86", {"start": v(0.86, 27.3) * mm, "end": v(0.86, 29.3) * mm});
            skLineSegment(sketch, "E25.1.6.87", {"start": v(-5.34, 27.3) * mm, "end": v(-5.34, 29.3) * mm});
            skLineSegment(sketch, "E25.1.6.88", {"start": v(-5.24, 29.3) * mm, "end": v(-5.22, 27.3) * mm});
            skLineSegment(sketch, "E25.1.6.89", {"start": v(0.76, 27.3) * mm, "end": v(0.76, 29.3) * mm});
            skLineSegment(sketch, "E25.1.6.90", {"start": v(-2.12, 25.2) * mm, "end": v(-2.22, 25.2) * mm});
            skLineSegment(sketch, "E25.1.6.91", {"start": v(0.86, 27.3) * mm, "end": v(0.76, 27.3) * mm});
            skLineSegment(sketch, "E25.1.7.0", {"start": v(-35.84, 33.5) * mm, "end": v(-41.84, 33.5) * mm});
            skLineSegment(sketch, "E25.1.7.1", {"start": v(-11.44, 33.5) * mm, "end": v(-17.44, 33.5) * mm});
            skLineSegment(sketch, "E25.1.7.2", {"start": v(-48.04, 33.5) * mm, "end": v(-54.04, 33.5) * mm});
            skLineSegment(sketch, "E25.1.7.3", {"start": v(-23.64, 33.5) * mm, "end": v(-29.64, 33.5) * mm});
            skLineSegment(sketch, "E25.1.7.4", {"start": v(-41.94, 33.5) * mm, "end": v(-47.94, 33.5) * mm});
            skLineSegment(sketch, "E25.1.7.5", {"start": v(-17.54, 33.5) * mm, "end": v(-23.54, 33.5) * mm});
            skLineSegment(sketch, "E25.1.7.6", {"start": v(-5.34, 33.5) * mm, "end": v(-11.34, 33.5) * mm});
            skLineSegment(sketch, "E25.1.7.7", {"start": v(-54.14, 33.5) * mm, "end": v(-60.14, 33.5) * mm});
            skLineSegment(sketch, "E25.1.7.8", {"start": v(-29.74, 33.5) * mm, "end": v(-35.74, 33.5) * mm});
            skLineSegment(sketch, "E25.1.7.9", {"start": v(-20.42, 29.4) * mm, "end": v(-14.42, 29.4) * mm});
            skLineSegment(sketch, "E25.1.7.10", {"start": v(-44.82, 29.4) * mm, "end": v(-38.82, 29.4) * mm});
            skLineSegment(sketch, "E25.1.7.11", {"start": v(-57.02, 29.4) * mm, "end": v(-51.02, 29.4) * mm});
            skLineSegment(sketch, "E25.1.7.12", {"start": v(-32.62, 29.4) * mm, "end": v(-26.62, 29.4) * mm});
            skLineSegment(sketch, "E25.1.7.13", {"start": v(-50.92, 29.4) * mm, "end": v(-44.92, 29.4) * mm});
            skLineSegment(sketch, "E25.1.7.14", {"start": v(-26.52, 29.4) * mm, "end": v(-20.52, 29.4) * mm});
            skPoint(sketch, "E25.1.7.15", {"position": v(-5.22, 31.4) * mm});
            skLineSegment(sketch, "E25.1.7.16", {"start": v(-63.12, 29.4) * mm, "end": v(-57.12, 29.4) * mm});
            skLineSegment(sketch, "E25.1.7.17", {"start": v(-38.72, 29.4) * mm, "end": v(-32.72, 29.4) * mm});
            skLineSegment(sketch, "E25.1.7.18", {"start": v(-14.32, 29.4) * mm, "end": v(-8.32, 29.4) * mm});
            skLineSegment(sketch, "E25.1.7.19", {"start": v(-2.12, 29.4) * mm, "end": v(3.88, 29.4) * mm});
            skLineSegment(sketch, "E25.1.7.20", {"start": v(0.76, 33.5) * mm, "end": v(-5.24, 33.5) * mm});
            skLineSegment(sketch, "E25.1.7.21", {"start": v(-63.12, 31.4) * mm, "end": v(-63.12, 29.4) * mm});
            skLineSegment(sketch, "E25.1.7.22", {"start": v(-8.22, 29.4) * mm, "end": v(-2.22, 29.4) * mm});
            skLineSegment(sketch, "E25.1.7.23", {"start": v(-23.54, 33.5) * mm, "end": v(-23.52, 31.5) * mm});
            skLineSegment(sketch, "E25.1.7.24", {"start": v(-60.14, 33.5) * mm, "end": v(-60.12, 31.5) * mm});
            skLineSegment(sketch, "E25.1.7.25", {"start": v(-57.12, 31.4) * mm, "end": v(-63.12, 31.4) * mm});
            skLineSegment(sketch, "E25.1.7.26", {"start": v(-54.14, 31.5) * mm, "end": v(-60.12, 31.5) * mm});
            skLineSegment(sketch, "E25.1.7.27", {"start": v(-20.52, 31.4) * mm, "end": v(-26.52, 31.4) * mm});
            skLineSegment(sketch, "E25.1.7.28", {"start": v(-51.02, 31.4) * mm, "end": v(-57.02, 31.4) * mm});
            skLineSegment(sketch, "E25.1.7.29", {"start": v(-23.64, 31.5) * mm, "end": v(-23.64, 33.5) * mm});
            skLineSegment(sketch, "E25.1.7.30", {"start": v(-57.02, 31.4) * mm, "end": v(-57.02, 29.4) * mm});
            skLineSegment(sketch, "E25.1.7.31", {"start": v(-57.12, 29.4) * mm, "end": v(-57.12, 31.4) * mm});
            skLineSegment(sketch, "E25.1.7.32", {"start": v(-17.54, 31.5) * mm, "end": v(-23.52, 31.5) * mm});
            skLineSegment(sketch, "E25.1.7.33", {"start": v(-26.62, 29.4) * mm, "end": v(-26.62, 31.4) * mm});
            skLineSegment(sketch, "E25.1.7.34", {"start": v(-48.04, 31.5) * mm, "end": v(-54.02, 31.5) * mm});
            skLineSegment(sketch, "E25.1.7.35", {"start": v(-23.64, 31.5) * mm, "end": v(-29.62, 31.5) * mm});
            skLineSegment(sketch, "E25.1.7.36", {"start": v(-17.54, 31.5) * mm, "end": v(-17.54, 33.5) * mm});
            skLineSegment(sketch, "E25.1.7.37", {"start": v(-44.92, 31.4) * mm, "end": v(-50.92, 31.4) * mm});
            skLineSegment(sketch, "E25.1.7.38", {"start": v(-14.42, 31.4) * mm, "end": v(-20.42, 31.4) * mm});
            skLineSegment(sketch, "E25.1.7.39", {"start": v(-26.62, 31.4) * mm, "end": v(-32.62, 31.4) * mm});
            skLineSegment(sketch, "E25.1.7.40", {"start": v(-48.04, 31.5) * mm, "end": v(-48.04, 33.5) * mm});
            skLineSegment(sketch, "E25.1.7.41", {"start": v(-26.52, 31.4) * mm, "end": v(-26.52, 29.4) * mm});
            skLineSegment(sketch, "E25.1.7.42", {"start": v(-41.84, 33.5) * mm, "end": v(-41.82, 31.5) * mm});
            skLineSegment(sketch, "E25.1.7.43", {"start": v(-17.44, 33.5) * mm, "end": v(-17.42, 31.5) * mm});
            skLineSegment(sketch, "E25.1.7.44", {"start": v(-50.92, 31.4) * mm, "end": v(-50.92, 29.4) * mm});
            skLineSegment(sketch, "E25.1.7.45", {"start": v(-8.32, 31.4) * mm, "end": v(-14.32, 31.4) * mm});
            skLineSegment(sketch, "E25.1.7.46", {"start": v(-20.42, 31.4) * mm, "end": v(-20.42, 29.4) * mm});
            skLineSegment(sketch, "E25.1.7.47", {"start": v(-44.82, 31.4) * mm, "end": v(-44.82, 29.4) * mm});
            skLineSegment(sketch, "E25.1.7.48", {"start": v(-2.22, 31.4) * mm, "end": v(-8.22, 31.4) * mm});
            skLineSegment(sketch, "E25.1.7.49", {"start": v(-32.62, 31.4) * mm, "end": v(-32.62, 29.4) * mm});
            skLineSegment(sketch, "E25.1.7.50", {"start": v(-47.94, 33.5) * mm, "end": v(-47.92, 31.5) * mm});
            skLineSegment(sketch, "E25.1.7.51", {"start": v(-35.84, 31.5) * mm, "end": v(-41.82, 31.5) * mm});
            skLineSegment(sketch, "E25.1.7.52", {"start": v(-11.44, 31.5) * mm, "end": v(-17.42, 31.5) * mm});
            skLineSegment(sketch, "E25.1.7.53", {"start": v(-32.72, 29.4) * mm, "end": v(-32.72, 31.4) * mm});
            skLineSegment(sketch, "E25.1.7.54", {"start": v(-11.34, 33.5) * mm, "end": v(-11.32, 31.5) * mm});
            skLineSegment(sketch, "E25.1.7.55", {"start": v(-35.74, 33.5) * mm, "end": v(-35.72, 31.5) * mm});
            skLineSegment(sketch, "E25.1.7.56", {"start": v(-14.42, 29.4) * mm, "end": v(-14.42, 31.4) * mm});
            skLineSegment(sketch, "E25.1.7.57", {"start": v(-29.74, 31.5) * mm, "end": v(-29.74, 33.5) * mm});
            skLineSegment(sketch, "E25.1.7.58", {"start": v(-41.94, 31.5) * mm, "end": v(-47.92, 31.5) * mm});
            skLineSegment(sketch, "E25.1.7.59", {"start": v(-32.72, 31.4) * mm, "end": v(-38.72, 31.4) * mm});
            skLineSegment(sketch, "E25.1.7.60", {"start": v(-38.82, 29.4) * mm, "end": v(-38.82, 31.4) * mm});
            skLineSegment(sketch, "E25.1.7.61", {"start": v(-54.14, 31.5) * mm, "end": v(-54.14, 33.5) * mm});
            skLineSegment(sketch, "E25.1.7.62", {"start": v(-8.32, 29.4) * mm, "end": v(-8.32, 31.4) * mm});
            skLineSegment(sketch, "E25.1.7.63", {"start": v(-54.04, 33.5) * mm, "end": v(-54.02, 31.5) * mm});
            skLineSegment(sketch, "E25.1.7.64", {"start": v(-29.64, 33.5) * mm, "end": v(-29.62, 31.5) * mm});
            skLineSegment(sketch, "E25.1.7.65", {"start": v(-5.34, 31.5) * mm, "end": v(-11.32, 31.5) * mm});
            skLineSegment(sketch, "E25.1.7.66", {"start": v(-51.02, 29.4) * mm, "end": v(-51.02, 31.4) * mm});
            skLineSegment(sketch, "E25.1.7.67", {"start": v(-29.74, 31.5) * mm, "end": v(-35.72, 31.5) * mm});
            skLineSegment(sketch, "E25.1.7.68", {"start": v(-44.92, 29.4) * mm, "end": v(-44.92, 31.4) * mm});
            skLineSegment(sketch, "E25.1.7.69", {"start": v(-20.52, 29.4) * mm, "end": v(-20.52, 31.4) * mm});
            skLineSegment(sketch, "E25.1.7.70", {"start": v(-41.94, 31.5) * mm, "end": v(-41.94, 33.5) * mm});
            skLineSegment(sketch, "E25.1.7.71", {"start": v(-38.72, 31.4) * mm, "end": v(-38.72, 29.4) * mm});
            skLineSegment(sketch, "E25.1.7.72", {"start": v(-35.84, 31.5) * mm, "end": v(-35.84, 33.5) * mm});
            skLineSegment(sketch, "E25.1.7.73", {"start": v(-11.44, 31.5) * mm, "end": v(-11.44, 33.5) * mm});
            skLineSegment(sketch, "E25.1.7.74", {"start": v(-38.82, 31.4) * mm, "end": v(-44.82, 31.4) * mm});
            skLineSegment(sketch, "E25.1.7.75", {"start": v(-14.32, 31.4) * mm, "end": v(-14.32, 29.4) * mm});
            skLineSegment(sketch, "E25.1.7.76", {"start": v(3.88, 29.4) * mm, "end": v(3.88, 31.4) * mm});
            skLineSegment(sketch, "E25.1.7.77", {"start": v(3.88, 31.4) * mm, "end": v(-2.12, 31.4) * mm});
            skLineSegment(sketch, "E25.1.7.78", {"start": v(-2.12, 31.4) * mm, "end": v(-2.12, 29.4) * mm});
            skLineSegment(sketch, "E25.1.7.79", {"start": v(-2.22, 29.4) * mm, "end": v(-2.22, 31.4) * mm});
            skLineSegment(sketch, "E25.1.7.80", {"start": v(-8.22, 31.4) * mm, "end": v(-8.22, 29.4) * mm});
            skLineSegment(sketch, "E25.1.7.81", {"start": v(0.86, 33.5) * mm, "end": v(3.88, 33.5) * mm});
            skLineSegment(sketch, "E25.1.7.85", {"start": v(0.76, 31.5) * mm, "end": v(-5.22, 31.5) * mm});
            skLineSegment(sketch, "E25.1.7.86", {"start": v(0.86, 31.5) * mm, "end": v(0.86, 33.5) * mm});
            skLineSegment(sketch, "E25.1.7.87", {"start": v(-5.34, 31.5) * mm, "end": v(-5.34, 33.5) * mm});
            skLineSegment(sketch, "E25.1.7.88", {"start": v(-5.24, 33.5) * mm, "end": v(-5.22, 31.5) * mm});
            skLineSegment(sketch, "E25.1.7.89", {"start": v(0.76, 31.5) * mm, "end": v(0.76, 33.5) * mm});
            skLineSegment(sketch, "E25.1.7.90", {"start": v(-2.12, 29.4) * mm, "end": v(-2.22, 29.4) * mm});
            skLineSegment(sketch, "E25.1.7.91", {"start": v(0.86, 31.5) * mm, "end": v(0.76, 31.5) * mm});
            skLineSegment(sketch, "E25.1.8.0", {"start": v(-35.84, 37.7) * mm, "end": v(-41.84, 37.7) * mm});
            skLineSegment(sketch, "E25.1.8.1", {"start": v(-11.44, 37.7) * mm, "end": v(-17.44, 37.7) * mm});
            skLineSegment(sketch, "E25.1.8.2", {"start": v(-48.04, 37.7) * mm, "end": v(-54.04, 37.7) * mm});
            skLineSegment(sketch, "E25.1.8.3", {"start": v(-23.64, 37.7) * mm, "end": v(-29.64, 37.7) * mm});
            skLineSegment(sketch, "E25.1.8.4", {"start": v(-41.94, 37.7) * mm, "end": v(-47.94, 37.7) * mm});
            skLineSegment(sketch, "E25.1.8.5", {"start": v(-17.54, 37.7) * mm, "end": v(-23.54, 37.7) * mm});
            skLineSegment(sketch, "E25.1.8.6", {"start": v(-5.34, 37.7) * mm, "end": v(-11.34, 37.7) * mm});
            skLineSegment(sketch, "E25.1.8.7", {"start": v(-54.14, 37.7) * mm, "end": v(-60.14, 37.7) * mm});
            skLineSegment(sketch, "E25.1.8.8", {"start": v(-29.74, 37.7) * mm, "end": v(-35.74, 37.7) * mm});
            skLineSegment(sketch, "E25.1.8.9", {"start": v(-20.42, 33.6) * mm, "end": v(-14.42, 33.6) * mm});
            skLineSegment(sketch, "E25.1.8.10", {"start": v(-44.82, 33.6) * mm, "end": v(-38.82, 33.6) * mm});
            skLineSegment(sketch, "E25.1.8.11", {"start": v(-57.02, 33.6) * mm, "end": v(-51.02, 33.6) * mm});
            skLineSegment(sketch, "E25.1.8.12", {"start": v(-32.62, 33.6) * mm, "end": v(-26.62, 33.6) * mm});
            skLineSegment(sketch, "E25.1.8.13", {"start": v(-50.92, 33.6) * mm, "end": v(-44.92, 33.6) * mm});
            skLineSegment(sketch, "E25.1.8.14", {"start": v(-26.52, 33.6) * mm, "end": v(-20.52, 33.6) * mm});
            skPoint(sketch, "E25.1.8.15", {"position": v(-5.22, 35.6) * mm});
            skLineSegment(sketch, "E25.1.8.16", {"start": v(-63.12, 33.6) * mm, "end": v(-57.12, 33.6) * mm});
            skLineSegment(sketch, "E25.1.8.17", {"start": v(-38.72, 33.6) * mm, "end": v(-32.72, 33.6) * mm});
            skLineSegment(sketch, "E25.1.8.18", {"start": v(-14.32, 33.6) * mm, "end": v(-8.32, 33.6) * mm});
            skLineSegment(sketch, "E25.1.8.19", {"start": v(-2.12, 33.6) * mm, "end": v(3.88, 33.6) * mm});
            skLineSegment(sketch, "E25.1.8.20", {"start": v(0.76, 37.7) * mm, "end": v(-5.24, 37.7) * mm});
            skLineSegment(sketch, "E25.1.8.21", {"start": v(-63.12, 35.6) * mm, "end": v(-63.12, 33.6) * mm});
            skLineSegment(sketch, "E25.1.8.22", {"start": v(-8.22, 33.6) * mm, "end": v(-2.22, 33.6) * mm});
            skLineSegment(sketch, "E25.1.8.23", {"start": v(-23.54, 37.7) * mm, "end": v(-23.52, 35.7) * mm});
            skLineSegment(sketch, "E25.1.8.24", {"start": v(-60.14, 37.7) * mm, "end": v(-60.12, 35.7) * mm});
            skLineSegment(sketch, "E25.1.8.25", {"start": v(-57.12, 35.6) * mm, "end": v(-63.12, 35.6) * mm});
            skLineSegment(sketch, "E25.1.8.26", {"start": v(-54.14, 35.7) * mm, "end": v(-60.12, 35.7) * mm});
            skLineSegment(sketch, "E25.1.8.27", {"start": v(-20.52, 35.6) * mm, "end": v(-26.52, 35.6) * mm});
            skLineSegment(sketch, "E25.1.8.28", {"start": v(-51.02, 35.6) * mm, "end": v(-57.02, 35.6) * mm});
            skLineSegment(sketch, "E25.1.8.29", {"start": v(-23.64, 35.7) * mm, "end": v(-23.64, 37.7) * mm});
            skLineSegment(sketch, "E25.1.8.30", {"start": v(-57.02, 35.6) * mm, "end": v(-57.02, 33.6) * mm});
            skLineSegment(sketch, "E25.1.8.31", {"start": v(-57.12, 33.6) * mm, "end": v(-57.12, 35.6) * mm});
            skLineSegment(sketch, "E25.1.8.32", {"start": v(-17.54, 35.7) * mm, "end": v(-23.52, 35.7) * mm});
            skLineSegment(sketch, "E25.1.8.33", {"start": v(-26.62, 33.6) * mm, "end": v(-26.62, 35.6) * mm});
            skLineSegment(sketch, "E25.1.8.34", {"start": v(-48.04, 35.7) * mm, "end": v(-54.02, 35.7) * mm});
            skLineSegment(sketch, "E25.1.8.35", {"start": v(-23.64, 35.7) * mm, "end": v(-29.62, 35.7) * mm});
            skLineSegment(sketch, "E25.1.8.36", {"start": v(-17.54, 35.7) * mm, "end": v(-17.54, 37.7) * mm});
            skLineSegment(sketch, "E25.1.8.37", {"start": v(-44.92, 35.6) * mm, "end": v(-50.92, 35.6) * mm});
            skLineSegment(sketch, "E25.1.8.38", {"start": v(-14.42, 35.6) * mm, "end": v(-20.42, 35.6) * mm});
            skLineSegment(sketch, "E25.1.8.39", {"start": v(-26.62, 35.6) * mm, "end": v(-32.62, 35.6) * mm});
            skLineSegment(sketch, "E25.1.8.40", {"start": v(-48.04, 35.7) * mm, "end": v(-48.04, 37.7) * mm});
            skLineSegment(sketch, "E25.1.8.41", {"start": v(-26.52, 35.6) * mm, "end": v(-26.52, 33.6) * mm});
            skLineSegment(sketch, "E25.1.8.42", {"start": v(-41.84, 37.7) * mm, "end": v(-41.82, 35.7) * mm});
            skLineSegment(sketch, "E25.1.8.43", {"start": v(-17.44, 37.7) * mm, "end": v(-17.42, 35.7) * mm});
            skLineSegment(sketch, "E25.1.8.44", {"start": v(-50.92, 35.6) * mm, "end": v(-50.92, 33.6) * mm});
            skLineSegment(sketch, "E25.1.8.45", {"start": v(-8.32, 35.6) * mm, "end": v(-14.32, 35.6) * mm});
            skLineSegment(sketch, "E25.1.8.46", {"start": v(-20.42, 35.6) * mm, "end": v(-20.42, 33.6) * mm});
            skLineSegment(sketch, "E25.1.8.47", {"start": v(-44.82, 35.6) * mm, "end": v(-44.82, 33.6) * mm});
            skLineSegment(sketch, "E25.1.8.48", {"start": v(-2.22, 35.6) * mm, "end": v(-8.22, 35.6) * mm});
            skLineSegment(sketch, "E25.1.8.49", {"start": v(-32.62, 35.6) * mm, "end": v(-32.62, 33.6) * mm});
            skLineSegment(sketch, "E25.1.8.50", {"start": v(-47.94, 37.7) * mm, "end": v(-47.92, 35.7) * mm});
            skLineSegment(sketch, "E25.1.8.51", {"start": v(-35.84, 35.7) * mm, "end": v(-41.82, 35.7) * mm});
            skLineSegment(sketch, "E25.1.8.52", {"start": v(-11.44, 35.7) * mm, "end": v(-17.42, 35.7) * mm});
            skLineSegment(sketch, "E25.1.8.53", {"start": v(-32.72, 33.6) * mm, "end": v(-32.72, 35.6) * mm});
            skLineSegment(sketch, "E25.1.8.54", {"start": v(-11.34, 37.7) * mm, "end": v(-11.32, 35.7) * mm});
            skLineSegment(sketch, "E25.1.8.55", {"start": v(-35.74, 37.7) * mm, "end": v(-35.72, 35.7) * mm});
            skLineSegment(sketch, "E25.1.8.56", {"start": v(-14.42, 33.6) * mm, "end": v(-14.42, 35.6) * mm});
            skLineSegment(sketch, "E25.1.8.57", {"start": v(-29.74, 35.7) * mm, "end": v(-29.74, 37.7) * mm});
            skLineSegment(sketch, "E25.1.8.58", {"start": v(-41.94, 35.7) * mm, "end": v(-47.92, 35.7) * mm});
            skLineSegment(sketch, "E25.1.8.59", {"start": v(-32.72, 35.6) * mm, "end": v(-38.72, 35.6) * mm});
            skLineSegment(sketch, "E25.1.8.60", {"start": v(-38.82, 33.6) * mm, "end": v(-38.82, 35.6) * mm});
            skLineSegment(sketch, "E25.1.8.61", {"start": v(-54.14, 35.7) * mm, "end": v(-54.14, 37.7) * mm});
            skLineSegment(sketch, "E25.1.8.62", {"start": v(-8.32, 33.6) * mm, "end": v(-8.32, 35.6) * mm});
            skLineSegment(sketch, "E25.1.8.63", {"start": v(-54.04, 37.7) * mm, "end": v(-54.02, 35.7) * mm});
            skLineSegment(sketch, "E25.1.8.64", {"start": v(-29.64, 37.7) * mm, "end": v(-29.62, 35.7) * mm});
            skLineSegment(sketch, "E25.1.8.65", {"start": v(-5.34, 35.7) * mm, "end": v(-11.32, 35.7) * mm});
            skLineSegment(sketch, "E25.1.8.66", {"start": v(-51.02, 33.6) * mm, "end": v(-51.02, 35.6) * mm});
            skLineSegment(sketch, "E25.1.8.67", {"start": v(-29.74, 35.7) * mm, "end": v(-35.72, 35.7) * mm});
            skLineSegment(sketch, "E25.1.8.68", {"start": v(-44.92, 33.6) * mm, "end": v(-44.92, 35.6) * mm});
            skLineSegment(sketch, "E25.1.8.69", {"start": v(-20.52, 33.6) * mm, "end": v(-20.52, 35.6) * mm});
            skLineSegment(sketch, "E25.1.8.70", {"start": v(-41.94, 35.7) * mm, "end": v(-41.94, 37.7) * mm});
            skLineSegment(sketch, "E25.1.8.71", {"start": v(-38.72, 35.6) * mm, "end": v(-38.72, 33.6) * mm});
            skLineSegment(sketch, "E25.1.8.72", {"start": v(-35.84, 35.7) * mm, "end": v(-35.84, 37.7) * mm});
            skLineSegment(sketch, "E25.1.8.73", {"start": v(-11.44, 35.7) * mm, "end": v(-11.44, 37.7) * mm});
            skLineSegment(sketch, "E25.1.8.74", {"start": v(-38.82, 35.6) * mm, "end": v(-44.82, 35.6) * mm});
            skLineSegment(sketch, "E25.1.8.75", {"start": v(-14.32, 35.6) * mm, "end": v(-14.32, 33.6) * mm});
            skLineSegment(sketch, "E25.1.8.76", {"start": v(3.88, 33.6) * mm, "end": v(3.88, 35.6) * mm});
            skLineSegment(sketch, "E25.1.8.77", {"start": v(3.88, 35.6) * mm, "end": v(-2.12, 35.6) * mm});
            skLineSegment(sketch, "E25.1.8.78", {"start": v(-2.12, 35.6) * mm, "end": v(-2.12, 33.6) * mm});
            skLineSegment(sketch, "E25.1.8.79", {"start": v(-2.22, 33.6) * mm, "end": v(-2.22, 35.6) * mm});
            skLineSegment(sketch, "E25.1.8.80", {"start": v(-8.22, 35.6) * mm, "end": v(-8.22, 33.6) * mm});
            skLineSegment(sketch, "E25.1.8.81", {"start": v(0.86, 37.7) * mm, "end": v(3.88, 37.7) * mm});
            skLineSegment(sketch, "E25.1.8.84", {"start": v(3.88, 35.7) * mm, "end": v(0.86, 35.7) * mm});
            skLineSegment(sketch, "E25.1.8.85", {"start": v(0.76, 35.7) * mm, "end": v(-5.22, 35.7) * mm});
            skLineSegment(sketch, "E25.1.8.86", {"start": v(0.86, 35.7) * mm, "end": v(0.86, 37.7) * mm});
            skLineSegment(sketch, "E25.1.8.87", {"start": v(-5.34, 35.7) * mm, "end": v(-5.34, 37.7) * mm});
            skLineSegment(sketch, "E25.1.8.88", {"start": v(-5.24, 37.7) * mm, "end": v(-5.22, 35.7) * mm});
            skLineSegment(sketch, "E25.1.8.89", {"start": v(0.76, 35.7) * mm, "end": v(0.76, 37.7) * mm});
            skLineSegment(sketch, "E25.1.8.90", {"start": v(-2.12, 33.6) * mm, "end": v(-2.22, 33.6) * mm});
            skLineSegment(sketch, "E25.1.8.91", {"start": v(0.86, 35.7) * mm, "end": v(0.76, 35.7) * mm});
            skLineSegment(sketch, "E25.1.9.0", {"start": v(-35.84, 41.9) * mm, "end": v(-41.84, 41.9) * mm});
            skLineSegment(sketch, "E25.1.9.1", {"start": v(-11.44, 41.9) * mm, "end": v(-17.44, 41.9) * mm});
            skLineSegment(sketch, "E25.1.9.2", {"start": v(-48.04, 41.9) * mm, "end": v(-54.04, 41.9) * mm});
            skLineSegment(sketch, "E25.1.9.3", {"start": v(-23.64, 41.9) * mm, "end": v(-29.64, 41.9) * mm});
            skLineSegment(sketch, "E25.1.9.4", {"start": v(-41.94, 41.9) * mm, "end": v(-47.94, 41.9) * mm});
            skLineSegment(sketch, "E25.1.9.5", {"start": v(-17.54, 41.9) * mm, "end": v(-23.54, 41.9) * mm});
            skLineSegment(sketch, "E25.1.9.6", {"start": v(-5.34, 41.9) * mm, "end": v(-11.34, 41.9) * mm});
            skLineSegment(sketch, "E25.1.9.7", {"start": v(-54.14, 41.9) * mm, "end": v(-60.14, 41.9) * mm});
            skLineSegment(sketch, "E25.1.9.8", {"start": v(-29.74, 41.9) * mm, "end": v(-35.74, 41.9) * mm});
            skLineSegment(sketch, "E25.1.9.9", {"start": v(-20.42, 37.8) * mm, "end": v(-14.42, 37.8) * mm});
            skLineSegment(sketch, "E25.1.9.10", {"start": v(-44.82, 37.8) * mm, "end": v(-38.82, 37.8) * mm});
            skLineSegment(sketch, "E25.1.9.11", {"start": v(-57.02, 37.8) * mm, "end": v(-51.02, 37.8) * mm});
            skLineSegment(sketch, "E25.1.9.12", {"start": v(-32.62, 37.8) * mm, "end": v(-26.62, 37.8) * mm});
            skLineSegment(sketch, "E25.1.9.13", {"start": v(-50.92, 37.8) * mm, "end": v(-44.92, 37.8) * mm});
            skLineSegment(sketch, "E25.1.9.14", {"start": v(-26.52, 37.8) * mm, "end": v(-20.52, 37.8) * mm});
            skPoint(sketch, "E25.1.9.15", {"position": v(-5.22, 39.8) * mm});
            skLineSegment(sketch, "E25.1.9.16", {"start": v(-63.12, 37.8) * mm, "end": v(-57.12, 37.8) * mm});
            skLineSegment(sketch, "E25.1.9.17", {"start": v(-38.72, 37.8) * mm, "end": v(-32.72, 37.8) * mm});
            skLineSegment(sketch, "E25.1.9.18", {"start": v(-14.32, 37.8) * mm, "end": v(-8.32, 37.8) * mm});
            skLineSegment(sketch, "E25.1.9.20", {"start": v(0.76, 41.9) * mm, "end": v(-5.24, 41.9) * mm});
            skLineSegment(sketch, "E25.1.9.21", {"start": v(-63.12, 39.8) * mm, "end": v(-63.12, 37.8) * mm});
            skLineSegment(sketch, "E25.1.9.22", {"start": v(-8.22, 37.8) * mm, "end": v(-2.22, 37.8) * mm});
            skLineSegment(sketch, "E25.1.9.23", {"start": v(-23.54, 41.9) * mm, "end": v(-23.52, 39.9) * mm});
            skLineSegment(sketch, "E25.1.9.24", {"start": v(-60.14, 41.9) * mm, "end": v(-60.12, 39.9) * mm});
            skLineSegment(sketch, "E25.1.9.25", {"start": v(-57.12, 39.8) * mm, "end": v(-63.12, 39.8) * mm});
            skLineSegment(sketch, "E25.1.9.26", {"start": v(-54.14, 39.9) * mm, "end": v(-60.12, 39.9) * mm});
            skLineSegment(sketch, "E25.1.9.27", {"start": v(-20.52, 39.8) * mm, "end": v(-26.52, 39.8) * mm});
            skLineSegment(sketch, "E25.1.9.28", {"start": v(-51.02, 39.8) * mm, "end": v(-57.02, 39.8) * mm});
            skLineSegment(sketch, "E25.1.9.29", {"start": v(-23.64, 39.9) * mm, "end": v(-23.64, 41.9) * mm});
            skLineSegment(sketch, "E25.1.9.30", {"start": v(-57.02, 39.8) * mm, "end": v(-57.02, 37.8) * mm});
            skLineSegment(sketch, "E25.1.9.31", {"start": v(-57.12, 37.8) * mm, "end": v(-57.12, 39.8) * mm});
            skLineSegment(sketch, "E25.1.9.32", {"start": v(-17.54, 39.9) * mm, "end": v(-23.52, 39.9) * mm});
            skLineSegment(sketch, "E25.1.9.33", {"start": v(-26.62, 37.8) * mm, "end": v(-26.62, 39.8) * mm});
            skLineSegment(sketch, "E25.1.9.34", {"start": v(-48.04, 39.9) * mm, "end": v(-54.02, 39.9) * mm});
            skLineSegment(sketch, "E25.1.9.35", {"start": v(-23.64, 39.9) * mm, "end": v(-29.62, 39.9) * mm});
            skLineSegment(sketch, "E25.1.9.36", {"start": v(-17.54, 39.9) * mm, "end": v(-17.54, 41.9) * mm});
            skLineSegment(sketch, "E25.1.9.37", {"start": v(-44.92, 39.8) * mm, "end": v(-50.92, 39.8) * mm});
            skLineSegment(sketch, "E25.1.9.38", {"start": v(-14.42, 39.8) * mm, "end": v(-20.42, 39.8) * mm});
            skLineSegment(sketch, "E25.1.9.39", {"start": v(-26.62, 39.8) * mm, "end": v(-32.62, 39.8) * mm});
            skLineSegment(sketch, "E25.1.9.40", {"start": v(-48.04, 39.9) * mm, "end": v(-48.04, 41.9) * mm});
            skLineSegment(sketch, "E25.1.9.41", {"start": v(-26.52, 39.8) * mm, "end": v(-26.52, 37.8) * mm});
            skLineSegment(sketch, "E25.1.9.42", {"start": v(-41.84, 41.9) * mm, "end": v(-41.82, 39.9) * mm});
            skLineSegment(sketch, "E25.1.9.43", {"start": v(-17.44, 41.9) * mm, "end": v(-17.42, 39.9) * mm});
            skLineSegment(sketch, "E25.1.9.44", {"start": v(-50.92, 39.8) * mm, "end": v(-50.92, 37.8) * mm});
            skLineSegment(sketch, "E25.1.9.45", {"start": v(-8.32, 39.8) * mm, "end": v(-14.32, 39.8) * mm});
            skLineSegment(sketch, "E25.1.9.46", {"start": v(-20.42, 39.8) * mm, "end": v(-20.42, 37.8) * mm});
            skLineSegment(sketch, "E25.1.9.47", {"start": v(-44.82, 39.8) * mm, "end": v(-44.82, 37.8) * mm});
            skLineSegment(sketch, "E25.1.9.48", {"start": v(-2.22, 39.8) * mm, "end": v(-8.22, 39.8) * mm});
            skLineSegment(sketch, "E25.1.9.49", {"start": v(-32.62, 39.8) * mm, "end": v(-32.62, 37.8) * mm});
            skLineSegment(sketch, "E25.1.9.50", {"start": v(-47.94, 41.9) * mm, "end": v(-47.92, 39.9) * mm});
            skLineSegment(sketch, "E25.1.9.51", {"start": v(-35.84, 39.9) * mm, "end": v(-41.82, 39.9) * mm});
            skLineSegment(sketch, "E25.1.9.52", {"start": v(-11.44, 39.9) * mm, "end": v(-17.42, 39.9) * mm});
            skLineSegment(sketch, "E25.1.9.53", {"start": v(-32.72, 37.8) * mm, "end": v(-32.72, 39.8) * mm});
            skLineSegment(sketch, "E25.1.9.54", {"start": v(-11.34, 41.9) * mm, "end": v(-11.32, 39.9) * mm});
            skLineSegment(sketch, "E25.1.9.55", {"start": v(-35.74, 41.9) * mm, "end": v(-35.72, 39.9) * mm});
            skLineSegment(sketch, "E25.1.9.56", {"start": v(-14.42, 37.8) * mm, "end": v(-14.42, 39.8) * mm});
            skLineSegment(sketch, "E25.1.9.57", {"start": v(-29.74, 39.9) * mm, "end": v(-29.74, 41.9) * mm});
            skLineSegment(sketch, "E25.1.9.58", {"start": v(-41.94, 39.9) * mm, "end": v(-47.92, 39.9) * mm});
            skLineSegment(sketch, "E25.1.9.59", {"start": v(-32.72, 39.8) * mm, "end": v(-38.72, 39.8) * mm});
            skLineSegment(sketch, "E25.1.9.60", {"start": v(-38.82, 37.8) * mm, "end": v(-38.82, 39.8) * mm});
            skLineSegment(sketch, "E25.1.9.61", {"start": v(-54.14, 39.9) * mm, "end": v(-54.14, 41.9) * mm});
            skLineSegment(sketch, "E25.1.9.62", {"start": v(-8.32, 37.8) * mm, "end": v(-8.32, 39.8) * mm});
            skLineSegment(sketch, "E25.1.9.63", {"start": v(-54.04, 41.9) * mm, "end": v(-54.02, 39.9) * mm});
            skLineSegment(sketch, "E25.1.9.64", {"start": v(-29.64, 41.9) * mm, "end": v(-29.62, 39.9) * mm});
            skLineSegment(sketch, "E25.1.9.65", {"start": v(-5.34, 39.9) * mm, "end": v(-11.32, 39.9) * mm});
            skLineSegment(sketch, "E25.1.9.66", {"start": v(-51.02, 37.8) * mm, "end": v(-51.02, 39.8) * mm});
            skLineSegment(sketch, "E25.1.9.67", {"start": v(-29.74, 39.9) * mm, "end": v(-35.72, 39.9) * mm});
            skLineSegment(sketch, "E25.1.9.68", {"start": v(-44.92, 37.8) * mm, "end": v(-44.92, 39.8) * mm});
            skLineSegment(sketch, "E25.1.9.69", {"start": v(-20.52, 37.8) * mm, "end": v(-20.52, 39.8) * mm});
            skLineSegment(sketch, "E25.1.9.70", {"start": v(-41.94, 39.9) * mm, "end": v(-41.94, 41.9) * mm});
            skLineSegment(sketch, "E25.1.9.71", {"start": v(-38.72, 39.8) * mm, "end": v(-38.72, 37.8) * mm});
            skLineSegment(sketch, "E25.1.9.72", {"start": v(-35.84, 39.9) * mm, "end": v(-35.84, 41.9) * mm});
            skLineSegment(sketch, "E25.1.9.73", {"start": v(-11.44, 39.9) * mm, "end": v(-11.44, 41.9) * mm});
            skLineSegment(sketch, "E25.1.9.74", {"start": v(-38.82, 39.8) * mm, "end": v(-44.82, 39.8) * mm});
            skLineSegment(sketch, "E25.1.9.75", {"start": v(-14.32, 39.8) * mm, "end": v(-14.32, 37.8) * mm});
            skLineSegment(sketch, "E25.1.9.76", {"start": v(3.88, 37.8) * mm, "end": v(3.88, 39.8) * mm});
            skLineSegment(sketch, "E25.1.9.78", {"start": v(-2.12, 39.8) * mm, "end": v(-2.12, 37.8) * mm});
            skLineSegment(sketch, "E25.1.9.79", {"start": v(-2.22, 37.8) * mm, "end": v(-2.22, 39.8) * mm});
            skLineSegment(sketch, "E25.1.9.80", {"start": v(-8.22, 39.8) * mm, "end": v(-8.22, 37.8) * mm});
            skLineSegment(sketch, "E25.1.9.81", {"start": v(0.86, 41.9) * mm, "end": v(3.88, 41.9) * mm});
            skLineSegment(sketch, "E25.1.9.84", {"start": v(3.88, 39.9) * mm, "end": v(0.86, 39.9) * mm});
            skLineSegment(sketch, "E25.1.9.85", {"start": v(0.76, 39.9) * mm, "end": v(-5.22, 39.9) * mm});
            skLineSegment(sketch, "E25.1.9.86", {"start": v(0.86, 39.9) * mm, "end": v(0.86, 41.9) * mm});
            skLineSegment(sketch, "E25.1.9.87", {"start": v(-5.34, 39.9) * mm, "end": v(-5.34, 41.9) * mm});
            skLineSegment(sketch, "E25.1.9.88", {"start": v(-5.24, 41.9) * mm, "end": v(-5.22, 39.9) * mm});
            skLineSegment(sketch, "E25.1.9.89", {"start": v(0.76, 39.9) * mm, "end": v(0.76, 41.9) * mm});
            skLineSegment(sketch, "E25.1.9.90", {"start": v(-2.12, 37.8) * mm, "end": v(-2.22, 37.8) * mm});
            skLineSegment(sketch, "E25.1.9.91", {"start": v(0.86, 39.9) * mm, "end": v(0.76, 39.9) * mm});
            skLineSegment(sketch, "E25.direction1", {"start": v(3.88, 0) * mm, "end": v(-63.12, 0) * mm, "construction": true});
            skLineSegment(sketch, "E26", {"start": v(9.93, 2) * mm, "end": v(3.93, 2) * mm});
            skLineSegment(sketch, "E27", {"start": v(9.93, 0) * mm, "end": v(3.88, 0) * mm});
            skLineSegment(sketch, "E28", {"start": v(3.93, 2) * mm, "end": v(3.83, 2) * mm});
            skLineSegment(sketch, "E29", {"start": v(3.93, 2) * mm, "end": v(3.93, 0) * mm});
            skLineSegment(sketch, "E30", {"start": v(3.83, 2) * mm, "end": v(3.83, 0) * mm});
            skLineSegment(sketch, "E31", {"start": v(3.83, 0) * mm, "end": v(3.93, 0) * mm});
            skLineSegment(sketch, "E32", {"start": v(3.83, 2) * mm, "end": v(-2.12, 2) * mm});
            skLineSegment(sketch, "E33", {"start": v(0.86, 2.1) * mm, "end": v(6.86, 2.1) * mm});
            skLineSegment(sketch, "E34", {"start": v(6.86, 2.1) * mm, "end": v(6.86, 4.1) * mm});
            skLineSegment(sketch, "E35", {"start": v(6.86, 4.1) * mm, "end": v(0.86, 4.1) * mm});
            skLineSegment(sketch, "E36", {"start": v(6.86, 4.1) * mm, "end": v(6.96, 4.1) * mm});
            skLineSegment(sketch, "E37", {"start": v(6.96, 4.1) * mm, "end": v(6.96, 2.1) * mm});
            skLineSegment(sketch, "E38", {"start": v(6.96, 4.1) * mm, "end": v(12.86, 4.1) * mm});
            skLineSegment(sketch, "E39", {"start": v(12.86, 2.1) * mm, "end": v(6.96, 2.1) * mm});
            skLineSegment(sketch, "E40", {"start": v(9.98, 4.2) * mm, "end": v(9.88, 4.2) * mm});
            skLineSegment(sketch, "E41", {"start": v(9.98, 6.2) * mm, "end": v(9.88, 6.2) * mm});
            skLineSegment(sketch, "E42", {"start": v(9.88, 4.2) * mm, "end": v(9.88, 6.2) * mm});
            skLineSegment(sketch, "E43", {"start": v(9.88, 6.2) * mm, "end": v(3.88, 6.2) * mm});
            skLineSegment(sketch, "E44", {"start": v(9.88, 4.2) * mm, "end": v(3.88, 4.2) * mm});
            skLineSegment(sketch, "E45", {"start": v(3.88, 4.2) * mm, "end": v(3.88, 6.2) * mm});
            skLineSegment(sketch, "E46", {"start": v(3.88, 6.2) * mm, "end": v(3.78, 6.2) * mm});
            skLineSegment(sketch, "E47", {"start": v(3.78, 6.2) * mm, "end": v(3.78, 4.2) * mm});
            skLineSegment(sketch, "E48", {"start": v(3.78, 6.2) * mm, "end": v(-2.12, 6.2) * mm});
            skLineSegment(sketch, "E49", {"start": v(-2.12, 4.2) * mm, "end": v(3.78, 4.2) * mm});
            skLineSegment(sketch, "E50", {"start": v(6.88, 6.3) * mm, "end": v(6.78, 6.3) * mm});
            skLineSegment(sketch, "E51", {"start": v(6.78, 6.3) * mm, "end": v(6.76, 8.3) * mm});
            skLineSegment(sketch, "E52", {"start": v(6.76, 8.3) * mm, "end": v(3.88, 8.3) * mm});
            skLineSegment(sketch, "E53", {"start": v(3.88, 6.3) * mm, "end": v(6.78, 6.3) * mm});
            skLineSegment(sketch, "E54", {"start": v(3.88, 8.4) * mm, "end": v(3.98, 8.4) * mm});
            skLineSegment(sketch, "E55", {"start": v(3.98, 8.4) * mm, "end": v(3.98, 10.4) * mm});
            skLineSegment(sketch, "E56", {"start": v(9.88, 10.4) * mm, "end": v(3.98, 10.4) * mm});
            skLineSegment(sketch, "E57", {"start": v(3.98, 8.4) * mm, "end": v(9.88, 8.4) * mm});
            skLineSegment(sketch, "E58", {"start": v(6.88, 10.52) * mm, "end": v(6.78, 10.52) * mm});
            skLineSegment(sketch, "E59", {"start": v(6.78, 10.52) * mm, "end": v(6.76, 12.52) * mm});
            skLineSegment(sketch, "E60", {"start": v(6.76, 12.52) * mm, "end": v(3.88, 12.5) * mm});
            skLineSegment(sketch, "E61", {"start": v(6.78, 10.52) * mm, "end": v(3.88, 10.5) * mm});
            skLineSegment(sketch, "E62", {"start": v(3.88, 14.6) * mm, "end": v(3.98, 14.6) * mm});
            skLineSegment(sketch, "E63", {"start": v(3.98, 14.6) * mm, "end": v(3.99, 12.6) * mm});
            skLineSegment(sketch, "E64", {"start": v(9.88, 14.6) * mm, "end": v(3.98, 14.6) * mm});
            skLineSegment(sketch, "E65", {"start": v(3.99, 12.6) * mm, "end": v(9.88, 12.6) * mm});
            skLineSegment(sketch, "E66", {"start": v(6.88, 14.7) * mm, "end": v(6.78, 14.7) * mm});
            skLineSegment(sketch, "E67", {"start": v(6.78, 14.7) * mm, "end": v(6.78, 16.7) * mm});
            skLineSegment(sketch, "E68", {"start": v(6.78, 16.7) * mm, "end": v(3.88, 16.7) * mm});
            skLineSegment(sketch, "E69", {"start": v(3.88, 14.7) * mm, "end": v(6.78, 14.7) * mm});
            skLineSegment(sketch, "E70", {"start": v(3.88, 18.8) * mm, "end": v(3.78, 18.8) * mm});
            skLineSegment(sketch, "E71", {"start": v(3.78, 18.8) * mm, "end": v(3.78, 16.8) * mm});
            skLineSegment(sketch, "E72", {"start": v(3.78, 16.8) * mm, "end": v(-2.12, 16.8) * mm});
            skLineSegment(sketch, "E73", {"start": v(-2.12, 18.8) * mm, "end": v(3.78, 18.8) * mm});
            skLineSegment(sketch, "E74", {"start": v(6.88, 18.9) * mm, "end": v(6.78, 18.9) * mm});
            skLineSegment(sketch, "E75", {"start": v(6.78, 18.9) * mm, "end": v(6.78, 20.9) * mm});
            skLineSegment(sketch, "E76", {"start": v(6.78, 20.9) * mm, "end": v(3.88, 20.9) * mm});
            skLineSegment(sketch, "E77", {"start": v(3.88, 18.9) * mm, "end": v(6.78, 18.9) * mm});
            skLineSegment(sketch, "E78", {"start": v(3.88, 21) * mm, "end": v(3.98, 21) * mm});
            skLineSegment(sketch, "E79", {"start": v(3.98, 21) * mm, "end": v(3.98, 23) * mm});
            skLineSegment(sketch, "E80", {"start": v(9.88, 23) * mm, "end": v(3.98, 23) * mm});
            skLineSegment(sketch, "E81", {"start": v(3.98, 21) * mm, "end": v(9.88, 21) * mm});
            skLineSegment(sketch, "E82", {"start": v(6.88, 23.1) * mm, "end": v(6.78, 23.1) * mm});
            skLineSegment(sketch, "E83", {"start": v(6.78, 23.1) * mm, "end": v(6.76, 25.1) * mm});
            skLineSegment(sketch, "E84", {"start": v(6.76, 25.1) * mm, "end": v(3.88, 25.1) * mm});
            skLineSegment(sketch, "E85", {"start": v(6.78, 23.1) * mm, "end": v(0.86, 23.1) * mm});
            skLineSegment(sketch, "E86", {"start": v(3.88, 25.2) * mm, "end": v(3.78, 25.2) * mm});
            skLineSegment(sketch, "E87", {"start": v(3.78, 25.2) * mm, "end": v(3.78, 27.2) * mm});
            skLineSegment(sketch, "E88", {"start": v(3.78, 27.2) * mm, "end": v(-2.12, 27.2) * mm});
            skLineSegment(sketch, "E89", {"start": v(-2.12, 25.2) * mm, "end": v(3.78, 25.2) * mm});
            skLineSegment(sketch, "E90", {"start": v(6.88, 27.3) * mm, "end": v(6.78, 27.3) * mm});
            skLineSegment(sketch, "E91", {"start": v(6.78, 27.3) * mm, "end": v(6.78, 29.3) * mm});
            skLineSegment(sketch, "E92", {"start": v(6.78, 27.3) * mm, "end": v(3.88, 27.3) * mm});
            skLineSegment(sketch, "E93", {"start": v(3.88, 29.3) * mm, "end": v(6.78, 29.3) * mm});
            skLineSegment(sketch, "E94", {"start": v(3.88, 31.4) * mm, "end": v(3.98, 31.4) * mm});
            skLineSegment(sketch, "E95", {"start": v(3.98, 31.4) * mm, "end": v(3.98, 29.4) * mm});
            skLineSegment(sketch, "E96", {"start": v(9.88, 31.4) * mm, "end": v(3.98, 31.4) * mm});
            skLineSegment(sketch, "E97", {"start": v(3.98, 29.4) * mm, "end": v(9.88, 29.4) * mm});
            skLineSegment(sketch, "E98", {"start": v(6.88, 31.5) * mm, "end": v(6.78, 31.5) * mm});
            skLineSegment(sketch, "E99", {"start": v(6.78, 31.5) * mm, "end": v(6.78, 33.5) * mm});
            skLineSegment(sketch, "E100", {"start": v(6.78, 33.5) * mm, "end": v(3.88, 33.5) * mm});
            skLineSegment(sketch, "E101", {"start": v(6.78, 31.5) * mm, "end": v(0.86, 31.5) * mm});
            skLineSegment(sketch, "E102", {"start": v(3.88, 35.6) * mm, "end": v(3.98, 35.6) * mm});
            skLineSegment(sketch, "E103", {"start": v(3.98, 35.6) * mm, "end": v(3.98, 33.6) * mm});
            skLineSegment(sketch, "E104", {"start": v(3.98, 35.6) * mm, "end": v(9.88, 35.6) * mm});
            skLineSegment(sketch, "E105", {"start": v(3.98, 33.6) * mm, "end": v(9.88, 33.6) * mm});
            skLineSegment(sketch, "E106", {"start": v(6.88, 35.7) * mm, "end": v(6.78, 35.7) * mm});
            skLineSegment(sketch, "E107", {"start": v(6.78, 35.7) * mm, "end": v(6.76, 37.7) * mm});
            skLineSegment(sketch, "E108", {"start": v(6.76, 37.7) * mm, "end": v(3.88, 37.7) * mm});
            skLineSegment(sketch, "E109", {"start": v(3.88, 35.7) * mm, "end": v(6.78, 35.7) * mm});
            skLineSegment(sketch, "E110", {"start": v(3.88, 39.8) * mm, "end": v(3.78, 39.8) * mm});
            skLineSegment(sketch, "E111", {"start": v(3.78, 39.8) * mm, "end": v(3.78, 37.8) * mm});
            skLineSegment(sketch, "E112", {"start": v(3.78, 39.8) * mm, "end": v(-2.12, 39.8) * mm});
            skLineSegment(sketch, "E113", {"start": v(-2.12, 37.8) * mm, "end": v(3.78, 37.8) * mm});
            skLineSegment(sketch, "E114", {"start": v(6.88, 39.9) * mm, "end": v(6.78, 39.9) * mm});
            skLineSegment(sketch, "E115", {"start": v(6.78, 39.9) * mm, "end": v(6.76, 41.9) * mm});
            skLineSegment(sketch, "E116", {"start": v(6.76, 41.9) * mm, "end": v(3.88, 41.9) * mm});
            skLineSegment(sketch, "E117", {"start": v(3.88, 39.9) * mm, "end": v(6.78, 39.9) * mm});
            skLineSegment(sketch, "E118", {"start": v(-63.12, 2) * mm, "end": v(-63.22, 2) * mm});
            skLineSegment(sketch, "E119", {"start": v(-63.22, 2) * mm, "end": v(-63.22, 0) * mm});
            skLineSegment(sketch, "E120", {"start": v(-63.22, 2) * mm, "end": v(-68.5, 2) * mm});
            skLineSegment(sketch, "E121", {"start": v(-60.12, 2.1) * mm, "end": v(-60.22, 2.1) * mm});
            skLineSegment(sketch, "E122", {"start": v(-60.22, 2.1) * mm, "end": v(-60.22, 4.1) * mm});
            skLineSegment(sketch, "E123", {"start": v(-60.22, 2.1) * mm, "end": v(-66.22, 2.1) * mm});
            skLineSegment(sketch, "E124", {"start": v(-60.22, 4.1) * mm, "end": v(-66.22, 4.1) * mm});
            skLineSegment(sketch, "E125", {"start": v(-66.22, 4.1) * mm, "end": v(-66.22, 2.1) * mm});
            skLineSegment(sketch, "E126", {"start": v(-66.22, 2.1) * mm, "end": v(-66.32, 2.1) * mm});
            skLineSegment(sketch, "E127", {"start": v(-66.32, 2.1) * mm, "end": v(-66.32, 4.1) * mm});
            skLineSegment(sketch, "E128", {"start": v(-66.32, 4.1) * mm, "end": v(-68.5, 4.1) * mm});
            skLineSegment(sketch, "E129", {"start": v(-66.32, 2.1) * mm, "end": v(-68.5, 2.1) * mm});
            skLineSegment(sketch, "E130", {"start": v(-68.5, 2.1) * mm, "end": v(-68.5, 4.1) * mm});
            skLineSegment(sketch, "E131", {"start": v(-63.12, 4.2) * mm, "end": v(-63.22, 4.2) * mm});
            skLineSegment(sketch, "E132", {"start": v(-63.12, 6.2) * mm, "end": v(-68.5, 6.2) * mm});
            skLineSegment(sketch, "E133", {"start": v(-63.22, 4.2) * mm, "end": v(-63.22, 6.2) * mm});
            skLineSegment(sketch, "E134", {"start": v(-63.22, 4.2) * mm, "end": v(-68.5, 4.2) * mm});
            skLineSegment(sketch, "E135", {"start": v(-68.5, 4.2) * mm, "end": v(-68.5, 6.2) * mm});
            skLineSegment(sketch, "E136", {"start": v(-47.94, 8.32) * mm, "end": v(-48.04, 8.32) * mm});
            skLineSegment(sketch, "E137", {"start": v(-41.94, 6.32) * mm, "end": v(-41.82, 6.32) * mm});
            skLineSegment(sketch, "E138", {"start": v(-54.02, 6.32) * mm, "end": v(-54.04, 8.32) * mm});
            skLineSegment(sketch, "E139", {"start": v(-54.02, 6.32) * mm, "end": v(-54.14, 6.32) * mm});
            skLineSegment(sketch, "E140", {"start": v(-54.14, 6.32) * mm, "end": v(-54.15, 8.32) * mm});
            skLineSegment(sketch, "E141", {"start": v(-54.15, 8.32) * mm, "end": v(-60.15, 8.32) * mm});
            skLineSegment(sketch, "E142", {"start": v(-60.15, 8.32) * mm, "end": v(-60.14, 6.32) * mm});
            skLineSegment(sketch, "E143", {"start": v(-60.14, 6.32) * mm, "end": v(-54.14, 6.32) * mm});
            skLineSegment(sketch, "E144", {"start": v(-60.14, 6.32) * mm, "end": v(-60.24, 6.32) * mm});
            skLineSegment(sketch, "E145", {"start": v(-60.24, 6.32) * mm, "end": v(-60.25, 8.32) * mm});
            skLineSegment(sketch, "E146", {"start": v(-60.25, 8.32) * mm, "end": v(-66.25, 8.32) * mm});
            skLineSegment(sketch, "E147", {"start": v(-66.25, 8.32) * mm, "end": v(-66.25, 6.32) * mm});
            skLineSegment(sketch, "E148", {"start": v(-66.25, 6.32) * mm, "end": v(-60.24, 6.32) * mm});
            skLineSegment(sketch, "E149", {"start": v(-66.25, 6.32) * mm, "end": v(-66.35, 6.32) * mm});
            skLineSegment(sketch, "E150", {"start": v(-66.35, 6.32) * mm, "end": v(-66.35, 8.32) * mm});
            skLineSegment(sketch, "E151", {"start": v(-66.35, 6.32) * mm, "end": v(-68.5, 6.32) * mm});
            skLineSegment(sketch, "E152", {"start": v(-66.35, 8.32) * mm, "end": v(-68.5, 8.32) * mm});
            skLineSegment(sketch, "E153", {"start": v(-68.5, 8.32) * mm, "end": v(-68.5, 6.32) * mm});
            skLineSegment(sketch, "E154", {"start": v(-63.12, 8.4) * mm, "end": v(-63.22, 8.4) * mm});
            skLineSegment(sketch, "E155", {"start": v(-63.22, 8.4) * mm, "end": v(-63.22, 10.4) * mm});
            skLineSegment(sketch, "E156", {"start": v(-63.22, 8.4) * mm, "end": v(-68.5, 8.4) * mm});
            skLineSegment(sketch, "E157", {"start": v(-63.22, 10.4) * mm, "end": v(-68.5, 10.4) * mm});
            skLineSegment(sketch, "E158", {"start": v(-68.5, 10.4) * mm, "end": v(-68.5, 8.4) * mm});
            skLineSegment(sketch, "E159", {"start": v(-60.12, 10.5) * mm, "end": v(-60.22, 10.5) * mm});
            skLineSegment(sketch, "E160", {"start": v(-60.22, 10.5) * mm, "end": v(-60.24, 12.5) * mm});
            skLineSegment(sketch, "E161", {"start": v(-60.22, 10.5) * mm, "end": v(-66.22, 10.5) * mm});
            skLineSegment(sketch, "E162", {"start": v(-66.22, 10.5) * mm, "end": v(-66.22, 12.5) * mm});
            skLineSegment(sketch, "E163", {"start": v(-60.24, 12.5) * mm, "end": v(-66.22, 12.5) * mm});
            skLineSegment(sketch, "E164", {"start": v(-66.22, 10.5) * mm, "end": v(-66.35, 10.5) * mm});
            skLineSegment(sketch, "E165", {"start": v(-66.35, 10.5) * mm, "end": v(-66.35, 12.5) * mm});
            skLineSegment(sketch, "E166", {"start": v(-66.35, 10.5) * mm, "end": v(-68.5, 10.5) * mm});
            skLineSegment(sketch, "E167", {"start": v(-66.35, 12.5) * mm, "end": v(-68.5, 12.5) * mm});
            skLineSegment(sketch, "E168", {"start": v(-68.5, 12.5) * mm, "end": v(-68.5, 10.5) * mm});
            skLineSegment(sketch, "E169", {"start": v(-63.12, 12.6) * mm, "end": v(-63.22, 12.6) * mm});
            skLineSegment(sketch, "E170", {"start": v(-63.22, 12.6) * mm, "end": v(-63.22, 14.6) * mm});
            skLineSegment(sketch, "E171", {"start": v(-63.22, 14.6) * mm, "end": v(-68.5, 14.6) * mm});
            skLineSegment(sketch, "E172", {"start": v(-63.22, 12.6) * mm, "end": v(-68.5, 12.6) * mm});
            skLineSegment(sketch, "E173", {"start": v(-68.5, 12.6) * mm, "end": v(-68.5, 14.6) * mm});
            skLineSegment(sketch, "E174", {"start": v(-60.12, 14.7) * mm, "end": v(-60.22, 14.7) * mm});
            skLineSegment(sketch, "E175", {"start": v(-60.22, 14.7) * mm, "end": v(-60.24, 16.7) * mm});
            skLineSegment(sketch, "E176", {"start": v(-60.22, 14.7) * mm, "end": v(-66.22, 14.7) * mm});
            skLineSegment(sketch, "E177", {"start": v(-66.22, 14.7) * mm, "end": v(-66.22, 16.7) * mm});
            skLineSegment(sketch, "E178", {"start": v(-66.22, 16.7) * mm, "end": v(-60.24, 16.7) * mm});
            skLineSegment(sketch, "E179", {"start": v(-66.22, 14.7) * mm, "end": v(-66.32, 14.7) * mm});
            skLineSegment(sketch, "E180", {"start": v(-66.32, 14.7) * mm, "end": v(-66.32, 16.7) * mm});
            skLineSegment(sketch, "E181", {"start": v(-66.32, 16.7) * mm, "end": v(-68.5, 16.7) * mm});
            skLineSegment(sketch, "E182", {"start": v(-66.32, 14.7) * mm, "end": v(-68.5, 14.7) * mm});
            skLineSegment(sketch, "E183", {"start": v(-68.5, 14.7) * mm, "end": v(-68.5, 16.7) * mm});
            skLineSegment(sketch, "E184", {"start": v(-63.12, 16.8) * mm, "end": v(-63.22, 16.8) * mm});
            skLineSegment(sketch, "E185", {"start": v(-63.22, 16.8) * mm, "end": v(-63.22, 18.8) * mm});
            skLineSegment(sketch, "E186", {"start": v(-63.22, 18.8) * mm, "end": v(-68.5, 18.8) * mm});
            skLineSegment(sketch, "E187", {"start": v(-63.22, 16.8) * mm, "end": v(-68.5, 16.8) * mm});
            skLineSegment(sketch, "E188", {"start": v(-68.5, 16.8) * mm, "end": v(-68.5, 18.8) * mm});
            skLineSegment(sketch, "E189", {"start": v(-60.12, 18.9) * mm, "end": v(-60.22, 18.9) * mm});
            skLineSegment(sketch, "E190", {"start": v(-60.22, 18.9) * mm, "end": v(-60.24, 20.9) * mm});
            skLineSegment(sketch, "E191", {"start": v(-66.2, 18.9) * mm, "end": v(-60.22, 18.9) * mm});
            skLineSegment(sketch, "E192", {"start": v(-66.2, 18.9) * mm, "end": v(-66.3, 18.9) * mm});
            skLineSegment(sketch, "E193", {"start": v(-66.2, 18.9) * mm, "end": v(-66.2, 20.9) * mm});
            skLineSegment(sketch, "E194", {"start": v(-66.2, 20.9) * mm, "end": v(-60.24, 20.9) * mm});
            skLineSegment(sketch, "E195", {"start": v(-66.3, 18.9) * mm, "end": v(-66.3, 20.9) * mm});
            skLineSegment(sketch, "E196", {"start": v(-66.3, 20.9) * mm, "end": v(-68.5, 20.9) * mm});
            skLineSegment(sketch, "E197", {"start": v(-66.3, 18.9) * mm, "end": v(-68.5, 18.9) * mm});
            skLineSegment(sketch, "E198", {"start": v(-68.5, 18.9) * mm, "end": v(-68.5, 20.9) * mm});
            skSolve(sketch);
        }
        {
            var Q0;
            Q0=qCreatedBy(makeId("Top.planeOp"),FACE);
            var sketch = newSketch(context, id + "F1", { "sketchPlane" : qUnion([Q0])});
            skLineSegment(sketch, "E199", {"start": v(-62.57, -16.2) * mm, "end": v(-62.8, -6) * mm});
            skLineSegment(sketch, "E200", {"start": v(70.88, -6.22) * mm, "end": v(70.88, -16.22) * mm});
            skArc(sketch, "E201", {"start": v(70.88, -6.22) * mm, "mid": v(4.05, 0.73) * mm, "end": v(-62.8, -6) * mm});
            skArc(sketch, "E202", {"start": v(70.88, -16.22) * mm, "mid": v(4.16, -9.4) * mm, "end": v(-62.57, -16.2) * mm});
            skSolve(sketch);
        }
        {
            var Q0;
            Q0 = qSketchRegion(id + "F1", true);
            extrude(context, id + "F2", {"entities" : qUnion([Q0]), "depth" : 42 * mm});
        }
        {
            var Q0;
            Q0=makeQuery(id+"F2.opExtrude","SWEPT_BODY",BODY,{"disambiguationData":[OSD([sQuery(id+"F1.wireOp",EDGE,"E199"),sQuery(id+"F1.wireOp",EDGE,"E200"),sQuery(id+"F1.wireOp",EDGE,"E201"),sQuery(id+"F1.wireOp",EDGE,"E202")])]});
            transform(context, id + "F3", {"entities" : qUnion([Q0]), "transformType" : TransformType.TRANSLATION_3D, "dx" : 0 * mm, "dy" : -7.8 * mm, "dz" : 0 * mm, "makeCopy" : false});
        }
        {
            var Q0;
            Q0=makeQuery(id+"F0.imprint","IMPRINT",FACE,{"disambiguationData":[TD([[makeQuery(id+"F0.imprint","IMPRINT",EDGE,{"derivedFrom":sQuery(id+"F0.wireOp",EDGE,"E25.0.9.81")}),-1.0]])]});
            var Q1;
            Q1=makeQuery(id+"F0.imprint","IMPRINT",FACE,{"disambiguationData":[TD([[makeQuery(id+"F0.imprint","IMPRINT",EDGE,{"derivedFrom":sQuery(id+"F0.wireOp",EDGE,"E25.0.9.20")}),1.0]])]});
            var Q2;
            Q2=makeQuery(id+"F0.imprint","IMPRINT",FACE,{"disambiguationData":[TD([[makeQuery(id+"F0.imprint","IMPRINT",EDGE,{"derivedFrom":sQuery(id+"F0.wireOp",EDGE,"E25.0.9.6")}),1.0]])]});
            var Q3;
            Q3=makeQuery(id+"F0.imprint","IMPRINT",FACE,{"disambiguationData":[TD([[makeQuery(id+"F0.imprint","IMPRINT",EDGE,{"derivedFrom":sQuery(id+"F0.wireOp",EDGE,"E25.0.9.1")}),1.0]])]});
            var Q4;
            Q4=makeQuery(id+"F0.imprint","IMPRINT",FACE,{"disambiguationData":[TD([[makeQuery(id+"F0.imprint","IMPRINT",EDGE,{"derivedFrom":sQuery(id+"F0.wireOp",EDGE,"E25.0.9.5")}),1.0]])]});
            var Q5;
            Q5=makeQuery(id+"F0.imprint","IMPRINT",FACE,{"disambiguationData":[TD([[makeQuery(id+"F0.imprint","IMPRINT",EDGE,{"derivedFrom":sQuery(id+"F0.wireOp",EDGE,"E25.0.9.3")}),1.0]])]});
            var Q6;
            Q6=makeQuery(id+"F0.imprint","IMPRINT",FACE,{"disambiguationData":[TD([[makeQuery(id+"F0.imprint","IMPRINT",EDGE,{"derivedFrom":sQuery(id+"F0.wireOp",EDGE,"E25.0.9.8")}),1.0]])]});
            var Q7;
            Q7=makeQuery(id+"F0.imprint","IMPRINT",FACE,{"disambiguationData":[TD([[makeQuery(id+"F0.imprint","IMPRINT",EDGE,{"derivedFrom":sQuery(id+"F0.wireOp",EDGE,"E25.0.9.0")}),1.0]])]});
            var Q8;
            Q8=makeQuery(id+"F0.imprint","IMPRINT",FACE,{"disambiguationData":[TD([[makeQuery(id+"F0.imprint","IMPRINT",EDGE,{"derivedFrom":sQuery(id+"F0.wireOp",EDGE,"E25.0.9.4")}),1.0]])]});
            var Q9;
            Q9=makeQuery(id+"F0.imprint","IMPRINT",FACE,{"disambiguationData":[TD([[makeQuery(id+"F0.imprint","IMPRINT",EDGE,{"derivedFrom":sQuery(id+"F0.wireOp",EDGE,"E25.0.9.2")}),1.0]])]});
            var Q10;
            Q10=makeQuery(id+"F0.imprint","IMPRINT",FACE,{"disambiguationData":[TD([[makeQuery(id+"F0.imprint","IMPRINT",EDGE,{"derivedFrom":sQuery(id+"F0.wireOp",EDGE,"E25.0.9.7")}),1.0]])]});
            var Q11;
            Q11=makeQuery(id+"F0.imprint","IMPRINT",FACE,{"disambiguationData":[TD([[makeQuery(id+"F0.imprint","IMPRINT",EDGE,{"derivedFrom":sQuery(id+"F0.wireOp",EDGE,"E25.1.9.81")}),-1.0]])]});
            var Q12;
            Q12=makeQuery(id+"F0.imprint","IMPRINT",FACE,{"disambiguationData":[TD([[makeQuery(id+"F0.imprint","IMPRINT",EDGE,{"derivedFrom":sQuery(id+"F0.wireOp",EDGE,"E25.1.9.20")}),1.0]])]});
            var Q13;
            Q13=makeQuery(id+"F0.imprint","IMPRINT",FACE,{"disambiguationData":[TD([[makeQuery(id+"F0.imprint","IMPRINT",EDGE,{"derivedFrom":sQuery(id+"F0.wireOp",EDGE,"E25.1.9.6")}),1.0]])]});
            var Q14;
            Q14=makeQuery(id+"F0.imprint","IMPRINT",FACE,{"disambiguationData":[TD([[makeQuery(id+"F0.imprint","IMPRINT",EDGE,{"derivedFrom":sQuery(id+"F0.wireOp",EDGE,"E25.1.9.1")}),1.0]])]});
            var Q15;
            Q15=makeQuery(id+"F0.imprint","IMPRINT",FACE,{"disambiguationData":[TD([[makeQuery(id+"F0.imprint","IMPRINT",EDGE,{"derivedFrom":sQuery(id+"F0.wireOp",EDGE,"E25.1.9.5")}),1.0]])]});
            var Q16;
            Q16=makeQuery(id+"F0.imprint","IMPRINT",FACE,{"disambiguationData":[TD([[makeQuery(id+"F0.imprint","IMPRINT",EDGE,{"derivedFrom":sQuery(id+"F0.wireOp",EDGE,"E25.1.9.3")}),1.0]])]});
            var Q17;
            Q17=makeQuery(id+"F0.imprint","IMPRINT",FACE,{"disambiguationData":[TD([[makeQuery(id+"F0.imprint","IMPRINT",EDGE,{"derivedFrom":sQuery(id+"F0.wireOp",EDGE,"E25.1.9.8")}),1.0]])]});
            var Q18;
            Q18=makeQuery(id+"F0.imprint","IMPRINT",FACE,{"disambiguationData":[TD([[makeQuery(id+"F0.imprint","IMPRINT",EDGE,{"derivedFrom":sQuery(id+"F0.wireOp",EDGE,"E25.1.9.0")}),1.0]])]});
            var Q19;
            Q19=makeQuery(id+"F0.imprint","IMPRINT",FACE,{"disambiguationData":[TD([[makeQuery(id+"F0.imprint","IMPRINT",EDGE,{"derivedFrom":sQuery(id+"F0.wireOp",EDGE,"E25.1.9.4")}),1.0]])]});
            var Q20;
            Q20=makeQuery(id+"F0.imprint","IMPRINT",FACE,{"disambiguationData":[TD([[makeQuery(id+"F0.imprint","IMPRINT",EDGE,{"derivedFrom":sQuery(id+"F0.wireOp",EDGE,"E25.1.9.2")}),1.0]])]});
            var Q21;
            Q21=makeQuery(id+"F0.imprint","IMPRINT",FACE,{"disambiguationData":[TD([[makeQuery(id+"F0.imprint","IMPRINT",EDGE,{"derivedFrom":sQuery(id+"F0.wireOp",EDGE,"E25.1.9.7")}),1.0]])]});
            var Q22;
            {var subQ0=sQuery(id+"F0.wireOp",EDGE,"E25.0.9.19");Q22=makeQuery(id+"F0.imprint","IMPRINT",FACE,{"disambiguationData":[TD([[makeQuery(id+"F0.imprint","IMPRINT",EDGE,{"derivedFrom":subQ0}),1.0]])]});}
            var Q23;
            Q23=makeQuery(id+"F0.imprint","IMPRINT",FACE,{"disambiguationData":[TD([[makeQuery(id+"F0.imprint","IMPRINT",EDGE,{"derivedFrom":sQuery(id+"F0.wireOp",EDGE,"E25.0.9.22")}),1.0]])]});
            var Q24;
            Q24=makeQuery(id+"F0.imprint","IMPRINT",FACE,{"disambiguationData":[TD([[makeQuery(id+"F0.imprint","IMPRINT",EDGE,{"derivedFrom":sQuery(id+"F0.wireOp",EDGE,"E25.0.9.18")}),1.0]])]});
            var Q25;
            Q25=makeQuery(id+"F0.imprint","IMPRINT",FACE,{"disambiguationData":[TD([[makeQuery(id+"F0.imprint","IMPRINT",EDGE,{"derivedFrom":sQuery(id+"F0.wireOp",EDGE,"E25.0.9.9")}),1.0]])]});
            var Q26;
            Q26=makeQuery(id+"F0.imprint","IMPRINT",FACE,{"disambiguationData":[TD([[makeQuery(id+"F0.imprint","IMPRINT",EDGE,{"derivedFrom":sQuery(id+"F0.wireOp",EDGE,"E25.0.9.14")}),1.0]])]});
            var Q27;
            Q27=makeQuery(id+"F0.imprint","IMPRINT",FACE,{"disambiguationData":[TD([[makeQuery(id+"F0.imprint","IMPRINT",EDGE,{"derivedFrom":sQuery(id+"F0.wireOp",EDGE,"E25.0.9.12")}),1.0]])]});
            var Q28;
            Q28=makeQuery(id+"F0.imprint","IMPRINT",FACE,{"disambiguationData":[TD([[makeQuery(id+"F0.imprint","IMPRINT",EDGE,{"derivedFrom":sQuery(id+"F0.wireOp",EDGE,"E25.0.9.17")}),1.0]])]});
            var Q29;
            Q29=makeQuery(id+"F0.imprint","IMPRINT",FACE,{"disambiguationData":[TD([[makeQuery(id+"F0.imprint","IMPRINT",EDGE,{"derivedFrom":sQuery(id+"F0.wireOp",EDGE,"E25.0.9.10")}),1.0]])]});
            var Q30;
            Q30=makeQuery(id+"F0.imprint","IMPRINT",FACE,{"disambiguationData":[TD([[makeQuery(id+"F0.imprint","IMPRINT",EDGE,{"derivedFrom":sQuery(id+"F0.wireOp",EDGE,"E25.0.9.13")}),1.0]])]});
            var Q31;
            Q31=makeQuery(id+"F0.imprint","IMPRINT",FACE,{"disambiguationData":[TD([[makeQuery(id+"F0.imprint","IMPRINT",EDGE,{"derivedFrom":sQuery(id+"F0.wireOp",EDGE,"E25.0.9.11")}),1.0]])]});
            var Q32;
            Q32=makeQuery(id+"F0.imprint","IMPRINT",FACE,{"disambiguationData":[TD([[makeQuery(id+"F0.imprint","IMPRINT",EDGE,{"derivedFrom":sQuery(id+"F0.wireOp",EDGE,"E25.1.9.78")}),1.0]])]});
            var Q33;
            Q33=makeQuery(id+"F0.imprint","IMPRINT",FACE,{"disambiguationData":[TD([[makeQuery(id+"F0.imprint","IMPRINT",EDGE,{"derivedFrom":sQuery(id+"F0.wireOp",EDGE,"E25.1.9.22")}),1.0]])]});
            var Q34;
            Q34=makeQuery(id+"F0.imprint","IMPRINT",FACE,{"disambiguationData":[TD([[makeQuery(id+"F0.imprint","IMPRINT",EDGE,{"derivedFrom":sQuery(id+"F0.wireOp",EDGE,"E25.1.9.18")}),1.0]])]});
            var Q35;
            Q35=makeQuery(id+"F0.imprint","IMPRINT",FACE,{"disambiguationData":[TD([[makeQuery(id+"F0.imprint","IMPRINT",EDGE,{"derivedFrom":sQuery(id+"F0.wireOp",EDGE,"E25.1.9.9")}),1.0]])]});
            var Q36;
            Q36=makeQuery(id+"F0.imprint","IMPRINT",FACE,{"disambiguationData":[TD([[makeQuery(id+"F0.imprint","IMPRINT",EDGE,{"derivedFrom":sQuery(id+"F0.wireOp",EDGE,"E25.1.9.14")}),1.0]])]});
            var Q37;
            Q37=makeQuery(id+"F0.imprint","IMPRINT",FACE,{"disambiguationData":[TD([[makeQuery(id+"F0.imprint","IMPRINT",EDGE,{"derivedFrom":sQuery(id+"F0.wireOp",EDGE,"E25.1.9.12")}),1.0]])]});
            var Q38;
            Q38=makeQuery(id+"F0.imprint","IMPRINT",FACE,{"disambiguationData":[TD([[makeQuery(id+"F0.imprint","IMPRINT",EDGE,{"derivedFrom":sQuery(id+"F0.wireOp",EDGE,"E25.1.9.17")}),1.0]])]});
            var Q39;
            Q39=makeQuery(id+"F0.imprint","IMPRINT",FACE,{"disambiguationData":[TD([[makeQuery(id+"F0.imprint","IMPRINT",EDGE,{"derivedFrom":sQuery(id+"F0.wireOp",EDGE,"E25.1.9.10")}),1.0]])]});
            var Q40;
            Q40=makeQuery(id+"F0.imprint","IMPRINT",FACE,{"disambiguationData":[TD([[makeQuery(id+"F0.imprint","IMPRINT",EDGE,{"derivedFrom":sQuery(id+"F0.wireOp",EDGE,"E25.1.9.13")}),1.0]])]});
            var Q41;
            Q41=makeQuery(id+"F0.imprint","IMPRINT",FACE,{"disambiguationData":[TD([[makeQuery(id+"F0.imprint","IMPRINT",EDGE,{"derivedFrom":sQuery(id+"F0.wireOp",EDGE,"E25.1.9.11")}),1.0]])]});
            var Q42;
            Q42=makeQuery(id+"F0.imprint","IMPRINT",FACE,{"disambiguationData":[TD([[makeQuery(id+"F0.imprint","IMPRINT",EDGE,{"derivedFrom":sQuery(id+"F0.wireOp",EDGE,"E25.1.9.16")}),1.0]])]});
            var Q43;
            Q43=makeQuery(id+"F0.imprint","IMPRINT",FACE,{"disambiguationData":[TD([[makeQuery(id+"F0.imprint","IMPRINT",EDGE,{"derivedFrom":sQuery(id+"F0.wireOp",EDGE,"E25.1.8.7")}),1.0]])]});
            var Q44;
            Q44=makeQuery(id+"F0.imprint","IMPRINT",FACE,{"disambiguationData":[TD([[makeQuery(id+"F0.imprint","IMPRINT",EDGE,{"derivedFrom":sQuery(id+"F0.wireOp",EDGE,"E25.1.8.2")}),1.0]])]});
            var Q45;
            Q45=makeQuery(id+"F0.imprint","IMPRINT",FACE,{"disambiguationData":[TD([[makeQuery(id+"F0.imprint","IMPRINT",EDGE,{"derivedFrom":sQuery(id+"F0.wireOp",EDGE,"E25.1.8.4")}),1.0]])]});
            var Q46;
            Q46=makeQuery(id+"F0.imprint","IMPRINT",FACE,{"disambiguationData":[TD([[makeQuery(id+"F0.imprint","IMPRINT",EDGE,{"derivedFrom":sQuery(id+"F0.wireOp",EDGE,"E25.1.8.0")}),1.0]])]});
            var Q47;
            Q47=makeQuery(id+"F0.imprint","IMPRINT",FACE,{"disambiguationData":[TD([[makeQuery(id+"F0.imprint","IMPRINT",EDGE,{"derivedFrom":sQuery(id+"F0.wireOp",EDGE,"E25.1.8.8")}),1.0]])]});
            var Q48;
            Q48=makeQuery(id+"F0.imprint","IMPRINT",FACE,{"disambiguationData":[TD([[makeQuery(id+"F0.imprint","IMPRINT",EDGE,{"derivedFrom":sQuery(id+"F0.wireOp",EDGE,"E25.1.8.3")}),1.0]])]});
            var Q49;
            Q49=makeQuery(id+"F0.imprint","IMPRINT",FACE,{"disambiguationData":[TD([[makeQuery(id+"F0.imprint","IMPRINT",EDGE,{"derivedFrom":sQuery(id+"F0.wireOp",EDGE,"E25.1.8.5")}),1.0]])]});
            var Q50;
            Q50=makeQuery(id+"F0.imprint","IMPRINT",FACE,{"disambiguationData":[TD([[makeQuery(id+"F0.imprint","IMPRINT",EDGE,{"derivedFrom":sQuery(id+"F0.wireOp",EDGE,"E25.1.8.1")}),1.0]])]});
            var Q51;
            Q51=makeQuery(id+"F0.imprint","IMPRINT",FACE,{"disambiguationData":[TD([[makeQuery(id+"F0.imprint","IMPRINT",EDGE,{"derivedFrom":sQuery(id+"F0.wireOp",EDGE,"E25.1.8.6")}),1.0]])]});
            var Q52;
            Q52=makeQuery(id+"F0.imprint","IMPRINT",FACE,{"disambiguationData":[TD([[makeQuery(id+"F0.imprint","IMPRINT",EDGE,{"derivedFrom":sQuery(id+"F0.wireOp",EDGE,"E25.1.8.20")}),1.0]])]});
            var Q53;
            Q53=makeQuery(id+"F0.imprint","IMPRINT",FACE,{"disambiguationData":[TD([[makeQuery(id+"F0.imprint","IMPRINT",EDGE,{"derivedFrom":sQuery(id+"F0.wireOp",EDGE,"E25.1.8.81")}),-1.0]])]});
            var Q54;
            Q54=makeQuery(id+"F0.imprint","IMPRINT",FACE,{"disambiguationData":[TD([[makeQuery(id+"F0.imprint","IMPRINT",EDGE,{"derivedFrom":sQuery(id+"F0.wireOp",EDGE,"E25.0.8.7")}),1.0]])]});
            var Q55;
            Q55=makeQuery(id+"F0.imprint","IMPRINT",FACE,{"disambiguationData":[TD([[makeQuery(id+"F0.imprint","IMPRINT",EDGE,{"derivedFrom":sQuery(id+"F0.wireOp",EDGE,"E25.0.8.2")}),1.0]])]});
            var Q56;
            Q56=makeQuery(id+"F0.imprint","IMPRINT",FACE,{"disambiguationData":[TD([[makeQuery(id+"F0.imprint","IMPRINT",EDGE,{"derivedFrom":sQuery(id+"F0.wireOp",EDGE,"E25.0.8.4")}),1.0]])]});
            var Q57;
            Q57=makeQuery(id+"F0.imprint","IMPRINT",FACE,{"disambiguationData":[TD([[makeQuery(id+"F0.imprint","IMPRINT",EDGE,{"derivedFrom":sQuery(id+"F0.wireOp",EDGE,"E25.0.8.0")}),1.0]])]});
            var Q58;
            Q58=makeQuery(id+"F0.imprint","IMPRINT",FACE,{"disambiguationData":[TD([[makeQuery(id+"F0.imprint","IMPRINT",EDGE,{"derivedFrom":sQuery(id+"F0.wireOp",EDGE,"E25.0.8.8")}),1.0]])]});
            var Q59;
            Q59=makeQuery(id+"F0.imprint","IMPRINT",FACE,{"disambiguationData":[TD([[makeQuery(id+"F0.imprint","IMPRINT",EDGE,{"derivedFrom":sQuery(id+"F0.wireOp",EDGE,"E25.0.8.3")}),1.0]])]});
            var Q60;
            Q60=makeQuery(id+"F0.imprint","IMPRINT",FACE,{"disambiguationData":[TD([[makeQuery(id+"F0.imprint","IMPRINT",EDGE,{"derivedFrom":sQuery(id+"F0.wireOp",EDGE,"E25.0.8.5")}),1.0]])]});
            var Q61;
            Q61=makeQuery(id+"F0.imprint","IMPRINT",FACE,{"disambiguationData":[TD([[makeQuery(id+"F0.imprint","IMPRINT",EDGE,{"derivedFrom":sQuery(id+"F0.wireOp",EDGE,"E25.0.8.1")}),1.0]])]});
            var Q62;
            Q62=makeQuery(id+"F0.imprint","IMPRINT",FACE,{"disambiguationData":[TD([[makeQuery(id+"F0.imprint","IMPRINT",EDGE,{"derivedFrom":sQuery(id+"F0.wireOp",EDGE,"E25.0.8.6")}),1.0]])]});
            var Q63;
            Q63=makeQuery(id+"F0.imprint","IMPRINT",FACE,{"disambiguationData":[TD([[makeQuery(id+"F0.imprint","IMPRINT",EDGE,{"derivedFrom":sQuery(id+"F0.wireOp",EDGE,"E25.0.8.20")}),1.0]])]});
            var Q64;
            Q64=makeQuery(id+"F0.imprint","IMPRINT",FACE,{"disambiguationData":[TD([[makeQuery(id+"F0.imprint","IMPRINT",EDGE,{"derivedFrom":sQuery(id+"F0.wireOp",EDGE,"E25.0.8.81")}),-1.0]])]});
            var Q65;
            {var subQ0=sQuery(id+"F0.wireOp",EDGE,"E25.0.8.19");Q65=makeQuery(id+"F0.imprint","IMPRINT",FACE,{"disambiguationData":[TD([[makeQuery(id+"F0.imprint","IMPRINT",EDGE,{"derivedFrom":subQ0}),1.0]])]});}
            var Q66;
            Q66=makeQuery(id+"F0.imprint","IMPRINT",FACE,{"disambiguationData":[TD([[makeQuery(id+"F0.imprint","IMPRINT",EDGE,{"derivedFrom":sQuery(id+"F0.wireOp",EDGE,"E25.0.8.22")}),1.0]])]});
            var Q67;
            Q67=makeQuery(id+"F0.imprint","IMPRINT",FACE,{"disambiguationData":[TD([[makeQuery(id+"F0.imprint","IMPRINT",EDGE,{"derivedFrom":sQuery(id+"F0.wireOp",EDGE,"E25.0.8.18")}),1.0]])]});
            var Q68;
            Q68=makeQuery(id+"F0.imprint","IMPRINT",FACE,{"disambiguationData":[TD([[makeQuery(id+"F0.imprint","IMPRINT",EDGE,{"derivedFrom":sQuery(id+"F0.wireOp",EDGE,"E25.0.8.9")}),1.0]])]});
            var Q69;
            Q69=makeQuery(id+"F0.imprint","IMPRINT",FACE,{"disambiguationData":[TD([[makeQuery(id+"F0.imprint","IMPRINT",EDGE,{"derivedFrom":sQuery(id+"F0.wireOp",EDGE,"E25.0.8.14")}),1.0]])]});
            var Q70;
            Q70=makeQuery(id+"F0.imprint","IMPRINT",FACE,{"disambiguationData":[TD([[makeQuery(id+"F0.imprint","IMPRINT",EDGE,{"derivedFrom":sQuery(id+"F0.wireOp",EDGE,"E25.0.8.12")}),1.0]])]});
            var Q71;
            Q71=makeQuery(id+"F0.imprint","IMPRINT",FACE,{"disambiguationData":[TD([[makeQuery(id+"F0.imprint","IMPRINT",EDGE,{"derivedFrom":sQuery(id+"F0.wireOp",EDGE,"E25.0.8.17")}),1.0]])]});
            var Q72;
            Q72=makeQuery(id+"F0.imprint","IMPRINT",FACE,{"disambiguationData":[TD([[makeQuery(id+"F0.imprint","IMPRINT",EDGE,{"derivedFrom":sQuery(id+"F0.wireOp",EDGE,"E25.0.8.10")}),1.0]])]});
            var Q73;
            Q73=makeQuery(id+"F0.imprint","IMPRINT",FACE,{"disambiguationData":[TD([[makeQuery(id+"F0.imprint","IMPRINT",EDGE,{"derivedFrom":sQuery(id+"F0.wireOp",EDGE,"E25.0.8.13")}),1.0]])]});
            var Q74;
            Q74=makeQuery(id+"F0.imprint","IMPRINT",FACE,{"disambiguationData":[TD([[makeQuery(id+"F0.imprint","IMPRINT",EDGE,{"derivedFrom":sQuery(id+"F0.wireOp",EDGE,"E25.0.8.11")}),1.0]])]});
            var Q75;
            Q75=makeQuery(id+"F0.imprint","IMPRINT",FACE,{"disambiguationData":[TD([[makeQuery(id+"F0.imprint","IMPRINT",EDGE,{"derivedFrom":sQuery(id+"F0.wireOp",EDGE,"E25.0.8.31")}),1.0]])]});
            var Q76;
            Q76=makeQuery(id+"F0.imprint","IMPRINT",FACE,{"disambiguationData":[TD([[makeQuery(id+"F0.imprint","IMPRINT",EDGE,{"derivedFrom":sQuery(id+"F0.wireOp",EDGE,"E25.1.8.19")}),1.0]])]});
            var Q77;
            Q77=makeQuery(id+"F0.imprint","IMPRINT",FACE,{"disambiguationData":[TD([[makeQuery(id+"F0.imprint","IMPRINT",EDGE,{"derivedFrom":sQuery(id+"F0.wireOp",EDGE,"E25.1.8.22")}),1.0]])]});
            var Q78;
            Q78=makeQuery(id+"F0.imprint","IMPRINT",FACE,{"disambiguationData":[TD([[makeQuery(id+"F0.imprint","IMPRINT",EDGE,{"derivedFrom":sQuery(id+"F0.wireOp",EDGE,"E25.1.8.18")}),1.0]])]});
            var Q79;
            Q79=makeQuery(id+"F0.imprint","IMPRINT",FACE,{"disambiguationData":[TD([[makeQuery(id+"F0.imprint","IMPRINT",EDGE,{"derivedFrom":sQuery(id+"F0.wireOp",EDGE,"E25.1.8.9")}),1.0]])]});
            var Q80;
            Q80=makeQuery(id+"F0.imprint","IMPRINT",FACE,{"disambiguationData":[TD([[makeQuery(id+"F0.imprint","IMPRINT",EDGE,{"derivedFrom":sQuery(id+"F0.wireOp",EDGE,"E25.1.8.14")}),1.0]])]});
            var Q81;
            Q81=makeQuery(id+"F0.imprint","IMPRINT",FACE,{"disambiguationData":[TD([[makeQuery(id+"F0.imprint","IMPRINT",EDGE,{"derivedFrom":sQuery(id+"F0.wireOp",EDGE,"E25.1.8.12")}),1.0]])]});
            var Q82;
            Q82=makeQuery(id+"F0.imprint","IMPRINT",FACE,{"disambiguationData":[TD([[makeQuery(id+"F0.imprint","IMPRINT",EDGE,{"derivedFrom":sQuery(id+"F0.wireOp",EDGE,"E25.1.8.17")}),1.0]])]});
            var Q83;
            Q83=makeQuery(id+"F0.imprint","IMPRINT",FACE,{"disambiguationData":[TD([[makeQuery(id+"F0.imprint","IMPRINT",EDGE,{"derivedFrom":sQuery(id+"F0.wireOp",EDGE,"E25.1.8.10")}),1.0]])]});
            var Q84;
            Q84=makeQuery(id+"F0.imprint","IMPRINT",FACE,{"disambiguationData":[TD([[makeQuery(id+"F0.imprint","IMPRINT",EDGE,{"derivedFrom":sQuery(id+"F0.wireOp",EDGE,"E25.1.8.13")}),1.0]])]});
            var Q85;
            Q85=makeQuery(id+"F0.imprint","IMPRINT",FACE,{"disambiguationData":[TD([[makeQuery(id+"F0.imprint","IMPRINT",EDGE,{"derivedFrom":sQuery(id+"F0.wireOp",EDGE,"E25.1.8.11")}),1.0]])]});
            var Q86;
            Q86=makeQuery(id+"F0.imprint","IMPRINT",FACE,{"disambiguationData":[TD([[makeQuery(id+"F0.imprint","IMPRINT",EDGE,{"derivedFrom":sQuery(id+"F0.wireOp",EDGE,"E25.1.8.16")}),1.0]])]});
            var Q87;
            Q87=makeQuery(id+"F0.imprint","IMPRINT",FACE,{"disambiguationData":[TD([[makeQuery(id+"F0.imprint","IMPRINT",EDGE,{"derivedFrom":sQuery(id+"F0.wireOp",EDGE,"E25.1.7.7")}),1.0]])]});
            var Q88;
            Q88=makeQuery(id+"F0.imprint","IMPRINT",FACE,{"disambiguationData":[TD([[makeQuery(id+"F0.imprint","IMPRINT",EDGE,{"derivedFrom":sQuery(id+"F0.wireOp",EDGE,"E25.1.7.16")}),1.0]])]});
            var Q89;
            Q89=makeQuery(id+"F0.imprint","IMPRINT",FACE,{"disambiguationData":[TD([[makeQuery(id+"F0.imprint","IMPRINT",EDGE,{"derivedFrom":sQuery(id+"F0.wireOp",EDGE,"E25.1.7.11")}),1.0]])]});
            var Q90;
            Q90=makeQuery(id+"F0.imprint","IMPRINT",FACE,{"disambiguationData":[TD([[makeQuery(id+"F0.imprint","IMPRINT",EDGE,{"derivedFrom":sQuery(id+"F0.wireOp",EDGE,"E25.1.6.7")}),1.0]])]});
            var Q91;
            Q91=makeQuery(id+"F0.imprint","IMPRINT",FACE,{"disambiguationData":[TD([[makeQuery(id+"F0.imprint","IMPRINT",EDGE,{"derivedFrom":sQuery(id+"F0.wireOp",EDGE,"E25.1.6.11")}),1.0]])]});
            var Q92;
            Q92=makeQuery(id+"F0.imprint","IMPRINT",FACE,{"disambiguationData":[TD([[makeQuery(id+"F0.imprint","IMPRINT",EDGE,{"derivedFrom":sQuery(id+"F0.wireOp",EDGE,"E25.1.6.16")}),1.0]])]});
            var Q93;
            Q93=makeQuery(id+"F0.imprint","IMPRINT",FACE,{"disambiguationData":[TD([[makeQuery(id+"F0.imprint","IMPRINT",EDGE,{"derivedFrom":sQuery(id+"F0.wireOp",EDGE,"E25.1.5.7")}),1.0]])]});
            var Q94;
            Q94=makeQuery(id+"F0.imprint","IMPRINT",FACE,{"disambiguationData":[TD([[makeQuery(id+"F0.imprint","IMPRINT",EDGE,{"derivedFrom":sQuery(id+"F0.wireOp",EDGE,"E25.1.5.2")}),1.0]])]});
            var Q95;
            Q95=makeQuery(id+"F0.imprint","IMPRINT",FACE,{"disambiguationData":[TD([[makeQuery(id+"F0.imprint","IMPRINT",EDGE,{"derivedFrom":sQuery(id+"F0.wireOp",EDGE,"E25.1.5.11")}),1.0]])]});
            var Q96;
            Q96=makeQuery(id+"F0.imprint","IMPRINT",FACE,{"disambiguationData":[TD([[makeQuery(id+"F0.imprint","IMPRINT",EDGE,{"derivedFrom":sQuery(id+"F0.wireOp",EDGE,"E25.1.5.16")}),1.0]])]});
            var Q97;
            Q97=makeQuery(id+"F0.imprint","IMPRINT",FACE,{"disambiguationData":[TD([[makeQuery(id+"F0.imprint","IMPRINT",EDGE,{"derivedFrom":sQuery(id+"F0.wireOp",EDGE,"E25.1.4.7")}),1.0]])]});
            var Q98;
            Q98=makeQuery(id+"F0.imprint","IMPRINT",FACE,{"disambiguationData":[TD([[makeQuery(id+"F0.imprint","IMPRINT",EDGE,{"derivedFrom":sQuery(id+"F0.wireOp",EDGE,"E25.1.4.2")}),1.0]])]});
            var Q99;
            Q99=makeQuery(id+"F0.imprint","IMPRINT",FACE,{"disambiguationData":[TD([[makeQuery(id+"F0.imprint","IMPRINT",EDGE,{"derivedFrom":sQuery(id+"F0.wireOp",EDGE,"E25.1.4.11")}),1.0]])]});
            var Q100;
            Q100=makeQuery(id+"F0.imprint","IMPRINT",FACE,{"disambiguationData":[TD([[makeQuery(id+"F0.imprint","IMPRINT",EDGE,{"derivedFrom":sQuery(id+"F0.wireOp",EDGE,"E25.1.4.16")}),1.0]])]});
            var Q101;
            Q101=makeQuery(id+"F0.imprint","IMPRINT",FACE,{"disambiguationData":[TD([[makeQuery(id+"F0.imprint","IMPRINT",EDGE,{"derivedFrom":sQuery(id+"F0.wireOp",EDGE,"E25.1.3.7")}),1.0]])]});
            var Q102;
            Q102=makeQuery(id+"F0.imprint","IMPRINT",FACE,{"disambiguationData":[TD([[makeQuery(id+"F0.imprint","IMPRINT",EDGE,{"derivedFrom":sQuery(id+"F0.wireOp",EDGE,"E25.1.3.2")}),1.0]])]});
            var Q103;
            Q103=makeQuery(id+"F0.imprint","IMPRINT",FACE,{"disambiguationData":[TD([[makeQuery(id+"F0.imprint","IMPRINT",EDGE,{"derivedFrom":sQuery(id+"F0.wireOp",EDGE,"E25.1.3.11")}),1.0]])]});
            var Q104;
            Q104=makeQuery(id+"F0.imprint","IMPRINT",FACE,{"disambiguationData":[TD([[makeQuery(id+"F0.imprint","IMPRINT",EDGE,{"derivedFrom":sQuery(id+"F0.wireOp",EDGE,"E25.1.3.16")}),1.0]])]});
            var Q105;
            Q105=makeQuery(id+"F0.imprint","IMPRINT",FACE,{"disambiguationData":[TD([[makeQuery(id+"F0.imprint","IMPRINT",EDGE,{"derivedFrom":sQuery(id+"F0.wireOp",EDGE,"E25.1.2.7")}),1.0]])]});
            var Q106;
            Q106=makeQuery(id+"F0.imprint","IMPRINT",FACE,{"disambiguationData":[TD([[makeQuery(id+"F0.imprint","IMPRINT",EDGE,{"derivedFrom":sQuery(id+"F0.wireOp",EDGE,"E25.1.2.2")}),1.0]])]});
            var Q107;
            Q107=makeQuery(id+"F0.imprint","IMPRINT",FACE,{"disambiguationData":[TD([[makeQuery(id+"F0.imprint","IMPRINT",EDGE,{"derivedFrom":sQuery(id+"F0.wireOp",EDGE,"E25.1.2.11")}),1.0]])]});
            var Q108;
            Q108=makeQuery(id+"F0.imprint","IMPRINT",FACE,{"disambiguationData":[TD([[makeQuery(id+"F0.imprint","IMPRINT",EDGE,{"derivedFrom":sQuery(id+"F0.wireOp",EDGE,"E25.1.2.16")}),1.0]])]});
            var Q109;
            Q109=makeQuery(id+"F0.imprint","IMPRINT",FACE,{"disambiguationData":[TD([[makeQuery(id+"F0.imprint","IMPRINT",EDGE,{"derivedFrom":sQuery(id+"F0.wireOp",EDGE,"E140")}),1.0]])]});
            var Q110;
            Q110=makeQuery(id+"F0.imprint","IMPRINT",FACE,{"disambiguationData":[TD([[makeQuery(id+"F0.imprint","IMPRINT",EDGE,{"derivedFrom":sQuery(id+"F0.wireOp",EDGE,"E25.1.1.2")}),1.0]])]});
            var Q111;
            Q111=makeQuery(id+"F0.imprint","IMPRINT",FACE,{"disambiguationData":[TD([[makeQuery(id+"F0.imprint","IMPRINT",EDGE,{"derivedFrom":sQuery(id+"F0.wireOp",EDGE,"E25.1.1.11")}),1.0]])]});
            var Q112;
            Q112=makeQuery(id+"F0.imprint","IMPRINT",FACE,{"disambiguationData":[TD([[makeQuery(id+"F0.imprint","IMPRINT",EDGE,{"derivedFrom":sQuery(id+"F0.wireOp",EDGE,"E25.1.1.16")}),1.0]])]});
            var Q113;
            Q113=makeQuery(id+"F0.imprint","IMPRINT",FACE,{"disambiguationData":[TD([[makeQuery(id+"F0.imprint","IMPRINT",EDGE,{"derivedFrom":sQuery(id+"F0.wireOp",EDGE,"E25.1.0.7")}),1.0]])]});
            var Q114;
            Q114=makeQuery(id+"F0.imprint","IMPRINT",FACE,{"disambiguationData":[TD([[makeQuery(id+"F0.imprint","IMPRINT",EDGE,{"derivedFrom":sQuery(id+"F0.wireOp",EDGE,"E25.1.0.2")}),1.0]])]});
            var Q115;
            Q115=makeQuery(id+"F0.imprint","IMPRINT",FACE,{"disambiguationData":[TD([[makeQuery(id+"F0.imprint","IMPRINT",EDGE,{"derivedFrom":sQuery(id+"F0.wireOp",EDGE,"E25.1.0.11")}),1.0]])]});
            var Q116;
            Q116=makeQuery(id+"F0.imprint","IMPRINT",FACE,{"disambiguationData":[TD([[makeQuery(id+"F0.imprint","IMPRINT",EDGE,{"derivedFrom":sQuery(id+"F0.wireOp",EDGE,"E25.1.0.16")}),1.0]])]});
            var Q117;
            Q117=makeQuery(id+"F0.imprint","IMPRINT",FACE,{"disambiguationData":[TD([[makeQuery(id+"F0.imprint","IMPRINT",EDGE,{"derivedFrom":sQuery(id+"F0.wireOp",EDGE,"E25.1.0.13")}),1.0]])]});
            var Q118;
            Q118=makeQuery(id+"F0.imprint","IMPRINT",FACE,{"disambiguationData":[TD([[makeQuery(id+"F0.imprint","IMPRINT",EDGE,{"derivedFrom":sQuery(id+"F0.wireOp",EDGE,"E25.1.0.4")}),1.0]])]});
            var Q119;
            Q119=makeQuery(id+"F0.imprint","IMPRINT",FACE,{"disambiguationData":[TD([[makeQuery(id+"F0.imprint","IMPRINT",EDGE,{"derivedFrom":sQuery(id+"F0.wireOp",EDGE,"E25.1.1.13")}),1.0]])]});
            var Q120;
            Q120=makeQuery(id+"F0.imprint","IMPRINT",FACE,{"disambiguationData":[TD([[makeQuery(id+"F0.imprint","IMPRINT",EDGE,{"derivedFrom":sQuery(id+"F0.wireOp",EDGE,"E25.1.1.10")}),1.0]])]});
            var Q121;
            Q121=makeQuery(id+"F0.imprint","IMPRINT",FACE,{"disambiguationData":[TD([[makeQuery(id+"F0.imprint","IMPRINT",EDGE,{"derivedFrom":sQuery(id+"F0.wireOp",EDGE,"E25.1.1.4")}),1.0]])]});
            var Q122;
            Q122=makeQuery(id+"F0.imprint","IMPRINT",FACE,{"disambiguationData":[TD([[makeQuery(id+"F0.imprint","IMPRINT",EDGE,{"derivedFrom":sQuery(id+"F0.wireOp",EDGE,"E25.1.2.13")}),1.0]])]});
            var Q123;
            Q123=makeQuery(id+"F0.imprint","IMPRINT",FACE,{"disambiguationData":[TD([[makeQuery(id+"F0.imprint","IMPRINT",EDGE,{"derivedFrom":sQuery(id+"F0.wireOp",EDGE,"E25.1.2.10")}),1.0]])]});
            var Q124;
            Q124=makeQuery(id+"F0.imprint","IMPRINT",FACE,{"disambiguationData":[TD([[makeQuery(id+"F0.imprint","IMPRINT",EDGE,{"derivedFrom":sQuery(id+"F0.wireOp",EDGE,"E25.1.2.4")}),1.0]])]});
            var Q125;
            Q125=makeQuery(id+"F0.imprint","IMPRINT",FACE,{"disambiguationData":[TD([[makeQuery(id+"F0.imprint","IMPRINT",EDGE,{"derivedFrom":sQuery(id+"F0.wireOp",EDGE,"E25.1.3.13")}),1.0]])]});
            var Q126;
            Q126=makeQuery(id+"F0.imprint","IMPRINT",FACE,{"disambiguationData":[TD([[makeQuery(id+"F0.imprint","IMPRINT",EDGE,{"derivedFrom":sQuery(id+"F0.wireOp",EDGE,"E25.1.3.10")}),1.0]])]});
            var Q127;
            Q127=makeQuery(id+"F0.imprint","IMPRINT",FACE,{"disambiguationData":[TD([[makeQuery(id+"F0.imprint","IMPRINT",EDGE,{"derivedFrom":sQuery(id+"F0.wireOp",EDGE,"E25.1.3.4")}),1.0]])]});
            var Q128;
            Q128=makeQuery(id+"F0.imprint","IMPRINT",FACE,{"disambiguationData":[TD([[makeQuery(id+"F0.imprint","IMPRINT",EDGE,{"derivedFrom":sQuery(id+"F0.wireOp",EDGE,"E25.1.4.13")}),1.0]])]});
            var Q129;
            Q129=makeQuery(id+"F0.imprint","IMPRINT",FACE,{"disambiguationData":[TD([[makeQuery(id+"F0.imprint","IMPRINT",EDGE,{"derivedFrom":sQuery(id+"F0.wireOp",EDGE,"E25.1.4.10")}),1.0]])]});
            var Q130;
            Q130=makeQuery(id+"F0.imprint","IMPRINT",FACE,{"disambiguationData":[TD([[makeQuery(id+"F0.imprint","IMPRINT",EDGE,{"derivedFrom":sQuery(id+"F0.wireOp",EDGE,"E25.1.4.4")}),1.0]])]});
            var Q131;
            Q131=makeQuery(id+"F0.imprint","IMPRINT",FACE,{"disambiguationData":[TD([[makeQuery(id+"F0.imprint","IMPRINT",EDGE,{"derivedFrom":sQuery(id+"F0.wireOp",EDGE,"E25.1.5.13")}),1.0]])]});
            var Q132;
            Q132=makeQuery(id+"F0.imprint","IMPRINT",FACE,{"disambiguationData":[TD([[makeQuery(id+"F0.imprint","IMPRINT",EDGE,{"derivedFrom":sQuery(id+"F0.wireOp",EDGE,"E25.1.5.10")}),1.0]])]});
            var Q133;
            Q133=makeQuery(id+"F0.imprint","IMPRINT",FACE,{"disambiguationData":[TD([[makeQuery(id+"F0.imprint","IMPRINT",EDGE,{"derivedFrom":sQuery(id+"F0.wireOp",EDGE,"E25.1.5.4")}),1.0]])]});
            var Q134;
            Q134=makeQuery(id+"F0.imprint","IMPRINT",FACE,{"disambiguationData":[TD([[makeQuery(id+"F0.imprint","IMPRINT",EDGE,{"derivedFrom":sQuery(id+"F0.wireOp",EDGE,"E25.1.6.13")}),1.0]])]});
            var Q135;
            Q135=makeQuery(id+"F0.imprint","IMPRINT",FACE,{"disambiguationData":[TD([[makeQuery(id+"F0.imprint","IMPRINT",EDGE,{"derivedFrom":sQuery(id+"F0.wireOp",EDGE,"E25.1.6.10")}),1.0]])]});
            var Q136;
            Q136=makeQuery(id+"F0.imprint","IMPRINT",FACE,{"disambiguationData":[TD([[makeQuery(id+"F0.imprint","IMPRINT",EDGE,{"derivedFrom":sQuery(id+"F0.wireOp",EDGE,"E25.1.5.0")}),1.0]])]});
            var Q137;
            Q137=makeQuery(id+"F0.imprint","IMPRINT",FACE,{"disambiguationData":[TD([[makeQuery(id+"F0.imprint","IMPRINT",EDGE,{"derivedFrom":sQuery(id+"F0.wireOp",EDGE,"E25.1.5.17")}),1.0]])]});
            var Q138;
            Q138=makeQuery(id+"F0.imprint","IMPRINT",FACE,{"disambiguationData":[TD([[makeQuery(id+"F0.imprint","IMPRINT",EDGE,{"derivedFrom":sQuery(id+"F0.wireOp",EDGE,"E25.1.4.0")}),1.0]])]});
            var Q139;
            Q139=makeQuery(id+"F0.imprint","IMPRINT",FACE,{"disambiguationData":[TD([[makeQuery(id+"F0.imprint","IMPRINT",EDGE,{"derivedFrom":sQuery(id+"F0.wireOp",EDGE,"E25.1.4.17")}),1.0]])]});
            var Q140;
            Q140=makeQuery(id+"F0.imprint","IMPRINT",FACE,{"disambiguationData":[TD([[makeQuery(id+"F0.imprint","IMPRINT",EDGE,{"derivedFrom":sQuery(id+"F0.wireOp",EDGE,"E25.1.3.0")}),1.0]])]});
            var Q141;
            Q141=makeQuery(id+"F0.imprint","IMPRINT",FACE,{"disambiguationData":[TD([[makeQuery(id+"F0.imprint","IMPRINT",EDGE,{"derivedFrom":sQuery(id+"F0.wireOp",EDGE,"E25.1.3.8")}),1.0]])]});
            var Q142;
            Q142=makeQuery(id+"F0.imprint","IMPRINT",FACE,{"disambiguationData":[TD([[makeQuery(id+"F0.imprint","IMPRINT",EDGE,{"derivedFrom":sQuery(id+"F0.wireOp",EDGE,"E25.1.3.17")}),1.0]])]});
            var Q143;
            Q143=makeQuery(id+"F0.imprint","IMPRINT",FACE,{"disambiguationData":[TD([[makeQuery(id+"F0.imprint","IMPRINT",EDGE,{"derivedFrom":sQuery(id+"F0.wireOp",EDGE,"E25.1.2.0")}),1.0]])]});
            var Q144;
            Q144=makeQuery(id+"F0.imprint","IMPRINT",FACE,{"disambiguationData":[TD([[makeQuery(id+"F0.imprint","IMPRINT",EDGE,{"derivedFrom":sQuery(id+"F0.wireOp",EDGE,"E25.1.2.8")}),1.0]])]});
            var Q145;
            Q145=makeQuery(id+"F0.imprint","IMPRINT",FACE,{"disambiguationData":[TD([[makeQuery(id+"F0.imprint","IMPRINT",EDGE,{"derivedFrom":sQuery(id+"F0.wireOp",EDGE,"E25.1.2.17")}),1.0]])]});
            var Q146;
            Q146=makeQuery(id+"F0.imprint","IMPRINT",FACE,{"disambiguationData":[TD([[makeQuery(id+"F0.imprint","IMPRINT",EDGE,{"derivedFrom":sQuery(id+"F0.wireOp",EDGE,"E25.1.1.8")}),1.0]])]});
            var Q147;
            Q147=makeQuery(id+"F0.imprint","IMPRINT",FACE,{"disambiguationData":[TD([[makeQuery(id+"F0.imprint","IMPRINT",EDGE,{"derivedFrom":sQuery(id+"F0.wireOp",EDGE,"E25.1.1.0")}),1.0]])]});
            var Q148;
            Q148=makeQuery(id+"F0.imprint","IMPRINT",FACE,{"disambiguationData":[TD([[makeQuery(id+"F0.imprint","IMPRINT",EDGE,{"derivedFrom":sQuery(id+"F0.wireOp",EDGE,"E25.1.1.17")}),1.0]])]});
            var Q149;
            Q149=makeQuery(id+"F0.imprint","IMPRINT",FACE,{"disambiguationData":[TD([[makeQuery(id+"F0.imprint","IMPRINT",EDGE,{"derivedFrom":sQuery(id+"F0.wireOp",EDGE,"E25.1.0.8")}),1.0]])]});
            var Q150;
            Q150=makeQuery(id+"F0.imprint","IMPRINT",FACE,{"disambiguationData":[TD([[makeQuery(id+"F0.imprint","IMPRINT",EDGE,{"derivedFrom":sQuery(id+"F0.wireOp",EDGE,"E25.1.0.17")}),1.0]])]});
            var Q151;
            Q151=makeQuery(id+"F0.imprint","IMPRINT",FACE,{"disambiguationData":[TD([[makeQuery(id+"F0.imprint","IMPRINT",EDGE,{"derivedFrom":sQuery(id+"F0.wireOp",EDGE,"E25.1.0.0")}),1.0]])]});
            var Q152;
            Q152=makeQuery(id+"F0.imprint","IMPRINT",FACE,{"disambiguationData":[TD([[makeQuery(id+"F0.imprint","IMPRINT",EDGE,{"derivedFrom":sQuery(id+"F0.wireOp",EDGE,"E25.1.0.10")}),1.0]])]});
            var Q153;
            Q153=makeQuery(id+"F0.imprint","IMPRINT",FACE,{"disambiguationData":[TD([[makeQuery(id+"F0.imprint","IMPRINT",EDGE,{"derivedFrom":sQuery(id+"F0.wireOp",EDGE,"E25.1.0.12")}),1.0]])]});
            var Q154;
            Q154=makeQuery(id+"F0.imprint","IMPRINT",FACE,{"disambiguationData":[TD([[makeQuery(id+"F0.imprint","IMPRINT",EDGE,{"derivedFrom":sQuery(id+"F0.wireOp",EDGE,"E25.1.0.14")}),1.0]])]});
            var Q155;
            Q155=makeQuery(id+"F0.imprint","IMPRINT",FACE,{"disambiguationData":[TD([[makeQuery(id+"F0.imprint","IMPRINT",EDGE,{"derivedFrom":sQuery(id+"F0.wireOp",EDGE,"E25.1.0.3")}),1.0]])]});
            var Q156;
            Q156=makeQuery(id+"F0.imprint","IMPRINT",FACE,{"disambiguationData":[TD([[makeQuery(id+"F0.imprint","IMPRINT",EDGE,{"derivedFrom":sQuery(id+"F0.wireOp",EDGE,"E25.1.1.12")}),1.0]])]});
            var Q157;
            Q157=makeQuery(id+"F0.imprint","IMPRINT",FACE,{"disambiguationData":[TD([[makeQuery(id+"F0.imprint","IMPRINT",EDGE,{"derivedFrom":sQuery(id+"F0.wireOp",EDGE,"E25.1.0.9")}),1.0]])]});
            var Q158;
            Q158=makeQuery(id+"F0.imprint","IMPRINT",FACE,{"disambiguationData":[TD([[makeQuery(id+"F0.imprint","IMPRINT",EDGE,{"derivedFrom":sQuery(id+"F0.wireOp",EDGE,"E25.1.0.5")}),1.0]])]});
            var Q159;
            Q159=makeQuery(id+"F0.imprint","IMPRINT",FACE,{"disambiguationData":[TD([[makeQuery(id+"F0.imprint","IMPRINT",EDGE,{"derivedFrom":sQuery(id+"F0.wireOp",EDGE,"E25.1.1.14")}),1.0]])]});
            var Q160;
            Q160=makeQuery(id+"F0.imprint","IMPRINT",FACE,{"disambiguationData":[TD([[makeQuery(id+"F0.imprint","IMPRINT",EDGE,{"derivedFrom":sQuery(id+"F0.wireOp",EDGE,"E25.1.1.3")}),1.0]])]});
            var Q161;
            Q161=makeQuery(id+"F0.imprint","IMPRINT",FACE,{"disambiguationData":[TD([[makeQuery(id+"F0.imprint","IMPRINT",EDGE,{"derivedFrom":sQuery(id+"F0.wireOp",EDGE,"E25.1.2.12")}),1.0]])]});
            var Q162;
            Q162=makeQuery(id+"F0.imprint","IMPRINT",FACE,{"disambiguationData":[TD([[makeQuery(id+"F0.imprint","IMPRINT",EDGE,{"derivedFrom":sQuery(id+"F0.wireOp",EDGE,"E25.1.2.14")}),1.0]])]});
            var Q163;
            Q163=makeQuery(id+"F0.imprint","IMPRINT",FACE,{"disambiguationData":[TD([[makeQuery(id+"F0.imprint","IMPRINT",EDGE,{"derivedFrom":sQuery(id+"F0.wireOp",EDGE,"E25.1.1.5")}),1.0]])]});
            var Q164;
            Q164=makeQuery(id+"F0.imprint","IMPRINT",FACE,{"disambiguationData":[TD([[makeQuery(id+"F0.imprint","IMPRINT",EDGE,{"derivedFrom":sQuery(id+"F0.wireOp",EDGE,"E25.1.1.9")}),1.0]])]});
            var Q165;
            Q165=makeQuery(id+"F0.imprint","IMPRINT",FACE,{"disambiguationData":[TD([[makeQuery(id+"F0.imprint","IMPRINT",EDGE,{"derivedFrom":sQuery(id+"F0.wireOp",EDGE,"E25.1.0.1")}),1.0]])]});
            var Q166;
            Q166=makeQuery(id+"F0.imprint","IMPRINT",FACE,{"disambiguationData":[TD([[makeQuery(id+"F0.imprint","IMPRINT",EDGE,{"derivedFrom":sQuery(id+"F0.wireOp",EDGE,"E25.1.2.3")}),1.0]])]});
            var Q167;
            Q167=makeQuery(id+"F0.imprint","IMPRINT",FACE,{"disambiguationData":[TD([[makeQuery(id+"F0.imprint","IMPRINT",EDGE,{"derivedFrom":sQuery(id+"F0.wireOp",EDGE,"E25.1.3.12")}),1.0]])]});
            var Q168;
            Q168=makeQuery(id+"F0.imprint","IMPRINT",FACE,{"disambiguationData":[TD([[makeQuery(id+"F0.imprint","IMPRINT",EDGE,{"derivedFrom":sQuery(id+"F0.wireOp",EDGE,"E25.1.3.3")}),1.0]])]});
            var Q169;
            Q169=makeQuery(id+"F0.imprint","IMPRINT",FACE,{"disambiguationData":[TD([[makeQuery(id+"F0.imprint","IMPRINT",EDGE,{"derivedFrom":sQuery(id+"F0.wireOp",EDGE,"E25.1.3.14")}),1.0]])]});
            var Q170;
            Q170=makeQuery(id+"F0.imprint","IMPRINT",FACE,{"disambiguationData":[TD([[makeQuery(id+"F0.imprint","IMPRINT",EDGE,{"derivedFrom":sQuery(id+"F0.wireOp",EDGE,"E25.1.2.5")}),1.0]])]});
            var Q171;
            Q171=makeQuery(id+"F0.imprint","IMPRINT",FACE,{"disambiguationData":[TD([[makeQuery(id+"F0.imprint","IMPRINT",EDGE,{"derivedFrom":sQuery(id+"F0.wireOp",EDGE,"E25.1.2.9")}),1.0]])]});
            var Q172;
            Q172=makeQuery(id+"F0.imprint","IMPRINT",FACE,{"disambiguationData":[TD([[makeQuery(id+"F0.imprint","IMPRINT",EDGE,{"derivedFrom":sQuery(id+"F0.wireOp",EDGE,"E25.1.1.1")}),1.0]])]});
            var Q173;
            Q173=makeQuery(id+"F0.imprint","IMPRINT",FACE,{"disambiguationData":[TD([[makeQuery(id+"F0.imprint","IMPRINT",EDGE,{"derivedFrom":sQuery(id+"F0.wireOp",EDGE,"E25.1.1.18")}),1.0]])]});
            var Q174;
            Q174=makeQuery(id+"F0.imprint","IMPRINT",FACE,{"disambiguationData":[TD([[makeQuery(id+"F0.imprint","IMPRINT",EDGE,{"derivedFrom":sQuery(id+"F0.wireOp",EDGE,"E25.1.0.6")}),1.0]])]});
            var Q175;
            Q175=makeQuery(id+"F0.imprint","IMPRINT",FACE,{"disambiguationData":[TD([[makeQuery(id+"F0.imprint","IMPRINT",EDGE,{"derivedFrom":sQuery(id+"F0.wireOp",EDGE,"E25.1.0.22")}),1.0]])]});
            var Q176;
            Q176=makeQuery(id+"F0.imprint","IMPRINT",FACE,{"disambiguationData":[TD([[makeQuery(id+"F0.imprint","IMPRINT",EDGE,{"derivedFrom":sQuery(id+"F0.wireOp",EDGE,"E25.1.0.18")}),1.0]])]});
            var Q177;
            Q177=makeQuery(id+"F0.imprint","IMPRINT",FACE,{"disambiguationData":[TD([[makeQuery(id+"F0.imprint","IMPRINT",EDGE,{"derivedFrom":sQuery(id+"F0.wireOp",EDGE,"E25.1.4.12")}),1.0]])]});
            var Q178;
            Q178=makeQuery(id+"F0.imprint","IMPRINT",FACE,{"disambiguationData":[TD([[makeQuery(id+"F0.imprint","IMPRINT",EDGE,{"derivedFrom":sQuery(id+"F0.wireOp",EDGE,"E25.1.4.8")}),1.0]])]});
            var Q179;
            {var subQ0=sQuery(id+"F0.wireOp",EDGE,"E25.1.0.78");Q179=makeQuery(id+"F0.imprint","IMPRINT",FACE,{"disambiguationData":[TD([[makeQuery(id+"F0.imprint","IMPRINT",EDGE,{"derivedFrom":subQ0}),1.0]])]});}
            var Q180;
            Q180=makeQuery(id+"F0.imprint","IMPRINT",FACE,{"disambiguationData":[TD([[makeQuery(id+"F0.imprint","IMPRINT",EDGE,{"derivedFrom":sQuery(id+"F0.wireOp",EDGE,"E25.1.0.20")}),1.0]])]});
            var Q181;
            Q181=makeQuery(id+"F0.imprint","IMPRINT",FACE,{"disambiguationData":[TD([[makeQuery(id+"F0.imprint","IMPRINT",EDGE,{"derivedFrom":sQuery(id+"F0.wireOp",EDGE,"E25.1.1.22")}),1.0]])]});
            var Q182;
            Q182=makeQuery(id+"F0.imprint","IMPRINT",FACE,{"disambiguationData":[TD([[makeQuery(id+"F0.imprint","IMPRINT",EDGE,{"derivedFrom":sQuery(id+"F0.wireOp",EDGE,"E25.1.1.6")}),1.0]])]});
            var Q183;
            Q183=makeQuery(id+"F0.imprint","IMPRINT",FACE,{"disambiguationData":[TD([[makeQuery(id+"F0.imprint","IMPRINT",EDGE,{"derivedFrom":sQuery(id+"F0.wireOp",EDGE,"E25.1.2.18")}),1.0]])]});
            var Q184;
            Q184=makeQuery(id+"F0.imprint","IMPRINT",FACE,{"disambiguationData":[TD([[makeQuery(id+"F0.imprint","IMPRINT",EDGE,{"derivedFrom":sQuery(id+"F0.wireOp",EDGE,"E25.1.2.1")}),1.0]])]});
            var Q185;
            Q185=makeQuery(id+"F0.imprint","IMPRINT",FACE,{"disambiguationData":[TD([[makeQuery(id+"F0.imprint","IMPRINT",EDGE,{"derivedFrom":sQuery(id+"F0.wireOp",EDGE,"E25.1.3.9")}),1.0]])]});
            var Q186;
            Q186=makeQuery(id+"F0.imprint","IMPRINT",FACE,{"disambiguationData":[TD([[makeQuery(id+"F0.imprint","IMPRINT",EDGE,{"derivedFrom":sQuery(id+"F0.wireOp",EDGE,"E25.1.3.5")}),1.0]])]});
            var Q187;
            Q187=makeQuery(id+"F0.imprint","IMPRINT",FACE,{"disambiguationData":[TD([[makeQuery(id+"F0.imprint","IMPRINT",EDGE,{"derivedFrom":sQuery(id+"F0.wireOp",EDGE,"E25.1.4.14")}),1.0]])]});
            var Q188;
            Q188=makeQuery(id+"F0.imprint","IMPRINT",FACE,{"disambiguationData":[TD([[makeQuery(id+"F0.imprint","IMPRINT",EDGE,{"derivedFrom":sQuery(id+"F0.wireOp",EDGE,"E25.1.4.3")}),1.0]])]});
            var Q189;
            Q189=makeQuery(id+"F0.imprint","IMPRINT",FACE,{"disambiguationData":[TD([[makeQuery(id+"F0.imprint","IMPRINT",EDGE,{"derivedFrom":sQuery(id+"F0.wireOp",EDGE,"E25.1.5.12")}),1.0]])]});
            var Q190;
            Q190=makeQuery(id+"F0.imprint","IMPRINT",FACE,{"disambiguationData":[TD([[makeQuery(id+"F0.imprint","IMPRINT",EDGE,{"derivedFrom":sQuery(id+"F0.wireOp",EDGE,"E25.1.5.8")}),1.0]])]});
            var Q191;
            Q191=makeQuery(id+"F0.imprint","IMPRINT",FACE,{"disambiguationData":[TD([[makeQuery(id+"F0.imprint","IMPRINT",EDGE,{"derivedFrom":sQuery(id+"F0.wireOp",EDGE,"E25.1.6.17")}),1.0]])]});
            var Q192;
            Q192=makeQuery(id+"F0.imprint","IMPRINT",FACE,{"disambiguationData":[TD([[makeQuery(id+"F0.imprint","IMPRINT",EDGE,{"derivedFrom":sQuery(id+"F0.wireOp",EDGE,"E25.1.6.12")}),1.0]])]});
            var Q193;
            Q193=makeQuery(id+"F0.imprint","IMPRINT",FACE,{"disambiguationData":[TD([[makeQuery(id+"F0.imprint","IMPRINT",EDGE,{"derivedFrom":sQuery(id+"F0.wireOp",EDGE,"E25.1.5.3")}),1.0]])]});
            var Q194;
            Q194=makeQuery(id+"F0.imprint","IMPRINT",FACE,{"disambiguationData":[TD([[makeQuery(id+"F0.imprint","IMPRINT",EDGE,{"derivedFrom":sQuery(id+"F0.wireOp",EDGE,"E25.1.5.14")}),1.0]])]});
            var Q195;
            Q195=makeQuery(id+"F0.imprint","IMPRINT",FACE,{"disambiguationData":[TD([[makeQuery(id+"F0.imprint","IMPRINT",EDGE,{"derivedFrom":sQuery(id+"F0.wireOp",EDGE,"E25.1.4.5")}),1.0]])]});
            var Q196;
            Q196=makeQuery(id+"F0.imprint","IMPRINT",FACE,{"disambiguationData":[TD([[makeQuery(id+"F0.imprint","IMPRINT",EDGE,{"derivedFrom":sQuery(id+"F0.wireOp",EDGE,"E25.1.4.9")}),1.0]])]});
            var Q197;
            Q197=makeQuery(id+"F0.imprint","IMPRINT",FACE,{"disambiguationData":[TD([[makeQuery(id+"F0.imprint","IMPRINT",EDGE,{"derivedFrom":sQuery(id+"F0.wireOp",EDGE,"E25.1.3.1")}),1.0]])]});
            var Q198;
            Q198=makeQuery(id+"F0.imprint","IMPRINT",FACE,{"disambiguationData":[TD([[makeQuery(id+"F0.imprint","IMPRINT",EDGE,{"derivedFrom":sQuery(id+"F0.wireOp",EDGE,"E25.1.3.18")}),1.0]])]});
            var Q199;
            Q199=makeQuery(id+"F0.imprint","IMPRINT",FACE,{"disambiguationData":[TD([[makeQuery(id+"F0.imprint","IMPRINT",EDGE,{"derivedFrom":sQuery(id+"F0.wireOp",EDGE,"E25.1.2.6")}),1.0]])]});
            var Q200;
            Q200=makeQuery(id+"F0.imprint","IMPRINT",FACE,{"disambiguationData":[TD([[makeQuery(id+"F0.imprint","IMPRINT",EDGE,{"derivedFrom":sQuery(id+"F0.wireOp",EDGE,"E25.1.2.22")}),1.0]])]});
            var Q201;
            Q201=makeQuery(id+"F0.imprint","IMPRINT",FACE,{"disambiguationData":[TD([[makeQuery(id+"F0.imprint","IMPRINT",EDGE,{"derivedFrom":sQuery(id+"F0.wireOp",EDGE,"E25.1.1.20")}),1.0]])]});
            var Q202;
            Q202=makeQuery(id+"F0.imprint","IMPRINT",FACE,{"disambiguationData":[TD([[makeQuery(id+"F0.imprint","IMPRINT",EDGE,{"derivedFrom":sQuery(id+"F0.wireOp",EDGE,"E25.1.1.78")}),1.0]])]});
            var Q203;
            Q203=makeQuery(id+"F0.imprint","IMPRINT",FACE,{"disambiguationData":[TD([[makeQuery(id+"F0.imprint","IMPRINT",EDGE,{"derivedFrom":sQuery(id+"F0.wireOp",EDGE,"E25.1.0.86")}),-1.0]])]});
            var Q204;
            Q204=makeQuery(id+"F0.imprint","IMPRINT",FACE,{"disambiguationData":[TD([[makeQuery(id+"F0.imprint","IMPRINT",EDGE,{"derivedFrom":sQuery(id+"F0.wireOp",EDGE,"E13.9.0.3")}),1.0]])]});
            var Q205;
            Q205=makeQuery(id+"F0.imprint","IMPRINT",FACE,{"disambiguationData":[TD([[makeQuery(id+"F0.imprint","IMPRINT",EDGE,{"derivedFrom":sQuery(id+"F0.wireOp",EDGE,"E25.1.6.8")}),1.0]])]});
            var Q206;
            Q206=makeQuery(id+"F0.imprint","IMPRINT",FACE,{"disambiguationData":[TD([[makeQuery(id+"F0.imprint","IMPRINT",EDGE,{"derivedFrom":sQuery(id+"F0.wireOp",EDGE,"E25.1.7.17")}),1.0]])]});
            var Q207;
            Q207=makeQuery(id+"F0.imprint","IMPRINT",FACE,{"disambiguationData":[TD([[makeQuery(id+"F0.imprint","IMPRINT",EDGE,{"derivedFrom":sQuery(id+"F0.wireOp",EDGE,"E25.1.7.0")}),1.0]])]});
            var Q208;
            Q208=makeQuery(id+"F0.imprint","IMPRINT",FACE,{"disambiguationData":[TD([[makeQuery(id+"F0.imprint","IMPRINT",EDGE,{"derivedFrom":sQuery(id+"F0.wireOp",EDGE,"E25.1.7.4")}),1.0]])]});
            var Q209;
            Q209=makeQuery(id+"F0.imprint","IMPRINT",FACE,{"disambiguationData":[TD([[makeQuery(id+"F0.imprint","IMPRINT",EDGE,{"derivedFrom":sQuery(id+"F0.wireOp",EDGE,"E25.1.7.10")}),1.0]])]});
            var Q210;
            Q210=makeQuery(id+"F0.imprint","IMPRINT",FACE,{"disambiguationData":[TD([[makeQuery(id+"F0.imprint","IMPRINT",EDGE,{"derivedFrom":sQuery(id+"F0.wireOp",EDGE,"E25.1.7.2")}),1.0]])]});
            var Q211;
            Q211=makeQuery(id+"F0.imprint","IMPRINT",FACE,{"disambiguationData":[TD([[makeQuery(id+"F0.imprint","IMPRINT",EDGE,{"derivedFrom":sQuery(id+"F0.wireOp",EDGE,"E25.1.7.13")}),1.0]])]});
            var Q212;
            Q212=makeQuery(id+"F0.imprint","IMPRINT",FACE,{"disambiguationData":[TD([[makeQuery(id+"F0.imprint","IMPRINT",EDGE,{"derivedFrom":sQuery(id+"F0.wireOp",EDGE,"E25.1.6.2")}),1.0]])]});
            var Q213;
            Q213=makeQuery(id+"F0.imprint","IMPRINT",FACE,{"disambiguationData":[TD([[makeQuery(id+"F0.imprint","IMPRINT",EDGE,{"derivedFrom":sQuery(id+"F0.wireOp",EDGE,"E25.1.6.4")}),1.0]])]});
            var Q214;
            Q214=makeQuery(id+"F0.imprint","IMPRINT",FACE,{"disambiguationData":[TD([[makeQuery(id+"F0.imprint","IMPRINT",EDGE,{"derivedFrom":sQuery(id+"F0.wireOp",EDGE,"E25.1.6.0")}),1.0]])]});
            var Q215;
            Q215=makeQuery(id+"F0.imprint","IMPRINT",FACE,{"disambiguationData":[TD([[makeQuery(id+"F0.imprint","IMPRINT",EDGE,{"derivedFrom":sQuery(id+"F0.wireOp",EDGE,"E25.1.7.8")}),1.0]])]});
            var Q216;
            Q216=makeQuery(id+"F0.imprint","IMPRINT",FACE,{"disambiguationData":[TD([[makeQuery(id+"F0.imprint","IMPRINT",EDGE,{"derivedFrom":sQuery(id+"F0.wireOp",EDGE,"E25.1.7.12")}),1.0]])]});
            var Q217;
            Q217=makeQuery(id+"F0.imprint","IMPRINT",FACE,{"disambiguationData":[TD([[makeQuery(id+"F0.imprint","IMPRINT",EDGE,{"derivedFrom":sQuery(id+"F0.wireOp",EDGE,"E25.1.6.3")}),1.0]])]});
            var Q218;
            Q218=makeQuery(id+"F0.imprint","IMPRINT",FACE,{"disambiguationData":[TD([[makeQuery(id+"F0.imprint","IMPRINT",EDGE,{"derivedFrom":sQuery(id+"F0.wireOp",EDGE,"E25.1.6.14")}),1.0]])]});
            var Q219;
            Q219=makeQuery(id+"F0.imprint","IMPRINT",FACE,{"disambiguationData":[TD([[makeQuery(id+"F0.imprint","IMPRINT",EDGE,{"derivedFrom":sQuery(id+"F0.wireOp",EDGE,"E25.1.5.5")}),1.0]])]});
            var Q220;
            Q220=makeQuery(id+"F0.imprint","IMPRINT",FACE,{"disambiguationData":[TD([[makeQuery(id+"F0.imprint","IMPRINT",EDGE,{"derivedFrom":sQuery(id+"F0.wireOp",EDGE,"E25.1.5.9")}),1.0]])]});
            var Q221;
            Q221=makeQuery(id+"F0.imprint","IMPRINT",FACE,{"disambiguationData":[TD([[makeQuery(id+"F0.imprint","IMPRINT",EDGE,{"derivedFrom":sQuery(id+"F0.wireOp",EDGE,"E25.1.4.1")}),1.0]])]});
            var Q222;
            Q222=makeQuery(id+"F0.imprint","IMPRINT",FACE,{"disambiguationData":[TD([[makeQuery(id+"F0.imprint","IMPRINT",EDGE,{"derivedFrom":sQuery(id+"F0.wireOp",EDGE,"E25.1.4.18")}),1.0]])]});
            var Q223;
            Q223=makeQuery(id+"F0.imprint","IMPRINT",FACE,{"disambiguationData":[TD([[makeQuery(id+"F0.imprint","IMPRINT",EDGE,{"derivedFrom":sQuery(id+"F0.wireOp",EDGE,"E25.1.3.6")}),1.0]])]});
            var Q224;
            Q224=makeQuery(id+"F0.imprint","IMPRINT",FACE,{"disambiguationData":[TD([[makeQuery(id+"F0.imprint","IMPRINT",EDGE,{"derivedFrom":sQuery(id+"F0.wireOp",EDGE,"E25.1.3.22")}),1.0]])]});
            var Q225;
            Q225=makeQuery(id+"F0.imprint","IMPRINT",FACE,{"disambiguationData":[TD([[makeQuery(id+"F0.imprint","IMPRINT",EDGE,{"derivedFrom":sQuery(id+"F0.wireOp",EDGE,"E25.1.2.20")}),1.0]])]});
            var Q226;
            Q226=makeQuery(id+"F0.imprint","IMPRINT",FACE,{"disambiguationData":[TD([[makeQuery(id+"F0.imprint","IMPRINT",EDGE,{"derivedFrom":sQuery(id+"F0.wireOp",EDGE,"E25.1.1.81")}),-1.0]])]});
            var Q227;
            Q227=makeQuery(id+"F0.imprint","IMPRINT",FACE,{"disambiguationData":[TD([[makeQuery(id+"F0.imprint","IMPRINT",EDGE,{"derivedFrom":sQuery(id+"F0.wireOp",EDGE,"E42")}),1.0]])]});
            var Q228;
            Q228=makeQuery(id+"F0.imprint","IMPRINT",FACE,{"disambiguationData":[TD([[makeQuery(id+"F0.imprint","IMPRINT",EDGE,{"derivedFrom":sQuery(id+"F0.wireOp",EDGE,"E23.9.0.3")}),1.0]])]});
            var Q229;
            Q229=makeQuery(id+"F0.imprint","IMPRINT",FACE,{"disambiguationData":[TD([[makeQuery(id+"F0.imprint","IMPRINT",EDGE,{"derivedFrom":sQuery(id+"F0.wireOp",EDGE,"E13.8.0.0")}),1.0]])]});
            var Q230;
            Q230=makeQuery(id+"F0.imprint","IMPRINT",FACE,{"disambiguationData":[TD([[makeQuery(id+"F0.imprint","IMPRINT",EDGE,{"derivedFrom":sQuery(id+"F0.wireOp",EDGE,"E13.7.0.0")}),1.0]])]});
            var Q231;
            Q231=makeQuery(id+"F0.imprint","IMPRINT",FACE,{"disambiguationData":[TD([[makeQuery(id+"F0.imprint","IMPRINT",EDGE,{"derivedFrom":sQuery(id+"F0.wireOp",EDGE,"E23.8.0.0")}),1.0]])]});
            var Q232;
            Q232=makeQuery(id+"F0.imprint","IMPRINT",FACE,{"disambiguationData":[TD([[makeQuery(id+"F0.imprint","IMPRINT",EDGE,{"derivedFrom":sQuery(id+"F0.wireOp",EDGE,"E25.0.1.11")}),1.0]])]});
            var Q233;
            Q233=makeQuery(id+"F0.imprint","IMPRINT",FACE,{"disambiguationData":[TD([[makeQuery(id+"F0.imprint","IMPRINT",EDGE,{"derivedFrom":sQuery(id+"F0.wireOp",EDGE,"E25.0.1.7")}),1.0]])]});
            var Q234;
            Q234=makeQuery(id+"F0.imprint","IMPRINT",FACE,{"disambiguationData":[TD([[makeQuery(id+"F0.imprint","IMPRINT",EDGE,{"derivedFrom":sQuery(id+"F0.wireOp",EDGE,"E25.0.2.31")}),1.0]])]});
            var Q235;
            Q235=makeQuery(id+"F0.imprint","IMPRINT",FACE,{"disambiguationData":[TD([[makeQuery(id+"F0.imprint","IMPRINT",EDGE,{"derivedFrom":sQuery(id+"F0.wireOp",EDGE,"E25.1.2.81")}),-1.0]])]});
            var Q236;
            Q236=makeQuery(id+"F0.imprint","IMPRINT",FACE,{"disambiguationData":[TD([[makeQuery(id+"F0.imprint","IMPRINT",EDGE,{"derivedFrom":sQuery(id+"F0.wireOp",EDGE,"E25.1.3.19")}),1.0]])]});
            var Q237;
            Q237=makeQuery(id+"F0.imprint","IMPRINT",FACE,{"disambiguationData":[TD([[makeQuery(id+"F0.imprint","IMPRINT",EDGE,{"derivedFrom":sQuery(id+"F0.wireOp",EDGE,"E25.1.3.20")}),1.0]])]});
            var Q238;
            Q238=makeQuery(id+"F0.imprint","IMPRINT",FACE,{"disambiguationData":[TD([[makeQuery(id+"F0.imprint","IMPRINT",EDGE,{"derivedFrom":sQuery(id+"F0.wireOp",EDGE,"E25.1.4.22")}),1.0]])]});
            var Q239;
            Q239=makeQuery(id+"F0.imprint","IMPRINT",FACE,{"disambiguationData":[TD([[makeQuery(id+"F0.imprint","IMPRINT",EDGE,{"derivedFrom":sQuery(id+"F0.wireOp",EDGE,"E25.1.4.6")}),1.0]])]});
            var Q240;
            Q240=makeQuery(id+"F0.imprint","IMPRINT",FACE,{"disambiguationData":[TD([[makeQuery(id+"F0.imprint","IMPRINT",EDGE,{"derivedFrom":sQuery(id+"F0.wireOp",EDGE,"E25.1.5.18")}),1.0]])]});
            var Q241;
            Q241=makeQuery(id+"F0.imprint","IMPRINT",FACE,{"disambiguationData":[TD([[makeQuery(id+"F0.imprint","IMPRINT",EDGE,{"derivedFrom":sQuery(id+"F0.wireOp",EDGE,"E25.1.5.1")}),1.0]])]});
            var Q242;
            Q242=makeQuery(id+"F0.imprint","IMPRINT",FACE,{"disambiguationData":[TD([[makeQuery(id+"F0.imprint","IMPRINT",EDGE,{"derivedFrom":sQuery(id+"F0.wireOp",EDGE,"E25.1.6.9")}),1.0]])]});
            var Q243;
            Q243=makeQuery(id+"F0.imprint","IMPRINT",FACE,{"disambiguationData":[TD([[makeQuery(id+"F0.imprint","IMPRINT",EDGE,{"derivedFrom":sQuery(id+"F0.wireOp",EDGE,"E25.1.6.5")}),1.0]])]});
            var Q244;
            Q244=makeQuery(id+"F0.imprint","IMPRINT",FACE,{"disambiguationData":[TD([[makeQuery(id+"F0.imprint","IMPRINT",EDGE,{"derivedFrom":sQuery(id+"F0.wireOp",EDGE,"E25.1.7.14")}),1.0]])]});
            var Q245;
            Q245=makeQuery(id+"F0.imprint","IMPRINT",FACE,{"disambiguationData":[TD([[makeQuery(id+"F0.imprint","IMPRINT",EDGE,{"derivedFrom":sQuery(id+"F0.wireOp",EDGE,"E25.1.7.3")}),1.0]])]});
            var Q246;
            Q246=makeQuery(id+"F0.imprint","IMPRINT",FACE,{"disambiguationData":[TD([[makeQuery(id+"F0.imprint","IMPRINT",EDGE,{"derivedFrom":sQuery(id+"F0.wireOp",EDGE,"E25.1.7.5")}),1.0]])]});
            var Q247;
            Q247=makeQuery(id+"F0.imprint","IMPRINT",FACE,{"disambiguationData":[TD([[makeQuery(id+"F0.imprint","IMPRINT",EDGE,{"derivedFrom":sQuery(id+"F0.wireOp",EDGE,"E25.1.7.9")}),1.0]])]});
            var Q248;
            Q248=makeQuery(id+"F0.imprint","IMPRINT",FACE,{"disambiguationData":[TD([[makeQuery(id+"F0.imprint","IMPRINT",EDGE,{"derivedFrom":sQuery(id+"F0.wireOp",EDGE,"E25.1.6.1")}),1.0]])]});
            var Q249;
            Q249=makeQuery(id+"F0.imprint","IMPRINT",FACE,{"disambiguationData":[TD([[makeQuery(id+"F0.imprint","IMPRINT",EDGE,{"derivedFrom":sQuery(id+"F0.wireOp",EDGE,"E25.1.6.18")}),1.0]])]});
            var Q250;
            Q250=makeQuery(id+"F0.imprint","IMPRINT",FACE,{"disambiguationData":[TD([[makeQuery(id+"F0.imprint","IMPRINT",EDGE,{"derivedFrom":sQuery(id+"F0.wireOp",EDGE,"E25.1.5.6")}),1.0]])]});
            var Q251;
            Q251=makeQuery(id+"F0.imprint","IMPRINT",FACE,{"disambiguationData":[TD([[makeQuery(id+"F0.imprint","IMPRINT",EDGE,{"derivedFrom":sQuery(id+"F0.wireOp",EDGE,"E25.1.5.22")}),1.0]])]});
            var Q252;
            Q252=makeQuery(id+"F0.imprint","IMPRINT",FACE,{"disambiguationData":[TD([[makeQuery(id+"F0.imprint","IMPRINT",EDGE,{"derivedFrom":sQuery(id+"F0.wireOp",EDGE,"E25.1.4.20")}),1.0]])]});
            var Q253;
            Q253=makeQuery(id+"F0.imprint","IMPRINT",FACE,{"disambiguationData":[TD([[makeQuery(id+"F0.imprint","IMPRINT",EDGE,{"derivedFrom":sQuery(id+"F0.wireOp",EDGE,"E25.1.4.78")}),1.0]])]});
            var Q254;
            Q254=makeQuery(id+"F0.imprint","IMPRINT",FACE,{"disambiguationData":[TD([[makeQuery(id+"F0.imprint","IMPRINT",EDGE,{"derivedFrom":sQuery(id+"F0.wireOp",EDGE,"E25.1.3.81")}),-1.0]])]});
            var Q255;
            Q255=makeQuery(id+"F0.imprint","IMPRINT",FACE,{"disambiguationData":[TD([[makeQuery(id+"F0.imprint","IMPRINT",EDGE,{"derivedFrom":sQuery(id+"F0.wireOp",EDGE,"E25.0.3.31")}),1.0]])]});
            var Q256;
            Q256=makeQuery(id+"F0.imprint","IMPRINT",FACE,{"disambiguationData":[TD([[makeQuery(id+"F0.imprint","IMPRINT",EDGE,{"derivedFrom":sQuery(id+"F0.wireOp",EDGE,"E25.0.2.7")}),1.0]])]});
            var Q257;
            Q257=makeQuery(id+"F0.imprint","IMPRINT",FACE,{"disambiguationData":[TD([[makeQuery(id+"F0.imprint","IMPRINT",EDGE,{"derivedFrom":sQuery(id+"F0.wireOp",EDGE,"E25.0.2.11")}),1.0]])]});
            var Q258;
            Q258=makeQuery(id+"F0.imprint","IMPRINT",FACE,{"disambiguationData":[TD([[makeQuery(id+"F0.imprint","IMPRINT",EDGE,{"derivedFrom":sQuery(id+"F0.wireOp",EDGE,"E25.0.1.2")}),1.0]])]});
            var Q259;
            Q259=makeQuery(id+"F0.imprint","IMPRINT",FACE,{"disambiguationData":[TD([[makeQuery(id+"F0.imprint","IMPRINT",EDGE,{"derivedFrom":sQuery(id+"F0.wireOp",EDGE,"E25.0.1.13")}),1.0]])]});
            var Q260;
            Q260=makeQuery(id+"F0.imprint","IMPRINT",FACE,{"disambiguationData":[TD([[makeQuery(id+"F0.imprint","IMPRINT",EDGE,{"derivedFrom":sQuery(id+"F0.wireOp",EDGE,"E23.7.0.0")}),1.0]])]});
            var Q261;
            Q261=makeQuery(id+"F0.imprint","IMPRINT",FACE,{"disambiguationData":[TD([[makeQuery(id+"F0.imprint","IMPRINT",EDGE,{"derivedFrom":sQuery(id+"F0.wireOp",EDGE,"E13.6.0.0")}),1.0]])]});
            var Q262;
            Q262=makeQuery(id+"F0.imprint","IMPRINT",FACE,{"disambiguationData":[TD([[makeQuery(id+"F0.imprint","IMPRINT",EDGE,{"derivedFrom":sQuery(id+"F0.wireOp",EDGE,"E23.6.0.0")}),1.0]])]});
            var Q263;
            Q263=makeQuery(id+"F0.imprint","IMPRINT",FACE,{"disambiguationData":[TD([[makeQuery(id+"F0.imprint","IMPRINT",EDGE,{"derivedFrom":sQuery(id+"F0.wireOp",EDGE,"E25.0.1.10")}),1.0]])]});
            var Q264;
            Q264=makeQuery(id+"F0.imprint","IMPRINT",FACE,{"disambiguationData":[TD([[makeQuery(id+"F0.imprint","IMPRINT",EDGE,{"derivedFrom":sQuery(id+"F0.wireOp",EDGE,"E25.0.1.4")}),1.0]])]});
            var Q265;
            Q265=makeQuery(id+"F0.imprint","IMPRINT",FACE,{"disambiguationData":[TD([[makeQuery(id+"F0.imprint","IMPRINT",EDGE,{"derivedFrom":sQuery(id+"F0.wireOp",EDGE,"E25.0.2.13")}),1.0]])]});
            var Q266;
            Q266=makeQuery(id+"F0.imprint","IMPRINT",FACE,{"disambiguationData":[TD([[makeQuery(id+"F0.imprint","IMPRINT",EDGE,{"derivedFrom":sQuery(id+"F0.wireOp",EDGE,"E25.0.2.2")}),1.0]])]});
            var Q267;
            Q267=makeQuery(id+"F0.imprint","IMPRINT",FACE,{"disambiguationData":[TD([[makeQuery(id+"F0.imprint","IMPRINT",EDGE,{"derivedFrom":sQuery(id+"F0.wireOp",EDGE,"E25.0.3.11")}),1.0]])]});
            var Q268;
            Q268=makeQuery(id+"F0.imprint","IMPRINT",FACE,{"disambiguationData":[TD([[makeQuery(id+"F0.imprint","IMPRINT",EDGE,{"derivedFrom":sQuery(id+"F0.wireOp",EDGE,"E25.0.3.7")}),1.0]])]});
            var Q269;
            Q269=makeQuery(id+"F0.imprint","IMPRINT",FACE,{"disambiguationData":[TD([[makeQuery(id+"F0.imprint","IMPRINT",EDGE,{"derivedFrom":sQuery(id+"F0.wireOp",EDGE,"E25.0.4.16")}),1.0]])]});
            var Q270;
            Q270=makeQuery(id+"F0.imprint","IMPRINT",FACE,{"disambiguationData":[TD([[makeQuery(id+"F0.imprint","IMPRINT",EDGE,{"derivedFrom":sQuery(id+"F0.wireOp",EDGE,"E25.1.4.81")}),-1.0]])]});
            var Q271;
            Q271=makeQuery(id+"F0.imprint","IMPRINT",FACE,{"disambiguationData":[TD([[makeQuery(id+"F0.imprint","IMPRINT",EDGE,{"derivedFrom":sQuery(id+"F0.wireOp",EDGE,"E25.0.5.21")}),-1.0]])]});
            var Q272;
            Q272=makeQuery(id+"F0.imprint","IMPRINT",FACE,{"disambiguationData":[TD([[makeQuery(id+"F0.imprint","IMPRINT",EDGE,{"derivedFrom":sQuery(id+"F0.wireOp",EDGE,"E25.1.5.20")}),1.0]])]});
            var Q273;
            Q273=makeQuery(id+"F0.imprint","IMPRINT",FACE,{"disambiguationData":[TD([[makeQuery(id+"F0.imprint","IMPRINT",EDGE,{"derivedFrom":sQuery(id+"F0.wireOp",EDGE,"E25.1.6.22")}),1.0]])]});
            var Q274;
            Q274=makeQuery(id+"F0.imprint","IMPRINT",FACE,{"disambiguationData":[TD([[makeQuery(id+"F0.imprint","IMPRINT",EDGE,{"derivedFrom":sQuery(id+"F0.wireOp",EDGE,"E25.1.6.6")}),1.0]])]});
            var Q275;
            Q275=makeQuery(id+"F0.imprint","IMPRINT",FACE,{"disambiguationData":[TD([[makeQuery(id+"F0.imprint","IMPRINT",EDGE,{"derivedFrom":sQuery(id+"F0.wireOp",EDGE,"E25.1.7.18")}),1.0]])]});
            var Q276;
            Q276=makeQuery(id+"F0.imprint","IMPRINT",FACE,{"disambiguationData":[TD([[makeQuery(id+"F0.imprint","IMPRINT",EDGE,{"derivedFrom":sQuery(id+"F0.wireOp",EDGE,"E25.1.7.1")}),1.0]])]});
            var Q277;
            Q277=makeQuery(id+"F0.imprint","IMPRINT",FACE,{"disambiguationData":[TD([[makeQuery(id+"F0.imprint","IMPRINT",EDGE,{"derivedFrom":sQuery(id+"F0.wireOp",EDGE,"E25.1.7.6")}),1.0]])]});
            var Q278;
            Q278=makeQuery(id+"F0.imprint","IMPRINT",FACE,{"disambiguationData":[TD([[makeQuery(id+"F0.imprint","IMPRINT",EDGE,{"derivedFrom":sQuery(id+"F0.wireOp",EDGE,"E25.1.7.22")}),1.0]])]});
            var Q279;
            Q279=makeQuery(id+"F0.imprint","IMPRINT",FACE,{"disambiguationData":[TD([[makeQuery(id+"F0.imprint","IMPRINT",EDGE,{"derivedFrom":sQuery(id+"F0.wireOp",EDGE,"E25.1.6.20")}),1.0]])]});
            var Q280;
            Q280=makeQuery(id+"F0.imprint","IMPRINT",FACE,{"disambiguationData":[TD([[makeQuery(id+"F0.imprint","IMPRINT",EDGE,{"derivedFrom":sQuery(id+"F0.wireOp",EDGE,"E25.1.6.78")}),1.0]])]});
            var Q281;
            Q281=makeQuery(id+"F0.imprint","IMPRINT",FACE,{"disambiguationData":[TD([[makeQuery(id+"F0.imprint","IMPRINT",EDGE,{"derivedFrom":sQuery(id+"F0.wireOp",EDGE,"E25.1.5.81")}),-1.0]])]});
            var Q282;
            Q282=makeQuery(id+"F0.imprint","IMPRINT",FACE,{"disambiguationData":[TD([[makeQuery(id+"F0.imprint","IMPRINT",EDGE,{"derivedFrom":sQuery(id+"F0.wireOp",EDGE,"E25.0.5.31")}),1.0]])]});
            var Q283;
            Q283=makeQuery(id+"F0.imprint","IMPRINT",FACE,{"disambiguationData":[TD([[makeQuery(id+"F0.imprint","IMPRINT",EDGE,{"derivedFrom":sQuery(id+"F0.wireOp",EDGE,"E25.0.4.7")}),1.0]])]});
            var Q284;
            Q284=makeQuery(id+"F0.imprint","IMPRINT",FACE,{"disambiguationData":[TD([[makeQuery(id+"F0.imprint","IMPRINT",EDGE,{"derivedFrom":sQuery(id+"F0.wireOp",EDGE,"E25.0.4.11")}),1.0]])]});
            var Q285;
            Q285=makeQuery(id+"F0.imprint","IMPRINT",FACE,{"disambiguationData":[TD([[makeQuery(id+"F0.imprint","IMPRINT",EDGE,{"derivedFrom":sQuery(id+"F0.wireOp",EDGE,"E25.0.3.2")}),1.0]])]});
            var Q286;
            Q286=makeQuery(id+"F0.imprint","IMPRINT",FACE,{"disambiguationData":[TD([[makeQuery(id+"F0.imprint","IMPRINT",EDGE,{"derivedFrom":sQuery(id+"F0.wireOp",EDGE,"E25.0.3.13")}),1.0]])]});
            var Q287;
            Q287=makeQuery(id+"F0.imprint","IMPRINT",FACE,{"disambiguationData":[TD([[makeQuery(id+"F0.imprint","IMPRINT",EDGE,{"derivedFrom":sQuery(id+"F0.wireOp",EDGE,"E25.0.2.4")}),1.0]])]});
            var Q288;
            Q288=makeQuery(id+"F0.imprint","IMPRINT",FACE,{"disambiguationData":[TD([[makeQuery(id+"F0.imprint","IMPRINT",EDGE,{"derivedFrom":sQuery(id+"F0.wireOp",EDGE,"E25.0.2.10")}),1.0]])]});
            var Q289;
            Q289=makeQuery(id+"F0.imprint","IMPRINT",FACE,{"disambiguationData":[TD([[makeQuery(id+"F0.imprint","IMPRINT",EDGE,{"derivedFrom":sQuery(id+"F0.wireOp",EDGE,"E25.0.1.0")}),1.0]])]});
            var Q290;
            Q290=makeQuery(id+"F0.imprint","IMPRINT",FACE,{"disambiguationData":[TD([[makeQuery(id+"F0.imprint","IMPRINT",EDGE,{"derivedFrom":sQuery(id+"F0.wireOp",EDGE,"E25.0.3.10")}),1.0]])]});
            var Q291;
            Q291=makeQuery(id+"F0.imprint","IMPRINT",FACE,{"disambiguationData":[TD([[makeQuery(id+"F0.imprint","IMPRINT",EDGE,{"derivedFrom":sQuery(id+"F0.wireOp",EDGE,"E25.0.2.0")}),1.0]])]});
            var Q292;
            Q292=makeQuery(id+"F0.imprint","IMPRINT",FACE,{"disambiguationData":[TD([[makeQuery(id+"F0.imprint","IMPRINT",EDGE,{"derivedFrom":sQuery(id+"F0.wireOp",EDGE,"E25.0.3.4")}),1.0]])]});
            var Q293;
            Q293=makeQuery(id+"F0.imprint","IMPRINT",FACE,{"disambiguationData":[TD([[makeQuery(id+"F0.imprint","IMPRINT",EDGE,{"derivedFrom":sQuery(id+"F0.wireOp",EDGE,"E25.0.4.13")}),1.0]])]});
            var Q294;
            Q294=makeQuery(id+"F0.imprint","IMPRINT",FACE,{"disambiguationData":[TD([[makeQuery(id+"F0.imprint","IMPRINT",EDGE,{"derivedFrom":sQuery(id+"F0.wireOp",EDGE,"E25.0.4.2")}),1.0]])]});
            var Q295;
            Q295=makeQuery(id+"F0.imprint","IMPRINT",FACE,{"disambiguationData":[TD([[makeQuery(id+"F0.imprint","IMPRINT",EDGE,{"derivedFrom":sQuery(id+"F0.wireOp",EDGE,"E25.0.5.11")}),1.0]])]});
            var Q296;
            Q296=makeQuery(id+"F0.imprint","IMPRINT",FACE,{"disambiguationData":[TD([[makeQuery(id+"F0.imprint","IMPRINT",EDGE,{"derivedFrom":sQuery(id+"F0.wireOp",EDGE,"E25.0.5.7")}),1.0]])]});
            var Q297;
            Q297=makeQuery(id+"F0.imprint","IMPRINT",FACE,{"disambiguationData":[TD([[makeQuery(id+"F0.imprint","IMPRINT",EDGE,{"derivedFrom":sQuery(id+"F0.wireOp",EDGE,"E25.0.6.16")}),1.0]])]});
            var Q298;
            Q298=makeQuery(id+"F0.imprint","IMPRINT",FACE,{"disambiguationData":[TD([[makeQuery(id+"F0.imprint","IMPRINT",EDGE,{"derivedFrom":sQuery(id+"F0.wireOp",EDGE,"E25.1.6.81")}),-1.0]])]});
            var Q299;
            {var subQ2=sQuery(id+"F0.wireOp",EDGE,"E25.1.7.19");Q299=makeQuery(id+"F0.imprint","IMPRINT",FACE,{"disambiguationData":[TD([[makeQuery(id+"F0.imprint","IMPRINT",EDGE,{"derivedFrom":subQ2}),1.0]])]});}
            var Q300;
            Q300=makeQuery(id+"F0.imprint","IMPRINT",FACE,{"disambiguationData":[TD([[makeQuery(id+"F0.imprint","IMPRINT",EDGE,{"derivedFrom":sQuery(id+"F0.wireOp",EDGE,"E25.1.7.20")}),1.0]])]});
            var Q301;
            Q301=makeQuery(id+"F0.imprint","IMPRINT",FACE,{"disambiguationData":[TD([[makeQuery(id+"F0.imprint","IMPRINT",EDGE,{"derivedFrom":sQuery(id+"F0.wireOp",EDGE,"E25.1.7.81")}),-1.0]])]});
            var Q302;
            Q302=makeQuery(id+"F0.imprint","IMPRINT",FACE,{"disambiguationData":[TD([[makeQuery(id+"F0.imprint","IMPRINT",EDGE,{"derivedFrom":sQuery(id+"F0.wireOp",EDGE,"E25.0.7.31")}),1.0]])]});
            var Q303;
            Q303=makeQuery(id+"F0.imprint","IMPRINT",FACE,{"disambiguationData":[TD([[makeQuery(id+"F0.imprint","IMPRINT",EDGE,{"derivedFrom":sQuery(id+"F0.wireOp",EDGE,"E25.0.6.7")}),1.0]])]});
            var Q304;
            Q304=makeQuery(id+"F0.imprint","IMPRINT",FACE,{"disambiguationData":[TD([[makeQuery(id+"F0.imprint","IMPRINT",EDGE,{"derivedFrom":sQuery(id+"F0.wireOp",EDGE,"E25.0.6.11")}),1.0]])]});
            var Q305;
            Q305=makeQuery(id+"F0.imprint","IMPRINT",FACE,{"disambiguationData":[TD([[makeQuery(id+"F0.imprint","IMPRINT",EDGE,{"derivedFrom":sQuery(id+"F0.wireOp",EDGE,"E25.0.5.2")}),1.0]])]});
            var Q306;
            Q306=makeQuery(id+"F0.imprint","IMPRINT",FACE,{"disambiguationData":[TD([[makeQuery(id+"F0.imprint","IMPRINT",EDGE,{"derivedFrom":sQuery(id+"F0.wireOp",EDGE,"E25.0.5.13")}),1.0]])]});
            var Q307;
            Q307=makeQuery(id+"F0.imprint","IMPRINT",FACE,{"disambiguationData":[TD([[makeQuery(id+"F0.imprint","IMPRINT",EDGE,{"derivedFrom":sQuery(id+"F0.wireOp",EDGE,"E25.0.4.4")}),1.0]])]});
            var Q308;
            Q308=makeQuery(id+"F0.imprint","IMPRINT",FACE,{"disambiguationData":[TD([[makeQuery(id+"F0.imprint","IMPRINT",EDGE,{"derivedFrom":sQuery(id+"F0.wireOp",EDGE,"E25.0.4.10")}),1.0]])]});
            var Q309;
            Q309=makeQuery(id+"F0.imprint","IMPRINT",FACE,{"disambiguationData":[TD([[makeQuery(id+"F0.imprint","IMPRINT",EDGE,{"derivedFrom":sQuery(id+"F0.wireOp",EDGE,"E25.0.3.0")}),1.0]])]});
            var Q310;
            Q310=makeQuery(id+"F0.imprint","IMPRINT",FACE,{"disambiguationData":[TD([[makeQuery(id+"F0.imprint","IMPRINT",EDGE,{"derivedFrom":sQuery(id+"F0.wireOp",EDGE,"E13.5.0.0")}),1.0]])]});
            var Q311;
            Q311=makeQuery(id+"F0.imprint","IMPRINT",FACE,{"disambiguationData":[TD([[makeQuery(id+"F0.imprint","IMPRINT",EDGE,{"derivedFrom":sQuery(id+"F0.wireOp",EDGE,"E13.4.0.0")}),1.0]])]});
            var Q312;
            Q312=makeQuery(id+"F0.imprint","IMPRINT",FACE,{"disambiguationData":[TD([[makeQuery(id+"F0.imprint","IMPRINT",EDGE,{"derivedFrom":sQuery(id+"F0.wireOp",EDGE,"E23.5.0.0")}),1.0]])]});
            var Q313;
            Q313=makeQuery(id+"F0.imprint","IMPRINT",FACE,{"disambiguationData":[TD([[makeQuery(id+"F0.imprint","IMPRINT",EDGE,{"derivedFrom":sQuery(id+"F0.wireOp",EDGE,"E25.0.1.17")}),1.0]])]});
            var Q314;
            Q314=makeQuery(id+"F0.imprint","IMPRINT",FACE,{"disambiguationData":[TD([[makeQuery(id+"F0.imprint","IMPRINT",EDGE,{"derivedFrom":sQuery(id+"F0.wireOp",EDGE,"E25.0.1.8")}),1.0]])]});
            var Q315;
            Q315=makeQuery(id+"F0.imprint","IMPRINT",FACE,{"disambiguationData":[TD([[makeQuery(id+"F0.imprint","IMPRINT",EDGE,{"derivedFrom":sQuery(id+"F0.wireOp",EDGE,"E25.0.1.12")}),1.0]])]});
            var Q316;
            Q316=makeQuery(id+"F0.imprint","IMPRINT",FACE,{"disambiguationData":[TD([[makeQuery(id+"F0.imprint","IMPRINT",EDGE,{"derivedFrom":sQuery(id+"F0.wireOp",EDGE,"E23.4.0.0")}),1.0]])]});
            var Q317;
            Q317=makeQuery(id+"F0.imprint","IMPRINT",FACE,{"disambiguationData":[TD([[makeQuery(id+"F0.imprint","IMPRINT",EDGE,{"derivedFrom":sQuery(id+"F0.wireOp",EDGE,"E13.3.0.0")}),1.0]])]});
            var Q318;
            Q318=makeQuery(id+"F0.imprint","IMPRINT",FACE,{"disambiguationData":[TD([[makeQuery(id+"F0.imprint","IMPRINT",EDGE,{"derivedFrom":sQuery(id+"F0.wireOp",EDGE,"E25.0.2.17")}),1.0]])]});
            var Q319;
            Q319=makeQuery(id+"F0.imprint","IMPRINT",FACE,{"disambiguationData":[TD([[makeQuery(id+"F0.imprint","IMPRINT",EDGE,{"derivedFrom":sQuery(id+"F0.wireOp",EDGE,"E25.0.3.17")}),1.0]])]});
            var Q320;
            Q320=makeQuery(id+"F0.imprint","IMPRINT",FACE,{"disambiguationData":[TD([[makeQuery(id+"F0.imprint","IMPRINT",EDGE,{"derivedFrom":sQuery(id+"F0.wireOp",EDGE,"E25.0.2.8")}),1.0]])]});
            var Q321;
            Q321=makeQuery(id+"F0.imprint","IMPRINT",FACE,{"disambiguationData":[TD([[makeQuery(id+"F0.imprint","IMPRINT",EDGE,{"derivedFrom":sQuery(id+"F0.wireOp",EDGE,"E25.0.2.12")}),1.0]])]});
            var Q322;
            Q322=makeQuery(id+"F0.imprint","IMPRINT",FACE,{"disambiguationData":[TD([[makeQuery(id+"F0.imprint","IMPRINT",EDGE,{"derivedFrom":sQuery(id+"F0.wireOp",EDGE,"E25.0.1.3")}),1.0]])]});
            var Q323;
            Q323=makeQuery(id+"F0.imprint","IMPRINT",FACE,{"disambiguationData":[TD([[makeQuery(id+"F0.imprint","IMPRINT",EDGE,{"derivedFrom":sQuery(id+"F0.wireOp",EDGE,"E25.0.1.14")}),1.0]])]});
            var Q324;
            Q324=makeQuery(id+"F0.imprint","IMPRINT",FACE,{"disambiguationData":[TD([[makeQuery(id+"F0.imprint","IMPRINT",EDGE,{"derivedFrom":sQuery(id+"F0.wireOp",EDGE,"E23.3.0.0")}),1.0]])]});
            var Q325;
            Q325=makeQuery(id+"F0.imprint","IMPRINT",FACE,{"disambiguationData":[TD([[makeQuery(id+"F0.imprint","IMPRINT",EDGE,{"derivedFrom":sQuery(id+"F0.wireOp",EDGE,"E13.2.0.0")}),1.0]])]});
            var Q326;
            Q326=makeQuery(id+"F0.imprint","IMPRINT",FACE,{"disambiguationData":[TD([[makeQuery(id+"F0.imprint","IMPRINT",EDGE,{"derivedFrom":sQuery(id+"F0.wireOp",EDGE,"E13.1.0.0")}),1.0]])]});
            var Q327;
            Q327=makeQuery(id+"F0.imprint","IMPRINT",FACE,{"disambiguationData":[TD([[makeQuery(id+"F0.imprint","IMPRINT",EDGE,{"derivedFrom":sQuery(id+"F0.wireOp",EDGE,"E23.2.0.0")}),1.0]])]});
            var Q328;
            Q328=makeQuery(id+"F0.imprint","IMPRINT",FACE,{"disambiguationData":[TD([[makeQuery(id+"F0.imprint","IMPRINT",EDGE,{"derivedFrom":sQuery(id+"F0.wireOp",EDGE,"E25.0.1.9")}),1.0]])]});
            var Q329;
            Q329=makeQuery(id+"F0.imprint","IMPRINT",FACE,{"disambiguationData":[TD([[makeQuery(id+"F0.imprint","IMPRINT",EDGE,{"derivedFrom":sQuery(id+"F0.wireOp",EDGE,"E25.0.1.5")}),1.0]])]});
            var Q330;
            Q330=makeQuery(id+"F0.imprint","IMPRINT",FACE,{"disambiguationData":[TD([[makeQuery(id+"F0.imprint","IMPRINT",EDGE,{"derivedFrom":sQuery(id+"F0.wireOp",EDGE,"E25.0.2.14")}),1.0]])]});
            var Q331;
            Q331=makeQuery(id+"F0.imprint","IMPRINT",FACE,{"disambiguationData":[TD([[makeQuery(id+"F0.imprint","IMPRINT",EDGE,{"derivedFrom":sQuery(id+"F0.wireOp",EDGE,"E25.0.2.3")}),1.0]])]});
            var Q332;
            Q332=makeQuery(id+"F0.imprint","IMPRINT",FACE,{"disambiguationData":[TD([[makeQuery(id+"F0.imprint","IMPRINT",EDGE,{"derivedFrom":sQuery(id+"F0.wireOp",EDGE,"E25.0.3.12")}),1.0]])]});
            var Q333;
            Q333=makeQuery(id+"F0.imprint","IMPRINT",FACE,{"disambiguationData":[TD([[makeQuery(id+"F0.imprint","IMPRINT",EDGE,{"derivedFrom":sQuery(id+"F0.wireOp",EDGE,"E25.0.3.8")}),1.0]])]});
            var Q334;
            Q334=makeQuery(id+"F0.imprint","IMPRINT",FACE,{"disambiguationData":[TD([[makeQuery(id+"F0.imprint","IMPRINT",EDGE,{"derivedFrom":sQuery(id+"F0.wireOp",EDGE,"E25.0.4.17")}),1.0]])]});
            var Q335;
            Q335=makeQuery(id+"F0.imprint","IMPRINT",FACE,{"disambiguationData":[TD([[makeQuery(id+"F0.imprint","IMPRINT",EDGE,{"derivedFrom":sQuery(id+"F0.wireOp",EDGE,"E25.0.4.0")}),1.0]])]});
            var Q336;
            Q336=makeQuery(id+"F0.imprint","IMPRINT",FACE,{"disambiguationData":[TD([[makeQuery(id+"F0.imprint","IMPRINT",EDGE,{"derivedFrom":sQuery(id+"F0.wireOp",EDGE,"E25.0.5.10")}),1.0]])]});
            var Q337;
            Q337=makeQuery(id+"F0.imprint","IMPRINT",FACE,{"disambiguationData":[TD([[makeQuery(id+"F0.imprint","IMPRINT",EDGE,{"derivedFrom":sQuery(id+"F0.wireOp",EDGE,"E25.0.5.4")}),1.0]])]});
            var Q338;
            Q338=makeQuery(id+"F0.imprint","IMPRINT",FACE,{"disambiguationData":[TD([[makeQuery(id+"F0.imprint","IMPRINT",EDGE,{"derivedFrom":sQuery(id+"F0.wireOp",EDGE,"E25.0.6.13")}),1.0]])]});
            var Q339;
            Q339=makeQuery(id+"F0.imprint","IMPRINT",FACE,{"disambiguationData":[TD([[makeQuery(id+"F0.imprint","IMPRINT",EDGE,{"derivedFrom":sQuery(id+"F0.wireOp",EDGE,"E25.0.6.2")}),1.0]])]});
            var Q340;
            Q340=makeQuery(id+"F0.imprint","IMPRINT",FACE,{"disambiguationData":[TD([[makeQuery(id+"F0.imprint","IMPRINT",EDGE,{"derivedFrom":sQuery(id+"F0.wireOp",EDGE,"E25.0.7.11")}),1.0]])]});
            var Q341;
            Q341=makeQuery(id+"F0.imprint","IMPRINT",FACE,{"disambiguationData":[TD([[makeQuery(id+"F0.imprint","IMPRINT",EDGE,{"derivedFrom":sQuery(id+"F0.wireOp",EDGE,"E25.0.7.7")}),1.0]])]});
            var Q342;
            Q342=makeQuery(id+"F0.imprint","IMPRINT",FACE,{"disambiguationData":[TD([[makeQuery(id+"F0.imprint","IMPRINT",EDGE,{"derivedFrom":sQuery(id+"F0.wireOp",EDGE,"E25.0.7.2")}),1.0]])]});
            var Q343;
            Q343=makeQuery(id+"F0.imprint","IMPRINT",FACE,{"disambiguationData":[TD([[makeQuery(id+"F0.imprint","IMPRINT",EDGE,{"derivedFrom":sQuery(id+"F0.wireOp",EDGE,"E25.0.7.13")}),1.0]])]});
            var Q344;
            Q344=makeQuery(id+"F0.imprint","IMPRINT",FACE,{"disambiguationData":[TD([[makeQuery(id+"F0.imprint","IMPRINT",EDGE,{"derivedFrom":sQuery(id+"F0.wireOp",EDGE,"E25.0.6.4")}),1.0]])]});
            var Q345;
            Q345=makeQuery(id+"F0.imprint","IMPRINT",FACE,{"disambiguationData":[TD([[makeQuery(id+"F0.imprint","IMPRINT",EDGE,{"derivedFrom":sQuery(id+"F0.wireOp",EDGE,"E25.0.6.10")}),1.0]])]});
            var Q346;
            Q346=makeQuery(id+"F0.imprint","IMPRINT",FACE,{"disambiguationData":[TD([[makeQuery(id+"F0.imprint","IMPRINT",EDGE,{"derivedFrom":sQuery(id+"F0.wireOp",EDGE,"E25.0.5.0")}),1.0]])]});
            var Q347;
            Q347=makeQuery(id+"F0.imprint","IMPRINT",FACE,{"disambiguationData":[TD([[makeQuery(id+"F0.imprint","IMPRINT",EDGE,{"derivedFrom":sQuery(id+"F0.wireOp",EDGE,"E25.0.5.17")}),1.0]])]});
            var Q348;
            Q348=makeQuery(id+"F0.imprint","IMPRINT",FACE,{"disambiguationData":[TD([[makeQuery(id+"F0.imprint","IMPRINT",EDGE,{"derivedFrom":sQuery(id+"F0.wireOp",EDGE,"E25.0.4.8")}),1.0]])]});
            var Q349;
            Q349=makeQuery(id+"F0.imprint","IMPRINT",FACE,{"disambiguationData":[TD([[makeQuery(id+"F0.imprint","IMPRINT",EDGE,{"derivedFrom":sQuery(id+"F0.wireOp",EDGE,"E25.0.4.3")}),1.0]])]});
            var Q350;
            Q350=makeQuery(id+"F0.imprint","IMPRINT",FACE,{"disambiguationData":[TD([[makeQuery(id+"F0.imprint","IMPRINT",EDGE,{"derivedFrom":sQuery(id+"F0.wireOp",EDGE,"E25.0.4.12")}),1.0]])]});
            var Q351;
            Q351=makeQuery(id+"F0.imprint","IMPRINT",FACE,{"disambiguationData":[TD([[makeQuery(id+"F0.imprint","IMPRINT",EDGE,{"derivedFrom":sQuery(id+"F0.wireOp",EDGE,"E25.0.3.3")}),1.0]])]});
            var Q352;
            Q352=makeQuery(id+"F0.imprint","IMPRINT",FACE,{"disambiguationData":[TD([[makeQuery(id+"F0.imprint","IMPRINT",EDGE,{"derivedFrom":sQuery(id+"F0.wireOp",EDGE,"E25.0.3.14")}),1.0]])]});
            var Q353;
            Q353=makeQuery(id+"F0.imprint","IMPRINT",FACE,{"disambiguationData":[TD([[makeQuery(id+"F0.imprint","IMPRINT",EDGE,{"derivedFrom":sQuery(id+"F0.wireOp",EDGE,"E25.0.2.5")}),1.0]])]});
            var Q354;
            Q354=makeQuery(id+"F0.imprint","IMPRINT",FACE,{"disambiguationData":[TD([[makeQuery(id+"F0.imprint","IMPRINT",EDGE,{"derivedFrom":sQuery(id+"F0.wireOp",EDGE,"E25.0.2.9")}),1.0]])]});
            var Q355;
            Q355=makeQuery(id+"F0.imprint","IMPRINT",FACE,{"disambiguationData":[TD([[makeQuery(id+"F0.imprint","IMPRINT",EDGE,{"derivedFrom":sQuery(id+"F0.wireOp",EDGE,"E25.0.1.1")}),1.0]])]});
            var Q356;
            Q356=makeQuery(id+"F0.imprint","IMPRINT",FACE,{"disambiguationData":[TD([[makeQuery(id+"F0.imprint","IMPRINT",EDGE,{"derivedFrom":sQuery(id+"F0.wireOp",EDGE,"E25.0.1.18")}),1.0]])]});
            var Q357;
            Q357=makeQuery(id+"F0.imprint","IMPRINT",FACE,{"disambiguationData":[TD([[makeQuery(id+"F0.imprint","IMPRINT",EDGE,{"derivedFrom":sQuery(id+"F0.wireOp",EDGE,"E23.1.0.0")}),1.0]])]});
            var Q358;
            Q358=makeQuery(id+"F0.imprint","IMPRINT",FACE,{"disambiguationData":[TD([[makeQuery(id+"F0.imprint","IMPRINT",EDGE,{"derivedFrom":sQuery(id+"F0.wireOp",EDGE,"E9")}),1.0]])]});
            var Q359;
            Q359=makeQuery(id+"F0.imprint","IMPRINT",FACE,{"disambiguationData":[TD([[makeQuery(id+"F0.imprint","IMPRINT",EDGE,{"derivedFrom":sQuery(id+"F0.wireOp",EDGE,"E4")}),1.0]])]});
            var Q360;
            Q360=makeQuery(id+"F0.imprint","IMPRINT",FACE,{"disambiguationData":[TD([[makeQuery(id+"F0.imprint","IMPRINT",EDGE,{"derivedFrom":sQuery(id+"F0.wireOp",EDGE,"E19")}),1.0]])]});
            var Q361;
            Q361=makeQuery(id+"F0.imprint","IMPRINT",FACE,{"disambiguationData":[TD([[makeQuery(id+"F0.imprint","IMPRINT",EDGE,{"derivedFrom":sQuery(id+"F0.wireOp",EDGE,"E25.0.1.22")}),1.0]])]});
            var Q362;
            Q362=makeQuery(id+"F0.imprint","IMPRINT",FACE,{"disambiguationData":[TD([[makeQuery(id+"F0.imprint","IMPRINT",EDGE,{"derivedFrom":sQuery(id+"F0.wireOp",EDGE,"E25.0.1.6")}),1.0]])]});
            var Q363;
            Q363=makeQuery(id+"F0.imprint","IMPRINT",FACE,{"disambiguationData":[TD([[makeQuery(id+"F0.imprint","IMPRINT",EDGE,{"derivedFrom":sQuery(id+"F0.wireOp",EDGE,"E25.0.2.18")}),1.0]])]});
            var Q364;
            Q364=makeQuery(id+"F0.imprint","IMPRINT",FACE,{"disambiguationData":[TD([[makeQuery(id+"F0.imprint","IMPRINT",EDGE,{"derivedFrom":sQuery(id+"F0.wireOp",EDGE,"E25.0.2.1")}),1.0]])]});
            var Q365;
            Q365=makeQuery(id+"F0.imprint","IMPRINT",FACE,{"disambiguationData":[TD([[makeQuery(id+"F0.imprint","IMPRINT",EDGE,{"derivedFrom":sQuery(id+"F0.wireOp",EDGE,"E25.0.3.9")}),1.0]])]});
            var Q366;
            Q366=makeQuery(id+"F0.imprint","IMPRINT",FACE,{"disambiguationData":[TD([[makeQuery(id+"F0.imprint","IMPRINT",EDGE,{"derivedFrom":sQuery(id+"F0.wireOp",EDGE,"E25.0.3.5")}),1.0]])]});
            var Q367;
            Q367=makeQuery(id+"F0.imprint","IMPRINT",FACE,{"disambiguationData":[TD([[makeQuery(id+"F0.imprint","IMPRINT",EDGE,{"derivedFrom":sQuery(id+"F0.wireOp",EDGE,"E25.0.4.14")}),1.0]])]});
            var Q368;
            Q368=makeQuery(id+"F0.imprint","IMPRINT",FACE,{"disambiguationData":[TD([[makeQuery(id+"F0.imprint","IMPRINT",EDGE,{"derivedFrom":sQuery(id+"F0.wireOp",EDGE,"E25.0.5.12")}),1.0]])]});
            var Q369;
            Q369=makeQuery(id+"F0.imprint","IMPRINT",FACE,{"disambiguationData":[TD([[makeQuery(id+"F0.imprint","IMPRINT",EDGE,{"derivedFrom":sQuery(id+"F0.wireOp",EDGE,"E25.0.5.8")}),1.0]])]});
            var Q370;
            Q370=makeQuery(id+"F0.imprint","IMPRINT",FACE,{"disambiguationData":[TD([[makeQuery(id+"F0.imprint","IMPRINT",EDGE,{"derivedFrom":sQuery(id+"F0.wireOp",EDGE,"E25.0.6.17")}),1.0]])]});
            var Q371;
            Q371=makeQuery(id+"F0.imprint","IMPRINT",FACE,{"disambiguationData":[TD([[makeQuery(id+"F0.imprint","IMPRINT",EDGE,{"derivedFrom":sQuery(id+"F0.wireOp",EDGE,"E25.0.6.0")}),1.0]])]});
            var Q372;
            Q372=makeQuery(id+"F0.imprint","IMPRINT",FACE,{"disambiguationData":[TD([[makeQuery(id+"F0.imprint","IMPRINT",EDGE,{"derivedFrom":sQuery(id+"F0.wireOp",EDGE,"E25.0.7.10")}),1.0]])]});
            var Q373;
            Q373=makeQuery(id+"F0.imprint","IMPRINT",FACE,{"disambiguationData":[TD([[makeQuery(id+"F0.imprint","IMPRINT",EDGE,{"derivedFrom":sQuery(id+"F0.wireOp",EDGE,"E25.0.7.4")}),1.0]])]});
            var Q374;
            Q374=makeQuery(id+"F0.imprint","IMPRINT",FACE,{"disambiguationData":[TD([[makeQuery(id+"F0.imprint","IMPRINT",EDGE,{"derivedFrom":sQuery(id+"F0.wireOp",EDGE,"E25.0.7.0")}),1.0]])]});
            var Q375;
            Q375=makeQuery(id+"F0.imprint","IMPRINT",FACE,{"disambiguationData":[TD([[makeQuery(id+"F0.imprint","IMPRINT",EDGE,{"derivedFrom":sQuery(id+"F0.wireOp",EDGE,"E25.0.7.17")}),1.0]])]});
            var Q376;
            Q376=makeQuery(id+"F0.imprint","IMPRINT",FACE,{"disambiguationData":[TD([[makeQuery(id+"F0.imprint","IMPRINT",EDGE,{"derivedFrom":sQuery(id+"F0.wireOp",EDGE,"E25.0.6.8")}),1.0]])]});
            var Q377;
            Q377=makeQuery(id+"F0.imprint","IMPRINT",FACE,{"disambiguationData":[TD([[makeQuery(id+"F0.imprint","IMPRINT",EDGE,{"derivedFrom":sQuery(id+"F0.wireOp",EDGE,"E25.0.6.12")}),1.0]])]});
            var Q378;
            Q378=makeQuery(id+"F0.imprint","IMPRINT",FACE,{"disambiguationData":[TD([[makeQuery(id+"F0.imprint","IMPRINT",EDGE,{"derivedFrom":sQuery(id+"F0.wireOp",EDGE,"E25.0.5.3")}),1.0]])]});
            var Q379;
            Q379=makeQuery(id+"F0.imprint","IMPRINT",FACE,{"disambiguationData":[TD([[makeQuery(id+"F0.imprint","IMPRINT",EDGE,{"derivedFrom":sQuery(id+"F0.wireOp",EDGE,"E25.0.5.14")}),1.0]])]});
            var Q380;
            Q380=makeQuery(id+"F0.imprint","IMPRINT",FACE,{"disambiguationData":[TD([[makeQuery(id+"F0.imprint","IMPRINT",EDGE,{"derivedFrom":sQuery(id+"F0.wireOp",EDGE,"E25.0.4.5")}),1.0]])]});
            var Q381;
            Q381=makeQuery(id+"F0.imprint","IMPRINT",FACE,{"disambiguationData":[TD([[makeQuery(id+"F0.imprint","IMPRINT",EDGE,{"derivedFrom":sQuery(id+"F0.wireOp",EDGE,"E25.0.4.9")}),1.0]])]});
            var Q382;
            Q382=makeQuery(id+"F0.imprint","IMPRINT",FACE,{"disambiguationData":[TD([[makeQuery(id+"F0.imprint","IMPRINT",EDGE,{"derivedFrom":sQuery(id+"F0.wireOp",EDGE,"E25.0.3.1")}),1.0]])]});
            var Q383;
            Q383=makeQuery(id+"F0.imprint","IMPRINT",FACE,{"disambiguationData":[TD([[makeQuery(id+"F0.imprint","IMPRINT",EDGE,{"derivedFrom":sQuery(id+"F0.wireOp",EDGE,"E25.0.3.18")}),1.0]])]});
            var Q384;
            Q384=makeQuery(id+"F0.imprint","IMPRINT",FACE,{"disambiguationData":[TD([[makeQuery(id+"F0.imprint","IMPRINT",EDGE,{"derivedFrom":sQuery(id+"F0.wireOp",EDGE,"E25.0.2.6")}),1.0]])]});
            var Q385;
            Q385=makeQuery(id+"F0.imprint","IMPRINT",FACE,{"disambiguationData":[TD([[makeQuery(id+"F0.imprint","IMPRINT",EDGE,{"derivedFrom":sQuery(id+"F0.wireOp",EDGE,"E25.0.2.22")}),1.0]])]});
            var Q386;
            Q386=makeQuery(id+"F0.imprint","IMPRINT",FACE,{"disambiguationData":[TD([[makeQuery(id+"F0.imprint","IMPRINT",EDGE,{"derivedFrom":sQuery(id+"F0.wireOp",EDGE,"E25.0.1.20")}),1.0]])]});
            var Q387;
            {var subQ0=sQuery(id+"F0.wireOp",EDGE,"E25.0.1.19");Q387=makeQuery(id+"F0.imprint","IMPRINT",FACE,{"disambiguationData":[TD([[makeQuery(id+"F0.imprint","IMPRINT",EDGE,{"derivedFrom":subQ0}),1.0]])]});}
            var Q388;
            Q388=makeQuery(id+"F0.imprint","IMPRINT",FACE,{"disambiguationData":[TD([[makeQuery(id+"F0.imprint","IMPRINT",EDGE,{"derivedFrom":sQuery(id+"F0.wireOp",EDGE,"E14")}),-1.0]])]});
            var Q389;
            Q389=makeQuery(id+"F0.imprint","IMPRINT",FACE,{"disambiguationData":[TD([[makeQuery(id+"F0.imprint","IMPRINT",EDGE,{"derivedFrom":sQuery(id+"F0.wireOp",EDGE,"E25.0.1.81")}),-1.0]])]});
            var Q390;
            {var subQ0=sQuery(id+"F0.wireOp",EDGE,"E25.0.2.19");Q390=makeQuery(id+"F0.imprint","IMPRINT",FACE,{"disambiguationData":[TD([[makeQuery(id+"F0.imprint","IMPRINT",EDGE,{"derivedFrom":subQ0}),1.0]])]});}
            var Q391;
            Q391=makeQuery(id+"F0.imprint","IMPRINT",FACE,{"disambiguationData":[TD([[makeQuery(id+"F0.imprint","IMPRINT",EDGE,{"derivedFrom":sQuery(id+"F0.wireOp",EDGE,"E25.0.2.20")}),1.0]])]});
            var Q392;
            Q392=makeQuery(id+"F0.imprint","IMPRINT",FACE,{"disambiguationData":[TD([[makeQuery(id+"F0.imprint","IMPRINT",EDGE,{"derivedFrom":sQuery(id+"F0.wireOp",EDGE,"E25.0.3.22")}),1.0]])]});
            var Q393;
            Q393=makeQuery(id+"F0.imprint","IMPRINT",FACE,{"disambiguationData":[TD([[makeQuery(id+"F0.imprint","IMPRINT",EDGE,{"derivedFrom":sQuery(id+"F0.wireOp",EDGE,"E25.0.4.18")}),1.0]])]});
            var Q394;
            Q394=makeQuery(id+"F0.imprint","IMPRINT",FACE,{"disambiguationData":[TD([[makeQuery(id+"F0.imprint","IMPRINT",EDGE,{"derivedFrom":sQuery(id+"F0.wireOp",EDGE,"E25.0.4.1")}),1.0]])]});
            var Q395;
            Q395=makeQuery(id+"F0.imprint","IMPRINT",FACE,{"disambiguationData":[TD([[makeQuery(id+"F0.imprint","IMPRINT",EDGE,{"derivedFrom":sQuery(id+"F0.wireOp",EDGE,"E25.0.3.6")}),1.0]])]});
            var Q396;
            Q396=makeQuery(id+"F0.imprint","IMPRINT",FACE,{"disambiguationData":[TD([[makeQuery(id+"F0.imprint","IMPRINT",EDGE,{"derivedFrom":sQuery(id+"F0.wireOp",EDGE,"E25.0.5.9")}),1.0]])]});
            var Q397;
            Q397=makeQuery(id+"F0.imprint","IMPRINT",FACE,{"disambiguationData":[TD([[makeQuery(id+"F0.imprint","IMPRINT",EDGE,{"derivedFrom":sQuery(id+"F0.wireOp",EDGE,"E25.0.5.5")}),1.0]])]});
            var Q398;
            Q398=makeQuery(id+"F0.imprint","IMPRINT",FACE,{"disambiguationData":[TD([[makeQuery(id+"F0.imprint","IMPRINT",EDGE,{"derivedFrom":sQuery(id+"F0.wireOp",EDGE,"E25.0.6.14")}),1.0]])]});
            var Q399;
            Q399=makeQuery(id+"F0.imprint","IMPRINT",FACE,{"disambiguationData":[TD([[makeQuery(id+"F0.imprint","IMPRINT",EDGE,{"derivedFrom":sQuery(id+"F0.wireOp",EDGE,"E25.0.6.3")}),1.0]])]});
            var Q400;
            Q400=makeQuery(id+"F0.imprint","IMPRINT",FACE,{"disambiguationData":[TD([[makeQuery(id+"F0.imprint","IMPRINT",EDGE,{"derivedFrom":sQuery(id+"F0.wireOp",EDGE,"E25.0.7.12")}),1.0]])]});
            var Q401;
            Q401=makeQuery(id+"F0.imprint","IMPRINT",FACE,{"disambiguationData":[TD([[makeQuery(id+"F0.imprint","IMPRINT",EDGE,{"derivedFrom":sQuery(id+"F0.wireOp",EDGE,"E25.0.7.8")}),1.0]])]});
            var Q402;
            Q402=makeQuery(id+"F0.imprint","IMPRINT",FACE,{"disambiguationData":[TD([[makeQuery(id+"F0.imprint","IMPRINT",EDGE,{"derivedFrom":sQuery(id+"F0.wireOp",EDGE,"E25.0.7.3")}),1.0]])]});
            var Q403;
            Q403=makeQuery(id+"F0.imprint","IMPRINT",FACE,{"disambiguationData":[TD([[makeQuery(id+"F0.imprint","IMPRINT",EDGE,{"derivedFrom":sQuery(id+"F0.wireOp",EDGE,"E25.0.7.14")}),1.0]])]});
            var Q404;
            Q404=makeQuery(id+"F0.imprint","IMPRINT",FACE,{"disambiguationData":[TD([[makeQuery(id+"F0.imprint","IMPRINT",EDGE,{"derivedFrom":sQuery(id+"F0.wireOp",EDGE,"E25.0.6.5")}),1.0]])]});
            var Q405;
            Q405=makeQuery(id+"F0.imprint","IMPRINT",FACE,{"disambiguationData":[TD([[makeQuery(id+"F0.imprint","IMPRINT",EDGE,{"derivedFrom":sQuery(id+"F0.wireOp",EDGE,"E25.0.6.9")}),1.0]])]});
            var Q406;
            Q406=makeQuery(id+"F0.imprint","IMPRINT",FACE,{"disambiguationData":[TD([[makeQuery(id+"F0.imprint","IMPRINT",EDGE,{"derivedFrom":sQuery(id+"F0.wireOp",EDGE,"E25.0.5.1")}),1.0]])]});
            var Q407;
            Q407=makeQuery(id+"F0.imprint","IMPRINT",FACE,{"disambiguationData":[TD([[makeQuery(id+"F0.imprint","IMPRINT",EDGE,{"derivedFrom":sQuery(id+"F0.wireOp",EDGE,"E25.0.5.18")}),1.0]])]});
            var Q408;
            Q408=makeQuery(id+"F0.imprint","IMPRINT",FACE,{"disambiguationData":[TD([[makeQuery(id+"F0.imprint","IMPRINT",EDGE,{"derivedFrom":sQuery(id+"F0.wireOp",EDGE,"E25.0.4.6")}),1.0]])]});
            var Q409;
            Q409=makeQuery(id+"F0.imprint","IMPRINT",FACE,{"disambiguationData":[TD([[makeQuery(id+"F0.imprint","IMPRINT",EDGE,{"derivedFrom":sQuery(id+"F0.wireOp",EDGE,"E25.0.4.22")}),1.0]])]});
            var Q410;
            Q410=makeQuery(id+"F0.imprint","IMPRINT",FACE,{"disambiguationData":[TD([[makeQuery(id+"F0.imprint","IMPRINT",EDGE,{"derivedFrom":sQuery(id+"F0.wireOp",EDGE,"E25.0.3.20")}),1.0]])]});
            var Q411;
            {var subQ0=sQuery(id+"F0.wireOp",EDGE,"E25.0.3.19");Q411=makeQuery(id+"F0.imprint","IMPRINT",FACE,{"disambiguationData":[TD([[makeQuery(id+"F0.imprint","IMPRINT",EDGE,{"derivedFrom":subQ0}),1.0]])]});}
            var Q412;
            Q412=makeQuery(id+"F0.imprint","IMPRINT",FACE,{"disambiguationData":[TD([[makeQuery(id+"F0.imprint","IMPRINT",EDGE,{"derivedFrom":sQuery(id+"F0.wireOp",EDGE,"E25.0.2.81")}),-1.0]])]});
            var Q413;
            Q413=makeQuery(id+"F0.imprint","IMPRINT",FACE,{"disambiguationData":[TD([[makeQuery(id+"F0.imprint","IMPRINT",EDGE,{"derivedFrom":sQuery(id+"F0.wireOp",EDGE,"E25.0.3.81")}),-1.0]])]});
            var Q414;
            {var subQ0=sQuery(id+"F0.wireOp",EDGE,"E25.0.4.19");Q414=makeQuery(id+"F0.imprint","IMPRINT",FACE,{"disambiguationData":[TD([[makeQuery(id+"F0.imprint","IMPRINT",EDGE,{"derivedFrom":subQ0}),1.0]])]});}
            var Q415;
            Q415=makeQuery(id+"F0.imprint","IMPRINT",FACE,{"disambiguationData":[TD([[makeQuery(id+"F0.imprint","IMPRINT",EDGE,{"derivedFrom":sQuery(id+"F0.wireOp",EDGE,"E25.0.4.20")}),1.0]])]});
            var Q416;
            Q416=makeQuery(id+"F0.imprint","IMPRINT",FACE,{"disambiguationData":[TD([[makeQuery(id+"F0.imprint","IMPRINT",EDGE,{"derivedFrom":sQuery(id+"F0.wireOp",EDGE,"E25.0.5.22")}),1.0]])]});
            var Q417;
            Q417=makeQuery(id+"F0.imprint","IMPRINT",FACE,{"disambiguationData":[TD([[makeQuery(id+"F0.imprint","IMPRINT",EDGE,{"derivedFrom":sQuery(id+"F0.wireOp",EDGE,"E25.0.5.6")}),1.0]])]});
            var Q418;
            Q418=makeQuery(id+"F0.imprint","IMPRINT",FACE,{"disambiguationData":[TD([[makeQuery(id+"F0.imprint","IMPRINT",EDGE,{"derivedFrom":sQuery(id+"F0.wireOp",EDGE,"E25.0.6.18")}),1.0]])]});
            var Q419;
            Q419=makeQuery(id+"F0.imprint","IMPRINT",FACE,{"disambiguationData":[TD([[makeQuery(id+"F0.imprint","IMPRINT",EDGE,{"derivedFrom":sQuery(id+"F0.wireOp",EDGE,"E25.0.6.1")}),1.0]])]});
            var Q420;
            Q420=makeQuery(id+"F0.imprint","IMPRINT",FACE,{"disambiguationData":[TD([[makeQuery(id+"F0.imprint","IMPRINT",EDGE,{"derivedFrom":sQuery(id+"F0.wireOp",EDGE,"E25.0.7.9")}),1.0]])]});
            var Q421;
            Q421=makeQuery(id+"F0.imprint","IMPRINT",FACE,{"disambiguationData":[TD([[makeQuery(id+"F0.imprint","IMPRINT",EDGE,{"derivedFrom":sQuery(id+"F0.wireOp",EDGE,"E25.0.7.5")}),1.0]])]});
            var Q422;
            Q422=makeQuery(id+"F0.imprint","IMPRINT",FACE,{"disambiguationData":[TD([[makeQuery(id+"F0.imprint","IMPRINT",EDGE,{"derivedFrom":sQuery(id+"F0.wireOp",EDGE,"E25.0.7.1")}),1.0]])]});
            var Q423;
            Q423=makeQuery(id+"F0.imprint","IMPRINT",FACE,{"disambiguationData":[TD([[makeQuery(id+"F0.imprint","IMPRINT",EDGE,{"derivedFrom":sQuery(id+"F0.wireOp",EDGE,"E25.0.7.18")}),1.0]])]});
            var Q424;
            Q424=makeQuery(id+"F0.imprint","IMPRINT",FACE,{"disambiguationData":[TD([[makeQuery(id+"F0.imprint","IMPRINT",EDGE,{"derivedFrom":sQuery(id+"F0.wireOp",EDGE,"E25.0.6.6")}),1.0]])]});
            var Q425;
            Q425=makeQuery(id+"F0.imprint","IMPRINT",FACE,{"disambiguationData":[TD([[makeQuery(id+"F0.imprint","IMPRINT",EDGE,{"derivedFrom":sQuery(id+"F0.wireOp",EDGE,"E25.0.6.22")}),1.0]])]});
            var Q426;
            Q426=makeQuery(id+"F0.imprint","IMPRINT",FACE,{"disambiguationData":[TD([[makeQuery(id+"F0.imprint","IMPRINT",EDGE,{"derivedFrom":sQuery(id+"F0.wireOp",EDGE,"E25.0.5.20")}),1.0]])]});
            var Q427;
            {var subQ0=sQuery(id+"F0.wireOp",EDGE,"E25.0.5.19");Q427=makeQuery(id+"F0.imprint","IMPRINT",FACE,{"disambiguationData":[TD([[makeQuery(id+"F0.imprint","IMPRINT",EDGE,{"derivedFrom":subQ0}),1.0]])]});}
            var Q428;
            Q428=makeQuery(id+"F0.imprint","IMPRINT",FACE,{"disambiguationData":[TD([[makeQuery(id+"F0.imprint","IMPRINT",EDGE,{"derivedFrom":sQuery(id+"F0.wireOp",EDGE,"E25.0.4.81")}),-1.0]])]});
            var Q429;
            Q429=makeQuery(id+"F0.imprint","IMPRINT",FACE,{"disambiguationData":[TD([[makeQuery(id+"F0.imprint","IMPRINT",EDGE,{"derivedFrom":sQuery(id+"F0.wireOp",EDGE,"E25.0.5.81")}),-1.0]])]});
            var Q430;
            {var subQ0=sQuery(id+"F0.wireOp",EDGE,"E25.0.6.19");Q430=makeQuery(id+"F0.imprint","IMPRINT",FACE,{"disambiguationData":[TD([[makeQuery(id+"F0.imprint","IMPRINT",EDGE,{"derivedFrom":subQ0}),1.0]])]});}
            var Q431;
            Q431=makeQuery(id+"F0.imprint","IMPRINT",FACE,{"disambiguationData":[TD([[makeQuery(id+"F0.imprint","IMPRINT",EDGE,{"derivedFrom":sQuery(id+"F0.wireOp",EDGE,"E25.0.6.20")}),1.0]])]});
            var Q432;
            Q432=makeQuery(id+"F0.imprint","IMPRINT",FACE,{"disambiguationData":[TD([[makeQuery(id+"F0.imprint","IMPRINT",EDGE,{"derivedFrom":sQuery(id+"F0.wireOp",EDGE,"E25.0.7.22")}),1.0]])]});
            var Q433;
            Q433=makeQuery(id+"F0.imprint","IMPRINT",FACE,{"disambiguationData":[TD([[makeQuery(id+"F0.imprint","IMPRINT",EDGE,{"derivedFrom":sQuery(id+"F0.wireOp",EDGE,"E25.0.7.6")}),1.0]])]});
            var Q434;
            Q434=makeQuery(id+"F0.imprint","IMPRINT",FACE,{"disambiguationData":[TD([[makeQuery(id+"F0.imprint","IMPRINT",EDGE,{"derivedFrom":sQuery(id+"F0.wireOp",EDGE,"E25.0.7.20")}),1.0]])]});
            var Q435;
            {var subQ0=sQuery(id+"F0.wireOp",EDGE,"E25.0.7.19");Q435=makeQuery(id+"F0.imprint","IMPRINT",FACE,{"disambiguationData":[TD([[makeQuery(id+"F0.imprint","IMPRINT",EDGE,{"derivedFrom":subQ0}),1.0]])]});}
            var Q436;
            Q436=makeQuery(id+"F0.imprint","IMPRINT",FACE,{"disambiguationData":[TD([[makeQuery(id+"F0.imprint","IMPRINT",EDGE,{"derivedFrom":sQuery(id+"F0.wireOp",EDGE,"E25.0.6.81")}),-1.0]])]});
            var Q437;
            Q437=makeQuery(id+"F0.imprint","IMPRINT",FACE,{"disambiguationData":[TD([[makeQuery(id+"F0.imprint","IMPRINT",EDGE,{"derivedFrom":sQuery(id+"F0.wireOp",EDGE,"E25.0.7.81")}),-1.0]])]});
            extrude(context, id + "F4", {"entities" : qUnion([Q0, Q1, Q2, Q3, Q4, Q5, Q6, Q7, Q8, Q9, Q10, Q11, Q12, Q13, Q14, Q15, Q16, Q17, Q18, Q19, Q20, Q21, Q22, Q23, Q24, Q25, Q26, Q27, Q28, Q29, Q30, Q31, Q32, Q33, Q34, Q35, Q36, Q37, Q38, Q39, Q40, Q41, Q42, Q43, Q44, Q45, Q46, Q47, Q48, Q49, Q50, Q51, Q52, Q53, Q54, Q55, Q56, Q57, Q58, Q59, Q60, Q61, Q62, Q63, Q64, Q65, Q66, Q67, Q68, Q69, Q70, Q71, Q72, Q73, Q74, Q75, Q76, Q77, Q78, Q79, Q80, Q81, Q82, Q83, Q84, Q85, Q86, Q87, Q88, Q89, Q90, Q91, Q92, Q93, Q94, Q95, Q96, Q97, Q98, Q99, Q100, Q101, Q102, Q103, Q104, Q105, Q106, Q107, Q108, Q109, Q110, Q111, Q112, Q113, Q114, Q115, Q116, Q117, Q118, Q119, Q120, Q121, Q122, Q123, Q124, Q125, Q126, Q127, Q128, Q129, Q130, Q131, Q132, Q133, Q134, Q135, Q136, Q137, Q138, Q139, Q140, Q141, Q142, Q143, Q144, Q145, Q146, Q147, Q148, Q149, Q150, Q151, Q152, Q153, Q154, Q155, Q156, Q157, Q158, Q159, Q160, Q161, Q162, Q163, Q164, Q165, Q166, Q167, Q168, Q169, Q170, Q171, Q172, Q173, Q174, Q175, Q176, Q177, Q178, Q179, Q180, Q181, Q182, Q183, Q184, Q185, Q186, Q187, Q188, Q189, Q190, Q191, Q192, Q193, Q194, Q195, Q196, Q197, Q198, Q199, Q200, Q201, Q202, Q203, Q204, Q205, Q206, Q207, Q208, Q209, Q210, Q211, Q212, Q213, Q214, Q215, Q216, Q217, Q218, Q219, Q220, Q221, Q222, Q223, Q224, Q225, Q226, Q227, Q228, Q229, Q230, Q231, Q232, Q233, Q234, Q235, Q236, Q237, Q238, Q239, Q240, Q241, Q242, Q243, Q244, Q245, Q246, Q247, Q248, Q249, Q250, Q251, Q252, Q253, Q254, Q255, Q256, Q257, Q258, Q259, Q260, Q261, Q262, Q263, Q264, Q265, Q266, Q267, Q268, Q269, Q270, Q271, Q272, Q273, Q274, Q275, Q276, Q277, Q278, Q279, Q280, Q281, Q282, Q283, Q284, Q285, Q286, Q287, Q288, Q289, Q290, Q291, Q292, Q293, Q294, Q295, Q296, Q297, Q298, Q299, Q300, Q301, Q302, Q303, Q304, Q305, Q306, Q307, Q308, Q309, Q310, Q311, Q312, Q313, Q314, Q315, Q316, Q317, Q318, Q319, Q320, Q321, Q322, Q323, Q324, Q325, Q326, Q327, Q328, Q329, Q330, Q331, Q332, Q333, Q334, Q335, Q336, Q337, Q338, Q339, Q340, Q341, Q342, Q343, Q344, Q345, Q346, Q347, Q348, Q349, Q350, Q351, Q352, Q353, Q354, Q355, Q356, Q357, Q358, Q359, Q360, Q361, Q362, Q363, Q364, Q365, Q366, Q367, Q368, Q369, Q370, Q371, Q372, Q373, Q374, Q375, Q376, Q377, Q378, Q379, Q380, Q381, Q382, Q383, Q384, Q385, Q386, Q387, Q388, Q389, Q390, Q391, Q392, Q393, Q394, Q395, Q396, Q397, Q398, Q399, Q400, Q401, Q402, Q403, Q404, Q405, Q406, Q407, Q408, Q409, Q410, Q411, Q412, Q413, Q414, Q415, Q416, Q417, Q418, Q419, Q420, Q421, Q422, Q423, Q424, Q425, Q426, Q427, Q428, Q429, Q430, Q431, Q432, Q433, Q434, Q435, Q436, Q437]), "depth" : 30 * mm});
        }
        {
            var Q0;
            Q0=makeQuery(id+"F2.opExtrude","CAP_FACE",FACE,{"disambiguationData":[OSD([sQuery(id+"F1.wireOp",EDGE,"E199"),sQuery(id+"F1.wireOp",EDGE,"E200"),sQuery(id+"F1.wireOp",EDGE,"E201"),sQuery(id+"F1.wireOp",EDGE,"E202")])],"isStart":true});
            var sketch = newSketch(context, id + "F5", { "sketchPlane" : qUnion([Q0])});
            skArc(sketch, "E203", {"start": v(-62.57, 24) * mm, "mid": v(4.16, 17.14) * mm, "end": v(70.88, 24.02) * mm});
            skLineSegment(sketch, "E204", {"start": v(-62.8, 13.8) * mm, "end": v(-62.8, 12.8) * mm});
            skLineSegment(sketch, "E205", {"start": v(70.88, 14.02) * mm, "end": v(70.88, 13.02) * mm});
            skArc(sketch, "E206", {"start": v(-62.8, 12.8) * mm, "mid": v(4.05, 6.09) * mm, "end": v(70.88, 13.02) * mm});
            skLineSegment(sketch, "E207", {"start": v(-62.8, 12.8) * mm, "end": v(-62.8, 0) * mm});
            skLineSegment(sketch, "E208", {"start": v(-62.8, 0) * mm, "end": v(70.88, 0) * mm});
            skLineSegment(sketch, "E209", {"start": v(70.88, 0) * mm, "end": v(70.88, 13.02) * mm});
            skLineSegment(sketch, "E210", {"start": v(-62.8, 0) * mm, "end": v(-63.27, 0) * mm});
            skLineSegment(sketch, "E211", {"start": v(-63.27, 0) * mm, "end": v(-63.27, 30.1) * mm});
            skLineSegment(sketch, "E212", {"start": v(-63.27, 30.1) * mm, "end": v(70.88, 30.1) * mm});
            skLineSegment(sketch, "E213", {"start": v(70.88, 30.1) * mm, "end": v(70.88, 24.02) * mm});
            skSolve(sketch);
        }
        {
            var Q0;
            Q0=makeQuery(id+"F5.imprint","IMPRINT",FACE,{"disambiguationData":[TD([[makeQuery(id+"F5.imprint","IMPRINT",EDGE,{"derivedFrom":sQuery(id+"F5.wireOp",EDGE,"E206")}),-1.0]])]});
            var Q1;
            Q1=makeQuery(id+"F5.imprint","IMPRINT",FACE,{"disambiguationData":[TD([[makeQuery(id+"F5.imprint","IMPRINT",EDGE,{"derivedFrom":sQuery(id+"F5.wireOp",EDGE,"E204")}),-1.0]])]});
            extrude(context, id + "F6", {"entities" : qUnion([Q0, Q1]), "operationType" : NewBodyOperationType.REMOVE, "oppositeDirection" : true, "depth" : 50 * mm});
        }
    });
